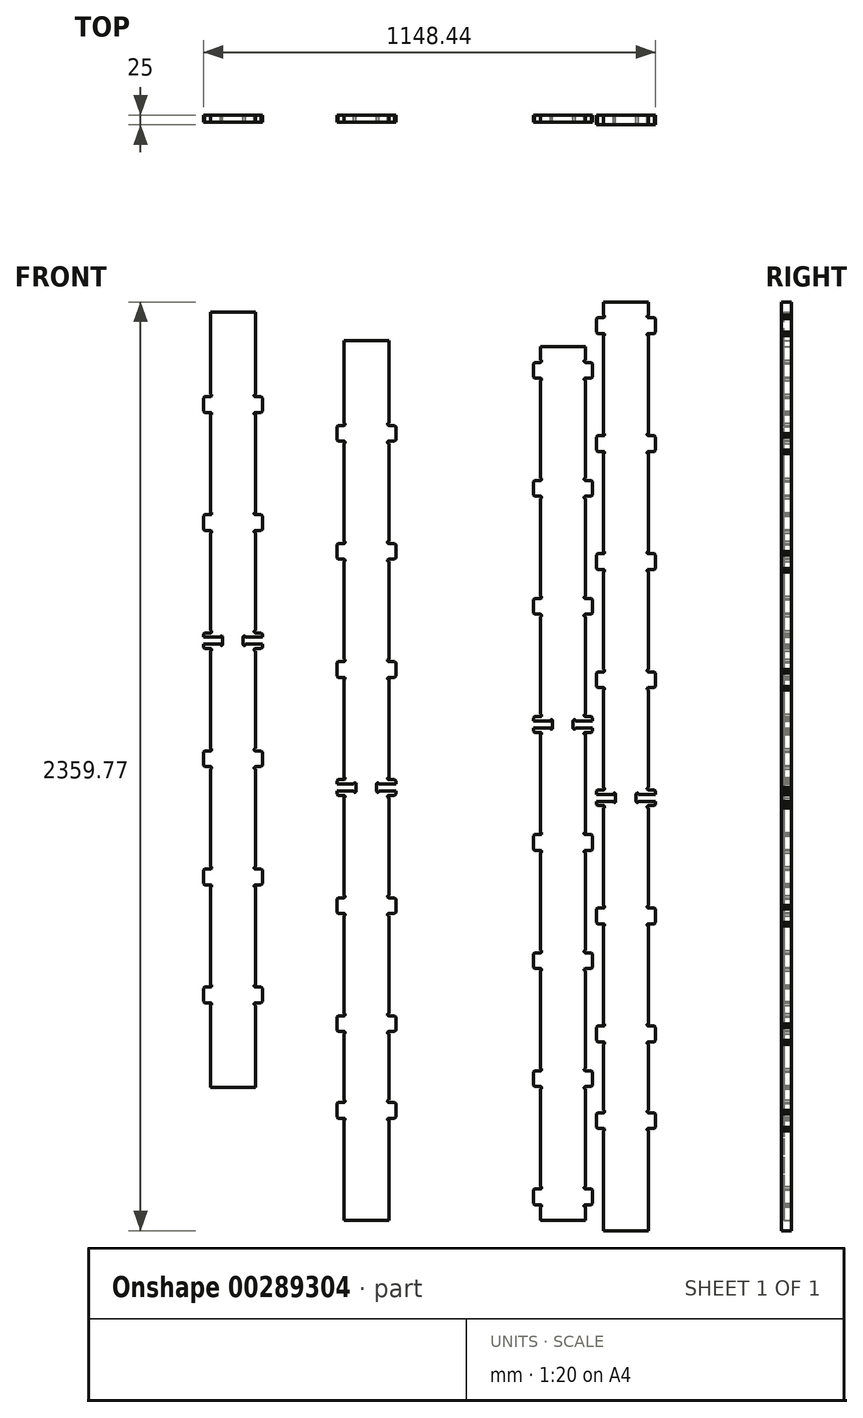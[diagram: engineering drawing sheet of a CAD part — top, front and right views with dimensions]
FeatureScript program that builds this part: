
annotation { "Feature Type Name" : "Feature", "Feature Type Description" : "" }
export const myFeature = defineFeature(function(context is Context, id is Id, definition is map)
    precondition{}
    {
        {
            var Q0;
            Q0=qCreatedBy(makeId("Front.planeOp"),FACE);
            var sketch = newSketch(context, id + "F0", { "sketchPlane" : qUnion([Q0])});
            skLineSegment(sketch, "E0", {"start": v(-600, -1200) * mm, "end": v(600, -1200) * mm});
            skLineSegment(sketch, "E1", {"start": v(600, -1200) * mm, "end": v(600, 1200) * mm});
            skLineSegment(sketch, "E2", {"start": v(600, 1200) * mm, "end": v(-600, 1200) * mm});
            skLineSegment(sketch, "E3", {"start": v(-600, 1200) * mm, "end": v(-600, -1200) * mm});
            skLineSegment(sketch, "E4", {"start": v(-87.48, 570.87) * mm, "end": v(-102.48, 570.87) * mm});
            skArc(sketch, "E5", {"start": v(-102.48, 570.87) * mm, "mid": v(-105.5, 573.88) * mm, "end": v(-102.48, 576.89) * mm});
            skLineSegment(sketch, "E6", {"start": v(-102.48, 576.89) * mm, "end": v(-102.48, 824.85) * mm});
            skArc(sketch, "E7", {"start": v(-102.48, 824.85) * mm, "mid": v(-105.5, 827.86) * mm, "end": v(-102.48, 830.87) * mm});
            skLineSegment(sketch, "E8", {"start": v(-102.48, 830.87) * mm, "end": v(-87.48, 830.87) * mm});
            skLineSegment(sketch, "E9", {"start": v(-87.48, 830.87) * mm, "end": v(-84.48, 833.87) * mm});
            skLineSegment(sketch, "E10", {"start": v(-84.48, 833.87) * mm, "end": v(-84.48, 867.87) * mm});
            skLineSegment(sketch, "E11", {"start": v(-84.48, 867.87) * mm, "end": v(-87.48, 870.87) * mm});
            skLineSegment(sketch, "E12", {"start": v(-87.48, 870.87) * mm, "end": v(-102.48, 870.87) * mm});
            skArc(sketch, "E13", {"start": v(-102.48, 870.87) * mm, "mid": v(-105.5, 873.88) * mm, "end": v(-102.48, 876.89) * mm});
            skLineSegment(sketch, "E14", {"start": v(-102.48, 876.89) * mm, "end": v(-102.48, 1085.87) * mm});
            skLineSegment(sketch, "E15", {"start": v(-102.48, 1085.87) * mm, "end": v(-216.48, 1085.87) * mm});
            skLineSegment(sketch, "E16", {"start": v(-216.48, 1085.87) * mm, "end": v(-216.48, 876.89) * mm});
            skArc(sketch, "E17", {"start": v(-216.48, 876.89) * mm, "mid": v(-213.47, 873.88) * mm, "end": v(-216.48, 870.87) * mm});
            skLineSegment(sketch, "E18", {"start": v(-216.48, 870.87) * mm, "end": v(-231.48, 870.87) * mm});
            skLineSegment(sketch, "E19", {"start": v(-231.48, 870.87) * mm, "end": v(-234.48, 867.87) * mm});
            skLineSegment(sketch, "E20", {"start": v(-234.48, 867.87) * mm, "end": v(-234.48, 833.87) * mm});
            skLineSegment(sketch, "E21", {"start": v(-234.48, 833.87) * mm, "end": v(-231.48, 830.87) * mm});
            skLineSegment(sketch, "E22", {"start": v(-231.48, 830.87) * mm, "end": v(-216.48, 830.87) * mm});
            skArc(sketch, "E23", {"start": v(-216.48, 830.87) * mm, "mid": v(-213.47, 827.86) * mm, "end": v(-216.48, 824.85) * mm});
            skLineSegment(sketch, "E24", {"start": v(-216.48, 824.85) * mm, "end": v(-216.48, 576.89) * mm});
            skArc(sketch, "E25", {"start": v(-216.48, 576.89) * mm, "mid": v(-213.47, 573.88) * mm, "end": v(-216.48, 570.87) * mm});
            skLineSegment(sketch, "E26", {"start": v(-216.48, 570.87) * mm, "end": v(-231.48, 570.87) * mm});
            skLineSegment(sketch, "E27", {"start": v(-231.48, 570.87) * mm, "end": v(-234.48, 567.87) * mm});
            skLineSegment(sketch, "E28", {"start": v(-234.48, 567.87) * mm, "end": v(-234.48, 533.87) * mm});
            skLineSegment(sketch, "E29", {"start": v(-234.48, 533.87) * mm, "end": v(-231.48, 530.87) * mm});
            skLineSegment(sketch, "E30", {"start": v(-231.48, 530.87) * mm, "end": v(-216.48, 530.87) * mm});
            skArc(sketch, "E31", {"start": v(-216.48, 530.87) * mm, "mid": v(-213.47, 527.86) * mm, "end": v(-216.48, 524.85) * mm});
            skLineSegment(sketch, "E32", {"start": v(-216.48, 524.85) * mm, "end": v(-216.48, 276.89) * mm});
            skArc(sketch, "E33", {"start": v(-216.48, 276.89) * mm, "mid": v(-213.47, 273.88) * mm, "end": v(-216.48, 270.87) * mm});
            skLineSegment(sketch, "E34", {"start": v(-216.48, 270.87) * mm, "end": v(-231.48, 270.87) * mm});
            skLineSegment(sketch, "E35", {"start": v(-231.48, 270.87) * mm, "end": v(-234.48, 267.87) * mm});
            skLineSegment(sketch, "E36", {"start": v(-234.48, 267.87) * mm, "end": v(-234.48, 233.87) * mm});
            skLineSegment(sketch, "E37", {"start": v(-234.48, 233.87) * mm, "end": v(-231.48, 230.87) * mm});
            skLineSegment(sketch, "E38", {"start": v(-231.48, 230.87) * mm, "end": v(-216.48, 230.87) * mm});
            skArc(sketch, "E39", {"start": v(-216.48, 230.87) * mm, "mid": v(-213.47, 227.86) * mm, "end": v(-216.48, 224.85) * mm});
            skLineSegment(sketch, "E40", {"start": v(-216.48, 224.85) * mm, "end": v(-216.48, -23.12) * mm});
            skArc(sketch, "E41", {"start": v(-216.48, -23.12) * mm, "mid": v(-213.47, -26.13) * mm, "end": v(-216.48, -29.14) * mm});
            skLineSegment(sketch, "E42", {"start": v(-216.48, -29.14) * mm, "end": v(-231.48, -29.14) * mm});
            skLineSegment(sketch, "E43", {"start": v(-231.48, -29.14) * mm, "end": v(-234.48, -32.14) * mm});
            skLineSegment(sketch, "E44", {"start": v(-234.48, -32.14) * mm, "end": v(-234.48, -40.14) * mm});
            skLineSegment(sketch, "E45", {"start": v(-234.48, -40.14) * mm, "end": v(-191.5, -40.14) * mm});
            skArc(sketch, "E46", {"start": v(-191.5, -40.14) * mm, "mid": v(-188.5, -37.13) * mm, "end": v(-185.48, -40.14) * mm});
            skLineSegment(sketch, "E47", {"start": v(-185.48, -40.14) * mm, "end": v(-185.48, -58.14) * mm});
            skArc(sketch, "E48", {"start": v(-185.48, -58.14) * mm, "mid": v(-188.5, -61.15) * mm, "end": v(-191.5, -58.14) * mm});
            skLineSegment(sketch, "E49", {"start": v(-191.5, -58.14) * mm, "end": v(-234.48, -58.14) * mm});
            skLineSegment(sketch, "E50", {"start": v(-234.48, -58.14) * mm, "end": v(-234.48, -66.14) * mm});
            skLineSegment(sketch, "E51", {"start": v(-234.48, -66.14) * mm, "end": v(-231.48, -69.14) * mm});
            skLineSegment(sketch, "E52", {"start": v(-231.48, -69.14) * mm, "end": v(-216.48, -69.14) * mm});
            skArc(sketch, "E53", {"start": v(-216.48, -69.14) * mm, "mid": v(-213.47, -72.15) * mm, "end": v(-216.48, -75.16) * mm});
            skLineSegment(sketch, "E54", {"start": v(-216.48, -75.16) * mm, "end": v(-216.48, -323.11) * mm});
            skArc(sketch, "E55", {"start": v(-216.48, -323.11) * mm, "mid": v(-213.47, -326.12) * mm, "end": v(-216.48, -329.13) * mm});
            skLineSegment(sketch, "E56", {"start": v(-216.48, -329.13) * mm, "end": v(-231.48, -329.13) * mm});
            skLineSegment(sketch, "E57", {"start": v(-231.48, -329.13) * mm, "end": v(-234.48, -332.13) * mm});
            skLineSegment(sketch, "E58", {"start": v(-234.48, -332.13) * mm, "end": v(-234.48, -366.13) * mm});
            skLineSegment(sketch, "E59", {"start": v(-234.48, -366.13) * mm, "end": v(-231.48, -369.13) * mm});
            skLineSegment(sketch, "E60", {"start": v(-231.48, -369.13) * mm, "end": v(-216.48, -369.13) * mm});
            skArc(sketch, "E61", {"start": v(-216.48, -369.13) * mm, "mid": v(-213.47, -372.14) * mm, "end": v(-216.48, -375.15) * mm});
            skLineSegment(sketch, "E62", {"start": v(-216.48, -375.15) * mm, "end": v(-216.48, -623.11) * mm});
            skArc(sketch, "E63", {"start": v(-216.48, -623.11) * mm, "mid": v(-213.47, -626.12) * mm, "end": v(-216.48, -629.13) * mm});
            skLineSegment(sketch, "E64", {"start": v(-216.48, -629.13) * mm, "end": v(-231.48, -629.13) * mm});
            skLineSegment(sketch, "E65", {"start": v(-231.48, -629.13) * mm, "end": v(-234.48, -632.13) * mm});
            skLineSegment(sketch, "E66", {"start": v(-234.48, -632.13) * mm, "end": v(-234.48, -666.13) * mm});
            skLineSegment(sketch, "E67", {"start": v(-234.48, -666.13) * mm, "end": v(-231.48, -669.13) * mm});
            skLineSegment(sketch, "E68", {"start": v(-231.48, -669.13) * mm, "end": v(-216.48, -669.13) * mm});
            skArc(sketch, "E69", {"start": v(-216.48, -669.13) * mm, "mid": v(-213.47, -672.14) * mm, "end": v(-216.48, -675.15) * mm});
            skLineSegment(sketch, "E70", {"start": v(-216.48, -675.15) * mm, "end": v(-216.48, -843.11) * mm});
            skArc(sketch, "E71", {"start": v(-216.48, -843.11) * mm, "mid": v(-213.47, -846.12) * mm, "end": v(-216.48, -849.13) * mm});
            skLineSegment(sketch, "E72", {"start": v(-216.48, -849.13) * mm, "end": v(-231.48, -849.13) * mm});
            skLineSegment(sketch, "E73", {"start": v(-231.48, -849.13) * mm, "end": v(-234.48, -852.13) * mm});
            skLineSegment(sketch, "E74", {"start": v(-234.48, -852.13) * mm, "end": v(-234.48, -886.13) * mm});
            skLineSegment(sketch, "E75", {"start": v(-234.48, -886.13) * mm, "end": v(-231.48, -889.13) * mm});
            skLineSegment(sketch, "E76", {"start": v(-231.48, -889.13) * mm, "end": v(-216.48, -889.13) * mm});
            skArc(sketch, "E77", {"start": v(-216.48, -889.13) * mm, "mid": v(-213.47, -892.14) * mm, "end": v(-216.48, -895.15) * mm});
            skLineSegment(sketch, "E78", {"start": v(-216.48, -895.15) * mm, "end": v(-216.48, -1148.9) * mm});
            skLineSegment(sketch, "E79", {"start": v(-216.48, -1148.9) * mm, "end": v(-102.48, -1148.9) * mm});
            skLineSegment(sketch, "E80", {"start": v(-102.48, -1148.9) * mm, "end": v(-102.48, -895.15) * mm});
            skArc(sketch, "E81", {"start": v(-102.48, -895.15) * mm, "mid": v(-105.5, -892.14) * mm, "end": v(-102.48, -889.13) * mm});
            skLineSegment(sketch, "E82", {"start": v(-102.48, -889.13) * mm, "end": v(-87.48, -889.13) * mm});
            skLineSegment(sketch, "E83", {"start": v(-87.48, -889.13) * mm, "end": v(-84.48, -886.13) * mm});
            skLineSegment(sketch, "E84", {"start": v(-84.48, -886.13) * mm, "end": v(-84.48, -852.13) * mm});
            skLineSegment(sketch, "E85", {"start": v(-84.48, -852.13) * mm, "end": v(-87.48, -849.13) * mm});
            skLineSegment(sketch, "E86", {"start": v(-87.48, -849.13) * mm, "end": v(-102.48, -849.13) * mm});
            skArc(sketch, "E87", {"start": v(-102.48, -849.13) * mm, "mid": v(-105.5, -846.12) * mm, "end": v(-102.48, -843.11) * mm});
            skLineSegment(sketch, "E88", {"start": v(-102.48, -843.11) * mm, "end": v(-102.48, -675.15) * mm});
            skArc(sketch, "E89", {"start": v(-102.48, -675.15) * mm, "mid": v(-105.5, -672.14) * mm, "end": v(-102.48, -669.13) * mm});
            skLineSegment(sketch, "E90", {"start": v(-102.48, -669.13) * mm, "end": v(-87.48, -669.13) * mm});
            skLineSegment(sketch, "E91", {"start": v(-87.48, -669.13) * mm, "end": v(-84.48, -666.13) * mm});
            skLineSegment(sketch, "E92", {"start": v(-84.48, -666.13) * mm, "end": v(-84.48, -632.13) * mm});
            skLineSegment(sketch, "E93", {"start": v(-84.48, -632.13) * mm, "end": v(-87.48, -629.13) * mm});
            skLineSegment(sketch, "E94", {"start": v(-87.48, -629.13) * mm, "end": v(-102.48, -629.13) * mm});
            skArc(sketch, "E95", {"start": v(-102.48, -629.13) * mm, "mid": v(-105.5, -626.12) * mm, "end": v(-102.48, -623.11) * mm});
            skLineSegment(sketch, "E96", {"start": v(-102.48, -623.11) * mm, "end": v(-102.48, -375.15) * mm});
            skArc(sketch, "E97", {"start": v(-102.48, -375.15) * mm, "mid": v(-105.5, -372.14) * mm, "end": v(-102.48, -369.13) * mm});
            skLineSegment(sketch, "E98", {"start": v(-102.48, -369.13) * mm, "end": v(-87.48, -369.13) * mm});
            skLineSegment(sketch, "E99", {"start": v(-87.48, -369.13) * mm, "end": v(-84.48, -366.13) * mm});
            skLineSegment(sketch, "E100", {"start": v(-84.48, -366.13) * mm, "end": v(-84.48, -332.13) * mm});
            skLineSegment(sketch, "E101", {"start": v(-84.48, -332.13) * mm, "end": v(-87.48, -329.13) * mm});
            skLineSegment(sketch, "E102", {"start": v(-87.48, -329.13) * mm, "end": v(-102.48, -329.13) * mm});
            skArc(sketch, "E103", {"start": v(-102.48, -329.13) * mm, "mid": v(-105.5, -326.12) * mm, "end": v(-102.48, -323.11) * mm});
            skLineSegment(sketch, "E104", {"start": v(-102.48, -323.11) * mm, "end": v(-102.48, -75.16) * mm});
            skArc(sketch, "E105", {"start": v(-102.48, -75.16) * mm, "mid": v(-105.5, -72.15) * mm, "end": v(-102.48, -69.14) * mm});
            skLineSegment(sketch, "E106", {"start": v(-102.48, -69.14) * mm, "end": v(-87.48, -69.14) * mm});
            skLineSegment(sketch, "E107", {"start": v(-87.48, -69.14) * mm, "end": v(-84.48, -66.14) * mm});
            skLineSegment(sketch, "E108", {"start": v(-84.48, -66.14) * mm, "end": v(-84.48, -58.14) * mm});
            skLineSegment(sketch, "E109", {"start": v(-84.48, -58.14) * mm, "end": v(-127.46, -58.14) * mm});
            skArc(sketch, "E110", {"start": v(-127.46, -58.14) * mm, "mid": v(-130.47, -61.15) * mm, "end": v(-133.48, -58.14) * mm});
            skLineSegment(sketch, "E111", {"start": v(-133.48, -58.14) * mm, "end": v(-133.48, -40.14) * mm});
            skArc(sketch, "E112", {"start": v(-133.48, -40.14) * mm, "mid": v(-130.47, -37.13) * mm, "end": v(-127.46, -40.14) * mm});
            skLineSegment(sketch, "E113", {"start": v(-127.46, -40.14) * mm, "end": v(-84.48, -40.14) * mm});
            skLineSegment(sketch, "E114", {"start": v(-84.48, -40.14) * mm, "end": v(-84.48, -32.14) * mm});
            skLineSegment(sketch, "E115", {"start": v(-84.48, -32.14) * mm, "end": v(-87.48, -29.14) * mm});
            skLineSegment(sketch, "E116", {"start": v(-87.48, -29.14) * mm, "end": v(-102.48, -29.14) * mm});
            skArc(sketch, "E117", {"start": v(-102.48, -29.14) * mm, "mid": v(-105.5, -26.13) * mm, "end": v(-102.48, -23.12) * mm});
            skLineSegment(sketch, "E118", {"start": v(-102.48, -23.12) * mm, "end": v(-102.48, 224.85) * mm});
            skArc(sketch, "E119", {"start": v(-102.48, 224.85) * mm, "mid": v(-105.5, 227.86) * mm, "end": v(-102.48, 230.87) * mm});
            skLineSegment(sketch, "E120", {"start": v(-102.48, 230.87) * mm, "end": v(-87.48, 230.87) * mm});
            skLineSegment(sketch, "E121", {"start": v(-87.48, 230.87) * mm, "end": v(-84.48, 233.87) * mm});
            skLineSegment(sketch, "E122", {"start": v(-84.48, 233.87) * mm, "end": v(-84.48, 267.87) * mm});
            skLineSegment(sketch, "E123", {"start": v(-84.48, 267.87) * mm, "end": v(-87.48, 270.87) * mm});
            skLineSegment(sketch, "E124", {"start": v(-87.48, 270.87) * mm, "end": v(-102.48, 270.87) * mm});
            skArc(sketch, "E125", {"start": v(-102.48, 270.87) * mm, "mid": v(-105.5, 273.88) * mm, "end": v(-102.48, 276.89) * mm});
            skLineSegment(sketch, "E126", {"start": v(-102.48, 276.89) * mm, "end": v(-102.48, 524.85) * mm});
            skArc(sketch, "E127", {"start": v(-102.48, 524.85) * mm, "mid": v(-105.5, 527.86) * mm, "end": v(-102.48, 530.87) * mm});
            skLineSegment(sketch, "E128", {"start": v(-102.48, 530.87) * mm, "end": v(-87.48, 530.87) * mm});
            skLineSegment(sketch, "E129", {"start": v(-87.48, 530.87) * mm, "end": v(-84.48, 533.87) * mm});
            skLineSegment(sketch, "E130", {"start": v(-84.48, 533.87) * mm, "end": v(-84.48, 567.87) * mm});
            skLineSegment(sketch, "E131", {"start": v(-84.48, 567.87) * mm, "end": v(-87.48, 570.87) * mm});
            skLineSegment(sketch, "E132", {"start": v(74.02, 431.1) * mm, "end": v(59.02, 431.1) * mm});
            skArc(sketch, "E133", {"start": v(59.02, 431.1) * mm, "mid": v(56, 434.1) * mm, "end": v(59.02, 437.12) * mm});
            skLineSegment(sketch, "E134", {"start": v(59.02, 437.12) * mm, "end": v(59.02, 685.08) * mm});
            skArc(sketch, "E135", {"start": v(59.02, 685.08) * mm, "mid": v(56, 688.09) * mm, "end": v(59.02, 691.1) * mm});
            skLineSegment(sketch, "E136", {"start": v(59.02, 691.1) * mm, "end": v(74.02, 691.1) * mm});
            skLineSegment(sketch, "E137", {"start": v(74.02, 691.1) * mm, "end": v(77.02, 694.1) * mm});
            skLineSegment(sketch, "E138", {"start": v(77.02, 694.1) * mm, "end": v(77.02, 728.1) * mm});
            skLineSegment(sketch, "E139", {"start": v(77.02, 728.1) * mm, "end": v(74.02, 731.1) * mm});
            skLineSegment(sketch, "E140", {"start": v(74.02, 731.1) * mm, "end": v(59.02, 731.1) * mm});
            skArc(sketch, "E141", {"start": v(59.02, 731.1) * mm, "mid": v(56, 734.1) * mm, "end": v(59.02, 737.12) * mm});
            skLineSegment(sketch, "E142", {"start": v(59.02, 737.12) * mm, "end": v(59.02, 985.08) * mm});
            skArc(sketch, "E143", {"start": v(59.02, 985.08) * mm, "mid": v(56, 988.09) * mm, "end": v(59.02, 991.1) * mm});
            skLineSegment(sketch, "E144", {"start": v(59.02, 991.1) * mm, "end": v(74.02, 991.1) * mm});
            skLineSegment(sketch, "E145", {"start": v(74.02, 991.1) * mm, "end": v(77.02, 994.1) * mm});
            skLineSegment(sketch, "E146", {"start": v(77.02, 994.1) * mm, "end": v(77.02, 1028.1) * mm});
            skLineSegment(sketch, "E147", {"start": v(77.02, 1028.1) * mm, "end": v(74.02, 1031.1) * mm});
            skLineSegment(sketch, "E148", {"start": v(74.02, 1031.1) * mm, "end": v(59.02, 1031.1) * mm});
            skArc(sketch, "E149", {"start": v(59.02, 1031.1) * mm, "mid": v(56, 1034.1) * mm, "end": v(59.02, 1037.12) * mm});
            skLineSegment(sketch, "E150", {"start": v(59.02, 1037.12) * mm, "end": v(59.02, 1071.1) * mm});
            skLineSegment(sketch, "E151", {"start": v(59.02, 1071.1) * mm, "end": v(-54.98, 1071.1) * mm});
            skLineSegment(sketch, "E152", {"start": v(-54.98, 1071.1) * mm, "end": v(-54.98, 1037.12) * mm});
            skArc(sketch, "E153", {"start": v(-54.98, 1037.12) * mm, "mid": v(-51.97, 1034.1) * mm, "end": v(-54.98, 1031.1) * mm});
            skLineSegment(sketch, "E154", {"start": v(-54.98, 1031.1) * mm, "end": v(-69.98, 1031.1) * mm});
            skLineSegment(sketch, "E155", {"start": v(-69.98, 1031.1) * mm, "end": v(-72.98, 1028.1) * mm});
            skLineSegment(sketch, "E156", {"start": v(-72.98, 1028.1) * mm, "end": v(-72.98, 994.1) * mm});
            skLineSegment(sketch, "E157", {"start": v(-72.98, 994.1) * mm, "end": v(-69.98, 991.1) * mm});
            skLineSegment(sketch, "E158", {"start": v(-69.98, 991.1) * mm, "end": v(-54.98, 991.1) * mm});
            skArc(sketch, "E159", {"start": v(-54.98, 991.1) * mm, "mid": v(-51.97, 988.09) * mm, "end": v(-54.98, 985.08) * mm});
            skLineSegment(sketch, "E160", {"start": v(-54.98, 985.08) * mm, "end": v(-54.98, 737.12) * mm});
            skArc(sketch, "E161", {"start": v(-54.98, 737.12) * mm, "mid": v(-51.97, 734.1) * mm, "end": v(-54.98, 731.1) * mm});
            skLineSegment(sketch, "E162", {"start": v(-54.98, 731.1) * mm, "end": v(-69.98, 731.1) * mm});
            skLineSegment(sketch, "E163", {"start": v(-69.98, 731.1) * mm, "end": v(-72.98, 728.1) * mm});
            skLineSegment(sketch, "E164", {"start": v(-72.98, 728.1) * mm, "end": v(-72.98, 694.1) * mm});
            skLineSegment(sketch, "E165", {"start": v(-72.98, 694.1) * mm, "end": v(-69.98, 691.1) * mm});
            skLineSegment(sketch, "E166", {"start": v(-69.98, 691.1) * mm, "end": v(-54.98, 691.1) * mm});
            skArc(sketch, "E167", {"start": v(-54.98, 691.1) * mm, "mid": v(-51.97, 688.09) * mm, "end": v(-54.98, 685.08) * mm});
            skLineSegment(sketch, "E168", {"start": v(-54.98, 685.08) * mm, "end": v(-54.98, 437.12) * mm});
            skArc(sketch, "E169", {"start": v(-54.98, 437.12) * mm, "mid": v(-51.97, 434.1) * mm, "end": v(-54.98, 431.1) * mm});
            skLineSegment(sketch, "E170", {"start": v(-54.98, 431.1) * mm, "end": v(-69.98, 431.1) * mm});
            skLineSegment(sketch, "E171", {"start": v(-69.98, 431.1) * mm, "end": v(-72.98, 428.1) * mm});
            skLineSegment(sketch, "E172", {"start": v(-72.98, 428.1) * mm, "end": v(-72.98, 394.1) * mm});
            skLineSegment(sketch, "E173", {"start": v(-72.98, 394.1) * mm, "end": v(-69.98, 391.1) * mm});
            skLineSegment(sketch, "E174", {"start": v(-69.98, 391.1) * mm, "end": v(-54.98, 391.1) * mm});
            skArc(sketch, "E175", {"start": v(-54.98, 391.1) * mm, "mid": v(-51.97, 388.09) * mm, "end": v(-54.98, 385.08) * mm});
            skLineSegment(sketch, "E176", {"start": v(-54.98, 385.08) * mm, "end": v(-54.98, 137.12) * mm});
            skArc(sketch, "E177", {"start": v(-54.98, 137.12) * mm, "mid": v(-51.97, 134.1) * mm, "end": v(-54.98, 131.1) * mm});
            skLineSegment(sketch, "E178", {"start": v(-54.98, 131.1) * mm, "end": v(-69.98, 131.1) * mm});
            skLineSegment(sketch, "E179", {"start": v(-69.98, 131.1) * mm, "end": v(-72.98, 128.1) * mm});
            skLineSegment(sketch, "E180", {"start": v(-72.98, 128.1) * mm, "end": v(-72.98, 120.1) * mm});
            skLineSegment(sketch, "E181", {"start": v(-72.98, 120.1) * mm, "end": v(-30, 120.1) * mm});
            skArc(sketch, "E182", {"start": v(-30, 120.1) * mm, "mid": v(-27, 123.11) * mm, "end": v(-23.98, 120.1) * mm});
            skLineSegment(sketch, "E183", {"start": v(-23.98, 120.1) * mm, "end": v(-23.98, 102.1) * mm});
            skArc(sketch, "E184", {"start": v(-23.98, 102.1) * mm, "mid": v(-27, 99.09) * mm, "end": v(-30, 102.1) * mm});
            skLineSegment(sketch, "E185", {"start": v(-30, 102.1) * mm, "end": v(-72.98, 102.1) * mm});
            skLineSegment(sketch, "E186", {"start": v(-72.98, 102.1) * mm, "end": v(-72.98, 94.1) * mm});
            skLineSegment(sketch, "E187", {"start": v(-72.98, 94.1) * mm, "end": v(-69.98, 91.1) * mm});
            skLineSegment(sketch, "E188", {"start": v(-69.98, 91.1) * mm, "end": v(-54.98, 91.1) * mm});
            skArc(sketch, "E189", {"start": v(-54.98, 91.1) * mm, "mid": v(-51.97, 88.09) * mm, "end": v(-54.98, 85.08) * mm});
            skLineSegment(sketch, "E190", {"start": v(-54.98, 85.08) * mm, "end": v(-54.98, -162.88) * mm});
            skArc(sketch, "E191", {"start": v(-54.98, -162.88) * mm, "mid": v(-51.97, -165.9) * mm, "end": v(-54.98, -168.9) * mm});
            skLineSegment(sketch, "E192", {"start": v(-54.98, -168.9) * mm, "end": v(-69.98, -168.9) * mm});
            skLineSegment(sketch, "E193", {"start": v(-69.98, -168.9) * mm, "end": v(-72.98, -171.9) * mm});
            skLineSegment(sketch, "E194", {"start": v(-72.98, -171.9) * mm, "end": v(-72.98, -205.9) * mm});
            skLineSegment(sketch, "E195", {"start": v(-72.98, -205.9) * mm, "end": v(-69.98, -208.9) * mm});
            skLineSegment(sketch, "E196", {"start": v(-69.98, -208.9) * mm, "end": v(-54.98, -208.9) * mm});
            skArc(sketch, "E197", {"start": v(-54.98, -208.9) * mm, "mid": v(-51.97, -211.91) * mm, "end": v(-54.98, -214.92) * mm});
            skLineSegment(sketch, "E198", {"start": v(-54.98, -214.92) * mm, "end": v(-54.98, -462.88) * mm});
            skArc(sketch, "E199", {"start": v(-54.98, -462.88) * mm, "mid": v(-51.97, -465.9) * mm, "end": v(-54.98, -468.9) * mm});
            skLineSegment(sketch, "E200", {"start": v(-54.98, -468.9) * mm, "end": v(-69.98, -468.9) * mm});
            skLineSegment(sketch, "E201", {"start": v(-69.98, -468.9) * mm, "end": v(-72.98, -471.9) * mm});
            skLineSegment(sketch, "E202", {"start": v(-72.98, -471.9) * mm, "end": v(-72.98, -505.9) * mm});
            skLineSegment(sketch, "E203", {"start": v(-72.98, -505.9) * mm, "end": v(-69.98, -508.9) * mm});
            skLineSegment(sketch, "E204", {"start": v(-69.98, -508.9) * mm, "end": v(-54.98, -508.9) * mm});
            skArc(sketch, "E205", {"start": v(-54.98, -508.9) * mm, "mid": v(-51.97, -511.91) * mm, "end": v(-54.98, -514.92) * mm});
            skLineSegment(sketch, "E206", {"start": v(-54.98, -514.92) * mm, "end": v(-54.98, -762.88) * mm});
            skArc(sketch, "E207", {"start": v(-54.98, -762.88) * mm, "mid": v(-51.97, -765.9) * mm, "end": v(-54.98, -768.9) * mm});
            skLineSegment(sketch, "E208", {"start": v(-54.98, -768.9) * mm, "end": v(-69.98, -768.9) * mm});
            skLineSegment(sketch, "E209", {"start": v(-69.98, -768.9) * mm, "end": v(-72.98, -771.9) * mm});
            skLineSegment(sketch, "E210", {"start": v(-72.98, -771.9) * mm, "end": v(-72.98, -805.9) * mm});
            skLineSegment(sketch, "E211", {"start": v(-72.98, -805.9) * mm, "end": v(-69.98, -808.9) * mm});
            skLineSegment(sketch, "E212", {"start": v(-69.98, -808.9) * mm, "end": v(-54.98, -808.9) * mm});
            skArc(sketch, "E213", {"start": v(-54.98, -808.9) * mm, "mid": v(-51.97, -811.91) * mm, "end": v(-54.98, -814.92) * mm});
            skLineSegment(sketch, "E214", {"start": v(-54.98, -814.92) * mm, "end": v(-54.98, -1062.88) * mm});
            skArc(sketch, "E215", {"start": v(-54.98, -1062.88) * mm, "mid": v(-51.97, -1065.9) * mm, "end": v(-54.98, -1068.9) * mm});
            skLineSegment(sketch, "E216", {"start": v(-54.98, -1068.9) * mm, "end": v(-69.98, -1068.9) * mm});
            skLineSegment(sketch, "E217", {"start": v(-69.98, -1068.9) * mm, "end": v(-72.98, -1071.9) * mm});
            skLineSegment(sketch, "E218", {"start": v(-72.98, -1071.9) * mm, "end": v(-72.98, -1105.9) * mm});
            skLineSegment(sketch, "E219", {"start": v(-72.98, -1105.9) * mm, "end": v(-69.98, -1108.9) * mm});
            skLineSegment(sketch, "E220", {"start": v(-69.98, -1108.9) * mm, "end": v(-54.98, -1108.9) * mm});
            skArc(sketch, "E221", {"start": v(-54.98, -1108.9) * mm, "mid": v(-51.97, -1111.91) * mm, "end": v(-54.98, -1114.92) * mm});
            skLineSegment(sketch, "E222", {"start": v(-54.98, -1114.92) * mm, "end": v(-54.98, -1148.9) * mm});
            skLineSegment(sketch, "E223", {"start": v(-54.98, -1148.9) * mm, "end": v(59.02, -1148.9) * mm});
            skLineSegment(sketch, "E224", {"start": v(59.02, -1148.9) * mm, "end": v(59.02, -1114.92) * mm});
            skArc(sketch, "E225", {"start": v(59.02, -1114.92) * mm, "mid": v(56, -1111.91) * mm, "end": v(59.02, -1108.9) * mm});
            skLineSegment(sketch, "E226", {"start": v(59.02, -1108.9) * mm, "end": v(74.02, -1108.9) * mm});
            skLineSegment(sketch, "E227", {"start": v(74.02, -1108.9) * mm, "end": v(77.02, -1105.9) * mm});
            skLineSegment(sketch, "E228", {"start": v(77.02, -1105.9) * mm, "end": v(77.02, -1071.9) * mm});
            skLineSegment(sketch, "E229", {"start": v(77.02, -1071.9) * mm, "end": v(74.02, -1068.9) * mm});
            skLineSegment(sketch, "E230", {"start": v(74.02, -1068.9) * mm, "end": v(59.02, -1068.9) * mm});
            skArc(sketch, "E231", {"start": v(59.02, -1068.9) * mm, "mid": v(56, -1065.9) * mm, "end": v(59.02, -1062.88) * mm});
            skLineSegment(sketch, "E232", {"start": v(59.02, -1062.88) * mm, "end": v(59.02, -814.92) * mm});
            skArc(sketch, "E233", {"start": v(59.02, -814.92) * mm, "mid": v(56, -811.91) * mm, "end": v(59.02, -808.9) * mm});
            skLineSegment(sketch, "E234", {"start": v(59.02, -808.9) * mm, "end": v(74.02, -808.9) * mm});
            skLineSegment(sketch, "E235", {"start": v(74.02, -808.9) * mm, "end": v(77.02, -805.9) * mm});
            skLineSegment(sketch, "E236", {"start": v(77.02, -805.9) * mm, "end": v(77.02, -771.9) * mm});
            skLineSegment(sketch, "E237", {"start": v(77.02, -771.9) * mm, "end": v(74.02, -768.9) * mm});
            skLineSegment(sketch, "E238", {"start": v(74.02, -768.9) * mm, "end": v(59.02, -768.9) * mm});
            skArc(sketch, "E239", {"start": v(59.02, -768.9) * mm, "mid": v(56, -765.9) * mm, "end": v(59.02, -762.88) * mm});
            skLineSegment(sketch, "E240", {"start": v(59.02, -762.88) * mm, "end": v(59.02, -514.92) * mm});
            skArc(sketch, "E241", {"start": v(59.02, -514.92) * mm, "mid": v(56, -511.91) * mm, "end": v(59.02, -508.9) * mm});
            skLineSegment(sketch, "E242", {"start": v(59.02, -508.9) * mm, "end": v(74.02, -508.9) * mm});
            skLineSegment(sketch, "E243", {"start": v(74.02, -508.9) * mm, "end": v(77.02, -505.9) * mm});
            skLineSegment(sketch, "E244", {"start": v(77.02, -505.9) * mm, "end": v(77.02, -471.9) * mm});
            skLineSegment(sketch, "E245", {"start": v(77.02, -471.9) * mm, "end": v(74.02, -468.9) * mm});
            skLineSegment(sketch, "E246", {"start": v(74.02, -468.9) * mm, "end": v(59.02, -468.9) * mm});
            skArc(sketch, "E247", {"start": v(59.02, -468.9) * mm, "mid": v(56, -465.9) * mm, "end": v(59.02, -462.88) * mm});
            skLineSegment(sketch, "E248", {"start": v(59.02, -462.88) * mm, "end": v(59.02, -214.92) * mm});
            skArc(sketch, "E249", {"start": v(59.02, -214.92) * mm, "mid": v(56, -211.91) * mm, "end": v(59.02, -208.9) * mm});
            skLineSegment(sketch, "E250", {"start": v(59.02, -208.9) * mm, "end": v(74.02, -208.9) * mm});
            skLineSegment(sketch, "E251", {"start": v(74.02, -208.9) * mm, "end": v(77.02, -205.9) * mm});
            skLineSegment(sketch, "E252", {"start": v(77.02, -205.9) * mm, "end": v(77.02, -171.9) * mm});
            skLineSegment(sketch, "E253", {"start": v(77.02, -171.9) * mm, "end": v(74.02, -168.9) * mm});
            skLineSegment(sketch, "E254", {"start": v(74.02, -168.9) * mm, "end": v(59.02, -168.9) * mm});
            skArc(sketch, "E255", {"start": v(59.02, -168.9) * mm, "mid": v(56, -165.9) * mm, "end": v(59.02, -162.88) * mm});
            skLineSegment(sketch, "E256", {"start": v(59.02, -162.88) * mm, "end": v(59.02, 85.08) * mm});
            skArc(sketch, "E257", {"start": v(59.02, 85.08) * mm, "mid": v(56, 88.09) * mm, "end": v(59.02, 91.1) * mm});
            skLineSegment(sketch, "E258", {"start": v(59.02, 91.1) * mm, "end": v(74.02, 91.1) * mm});
            skLineSegment(sketch, "E259", {"start": v(74.02, 91.1) * mm, "end": v(77.02, 94.1) * mm});
            skLineSegment(sketch, "E260", {"start": v(77.02, 94.1) * mm, "end": v(77.02, 102.1) * mm});
            skLineSegment(sketch, "E261", {"start": v(77.02, 102.1) * mm, "end": v(34.04, 102.1) * mm});
            skArc(sketch, "E262", {"start": v(34.04, 102.1) * mm, "mid": v(31.03, 99.1) * mm, "end": v(28.02, 102.1) * mm});
            skLineSegment(sketch, "E263", {"start": v(28.02, 102.1) * mm, "end": v(28.02, 120.1) * mm});
            skArc(sketch, "E264", {"start": v(28.02, 120.1) * mm, "mid": v(31.03, 123.11) * mm, "end": v(34.04, 120.1) * mm});
            skLineSegment(sketch, "E265", {"start": v(34.04, 120.1) * mm, "end": v(77.02, 120.1) * mm});
            skLineSegment(sketch, "E266", {"start": v(77.02, 120.1) * mm, "end": v(77.02, 128.1) * mm});
            skLineSegment(sketch, "E267", {"start": v(77.02, 128.1) * mm, "end": v(74.02, 131.1) * mm});
            skLineSegment(sketch, "E268", {"start": v(74.02, 131.1) * mm, "end": v(59.02, 131.1) * mm});
            skArc(sketch, "E269", {"start": v(59.02, 131.1) * mm, "mid": v(56, 134.1) * mm, "end": v(59.02, 137.12) * mm});
            skLineSegment(sketch, "E270", {"start": v(59.02, 137.12) * mm, "end": v(59.02, 385.08) * mm});
            skArc(sketch, "E271", {"start": v(59.02, 385.08) * mm, "mid": v(56, 388.09) * mm, "end": v(59.02, 391.1) * mm});
            skLineSegment(sketch, "E272", {"start": v(59.02, 391.1) * mm, "end": v(74.02, 391.1) * mm});
            skLineSegment(sketch, "E273", {"start": v(74.02, 391.1) * mm, "end": v(77.02, 394.1) * mm});
            skLineSegment(sketch, "E274", {"start": v(77.02, 394.1) * mm, "end": v(77.02, 428.1) * mm});
            skLineSegment(sketch, "E275", {"start": v(77.02, 428.1) * mm, "end": v(74.02, 431.1) * mm});
            skLineSegment(sketch, "E276", {"start": v(247.4, 570.87) * mm, "end": v(232.4, 570.87) * mm});
            skArc(sketch, "E277", {"start": v(232.4, 570.87) * mm, "mid": v(229.4, 573.88) * mm, "end": v(232.4, 576.89) * mm});
            skLineSegment(sketch, "E278", {"start": v(232.4, 576.89) * mm, "end": v(232.4, 824.85) * mm});
            skArc(sketch, "E279", {"start": v(232.4, 824.85) * mm, "mid": v(229.4, 827.86) * mm, "end": v(232.4, 830.87) * mm});
            skLineSegment(sketch, "E280", {"start": v(232.4, 830.87) * mm, "end": v(247.4, 830.87) * mm});
            skLineSegment(sketch, "E281", {"start": v(247.4, 830.87) * mm, "end": v(250.4, 833.87) * mm});
            skLineSegment(sketch, "E282", {"start": v(250.4, 833.87) * mm, "end": v(250.4, 867.87) * mm});
            skLineSegment(sketch, "E283", {"start": v(250.4, 867.87) * mm, "end": v(247.4, 870.87) * mm});
            skLineSegment(sketch, "E284", {"start": v(247.4, 870.87) * mm, "end": v(232.4, 870.87) * mm});
            skArc(sketch, "E285", {"start": v(232.4, 870.87) * mm, "mid": v(229.4, 873.88) * mm, "end": v(232.4, 876.89) * mm});
            skLineSegment(sketch, "E286", {"start": v(232.4, 876.89) * mm, "end": v(232.4, 1085.87) * mm});
            skLineSegment(sketch, "E287", {"start": v(232.4, 1085.87) * mm, "end": v(118.4, 1085.87) * mm});
            skLineSegment(sketch, "E288", {"start": v(118.4, 1085.87) * mm, "end": v(118.4, 876.89) * mm});
            skArc(sketch, "E289", {"start": v(118.4, 876.89) * mm, "mid": v(121.41, 873.88) * mm, "end": v(118.4, 870.87) * mm});
            skLineSegment(sketch, "E290", {"start": v(118.4, 870.87) * mm, "end": v(103.4, 870.87) * mm});
            skLineSegment(sketch, "E291", {"start": v(103.4, 870.87) * mm, "end": v(100.4, 867.87) * mm});
            skLineSegment(sketch, "E292", {"start": v(100.4, 867.87) * mm, "end": v(100.4, 833.87) * mm});
            skLineSegment(sketch, "E293", {"start": v(100.4, 833.87) * mm, "end": v(103.4, 830.87) * mm});
            skLineSegment(sketch, "E294", {"start": v(103.4, 830.87) * mm, "end": v(118.4, 830.87) * mm});
            skArc(sketch, "E295", {"start": v(118.4, 830.87) * mm, "mid": v(121.41, 827.86) * mm, "end": v(118.4, 824.85) * mm});
            skLineSegment(sketch, "E296", {"start": v(118.4, 824.85) * mm, "end": v(118.4, 576.89) * mm});
            skArc(sketch, "E297", {"start": v(118.4, 576.89) * mm, "mid": v(121.41, 573.88) * mm, "end": v(118.4, 570.87) * mm});
            skLineSegment(sketch, "E298", {"start": v(118.4, 570.87) * mm, "end": v(103.4, 570.87) * mm});
            skLineSegment(sketch, "E299", {"start": v(103.4, 570.87) * mm, "end": v(100.4, 567.87) * mm});
            skLineSegment(sketch, "E300", {"start": v(100.4, 567.87) * mm, "end": v(100.4, 533.87) * mm});
            skLineSegment(sketch, "E301", {"start": v(100.4, 533.87) * mm, "end": v(103.4, 530.87) * mm});
            skLineSegment(sketch, "E302", {"start": v(103.4, 530.87) * mm, "end": v(118.4, 530.87) * mm});
            skArc(sketch, "E303", {"start": v(118.4, 530.87) * mm, "mid": v(121.41, 527.86) * mm, "end": v(118.4, 524.85) * mm});
            skLineSegment(sketch, "E304", {"start": v(118.4, 524.85) * mm, "end": v(118.4, 276.89) * mm});
            skArc(sketch, "E305", {"start": v(118.4, 276.89) * mm, "mid": v(121.41, 273.88) * mm, "end": v(118.4, 270.87) * mm});
            skLineSegment(sketch, "E306", {"start": v(118.4, 270.87) * mm, "end": v(103.4, 270.87) * mm});
            skLineSegment(sketch, "E307", {"start": v(103.4, 270.87) * mm, "end": v(100.4, 267.87) * mm});
            skLineSegment(sketch, "E308", {"start": v(100.4, 267.87) * mm, "end": v(100.4, 233.87) * mm});
            skLineSegment(sketch, "E309", {"start": v(100.4, 233.87) * mm, "end": v(103.4, 230.87) * mm});
            skLineSegment(sketch, "E310", {"start": v(103.4, 230.87) * mm, "end": v(118.4, 230.87) * mm});
            skArc(sketch, "E311", {"start": v(118.4, 230.87) * mm, "mid": v(121.41, 227.86) * mm, "end": v(118.4, 224.85) * mm});
            skLineSegment(sketch, "E312", {"start": v(118.4, 224.85) * mm, "end": v(118.4, -23.12) * mm});
            skArc(sketch, "E313", {"start": v(118.4, -23.12) * mm, "mid": v(121.41, -26.13) * mm, "end": v(118.4, -29.14) * mm});
            skLineSegment(sketch, "E314", {"start": v(118.4, -29.14) * mm, "end": v(103.4, -29.14) * mm});
            skLineSegment(sketch, "E315", {"start": v(103.4, -29.14) * mm, "end": v(100.4, -32.14) * mm});
            skLineSegment(sketch, "E316", {"start": v(100.4, -32.14) * mm, "end": v(100.4, -40.14) * mm});
            skLineSegment(sketch, "E317", {"start": v(100.4, -40.14) * mm, "end": v(143.38, -40.14) * mm});
            skArc(sketch, "E318", {"start": v(143.38, -40.14) * mm, "mid": v(146.39, -37.13) * mm, "end": v(149.4, -40.14) * mm});
            skLineSegment(sketch, "E319", {"start": v(149.4, -40.14) * mm, "end": v(149.4, -58.14) * mm});
            skArc(sketch, "E320", {"start": v(149.4, -58.14) * mm, "mid": v(146.39, -61.15) * mm, "end": v(143.38, -58.14) * mm});
            skLineSegment(sketch, "E321", {"start": v(143.38, -58.14) * mm, "end": v(100.4, -58.14) * mm});
            skLineSegment(sketch, "E322", {"start": v(100.4, -58.14) * mm, "end": v(100.4, -66.14) * mm});
            skLineSegment(sketch, "E323", {"start": v(100.4, -66.14) * mm, "end": v(103.4, -69.14) * mm});
            skLineSegment(sketch, "E324", {"start": v(103.4, -69.14) * mm, "end": v(118.4, -69.14) * mm});
            skArc(sketch, "E325", {"start": v(118.4, -69.14) * mm, "mid": v(121.41, -72.15) * mm, "end": v(118.4, -75.16) * mm});
            skLineSegment(sketch, "E326", {"start": v(118.4, -75.16) * mm, "end": v(118.4, -323.11) * mm});
            skArc(sketch, "E327", {"start": v(118.4, -323.11) * mm, "mid": v(121.41, -326.12) * mm, "end": v(118.4, -329.13) * mm});
            skLineSegment(sketch, "E328", {"start": v(118.4, -329.13) * mm, "end": v(103.4, -329.13) * mm});
            skLineSegment(sketch, "E329", {"start": v(103.4, -329.13) * mm, "end": v(100.4, -332.13) * mm});
            skLineSegment(sketch, "E330", {"start": v(100.4, -332.13) * mm, "end": v(100.4, -366.13) * mm});
            skLineSegment(sketch, "E331", {"start": v(100.4, -366.13) * mm, "end": v(103.4, -369.13) * mm});
            skLineSegment(sketch, "E332", {"start": v(103.4, -369.13) * mm, "end": v(118.4, -369.13) * mm});
            skArc(sketch, "E333", {"start": v(118.4, -369.13) * mm, "mid": v(121.41, -372.14) * mm, "end": v(118.4, -375.15) * mm});
            skLineSegment(sketch, "E334", {"start": v(118.4, -375.15) * mm, "end": v(118.4, -623.11) * mm});
            skArc(sketch, "E335", {"start": v(118.4, -623.11) * mm, "mid": v(121.41, -626.12) * mm, "end": v(118.4, -629.13) * mm});
            skLineSegment(sketch, "E336", {"start": v(118.4, -629.13) * mm, "end": v(103.4, -629.13) * mm});
            skLineSegment(sketch, "E337", {"start": v(103.4, -629.13) * mm, "end": v(100.4, -632.13) * mm});
            skLineSegment(sketch, "E338", {"start": v(100.4, -632.13) * mm, "end": v(100.4, -666.13) * mm});
            skLineSegment(sketch, "E339", {"start": v(100.4, -666.13) * mm, "end": v(103.4, -669.13) * mm});
            skLineSegment(sketch, "E340", {"start": v(103.4, -669.13) * mm, "end": v(118.4, -669.13) * mm});
            skArc(sketch, "E341", {"start": v(118.4, -669.13) * mm, "mid": v(121.41, -672.14) * mm, "end": v(118.4, -675.15) * mm});
            skLineSegment(sketch, "E342", {"start": v(118.4, -675.15) * mm, "end": v(118.4, -843.11) * mm});
            skArc(sketch, "E343", {"start": v(118.4, -843.11) * mm, "mid": v(121.4, -846.12) * mm, "end": v(118.4, -849.13) * mm});
            skLineSegment(sketch, "E344", {"start": v(118.4, -849.13) * mm, "end": v(103.4, -849.13) * mm});
            skLineSegment(sketch, "E345", {"start": v(103.4, -849.13) * mm, "end": v(100.4, -852.13) * mm});
            skLineSegment(sketch, "E346", {"start": v(100.4, -852.13) * mm, "end": v(100.4, -886.13) * mm});
            skLineSegment(sketch, "E347", {"start": v(100.4, -886.13) * mm, "end": v(103.4, -889.13) * mm});
            skLineSegment(sketch, "E348", {"start": v(103.4, -889.13) * mm, "end": v(118.4, -889.13) * mm});
            skArc(sketch, "E349", {"start": v(118.4, -889.13) * mm, "mid": v(121.4, -892.14) * mm, "end": v(118.4, -895.15) * mm});
            skLineSegment(sketch, "E350", {"start": v(118.4, -895.15) * mm, "end": v(118.4, -1148.9) * mm});
            skLineSegment(sketch, "E351", {"start": v(118.4, -1148.9) * mm, "end": v(232.4, -1148.9) * mm});
            skLineSegment(sketch, "E352", {"start": v(232.4, -1148.9) * mm, "end": v(232.4, -895.15) * mm});
            skArc(sketch, "E353", {"start": v(232.4, -895.15) * mm, "mid": v(229.4, -892.14) * mm, "end": v(232.4, -889.13) * mm});
            skLineSegment(sketch, "E354", {"start": v(232.4, -889.13) * mm, "end": v(247.4, -889.13) * mm});
            skLineSegment(sketch, "E355", {"start": v(247.4, -889.13) * mm, "end": v(250.4, -886.13) * mm});
            skLineSegment(sketch, "E356", {"start": v(250.4, -886.13) * mm, "end": v(250.4, -852.13) * mm});
            skLineSegment(sketch, "E357", {"start": v(250.4, -852.13) * mm, "end": v(247.4, -849.13) * mm});
            skLineSegment(sketch, "E358", {"start": v(247.4, -849.13) * mm, "end": v(232.4, -849.13) * mm});
            skArc(sketch, "E359", {"start": v(232.4, -849.13) * mm, "mid": v(229.4, -846.12) * mm, "end": v(232.4, -843.11) * mm});
            skLineSegment(sketch, "E360", {"start": v(232.4, -843.11) * mm, "end": v(232.4, -675.15) * mm});
            skArc(sketch, "E361", {"start": v(232.4, -675.15) * mm, "mid": v(229.4, -672.14) * mm, "end": v(232.4, -669.13) * mm});
            skLineSegment(sketch, "E362", {"start": v(232.4, -669.13) * mm, "end": v(247.4, -669.13) * mm});
            skLineSegment(sketch, "E363", {"start": v(247.4, -669.13) * mm, "end": v(250.4, -666.13) * mm});
            skLineSegment(sketch, "E364", {"start": v(250.4, -666.13) * mm, "end": v(250.4, -632.13) * mm});
            skLineSegment(sketch, "E365", {"start": v(250.4, -632.13) * mm, "end": v(247.4, -629.13) * mm});
            skLineSegment(sketch, "E366", {"start": v(247.4, -629.13) * mm, "end": v(232.4, -629.13) * mm});
            skArc(sketch, "E367", {"start": v(232.4, -629.13) * mm, "mid": v(229.4, -626.12) * mm, "end": v(232.4, -623.11) * mm});
            skLineSegment(sketch, "E368", {"start": v(232.4, -623.11) * mm, "end": v(232.4, -375.15) * mm});
            skArc(sketch, "E369", {"start": v(232.4, -375.15) * mm, "mid": v(229.4, -372.14) * mm, "end": v(232.4, -369.13) * mm});
            skLineSegment(sketch, "E370", {"start": v(232.4, -369.13) * mm, "end": v(247.4, -369.13) * mm});
            skLineSegment(sketch, "E371", {"start": v(247.4, -369.13) * mm, "end": v(250.4, -366.13) * mm});
            skLineSegment(sketch, "E372", {"start": v(250.4, -366.13) * mm, "end": v(250.4, -332.13) * mm});
            skLineSegment(sketch, "E373", {"start": v(250.4, -332.13) * mm, "end": v(247.4, -329.13) * mm});
            skLineSegment(sketch, "E374", {"start": v(247.4, -329.13) * mm, "end": v(232.4, -329.13) * mm});
            skArc(sketch, "E375", {"start": v(232.4, -329.13) * mm, "mid": v(229.4, -326.12) * mm, "end": v(232.4, -323.11) * mm});
            skLineSegment(sketch, "E376", {"start": v(232.4, -323.11) * mm, "end": v(232.4, -75.16) * mm});
            skArc(sketch, "E377", {"start": v(232.4, -75.16) * mm, "mid": v(229.4, -72.15) * mm, "end": v(232.4, -69.14) * mm});
            skLineSegment(sketch, "E378", {"start": v(232.4, -69.14) * mm, "end": v(247.4, -69.14) * mm});
            skLineSegment(sketch, "E379", {"start": v(247.4, -69.14) * mm, "end": v(250.4, -66.14) * mm});
            skLineSegment(sketch, "E380", {"start": v(250.4, -66.14) * mm, "end": v(250.4, -58.14) * mm});
            skLineSegment(sketch, "E381", {"start": v(250.4, -58.14) * mm, "end": v(207.42, -58.14) * mm});
            skArc(sketch, "E382", {"start": v(207.42, -58.14) * mm, "mid": v(204.4, -61.15) * mm, "end": v(201.4, -58.14) * mm});
            skLineSegment(sketch, "E383", {"start": v(201.4, -58.14) * mm, "end": v(201.4, -40.14) * mm});
            skArc(sketch, "E384", {"start": v(201.4, -40.14) * mm, "mid": v(204.4, -37.13) * mm, "end": v(207.42, -40.14) * mm});
            skLineSegment(sketch, "E385", {"start": v(207.42, -40.14) * mm, "end": v(250.4, -40.14) * mm});
            skLineSegment(sketch, "E386", {"start": v(250.4, -40.14) * mm, "end": v(250.4, -32.14) * mm});
            skLineSegment(sketch, "E387", {"start": v(250.4, -32.14) * mm, "end": v(247.4, -29.14) * mm});
            skLineSegment(sketch, "E388", {"start": v(247.4, -29.14) * mm, "end": v(232.4, -29.14) * mm});
            skArc(sketch, "E389", {"start": v(232.4, -29.14) * mm, "mid": v(229.4, -26.13) * mm, "end": v(232.4, -23.12) * mm});
            skLineSegment(sketch, "E390", {"start": v(232.4, -23.12) * mm, "end": v(232.4, 224.85) * mm});
            skArc(sketch, "E391", {"start": v(232.4, 224.85) * mm, "mid": v(229.4, 227.86) * mm, "end": v(232.4, 230.87) * mm});
            skLineSegment(sketch, "E392", {"start": v(232.4, 230.87) * mm, "end": v(247.4, 230.87) * mm});
            skLineSegment(sketch, "E393", {"start": v(247.4, 230.87) * mm, "end": v(250.4, 233.87) * mm});
            skLineSegment(sketch, "E394", {"start": v(250.4, 233.87) * mm, "end": v(250.4, 267.87) * mm});
            skLineSegment(sketch, "E395", {"start": v(250.4, 267.87) * mm, "end": v(247.4, 270.87) * mm});
            skLineSegment(sketch, "E396", {"start": v(247.4, 270.87) * mm, "end": v(232.4, 270.87) * mm});
            skArc(sketch, "E397", {"start": v(232.4, 270.87) * mm, "mid": v(229.4, 273.88) * mm, "end": v(232.4, 276.89) * mm});
            skLineSegment(sketch, "E398", {"start": v(232.4, 276.89) * mm, "end": v(232.4, 524.85) * mm});
            skArc(sketch, "E399", {"start": v(232.4, 524.85) * mm, "mid": v(229.4, 527.86) * mm, "end": v(232.4, 530.87) * mm});
            skLineSegment(sketch, "E400", {"start": v(232.4, 530.87) * mm, "end": v(247.4, 530.87) * mm});
            skLineSegment(sketch, "E401", {"start": v(247.4, 530.87) * mm, "end": v(250.4, 533.87) * mm});
            skLineSegment(sketch, "E402", {"start": v(250.4, 533.87) * mm, "end": v(250.4, 567.87) * mm});
            skLineSegment(sketch, "E403", {"start": v(250.4, 567.87) * mm, "end": v(247.4, 570.87) * mm});
            skLineSegment(sketch, "E404", {"start": v(411.9, 431.1) * mm, "end": v(396.9, 431.1) * mm});
            skArc(sketch, "E405", {"start": v(396.9, 431.1) * mm, "mid": v(393.9, 434.1) * mm, "end": v(396.9, 437.12) * mm});
            skLineSegment(sketch, "E406", {"start": v(396.9, 437.12) * mm, "end": v(396.9, 685.08) * mm});
            skArc(sketch, "E407", {"start": v(396.9, 685.08) * mm, "mid": v(393.9, 688.09) * mm, "end": v(396.9, 691.1) * mm});
            skLineSegment(sketch, "E408", {"start": v(396.9, 691.1) * mm, "end": v(411.9, 691.1) * mm});
            skLineSegment(sketch, "E409", {"start": v(411.9, 691.1) * mm, "end": v(414.9, 694.1) * mm});
            skLineSegment(sketch, "E410", {"start": v(414.9, 694.1) * mm, "end": v(414.9, 728.1) * mm});
            skLineSegment(sketch, "E411", {"start": v(414.9, 728.1) * mm, "end": v(411.9, 731.1) * mm});
            skLineSegment(sketch, "E412", {"start": v(411.9, 731.1) * mm, "end": v(396.9, 731.1) * mm});
            skArc(sketch, "E413", {"start": v(396.9, 731.1) * mm, "mid": v(393.9, 734.1) * mm, "end": v(396.9, 737.12) * mm});
            skLineSegment(sketch, "E414", {"start": v(396.9, 737.12) * mm, "end": v(396.9, 985.08) * mm});
            skArc(sketch, "E415", {"start": v(396.9, 985.08) * mm, "mid": v(393.9, 988.09) * mm, "end": v(396.9, 991.1) * mm});
            skLineSegment(sketch, "E416", {"start": v(396.9, 991.1) * mm, "end": v(411.9, 991.1) * mm});
            skLineSegment(sketch, "E417", {"start": v(411.9, 991.1) * mm, "end": v(414.9, 994.1) * mm});
            skLineSegment(sketch, "E418", {"start": v(414.9, 994.1) * mm, "end": v(414.9, 1028.1) * mm});
            skLineSegment(sketch, "E419", {"start": v(414.9, 1028.1) * mm, "end": v(411.9, 1031.1) * mm});
            skLineSegment(sketch, "E420", {"start": v(411.9, 1031.1) * mm, "end": v(396.9, 1031.1) * mm});
            skArc(sketch, "E421", {"start": v(396.9, 1031.1) * mm, "mid": v(393.9, 1034.1) * mm, "end": v(396.9, 1037.12) * mm});
            skLineSegment(sketch, "E422", {"start": v(396.9, 1037.12) * mm, "end": v(396.9, 1071.1) * mm});
            skLineSegment(sketch, "E423", {"start": v(396.9, 1071.1) * mm, "end": v(282.9, 1071.1) * mm});
            skLineSegment(sketch, "E424", {"start": v(282.9, 1071.1) * mm, "end": v(282.9, 1037.12) * mm});
            skArc(sketch, "E425", {"start": v(282.9, 1037.12) * mm, "mid": v(285.91, 1034.1) * mm, "end": v(282.9, 1031.1) * mm});
            skLineSegment(sketch, "E426", {"start": v(282.9, 1031.1) * mm, "end": v(267.9, 1031.1) * mm});
            skLineSegment(sketch, "E427", {"start": v(267.9, 1031.1) * mm, "end": v(264.9, 1028.1) * mm});
            skLineSegment(sketch, "E428", {"start": v(264.9, 1028.1) * mm, "end": v(264.9, 994.1) * mm});
            skLineSegment(sketch, "E429", {"start": v(264.9, 994.1) * mm, "end": v(267.9, 991.1) * mm});
            skLineSegment(sketch, "E430", {"start": v(267.9, 991.1) * mm, "end": v(282.9, 991.1) * mm});
            skArc(sketch, "E431", {"start": v(282.9, 991.1) * mm, "mid": v(285.91, 988.09) * mm, "end": v(282.9, 985.08) * mm});
            skLineSegment(sketch, "E432", {"start": v(282.9, 985.08) * mm, "end": v(282.9, 737.12) * mm});
            skArc(sketch, "E433", {"start": v(282.9, 737.12) * mm, "mid": v(285.91, 734.1) * mm, "end": v(282.9, 731.1) * mm});
            skLineSegment(sketch, "E434", {"start": v(282.9, 731.1) * mm, "end": v(267.9, 731.1) * mm});
            skLineSegment(sketch, "E435", {"start": v(267.9, 731.1) * mm, "end": v(264.9, 728.1) * mm});
            skLineSegment(sketch, "E436", {"start": v(264.9, 728.1) * mm, "end": v(264.9, 694.1) * mm});
            skLineSegment(sketch, "E437", {"start": v(264.9, 694.1) * mm, "end": v(267.9, 691.1) * mm});
            skLineSegment(sketch, "E438", {"start": v(267.9, 691.1) * mm, "end": v(282.9, 691.1) * mm});
            skArc(sketch, "E439", {"start": v(282.9, 691.1) * mm, "mid": v(285.91, 688.09) * mm, "end": v(282.9, 685.08) * mm});
            skLineSegment(sketch, "E440", {"start": v(282.9, 685.08) * mm, "end": v(282.9, 437.12) * mm});
            skArc(sketch, "E441", {"start": v(282.9, 437.12) * mm, "mid": v(285.91, 434.1) * mm, "end": v(282.9, 431.1) * mm});
            skLineSegment(sketch, "E442", {"start": v(282.9, 431.1) * mm, "end": v(267.9, 431.1) * mm});
            skLineSegment(sketch, "E443", {"start": v(267.9, 431.1) * mm, "end": v(264.9, 428.1) * mm});
            skLineSegment(sketch, "E444", {"start": v(264.9, 428.1) * mm, "end": v(264.9, 394.1) * mm});
            skLineSegment(sketch, "E445", {"start": v(264.9, 394.1) * mm, "end": v(267.9, 391.1) * mm});
            skLineSegment(sketch, "E446", {"start": v(267.9, 391.1) * mm, "end": v(282.9, 391.1) * mm});
            skArc(sketch, "E447", {"start": v(282.9, 391.1) * mm, "mid": v(285.91, 388.09) * mm, "end": v(282.9, 385.08) * mm});
            skLineSegment(sketch, "E448", {"start": v(282.9, 385.08) * mm, "end": v(282.9, 137.12) * mm});
            skArc(sketch, "E449", {"start": v(282.9, 137.12) * mm, "mid": v(285.91, 134.1) * mm, "end": v(282.9, 131.1) * mm});
            skLineSegment(sketch, "E450", {"start": v(282.9, 131.1) * mm, "end": v(267.9, 131.1) * mm});
            skLineSegment(sketch, "E451", {"start": v(267.9, 131.1) * mm, "end": v(264.9, 128.1) * mm});
            skLineSegment(sketch, "E452", {"start": v(264.9, 128.1) * mm, "end": v(264.9, 120.1) * mm});
            skLineSegment(sketch, "E453", {"start": v(264.9, 120.1) * mm, "end": v(307.88, 120.1) * mm});
            skArc(sketch, "E454", {"start": v(307.88, 120.1) * mm, "mid": v(310.89, 123.11) * mm, "end": v(313.9, 120.1) * mm});
            skLineSegment(sketch, "E455", {"start": v(313.9, 120.1) * mm, "end": v(313.9, 102.1) * mm});
            skArc(sketch, "E456", {"start": v(313.9, 102.1) * mm, "mid": v(310.89, 99.09) * mm, "end": v(307.88, 102.1) * mm});
            skLineSegment(sketch, "E457", {"start": v(307.88, 102.1) * mm, "end": v(264.9, 102.1) * mm});
            skLineSegment(sketch, "E458", {"start": v(264.9, 102.1) * mm, "end": v(264.9, 94.1) * mm});
            skLineSegment(sketch, "E459", {"start": v(264.9, 94.1) * mm, "end": v(267.9, 91.1) * mm});
            skLineSegment(sketch, "E460", {"start": v(267.9, 91.1) * mm, "end": v(282.9, 91.1) * mm});
            skArc(sketch, "E461", {"start": v(282.9, 91.1) * mm, "mid": v(285.91, 88.09) * mm, "end": v(282.9, 85.08) * mm});
            skLineSegment(sketch, "E462", {"start": v(282.9, 85.08) * mm, "end": v(282.9, -162.88) * mm});
            skArc(sketch, "E463", {"start": v(282.9, -162.88) * mm, "mid": v(285.91, -165.9) * mm, "end": v(282.9, -168.9) * mm});
            skLineSegment(sketch, "E464", {"start": v(282.9, -168.9) * mm, "end": v(267.9, -168.9) * mm});
            skLineSegment(sketch, "E465", {"start": v(267.9, -168.9) * mm, "end": v(264.9, -171.9) * mm});
            skLineSegment(sketch, "E466", {"start": v(264.9, -171.9) * mm, "end": v(264.9, -205.9) * mm});
            skLineSegment(sketch, "E467", {"start": v(264.9, -205.9) * mm, "end": v(267.9, -208.9) * mm});
            skLineSegment(sketch, "E468", {"start": v(267.9, -208.9) * mm, "end": v(282.9, -208.9) * mm});
            skArc(sketch, "E469", {"start": v(282.9, -208.9) * mm, "mid": v(285.91, -211.91) * mm, "end": v(282.9, -214.92) * mm});
            skLineSegment(sketch, "E470", {"start": v(282.9, -214.92) * mm, "end": v(282.9, -462.88) * mm});
            skArc(sketch, "E471", {"start": v(282.9, -462.88) * mm, "mid": v(285.91, -465.9) * mm, "end": v(282.9, -468.9) * mm});
            skLineSegment(sketch, "E472", {"start": v(282.9, -468.9) * mm, "end": v(267.9, -468.9) * mm});
            skLineSegment(sketch, "E473", {"start": v(267.9, -468.9) * mm, "end": v(264.9, -471.9) * mm});
            skLineSegment(sketch, "E474", {"start": v(264.9, -471.9) * mm, "end": v(264.9, -505.9) * mm});
            skLineSegment(sketch, "E475", {"start": v(264.9, -505.9) * mm, "end": v(267.9, -508.9) * mm});
            skLineSegment(sketch, "E476", {"start": v(267.9, -508.9) * mm, "end": v(282.9, -508.9) * mm});
            skArc(sketch, "E477", {"start": v(282.9, -508.9) * mm, "mid": v(285.91, -511.91) * mm, "end": v(282.9, -514.92) * mm});
            skLineSegment(sketch, "E478", {"start": v(282.9, -514.92) * mm, "end": v(282.9, -762.88) * mm});
            skArc(sketch, "E479", {"start": v(282.9, -762.88) * mm, "mid": v(285.91, -765.9) * mm, "end": v(282.9, -768.9) * mm});
            skLineSegment(sketch, "E480", {"start": v(282.9, -768.9) * mm, "end": v(267.9, -768.9) * mm});
            skLineSegment(sketch, "E481", {"start": v(267.9, -768.9) * mm, "end": v(264.9, -771.9) * mm});
            skLineSegment(sketch, "E482", {"start": v(264.9, -771.9) * mm, "end": v(264.9, -805.9) * mm});
            skLineSegment(sketch, "E483", {"start": v(264.9, -805.9) * mm, "end": v(267.9, -808.9) * mm});
            skLineSegment(sketch, "E484", {"start": v(267.9, -808.9) * mm, "end": v(282.9, -808.9) * mm});
            skArc(sketch, "E485", {"start": v(282.9, -808.9) * mm, "mid": v(285.91, -811.91) * mm, "end": v(282.9, -814.92) * mm});
            skLineSegment(sketch, "E486", {"start": v(282.9, -814.92) * mm, "end": v(282.9, -1062.88) * mm});
            skArc(sketch, "E487", {"start": v(282.9, -1062.88) * mm, "mid": v(285.91, -1065.9) * mm, "end": v(282.9, -1068.9) * mm});
            skLineSegment(sketch, "E488", {"start": v(282.9, -1068.9) * mm, "end": v(267.9, -1068.9) * mm});
            skLineSegment(sketch, "E489", {"start": v(267.9, -1068.9) * mm, "end": v(264.9, -1071.9) * mm});
            skLineSegment(sketch, "E490", {"start": v(264.9, -1071.9) * mm, "end": v(264.9, -1105.9) * mm});
            skLineSegment(sketch, "E491", {"start": v(264.9, -1105.9) * mm, "end": v(267.9, -1108.9) * mm});
            skLineSegment(sketch, "E492", {"start": v(267.9, -1108.9) * mm, "end": v(282.9, -1108.9) * mm});
            skArc(sketch, "E493", {"start": v(282.9, -1108.9) * mm, "mid": v(285.91, -1111.91) * mm, "end": v(282.9, -1114.92) * mm});
            skLineSegment(sketch, "E494", {"start": v(282.9, -1114.92) * mm, "end": v(282.9, -1148.9) * mm});
            skLineSegment(sketch, "E495", {"start": v(282.9, -1148.9) * mm, "end": v(396.9, -1148.9) * mm});
            skLineSegment(sketch, "E496", {"start": v(396.9, -1148.9) * mm, "end": v(396.9, -1114.92) * mm});
            skArc(sketch, "E497", {"start": v(396.9, -1114.92) * mm, "mid": v(393.9, -1111.91) * mm, "end": v(396.9, -1108.9) * mm});
            skLineSegment(sketch, "E498", {"start": v(396.9, -1108.9) * mm, "end": v(411.9, -1108.9) * mm});
            skLineSegment(sketch, "E499", {"start": v(411.9, -1108.9) * mm, "end": v(414.9, -1105.9) * mm});
            skLineSegment(sketch, "E500", {"start": v(414.9, -1105.9) * mm, "end": v(414.9, -1071.9) * mm});
            skLineSegment(sketch, "E501", {"start": v(414.9, -1071.9) * mm, "end": v(411.9, -1068.9) * mm});
            skLineSegment(sketch, "E502", {"start": v(411.9, -1068.9) * mm, "end": v(396.9, -1068.9) * mm});
            skArc(sketch, "E503", {"start": v(396.9, -1068.9) * mm, "mid": v(393.9, -1065.9) * mm, "end": v(396.9, -1062.88) * mm});
            skLineSegment(sketch, "E504", {"start": v(396.9, -1062.88) * mm, "end": v(396.9, -814.92) * mm});
            skArc(sketch, "E505", {"start": v(396.9, -814.92) * mm, "mid": v(393.9, -811.91) * mm, "end": v(396.9, -808.9) * mm});
            skLineSegment(sketch, "E506", {"start": v(396.9, -808.9) * mm, "end": v(411.9, -808.9) * mm});
            skLineSegment(sketch, "E507", {"start": v(411.9, -808.9) * mm, "end": v(414.9, -805.9) * mm});
            skLineSegment(sketch, "E508", {"start": v(414.9, -805.9) * mm, "end": v(414.9, -771.9) * mm});
            skLineSegment(sketch, "E509", {"start": v(414.9, -771.9) * mm, "end": v(411.9, -768.9) * mm});
            skLineSegment(sketch, "E510", {"start": v(411.9, -768.9) * mm, "end": v(396.9, -768.9) * mm});
            skArc(sketch, "E511", {"start": v(396.9, -768.9) * mm, "mid": v(393.9, -765.9) * mm, "end": v(396.9, -762.88) * mm});
            skLineSegment(sketch, "E512", {"start": v(396.9, -762.88) * mm, "end": v(396.9, -514.92) * mm});
            skArc(sketch, "E513", {"start": v(396.9, -514.92) * mm, "mid": v(393.9, -511.91) * mm, "end": v(396.9, -508.9) * mm});
            skLineSegment(sketch, "E514", {"start": v(396.9, -508.9) * mm, "end": v(411.9, -508.9) * mm});
            skLineSegment(sketch, "E515", {"start": v(411.9, -508.9) * mm, "end": v(414.9, -505.9) * mm});
            skLineSegment(sketch, "E516", {"start": v(414.9, -505.9) * mm, "end": v(414.9, -471.9) * mm});
            skLineSegment(sketch, "E517", {"start": v(414.9, -471.9) * mm, "end": v(411.9, -468.9) * mm});
            skLineSegment(sketch, "E518", {"start": v(411.9, -468.9) * mm, "end": v(396.9, -468.9) * mm});
            skArc(sketch, "E519", {"start": v(396.9, -468.9) * mm, "mid": v(393.9, -465.9) * mm, "end": v(396.9, -462.88) * mm});
            skLineSegment(sketch, "E520", {"start": v(396.9, -462.88) * mm, "end": v(396.9, -214.92) * mm});
            skArc(sketch, "E521", {"start": v(396.9, -214.92) * mm, "mid": v(393.9, -211.91) * mm, "end": v(396.9, -208.9) * mm});
            skLineSegment(sketch, "E522", {"start": v(396.9, -208.9) * mm, "end": v(411.9, -208.9) * mm});
            skLineSegment(sketch, "E523", {"start": v(411.9, -208.9) * mm, "end": v(414.9, -205.9) * mm});
            skLineSegment(sketch, "E524", {"start": v(414.9, -205.9) * mm, "end": v(414.9, -171.9) * mm});
            skLineSegment(sketch, "E525", {"start": v(414.9, -171.9) * mm, "end": v(411.9, -168.9) * mm});
            skLineSegment(sketch, "E526", {"start": v(411.9, -168.9) * mm, "end": v(396.9, -168.9) * mm});
            skArc(sketch, "E527", {"start": v(396.9, -168.9) * mm, "mid": v(393.9, -165.9) * mm, "end": v(396.9, -162.88) * mm});
            skLineSegment(sketch, "E528", {"start": v(396.9, -162.88) * mm, "end": v(396.9, 85.08) * mm});
            skArc(sketch, "E529", {"start": v(396.9, 85.08) * mm, "mid": v(393.9, 88.09) * mm, "end": v(396.9, 91.1) * mm});
            skLineSegment(sketch, "E530", {"start": v(396.9, 91.1) * mm, "end": v(411.9, 91.1) * mm});
            skLineSegment(sketch, "E531", {"start": v(411.9, 91.1) * mm, "end": v(414.9, 94.1) * mm});
            skLineSegment(sketch, "E532", {"start": v(414.9, 94.1) * mm, "end": v(414.9, 102.1) * mm});
            skLineSegment(sketch, "E533", {"start": v(414.9, 102.1) * mm, "end": v(371.92, 102.1) * mm});
            skArc(sketch, "E534", {"start": v(371.92, 102.1) * mm, "mid": v(368.9, 99.1) * mm, "end": v(365.9, 102.1) * mm});
            skLineSegment(sketch, "E535", {"start": v(365.9, 102.1) * mm, "end": v(365.9, 120.1) * mm});
            skArc(sketch, "E536", {"start": v(365.9, 120.1) * mm, "mid": v(368.9, 123.11) * mm, "end": v(371.92, 120.1) * mm});
            skLineSegment(sketch, "E537", {"start": v(371.92, 120.1) * mm, "end": v(414.9, 120.1) * mm});
            skLineSegment(sketch, "E538", {"start": v(414.9, 120.1) * mm, "end": v(414.9, 128.1) * mm});
            skLineSegment(sketch, "E539", {"start": v(414.9, 128.1) * mm, "end": v(411.9, 131.1) * mm});
            skLineSegment(sketch, "E540", {"start": v(411.9, 131.1) * mm, "end": v(396.9, 131.1) * mm});
            skArc(sketch, "E541", {"start": v(396.9, 131.1) * mm, "mid": v(393.9, 134.1) * mm, "end": v(396.9, 137.12) * mm});
            skLineSegment(sketch, "E542", {"start": v(396.9, 137.12) * mm, "end": v(396.9, 385.08) * mm});
            skArc(sketch, "E543", {"start": v(396.9, 385.08) * mm, "mid": v(393.9, 388.09) * mm, "end": v(396.9, 391.1) * mm});
            skLineSegment(sketch, "E544", {"start": v(396.9, 391.1) * mm, "end": v(411.9, 391.1) * mm});
            skLineSegment(sketch, "E545", {"start": v(411.9, 391.1) * mm, "end": v(414.9, 394.1) * mm});
            skLineSegment(sketch, "E546", {"start": v(414.9, 394.1) * mm, "end": v(414.9, 428.1) * mm});
            skLineSegment(sketch, "E547", {"start": v(414.9, 428.1) * mm, "end": v(411.9, 431.1) * mm});
            skLineSegment(sketch, "E548", {"start": v(-246.2, 640.87) * mm, "end": v(-249.2, 643.87) * mm});
            skLineSegment(sketch, "E549", {"start": v(-249.2, 643.87) * mm, "end": v(-264.2, 643.87) * mm});
            skArc(sketch, "E550", {"start": v(-264.2, 643.87) * mm, "mid": v(-267.2, 646.88) * mm, "end": v(-264.2, 649.9) * mm});
            skLineSegment(sketch, "E551", {"start": v(-264.2, 649.9) * mm, "end": v(-264.2, 897.85) * mm});
            skArc(sketch, "E552", {"start": v(-264.2, 897.85) * mm, "mid": v(-267.2, 900.86) * mm, "end": v(-264.2, 903.87) * mm});
            skLineSegment(sketch, "E553", {"start": v(-264.2, 903.87) * mm, "end": v(-249.2, 903.87) * mm});
            skLineSegment(sketch, "E554", {"start": v(-249.2, 903.87) * mm, "end": v(-246.2, 906.87) * mm});
            skLineSegment(sketch, "E555", {"start": v(-246.2, 906.87) * mm, "end": v(-246.2, 940.87) * mm});
            skLineSegment(sketch, "E556", {"start": v(-246.2, 940.87) * mm, "end": v(-249.2, 943.87) * mm});
            skLineSegment(sketch, "E557", {"start": v(-249.2, 943.87) * mm, "end": v(-264.2, 943.87) * mm});
            skArc(sketch, "E558", {"start": v(-264.2, 943.87) * mm, "mid": v(-267.2, 946.88) * mm, "end": v(-264.2, 949.9) * mm});
            skLineSegment(sketch, "E559", {"start": v(-264.2, 949.9) * mm, "end": v(-264.2, 1158.87) * mm});
            skLineSegment(sketch, "E560", {"start": v(-264.2, 1158.87) * mm, "end": v(-378.2, 1158.87) * mm});
            skLineSegment(sketch, "E561", {"start": v(-378.2, 1158.87) * mm, "end": v(-378.2, 949.9) * mm});
            skArc(sketch, "E562", {"start": v(-378.2, 949.9) * mm, "mid": v(-375.19, 946.88) * mm, "end": v(-378.2, 943.87) * mm});
            skLineSegment(sketch, "E563", {"start": v(-378.2, 943.87) * mm, "end": v(-393.2, 943.87) * mm});
            skLineSegment(sketch, "E564", {"start": v(-393.2, 943.87) * mm, "end": v(-396.2, 940.87) * mm});
            skLineSegment(sketch, "E565", {"start": v(-396.2, 940.87) * mm, "end": v(-396.2, 906.87) * mm});
            skLineSegment(sketch, "E566", {"start": v(-396.2, 906.87) * mm, "end": v(-393.2, 903.87) * mm});
            skLineSegment(sketch, "E567", {"start": v(-393.2, 903.87) * mm, "end": v(-378.2, 903.87) * mm});
            skArc(sketch, "E568", {"start": v(-378.2, 903.87) * mm, "mid": v(-375.19, 900.86) * mm, "end": v(-378.2, 897.85) * mm});
            skLineSegment(sketch, "E569", {"start": v(-378.2, 897.85) * mm, "end": v(-378.2, 649.9) * mm});
            skArc(sketch, "E570", {"start": v(-378.2, 649.9) * mm, "mid": v(-375.19, 646.88) * mm, "end": v(-378.2, 643.87) * mm});
            skLineSegment(sketch, "E571", {"start": v(-378.2, 643.87) * mm, "end": v(-393.2, 643.87) * mm});
            skLineSegment(sketch, "E572", {"start": v(-393.2, 643.87) * mm, "end": v(-396.2, 640.87) * mm});
            skLineSegment(sketch, "E573", {"start": v(-396.2, 640.87) * mm, "end": v(-396.2, 606.87) * mm});
            skLineSegment(sketch, "E574", {"start": v(-396.2, 606.87) * mm, "end": v(-393.2, 603.87) * mm});
            skLineSegment(sketch, "E575", {"start": v(-393.2, 603.87) * mm, "end": v(-378.2, 603.87) * mm});
            skArc(sketch, "E576", {"start": v(-378.2, 603.87) * mm, "mid": v(-375.19, 600.86) * mm, "end": v(-378.2, 597.85) * mm});
            skLineSegment(sketch, "E577", {"start": v(-378.2, 597.85) * mm, "end": v(-378.2, 349.9) * mm});
            skArc(sketch, "E578", {"start": v(-378.2, 349.9) * mm, "mid": v(-375.19, 346.88) * mm, "end": v(-378.2, 343.87) * mm});
            skLineSegment(sketch, "E579", {"start": v(-378.2, 343.87) * mm, "end": v(-393.2, 343.87) * mm});
            skLineSegment(sketch, "E580", {"start": v(-393.2, 343.87) * mm, "end": v(-396.2, 340.87) * mm});
            skLineSegment(sketch, "E581", {"start": v(-396.2, 340.87) * mm, "end": v(-396.2, 332.87) * mm});
            skLineSegment(sketch, "E582", {"start": v(-396.2, 332.87) * mm, "end": v(-353.22, 332.87) * mm});
            skArc(sketch, "E583", {"start": v(-353.22, 332.87) * mm, "mid": v(-350.21, 335.88) * mm, "end": v(-347.2, 332.87) * mm});
            skLineSegment(sketch, "E584", {"start": v(-347.2, 332.87) * mm, "end": v(-347.2, 314.87) * mm});
            skArc(sketch, "E585", {"start": v(-347.2, 314.87) * mm, "mid": v(-350.21, 311.86) * mm, "end": v(-353.22, 314.87) * mm});
            skLineSegment(sketch, "E586", {"start": v(-353.22, 314.87) * mm, "end": v(-396.2, 314.87) * mm});
            skLineSegment(sketch, "E587", {"start": v(-396.2, 314.87) * mm, "end": v(-396.2, 306.87) * mm});
            skLineSegment(sketch, "E588", {"start": v(-396.2, 306.87) * mm, "end": v(-393.2, 303.87) * mm});
            skLineSegment(sketch, "E589", {"start": v(-393.2, 303.87) * mm, "end": v(-378.2, 303.87) * mm});
            skArc(sketch, "E590", {"start": v(-378.2, 303.87) * mm, "mid": v(-375.19, 300.86) * mm, "end": v(-378.2, 297.85) * mm});
            skLineSegment(sketch, "E591", {"start": v(-378.2, 297.85) * mm, "end": v(-378.2, 49.9) * mm});
            skArc(sketch, "E592", {"start": v(-378.2, 49.9) * mm, "mid": v(-375.19, 46.88) * mm, "end": v(-378.2, 43.87) * mm});
            skLineSegment(sketch, "E593", {"start": v(-378.2, 43.87) * mm, "end": v(-393.2, 43.87) * mm});
            skLineSegment(sketch, "E594", {"start": v(-393.2, 43.87) * mm, "end": v(-396.2, 40.87) * mm});
            skLineSegment(sketch, "E595", {"start": v(-396.2, 40.87) * mm, "end": v(-396.2, 6.87) * mm});
            skLineSegment(sketch, "E596", {"start": v(-396.2, 6.87) * mm, "end": v(-393.2, 3.87) * mm});
            skLineSegment(sketch, "E597", {"start": v(-393.2, 3.87) * mm, "end": v(-378.2, 3.87) * mm});
            skArc(sketch, "E598", {"start": v(-378.2, 3.87) * mm, "mid": v(-375.19, 0.86) * mm, "end": v(-378.2, -2.15) * mm});
            skLineSegment(sketch, "E599", {"start": v(-378.2, -2.15) * mm, "end": v(-378.2, -250.1) * mm});
            skArc(sketch, "E600", {"start": v(-378.2, -250.1) * mm, "mid": v(-375.19, -253.12) * mm, "end": v(-378.2, -256.13) * mm});
            skLineSegment(sketch, "E601", {"start": v(-378.2, -256.13) * mm, "end": v(-393.2, -256.13) * mm});
            skLineSegment(sketch, "E602", {"start": v(-393.2, -256.13) * mm, "end": v(-396.2, -259.13) * mm});
            skLineSegment(sketch, "E603", {"start": v(-396.2, -259.13) * mm, "end": v(-396.2, -293.13) * mm});
            skLineSegment(sketch, "E604", {"start": v(-396.2, -293.13) * mm, "end": v(-393.2, -296.13) * mm});
            skLineSegment(sketch, "E605", {"start": v(-393.2, -296.13) * mm, "end": v(-378.2, -296.13) * mm});
            skArc(sketch, "E606", {"start": v(-378.2, -296.13) * mm, "mid": v(-375.19, -299.14) * mm, "end": v(-378.2, -302.15) * mm});
            skLineSegment(sketch, "E607", {"start": v(-378.2, -302.15) * mm, "end": v(-378.2, -550.1) * mm});
            skArc(sketch, "E608", {"start": v(-378.2, -550.1) * mm, "mid": v(-375.19, -553.12) * mm, "end": v(-378.2, -556.13) * mm});
            skLineSegment(sketch, "E609", {"start": v(-378.2, -556.13) * mm, "end": v(-393.2, -556.13) * mm});
            skLineSegment(sketch, "E610", {"start": v(-393.2, -556.13) * mm, "end": v(-396.2, -559.13) * mm});
            skLineSegment(sketch, "E611", {"start": v(-396.2, -559.13) * mm, "end": v(-396.2, -593.13) * mm});
            skLineSegment(sketch, "E612", {"start": v(-396.2, -593.13) * mm, "end": v(-393.2, -596.13) * mm});
            skLineSegment(sketch, "E613", {"start": v(-393.2, -596.13) * mm, "end": v(-378.2, -596.13) * mm});
            skArc(sketch, "E614", {"start": v(-378.2, -596.13) * mm, "mid": v(-375.19, -599.14) * mm, "end": v(-378.2, -602.15) * mm});
            skLineSegment(sketch, "E615", {"start": v(-378.2, -602.15) * mm, "end": v(-378.2, -811.13) * mm});
            skLineSegment(sketch, "E616", {"start": v(-378.2, -811.13) * mm, "end": v(-264.2, -811.13) * mm});
            skLineSegment(sketch, "E617", {"start": v(-264.2, -811.13) * mm, "end": v(-264.2, -602.15) * mm});
            skArc(sketch, "E618", {"start": v(-264.2, -602.15) * mm, "mid": v(-267.2, -599.14) * mm, "end": v(-264.2, -596.13) * mm});
            skLineSegment(sketch, "E619", {"start": v(-264.2, -596.13) * mm, "end": v(-249.2, -596.13) * mm});
            skLineSegment(sketch, "E620", {"start": v(-249.2, -596.13) * mm, "end": v(-246.2, -593.13) * mm});
            skLineSegment(sketch, "E621", {"start": v(-246.2, -593.13) * mm, "end": v(-246.2, -559.13) * mm});
            skLineSegment(sketch, "E622", {"start": v(-246.2, -559.13) * mm, "end": v(-249.2, -556.13) * mm});
            skLineSegment(sketch, "E623", {"start": v(-249.2, -556.13) * mm, "end": v(-264.2, -556.13) * mm});
            skArc(sketch, "E624", {"start": v(-264.2, -556.13) * mm, "mid": v(-267.2, -553.12) * mm, "end": v(-264.2, -550.1) * mm});
            skLineSegment(sketch, "E625", {"start": v(-264.2, -550.1) * mm, "end": v(-264.2, -302.15) * mm});
            skArc(sketch, "E626", {"start": v(-264.2, -302.15) * mm, "mid": v(-267.2, -299.14) * mm, "end": v(-264.2, -296.13) * mm});
            skLineSegment(sketch, "E627", {"start": v(-264.2, -296.13) * mm, "end": v(-249.2, -296.13) * mm});
            skLineSegment(sketch, "E628", {"start": v(-249.2, -296.13) * mm, "end": v(-246.2, -293.13) * mm});
            skLineSegment(sketch, "E629", {"start": v(-246.2, -293.13) * mm, "end": v(-246.2, -259.13) * mm});
            skLineSegment(sketch, "E630", {"start": v(-246.2, -259.13) * mm, "end": v(-249.2, -256.13) * mm});
            skLineSegment(sketch, "E631", {"start": v(-249.2, -256.13) * mm, "end": v(-264.2, -256.13) * mm});
            skArc(sketch, "E632", {"start": v(-264.2, -256.13) * mm, "mid": v(-267.2, -253.12) * mm, "end": v(-264.2, -250.1) * mm});
            skLineSegment(sketch, "E633", {"start": v(-264.2, -250.1) * mm, "end": v(-264.2, -2.15) * mm});
            skArc(sketch, "E634", {"start": v(-264.2, -2.15) * mm, "mid": v(-267.2, 0.86) * mm, "end": v(-264.2, 3.87) * mm});
            skLineSegment(sketch, "E635", {"start": v(-264.2, 3.87) * mm, "end": v(-249.2, 3.87) * mm});
            skLineSegment(sketch, "E636", {"start": v(-249.2, 3.87) * mm, "end": v(-246.2, 6.87) * mm});
            skLineSegment(sketch, "E637", {"start": v(-246.2, 6.87) * mm, "end": v(-246.2, 40.87) * mm});
            skLineSegment(sketch, "E638", {"start": v(-246.2, 40.87) * mm, "end": v(-249.2, 43.87) * mm});
            skLineSegment(sketch, "E639", {"start": v(-249.2, 43.87) * mm, "end": v(-264.2, 43.87) * mm});
            skArc(sketch, "E640", {"start": v(-264.2, 43.87) * mm, "mid": v(-267.2, 46.88) * mm, "end": v(-264.2, 49.9) * mm});
            skLineSegment(sketch, "E641", {"start": v(-264.2, 49.9) * mm, "end": v(-264.2, 297.85) * mm});
            skArc(sketch, "E642", {"start": v(-264.2, 297.85) * mm, "mid": v(-267.2, 300.86) * mm, "end": v(-264.2, 303.87) * mm});
            skLineSegment(sketch, "E643", {"start": v(-264.2, 303.87) * mm, "end": v(-249.2, 303.87) * mm});
            skLineSegment(sketch, "E644", {"start": v(-249.2, 303.87) * mm, "end": v(-246.2, 306.87) * mm});
            skLineSegment(sketch, "E645", {"start": v(-246.2, 306.87) * mm, "end": v(-246.2, 314.87) * mm});
            skLineSegment(sketch, "E646", {"start": v(-246.2, 314.87) * mm, "end": v(-289.18, 314.87) * mm});
            skArc(sketch, "E647", {"start": v(-289.18, 314.87) * mm, "mid": v(-292.2, 311.86) * mm, "end": v(-295.2, 314.87) * mm});
            skLineSegment(sketch, "E648", {"start": v(-295.2, 314.87) * mm, "end": v(-295.2, 332.87) * mm});
            skArc(sketch, "E649", {"start": v(-295.2, 332.87) * mm, "mid": v(-292.2, 335.88) * mm, "end": v(-289.18, 332.87) * mm});
            skLineSegment(sketch, "E650", {"start": v(-289.18, 332.87) * mm, "end": v(-246.2, 332.87) * mm});
            skLineSegment(sketch, "E651", {"start": v(-246.2, 332.87) * mm, "end": v(-246.2, 340.87) * mm});
            skLineSegment(sketch, "E652", {"start": v(-246.2, 340.87) * mm, "end": v(-249.2, 343.87) * mm});
            skLineSegment(sketch, "E653", {"start": v(-249.2, 343.87) * mm, "end": v(-264.2, 343.87) * mm});
            skArc(sketch, "E654", {"start": v(-264.2, 343.87) * mm, "mid": v(-267.2, 346.88) * mm, "end": v(-264.2, 349.9) * mm});
            skLineSegment(sketch, "E655", {"start": v(-264.2, 349.9) * mm, "end": v(-264.2, 597.85) * mm});
            skArc(sketch, "E656", {"start": v(-264.2, 597.85) * mm, "mid": v(-267.2, 600.86) * mm, "end": v(-264.2, 603.87) * mm});
            skLineSegment(sketch, "E657", {"start": v(-264.2, 603.87) * mm, "end": v(-249.2, 603.87) * mm});
            skLineSegment(sketch, "E658", {"start": v(-249.2, 603.87) * mm, "end": v(-246.2, 606.87) * mm});
            skLineSegment(sketch, "E659", {"start": v(-246.2, 606.87) * mm, "end": v(-246.2, 640.87) * mm});
            skLineSegment(sketch, "E660", {"start": v(-423.44, 640.87) * mm, "end": v(-426.44, 643.87) * mm});
            skLineSegment(sketch, "E661", {"start": v(-426.44, 643.87) * mm, "end": v(-441.44, 643.87) * mm});
            skArc(sketch, "E662", {"start": v(-441.44, 643.87) * mm, "mid": v(-444.45, 646.88) * mm, "end": v(-441.44, 649.9) * mm});
            skLineSegment(sketch, "E663", {"start": v(-441.44, 649.9) * mm, "end": v(-441.44, 897.85) * mm});
            skArc(sketch, "E664", {"start": v(-441.44, 897.85) * mm, "mid": v(-444.45, 900.86) * mm, "end": v(-441.44, 903.87) * mm});
            skLineSegment(sketch, "E665", {"start": v(-441.44, 903.87) * mm, "end": v(-426.44, 903.87) * mm});
            skLineSegment(sketch, "E666", {"start": v(-426.44, 903.87) * mm, "end": v(-423.44, 906.87) * mm});
            skLineSegment(sketch, "E667", {"start": v(-423.44, 906.87) * mm, "end": v(-423.44, 940.87) * mm});
            skLineSegment(sketch, "E668", {"start": v(-423.44, 940.87) * mm, "end": v(-426.44, 943.87) * mm});
            skLineSegment(sketch, "E669", {"start": v(-426.44, 943.87) * mm, "end": v(-441.44, 943.87) * mm});
            skArc(sketch, "E670", {"start": v(-441.44, 943.87) * mm, "mid": v(-444.45, 946.88) * mm, "end": v(-441.44, 949.9) * mm});
            skLineSegment(sketch, "E671", {"start": v(-441.44, 949.9) * mm, "end": v(-441.44, 1158.87) * mm});
            skLineSegment(sketch, "E672", {"start": v(-441.44, 1158.87) * mm, "end": v(-555.44, 1158.87) * mm});
            skLineSegment(sketch, "E673", {"start": v(-555.44, 1158.87) * mm, "end": v(-555.44, 949.9) * mm});
            skArc(sketch, "E674", {"start": v(-555.44, 949.9) * mm, "mid": v(-552.43, 946.88) * mm, "end": v(-555.44, 943.87) * mm});
            skLineSegment(sketch, "E675", {"start": v(-555.44, 943.87) * mm, "end": v(-570.44, 943.87) * mm});
            skLineSegment(sketch, "E676", {"start": v(-570.44, 943.87) * mm, "end": v(-573.44, 940.87) * mm});
            skLineSegment(sketch, "E677", {"start": v(-573.44, 940.87) * mm, "end": v(-573.44, 906.87) * mm});
            skLineSegment(sketch, "E678", {"start": v(-573.44, 906.87) * mm, "end": v(-570.44, 903.87) * mm});
            skLineSegment(sketch, "E679", {"start": v(-570.44, 903.87) * mm, "end": v(-555.44, 903.87) * mm});
            skArc(sketch, "E680", {"start": v(-555.44, 903.87) * mm, "mid": v(-552.43, 900.86) * mm, "end": v(-555.44, 897.85) * mm});
            skLineSegment(sketch, "E681", {"start": v(-555.44, 897.85) * mm, "end": v(-555.44, 649.9) * mm});
            skArc(sketch, "E682", {"start": v(-555.44, 649.9) * mm, "mid": v(-552.43, 646.88) * mm, "end": v(-555.44, 643.87) * mm});
            skLineSegment(sketch, "E683", {"start": v(-555.44, 643.87) * mm, "end": v(-570.44, 643.87) * mm});
            skLineSegment(sketch, "E684", {"start": v(-570.44, 643.87) * mm, "end": v(-573.44, 640.87) * mm});
            skLineSegment(sketch, "E685", {"start": v(-573.44, 640.87) * mm, "end": v(-573.44, 606.87) * mm});
            skLineSegment(sketch, "E686", {"start": v(-573.44, 606.87) * mm, "end": v(-570.44, 603.87) * mm});
            skLineSegment(sketch, "E687", {"start": v(-570.44, 603.87) * mm, "end": v(-555.44, 603.87) * mm});
            skArc(sketch, "E688", {"start": v(-555.44, 603.87) * mm, "mid": v(-552.43, 600.86) * mm, "end": v(-555.44, 597.85) * mm});
            skLineSegment(sketch, "E689", {"start": v(-555.44, 597.85) * mm, "end": v(-555.44, 349.9) * mm});
            skArc(sketch, "E690", {"start": v(-555.44, 349.9) * mm, "mid": v(-552.43, 346.88) * mm, "end": v(-555.44, 343.87) * mm});
            skLineSegment(sketch, "E691", {"start": v(-555.44, 343.87) * mm, "end": v(-570.44, 343.87) * mm});
            skLineSegment(sketch, "E692", {"start": v(-570.44, 343.87) * mm, "end": v(-573.44, 340.87) * mm});
            skLineSegment(sketch, "E693", {"start": v(-573.44, 340.87) * mm, "end": v(-573.44, 332.87) * mm});
            skLineSegment(sketch, "E694", {"start": v(-573.44, 332.87) * mm, "end": v(-530.46, 332.87) * mm});
            skArc(sketch, "E695", {"start": v(-530.46, 332.87) * mm, "mid": v(-527.45, 335.88) * mm, "end": v(-524.44, 332.87) * mm});
            skLineSegment(sketch, "E696", {"start": v(-524.44, 332.87) * mm, "end": v(-524.44, 314.87) * mm});
            skArc(sketch, "E697", {"start": v(-524.44, 314.87) * mm, "mid": v(-527.45, 311.86) * mm, "end": v(-530.46, 314.87) * mm});
            skLineSegment(sketch, "E698", {"start": v(-530.46, 314.87) * mm, "end": v(-573.44, 314.87) * mm});
            skLineSegment(sketch, "E699", {"start": v(-573.44, 314.87) * mm, "end": v(-573.44, 306.87) * mm});
            skLineSegment(sketch, "E700", {"start": v(-573.44, 306.87) * mm, "end": v(-570.44, 303.87) * mm});
            skLineSegment(sketch, "E701", {"start": v(-570.44, 303.87) * mm, "end": v(-555.44, 303.87) * mm});
            skArc(sketch, "E702", {"start": v(-555.44, 303.87) * mm, "mid": v(-552.43, 300.86) * mm, "end": v(-555.44, 297.85) * mm});
            skLineSegment(sketch, "E703", {"start": v(-555.44, 297.85) * mm, "end": v(-555.44, 49.9) * mm});
            skArc(sketch, "E704", {"start": v(-555.44, 49.9) * mm, "mid": v(-552.43, 46.88) * mm, "end": v(-555.44, 43.87) * mm});
            skLineSegment(sketch, "E705", {"start": v(-555.44, 43.87) * mm, "end": v(-570.44, 43.87) * mm});
            skLineSegment(sketch, "E706", {"start": v(-570.44, 43.87) * mm, "end": v(-573.44, 40.87) * mm});
            skLineSegment(sketch, "E707", {"start": v(-573.44, 40.87) * mm, "end": v(-573.44, 6.87) * mm});
            skLineSegment(sketch, "E708", {"start": v(-573.44, 6.87) * mm, "end": v(-570.44, 3.87) * mm});
            skLineSegment(sketch, "E709", {"start": v(-570.44, 3.87) * mm, "end": v(-555.44, 3.87) * mm});
            skArc(sketch, "E710", {"start": v(-555.44, 3.87) * mm, "mid": v(-552.43, 0.86) * mm, "end": v(-555.44, -2.15) * mm});
            skLineSegment(sketch, "E711", {"start": v(-555.44, -2.15) * mm, "end": v(-555.44, -250.1) * mm});
            skArc(sketch, "E712", {"start": v(-555.44, -250.1) * mm, "mid": v(-552.43, -253.12) * mm, "end": v(-555.44, -256.13) * mm});
            skLineSegment(sketch, "E713", {"start": v(-555.44, -256.13) * mm, "end": v(-570.44, -256.13) * mm});
            skLineSegment(sketch, "E714", {"start": v(-570.44, -256.13) * mm, "end": v(-573.44, -259.13) * mm});
            skLineSegment(sketch, "E715", {"start": v(-573.44, -259.13) * mm, "end": v(-573.44, -293.13) * mm});
            skLineSegment(sketch, "E716", {"start": v(-573.44, -293.13) * mm, "end": v(-570.44, -296.13) * mm});
            skLineSegment(sketch, "E717", {"start": v(-570.44, -296.13) * mm, "end": v(-555.44, -296.13) * mm});
            skArc(sketch, "E718", {"start": v(-555.44, -296.13) * mm, "mid": v(-552.43, -299.14) * mm, "end": v(-555.44, -302.15) * mm});
            skLineSegment(sketch, "E719", {"start": v(-555.44, -302.15) * mm, "end": v(-555.44, -550.1) * mm});
            skArc(sketch, "E720", {"start": v(-555.44, -550.1) * mm, "mid": v(-552.43, -553.12) * mm, "end": v(-555.44, -556.13) * mm});
            skLineSegment(sketch, "E721", {"start": v(-555.44, -556.13) * mm, "end": v(-570.44, -556.13) * mm});
            skLineSegment(sketch, "E722", {"start": v(-570.44, -556.13) * mm, "end": v(-573.44, -559.13) * mm});
            skLineSegment(sketch, "E723", {"start": v(-573.44, -559.13) * mm, "end": v(-573.44, -593.13) * mm});
            skLineSegment(sketch, "E724", {"start": v(-573.44, -593.13) * mm, "end": v(-570.44, -596.13) * mm});
            skLineSegment(sketch, "E725", {"start": v(-570.44, -596.13) * mm, "end": v(-555.44, -596.13) * mm});
            skArc(sketch, "E726", {"start": v(-555.44, -596.13) * mm, "mid": v(-552.43, -599.14) * mm, "end": v(-555.44, -602.15) * mm});
            skLineSegment(sketch, "E727", {"start": v(-555.44, -602.15) * mm, "end": v(-555.44, -811.13) * mm});
            skLineSegment(sketch, "E728", {"start": v(-555.44, -811.13) * mm, "end": v(-441.44, -811.13) * mm});
            skLineSegment(sketch, "E729", {"start": v(-441.44, -811.13) * mm, "end": v(-441.44, -602.15) * mm});
            skArc(sketch, "E730", {"start": v(-441.44, -602.15) * mm, "mid": v(-444.45, -599.14) * mm, "end": v(-441.44, -596.13) * mm});
            skLineSegment(sketch, "E731", {"start": v(-441.44, -596.13) * mm, "end": v(-426.44, -596.13) * mm});
            skLineSegment(sketch, "E732", {"start": v(-426.44, -596.13) * mm, "end": v(-423.44, -593.13) * mm});
            skLineSegment(sketch, "E733", {"start": v(-423.44, -593.13) * mm, "end": v(-423.44, -559.13) * mm});
            skLineSegment(sketch, "E734", {"start": v(-423.44, -559.13) * mm, "end": v(-426.44, -556.13) * mm});
            skLineSegment(sketch, "E735", {"start": v(-426.44, -556.13) * mm, "end": v(-441.44, -556.13) * mm});
            skArc(sketch, "E736", {"start": v(-441.44, -556.13) * mm, "mid": v(-444.45, -553.12) * mm, "end": v(-441.44, -550.1) * mm});
            skLineSegment(sketch, "E737", {"start": v(-441.44, -550.1) * mm, "end": v(-441.44, -302.15) * mm});
            skArc(sketch, "E738", {"start": v(-441.44, -302.15) * mm, "mid": v(-444.45, -299.14) * mm, "end": v(-441.44, -296.13) * mm});
            skLineSegment(sketch, "E739", {"start": v(-441.44, -296.13) * mm, "end": v(-426.44, -296.13) * mm});
            skLineSegment(sketch, "E740", {"start": v(-426.44, -296.13) * mm, "end": v(-423.44, -293.13) * mm});
            skLineSegment(sketch, "E741", {"start": v(-423.44, -293.13) * mm, "end": v(-423.44, -259.13) * mm});
            skLineSegment(sketch, "E742", {"start": v(-423.44, -259.13) * mm, "end": v(-426.44, -256.13) * mm});
            skLineSegment(sketch, "E743", {"start": v(-426.44, -256.13) * mm, "end": v(-441.44, -256.13) * mm});
            skArc(sketch, "E744", {"start": v(-441.44, -256.13) * mm, "mid": v(-444.45, -253.12) * mm, "end": v(-441.44, -250.1) * mm});
            skLineSegment(sketch, "E745", {"start": v(-441.44, -250.1) * mm, "end": v(-441.44, -2.15) * mm});
            skArc(sketch, "E746", {"start": v(-441.44, -2.15) * mm, "mid": v(-444.45, 0.86) * mm, "end": v(-441.44, 3.87) * mm});
            skLineSegment(sketch, "E747", {"start": v(-441.44, 3.87) * mm, "end": v(-426.44, 3.87) * mm});
            skLineSegment(sketch, "E748", {"start": v(-426.44, 3.87) * mm, "end": v(-423.44, 6.87) * mm});
            skLineSegment(sketch, "E749", {"start": v(-423.44, 6.87) * mm, "end": v(-423.44, 40.87) * mm});
            skLineSegment(sketch, "E750", {"start": v(-423.44, 40.87) * mm, "end": v(-426.44, 43.87) * mm});
            skLineSegment(sketch, "E751", {"start": v(-426.44, 43.87) * mm, "end": v(-441.44, 43.87) * mm});
            skArc(sketch, "E752", {"start": v(-441.44, 43.87) * mm, "mid": v(-444.45, 46.88) * mm, "end": v(-441.44, 49.9) * mm});
            skLineSegment(sketch, "E753", {"start": v(-441.44, 49.9) * mm, "end": v(-441.44, 297.85) * mm});
            skArc(sketch, "E754", {"start": v(-441.44, 297.85) * mm, "mid": v(-444.45, 300.86) * mm, "end": v(-441.44, 303.87) * mm});
            skLineSegment(sketch, "E755", {"start": v(-441.44, 303.87) * mm, "end": v(-426.44, 303.87) * mm});
            skLineSegment(sketch, "E756", {"start": v(-426.44, 303.87) * mm, "end": v(-423.44, 306.87) * mm});
            skLineSegment(sketch, "E757", {"start": v(-423.44, 306.87) * mm, "end": v(-423.45, 314.87) * mm});
            skLineSegment(sketch, "E758", {"start": v(-423.45, 314.87) * mm, "end": v(-466.43, 314.87) * mm});
            skArc(sketch, "E759", {"start": v(-466.43, 314.87) * mm, "mid": v(-469.44, 311.86) * mm, "end": v(-472.45, 314.87) * mm});
            skLineSegment(sketch, "E760", {"start": v(-472.45, 314.87) * mm, "end": v(-472.45, 332.87) * mm});
            skArc(sketch, "E761", {"start": v(-472.45, 332.87) * mm, "mid": v(-469.44, 335.88) * mm, "end": v(-466.43, 332.87) * mm});
            skLineSegment(sketch, "E762", {"start": v(-466.43, 332.87) * mm, "end": v(-423.45, 332.87) * mm});
            skLineSegment(sketch, "E763", {"start": v(-423.45, 332.87) * mm, "end": v(-423.44, 340.87) * mm});
            skLineSegment(sketch, "E764", {"start": v(-423.44, 340.87) * mm, "end": v(-426.44, 343.87) * mm});
            skLineSegment(sketch, "E765", {"start": v(-426.44, 343.87) * mm, "end": v(-441.44, 343.87) * mm});
            skArc(sketch, "E766", {"start": v(-441.44, 343.87) * mm, "mid": v(-444.45, 346.88) * mm, "end": v(-441.44, 349.9) * mm});
            skLineSegment(sketch, "E767", {"start": v(-441.44, 349.9) * mm, "end": v(-441.44, 597.85) * mm});
            skArc(sketch, "E768", {"start": v(-441.44, 597.85) * mm, "mid": v(-444.45, 600.86) * mm, "end": v(-441.44, 603.87) * mm});
            skLineSegment(sketch, "E769", {"start": v(-441.44, 603.87) * mm, "end": v(-426.44, 603.87) * mm});
            skLineSegment(sketch, "E770", {"start": v(-426.44, 603.87) * mm, "end": v(-423.44, 606.87) * mm});
            skLineSegment(sketch, "E771", {"start": v(-423.44, 606.87) * mm, "end": v(-423.44, 640.87) * mm});
            skLineSegment(sketch, "E772", {"start": v(572, 544.77) * mm, "end": v(557, 544.77) * mm});
            skArc(sketch, "E773", {"start": v(557, 544.77) * mm, "mid": v(554, 547.78) * mm, "end": v(557, 550.79) * mm});
            skLineSegment(sketch, "E774", {"start": v(557, 550.79) * mm, "end": v(557, 798.75) * mm});
            skArc(sketch, "E775", {"start": v(557, 798.75) * mm, "mid": v(554, 801.76) * mm, "end": v(557, 804.77) * mm});
            skLineSegment(sketch, "E776", {"start": v(557, 804.77) * mm, "end": v(572, 804.77) * mm});
            skLineSegment(sketch, "E777", {"start": v(572, 804.77) * mm, "end": v(575, 807.77) * mm});
            skLineSegment(sketch, "E778", {"start": v(575, 807.77) * mm, "end": v(575, 841.77) * mm});
            skLineSegment(sketch, "E779", {"start": v(575, 841.77) * mm, "end": v(572, 844.77) * mm});
            skLineSegment(sketch, "E780", {"start": v(572, 844.77) * mm, "end": v(557, 844.77) * mm});
            skArc(sketch, "E781", {"start": v(557, 844.77) * mm, "mid": v(554, 847.78) * mm, "end": v(557, 850.79) * mm});
            skLineSegment(sketch, "E782", {"start": v(557, 850.79) * mm, "end": v(557, 1098.75) * mm});
            skArc(sketch, "E783", {"start": v(557, 1098.75) * mm, "mid": v(554, 1101.76) * mm, "end": v(557, 1104.77) * mm});
            skLineSegment(sketch, "E784", {"start": v(557, 1104.77) * mm, "end": v(572, 1104.77) * mm});
            skLineSegment(sketch, "E785", {"start": v(572, 1104.77) * mm, "end": v(575, 1107.77) * mm});
            skLineSegment(sketch, "E786", {"start": v(575, 1107.77) * mm, "end": v(575, 1141.77) * mm});
            skLineSegment(sketch, "E787", {"start": v(575, 1141.77) * mm, "end": v(572, 1144.77) * mm});
            skLineSegment(sketch, "E788", {"start": v(572, 1144.77) * mm, "end": v(557, 1144.77) * mm});
            skArc(sketch, "E789", {"start": v(557, 1144.77) * mm, "mid": v(554, 1147.78) * mm, "end": v(557, 1150.79) * mm});
            skLineSegment(sketch, "E790", {"start": v(557, 1150.79) * mm, "end": v(557, 1184.77) * mm});
            skLineSegment(sketch, "E791", {"start": v(557, 1184.77) * mm, "end": v(443, 1184.77) * mm});
            skLineSegment(sketch, "E792", {"start": v(443, 1184.77) * mm, "end": v(443, 1150.79) * mm});
            skArc(sketch, "E793", {"start": v(443, 1150.79) * mm, "mid": v(446.01, 1147.78) * mm, "end": v(443, 1144.77) * mm});
            skLineSegment(sketch, "E794", {"start": v(443, 1144.77) * mm, "end": v(428, 1144.77) * mm});
            skLineSegment(sketch, "E795", {"start": v(428, 1144.77) * mm, "end": v(425, 1141.77) * mm});
            skLineSegment(sketch, "E796", {"start": v(425, 1141.77) * mm, "end": v(425, 1107.77) * mm});
            skLineSegment(sketch, "E797", {"start": v(425, 1107.77) * mm, "end": v(428, 1104.77) * mm});
            skLineSegment(sketch, "E798", {"start": v(428, 1104.77) * mm, "end": v(443, 1104.77) * mm});
            skArc(sketch, "E799", {"start": v(443, 1104.77) * mm, "mid": v(446.01, 1101.76) * mm, "end": v(443, 1098.75) * mm});
            skLineSegment(sketch, "E800", {"start": v(443, 1098.75) * mm, "end": v(443, 850.79) * mm});
            skArc(sketch, "E801", {"start": v(443, 850.79) * mm, "mid": v(446.01, 847.78) * mm, "end": v(443, 844.77) * mm});
            skLineSegment(sketch, "E802", {"start": v(443, 844.77) * mm, "end": v(428, 844.77) * mm});
            skLineSegment(sketch, "E803", {"start": v(428, 844.77) * mm, "end": v(425, 841.77) * mm});
            skLineSegment(sketch, "E804", {"start": v(425, 841.77) * mm, "end": v(425, 807.77) * mm});
            skLineSegment(sketch, "E805", {"start": v(425, 807.77) * mm, "end": v(428, 804.77) * mm});
            skLineSegment(sketch, "E806", {"start": v(428, 804.77) * mm, "end": v(443, 804.77) * mm});
            skArc(sketch, "E807", {"start": v(443, 804.77) * mm, "mid": v(446.01, 801.76) * mm, "end": v(443, 798.75) * mm});
            skLineSegment(sketch, "E808", {"start": v(443, 798.75) * mm, "end": v(443, 550.79) * mm});
            skArc(sketch, "E809", {"start": v(443, 550.79) * mm, "mid": v(446.01, 547.78) * mm, "end": v(443, 544.77) * mm});
            skLineSegment(sketch, "E810", {"start": v(443, 544.77) * mm, "end": v(428, 544.77) * mm});
            skLineSegment(sketch, "E811", {"start": v(428, 544.77) * mm, "end": v(425, 541.77) * mm});
            skLineSegment(sketch, "E812", {"start": v(425, 541.77) * mm, "end": v(425, 507.77) * mm});
            skLineSegment(sketch, "E813", {"start": v(425, 507.77) * mm, "end": v(428, 504.77) * mm});
            skLineSegment(sketch, "E814", {"start": v(428, 504.77) * mm, "end": v(443, 504.77) * mm});
            skArc(sketch, "E815", {"start": v(443, 504.77) * mm, "mid": v(446.01, 501.76) * mm, "end": v(443, 498.75) * mm});
            skLineSegment(sketch, "E816", {"start": v(443, 498.75) * mm, "end": v(443, 250.79) * mm});
            skArc(sketch, "E817", {"start": v(443, 250.79) * mm, "mid": v(446.01, 247.78) * mm, "end": v(443, 244.77) * mm});
            skLineSegment(sketch, "E818", {"start": v(443, 244.77) * mm, "end": v(428, 244.77) * mm});
            skLineSegment(sketch, "E819", {"start": v(428, 244.77) * mm, "end": v(425, 241.77) * mm});
            skLineSegment(sketch, "E820", {"start": v(425, 241.77) * mm, "end": v(425, 207.77) * mm});
            skLineSegment(sketch, "E821", {"start": v(425, 207.77) * mm, "end": v(428, 204.77) * mm});
            skLineSegment(sketch, "E822", {"start": v(428, 204.77) * mm, "end": v(443, 204.77) * mm});
            skArc(sketch, "E823", {"start": v(443, 204.77) * mm, "mid": v(446.01, 201.76) * mm, "end": v(443, 198.75) * mm});
            skLineSegment(sketch, "E824", {"start": v(443, 198.75) * mm, "end": v(443, -49.21) * mm});
            skArc(sketch, "E825", {"start": v(443, -49.21) * mm, "mid": v(446.01, -52.22) * mm, "end": v(443, -55.23) * mm});
            skLineSegment(sketch, "E826", {"start": v(443, -55.23) * mm, "end": v(428, -55.23) * mm});
            skLineSegment(sketch, "E827", {"start": v(428, -55.23) * mm, "end": v(425, -58.23) * mm});
            skLineSegment(sketch, "E828", {"start": v(425, -58.23) * mm, "end": v(425, -66.23) * mm});
            skLineSegment(sketch, "E829", {"start": v(425, -66.23) * mm, "end": v(467.98, -66.23) * mm});
            skArc(sketch, "E830", {"start": v(467.98, -66.23) * mm, "mid": v(470.99, -63.22) * mm, "end": v(474, -66.23) * mm});
            skLineSegment(sketch, "E831", {"start": v(474, -66.23) * mm, "end": v(474, -84.23) * mm});
            skArc(sketch, "E832", {"start": v(474, -84.23) * mm, "mid": v(470.99, -87.24) * mm, "end": v(467.98, -84.23) * mm});
            skLineSegment(sketch, "E833", {"start": v(467.98, -84.23) * mm, "end": v(425, -84.23) * mm});
            skLineSegment(sketch, "E834", {"start": v(425, -84.23) * mm, "end": v(425, -92.23) * mm});
            skLineSegment(sketch, "E835", {"start": v(425, -92.23) * mm, "end": v(428, -95.23) * mm});
            skLineSegment(sketch, "E836", {"start": v(428, -95.23) * mm, "end": v(443, -95.23) * mm});
            skArc(sketch, "E837", {"start": v(443, -95.23) * mm, "mid": v(446.01, -98.24) * mm, "end": v(443, -101.25) * mm});
            skLineSegment(sketch, "E838", {"start": v(443, -101.25) * mm, "end": v(443, -349.21) * mm});
            skArc(sketch, "E839", {"start": v(443, -349.21) * mm, "mid": v(446.01, -352.22) * mm, "end": v(443, -355.23) * mm});
            skLineSegment(sketch, "E840", {"start": v(443, -355.23) * mm, "end": v(428, -355.23) * mm});
            skLineSegment(sketch, "E841", {"start": v(428, -355.23) * mm, "end": v(425, -358.23) * mm});
            skLineSegment(sketch, "E842", {"start": v(425, -358.23) * mm, "end": v(425, -392.23) * mm});
            skLineSegment(sketch, "E843", {"start": v(425, -392.23) * mm, "end": v(428, -395.23) * mm});
            skLineSegment(sketch, "E844", {"start": v(428, -395.23) * mm, "end": v(443, -395.23) * mm});
            skArc(sketch, "E845", {"start": v(443, -395.23) * mm, "mid": v(446.01, -398.24) * mm, "end": v(443, -401.25) * mm});
            skLineSegment(sketch, "E846", {"start": v(443, -401.25) * mm, "end": v(443, -649.21) * mm});
            skArc(sketch, "E847", {"start": v(443, -649.21) * mm, "mid": v(446.01, -652.22) * mm, "end": v(443, -655.23) * mm});
            skLineSegment(sketch, "E848", {"start": v(443, -655.23) * mm, "end": v(428, -655.23) * mm});
            skLineSegment(sketch, "E849", {"start": v(428, -655.23) * mm, "end": v(425, -658.23) * mm});
            skLineSegment(sketch, "E850", {"start": v(425, -658.23) * mm, "end": v(425, -692.23) * mm});
            skLineSegment(sketch, "E851", {"start": v(425, -692.23) * mm, "end": v(428, -695.23) * mm});
            skLineSegment(sketch, "E852", {"start": v(428, -695.23) * mm, "end": v(443, -695.23) * mm});
            skArc(sketch, "E853", {"start": v(443, -695.23) * mm, "mid": v(446.01, -698.24) * mm, "end": v(443, -701.25) * mm});
            skLineSegment(sketch, "E854", {"start": v(443, -701.25) * mm, "end": v(443, -869.21) * mm});
            skArc(sketch, "E855", {"start": v(443, -869.21) * mm, "mid": v(446, -872.22) * mm, "end": v(443, -875.23) * mm});
            skLineSegment(sketch, "E856", {"start": v(443, -875.23) * mm, "end": v(428, -875.23) * mm});
            skLineSegment(sketch, "E857", {"start": v(428, -875.23) * mm, "end": v(425, -878.23) * mm});
            skLineSegment(sketch, "E858", {"start": v(425, -878.23) * mm, "end": v(425, -912.23) * mm});
            skLineSegment(sketch, "E859", {"start": v(425, -912.23) * mm, "end": v(428, -915.23) * mm});
            skLineSegment(sketch, "E860", {"start": v(428, -915.23) * mm, "end": v(443, -915.23) * mm});
            skArc(sketch, "E861", {"start": v(443, -915.23) * mm, "mid": v(446, -918.24) * mm, "end": v(443, -921.25) * mm});
            skLineSegment(sketch, "E862", {"start": v(443, -921.25) * mm, "end": v(443, -1175) * mm});
            skLineSegment(sketch, "E863", {"start": v(443, -1175) * mm, "end": v(557, -1175) * mm});
            skLineSegment(sketch, "E864", {"start": v(557, -1175) * mm, "end": v(557, -921.25) * mm});
            skArc(sketch, "E865", {"start": v(557, -921.25) * mm, "mid": v(553.99, -918.24) * mm, "end": v(557, -915.23) * mm});
            skLineSegment(sketch, "E866", {"start": v(557, -915.23) * mm, "end": v(572, -915.23) * mm});
            skLineSegment(sketch, "E867", {"start": v(572, -915.23) * mm, "end": v(575, -912.23) * mm});
            skLineSegment(sketch, "E868", {"start": v(575, -912.23) * mm, "end": v(575, -878.23) * mm});
            skLineSegment(sketch, "E869", {"start": v(575, -878.23) * mm, "end": v(572, -875.23) * mm});
            skLineSegment(sketch, "E870", {"start": v(572, -875.23) * mm, "end": v(557, -875.23) * mm});
            skArc(sketch, "E871", {"start": v(557, -875.23) * mm, "mid": v(553.99, -872.22) * mm, "end": v(557, -869.21) * mm});
            skLineSegment(sketch, "E872", {"start": v(557, -869.21) * mm, "end": v(557, -701.25) * mm});
            skArc(sketch, "E873", {"start": v(557, -701.25) * mm, "mid": v(554, -698.24) * mm, "end": v(557, -695.23) * mm});
            skLineSegment(sketch, "E874", {"start": v(557, -695.23) * mm, "end": v(572, -695.23) * mm});
            skLineSegment(sketch, "E875", {"start": v(572, -695.23) * mm, "end": v(575, -692.23) * mm});
            skLineSegment(sketch, "E876", {"start": v(575, -692.23) * mm, "end": v(575, -658.23) * mm});
            skLineSegment(sketch, "E877", {"start": v(575, -658.23) * mm, "end": v(572, -655.23) * mm});
            skLineSegment(sketch, "E878", {"start": v(572, -655.23) * mm, "end": v(557, -655.23) * mm});
            skArc(sketch, "E879", {"start": v(557, -655.23) * mm, "mid": v(554, -652.22) * mm, "end": v(557, -649.21) * mm});
            skLineSegment(sketch, "E880", {"start": v(557, -649.21) * mm, "end": v(557, -401.25) * mm});
            skArc(sketch, "E881", {"start": v(557, -401.25) * mm, "mid": v(554, -398.24) * mm, "end": v(557, -395.23) * mm});
            skLineSegment(sketch, "E882", {"start": v(557, -395.23) * mm, "end": v(572, -395.23) * mm});
            skLineSegment(sketch, "E883", {"start": v(572, -395.23) * mm, "end": v(575, -392.23) * mm});
            skLineSegment(sketch, "E884", {"start": v(575, -392.23) * mm, "end": v(575, -358.23) * mm});
            skLineSegment(sketch, "E885", {"start": v(575, -358.23) * mm, "end": v(572, -355.23) * mm});
            skLineSegment(sketch, "E886", {"start": v(572, -355.23) * mm, "end": v(557, -355.23) * mm});
            skArc(sketch, "E887", {"start": v(557, -355.23) * mm, "mid": v(554, -352.22) * mm, "end": v(557, -349.21) * mm});
            skLineSegment(sketch, "E888", {"start": v(557, -349.21) * mm, "end": v(557, -101.25) * mm});
            skArc(sketch, "E889", {"start": v(557, -101.25) * mm, "mid": v(554, -98.24) * mm, "end": v(557, -95.23) * mm});
            skLineSegment(sketch, "E890", {"start": v(557, -95.23) * mm, "end": v(572, -95.23) * mm});
            skLineSegment(sketch, "E891", {"start": v(572, -95.23) * mm, "end": v(575, -92.23) * mm});
            skLineSegment(sketch, "E892", {"start": v(575, -92.23) * mm, "end": v(575, -84.23) * mm});
            skLineSegment(sketch, "E893", {"start": v(575, -84.23) * mm, "end": v(532.02, -84.23) * mm});
            skArc(sketch, "E894", {"start": v(532.02, -84.23) * mm, "mid": v(529, -87.24) * mm, "end": v(526, -84.23) * mm});
            skLineSegment(sketch, "E895", {"start": v(526, -84.23) * mm, "end": v(526, -66.23) * mm});
            skArc(sketch, "E896", {"start": v(526, -66.23) * mm, "mid": v(529, -63.22) * mm, "end": v(532.02, -66.23) * mm});
            skLineSegment(sketch, "E897", {"start": v(532.02, -66.23) * mm, "end": v(575, -66.23) * mm});
            skLineSegment(sketch, "E898", {"start": v(575, -66.23) * mm, "end": v(575, -58.23) * mm});
            skLineSegment(sketch, "E899", {"start": v(575, -58.23) * mm, "end": v(572, -55.23) * mm});
            skLineSegment(sketch, "E900", {"start": v(572, -55.23) * mm, "end": v(557, -55.23) * mm});
            skArc(sketch, "E901", {"start": v(557, -55.23) * mm, "mid": v(554, -52.22) * mm, "end": v(557, -49.21) * mm});
            skLineSegment(sketch, "E902", {"start": v(557, -49.21) * mm, "end": v(557, 198.75) * mm});
            skArc(sketch, "E903", {"start": v(557, 198.75) * mm, "mid": v(554, 201.76) * mm, "end": v(557, 204.77) * mm});
            skLineSegment(sketch, "E904", {"start": v(557, 204.77) * mm, "end": v(572, 204.77) * mm});
            skLineSegment(sketch, "E905", {"start": v(572, 204.77) * mm, "end": v(575, 207.77) * mm});
            skLineSegment(sketch, "E906", {"start": v(575, 207.77) * mm, "end": v(575, 241.77) * mm});
            skLineSegment(sketch, "E907", {"start": v(575, 241.77) * mm, "end": v(572, 244.77) * mm});
            skLineSegment(sketch, "E908", {"start": v(572, 244.77) * mm, "end": v(557, 244.77) * mm});
            skArc(sketch, "E909", {"start": v(557, 244.77) * mm, "mid": v(554, 247.78) * mm, "end": v(557, 250.79) * mm});
            skLineSegment(sketch, "E910", {"start": v(557, 250.79) * mm, "end": v(557, 498.75) * mm});
            skArc(sketch, "E911", {"start": v(557, 498.75) * mm, "mid": v(554, 501.76) * mm, "end": v(557, 504.77) * mm});
            skLineSegment(sketch, "E912", {"start": v(557, 504.77) * mm, "end": v(572, 504.77) * mm});
            skLineSegment(sketch, "E913", {"start": v(572, 504.77) * mm, "end": v(575, 507.77) * mm});
            skLineSegment(sketch, "E914", {"start": v(575, 507.77) * mm, "end": v(575, 541.77) * mm});
            skLineSegment(sketch, "E915", {"start": v(575, 541.77) * mm, "end": v(572, 544.77) * mm});
            skLineSegment(sketch, "E916", {"start": v(-439.44, -907.03) * mm, "end": v(-439.44, -979.93) * mm});
            skLineSegment(sketch, "E917", {"start": v(-439.44, -979.93) * mm, "end": v(-555.44, -979.93) * mm});
            skLineSegment(sketch, "E918", {"start": v(-555.44, -979.93) * mm, "end": v(-555.44, -831.13) * mm});
            skLineSegment(sketch, "E919", {"start": v(-555.44, -831.13) * mm, "end": v(-305.64, -831.13) * mm});
            skLineSegment(sketch, "E920", {"start": v(-305.64, -831.13) * mm, "end": v(-305.64, -979.93) * mm});
            skLineSegment(sketch, "E921", {"start": v(-305.64, -979.93) * mm, "end": v(-421.64, -979.93) * mm});
            skLineSegment(sketch, "E922", {"start": v(-421.64, -979.93) * mm, "end": v(-421.64, -907.03) * mm});
            skArc(sketch, "E923", {"start": v(-421.64, -907.03) * mm, "mid": v(-422.55, -904.84) * mm, "end": v(-424.74, -903.93) * mm});
            skLineSegment(sketch, "E924", {"start": v(-424.74, -903.93) * mm, "end": v(-436.34, -903.93) * mm});
            skArc(sketch, "E925", {"start": v(-436.34, -903.93) * mm, "mid": v(-438.54, -904.84) * mm, "end": v(-439.44, -907.03) * mm});
            skLineSegment(sketch, "E926", {"start": v(-439.44, -1075.83) * mm, "end": v(-439.44, -1148.73) * mm});
            skLineSegment(sketch, "E927", {"start": v(-439.44, -1148.73) * mm, "end": v(-555.44, -1148.73) * mm});
            skLineSegment(sketch, "E928", {"start": v(-555.44, -1148.73) * mm, "end": v(-555.44, -999.93) * mm});
            skLineSegment(sketch, "E929", {"start": v(-555.44, -999.93) * mm, "end": v(-305.64, -999.93) * mm});
            skLineSegment(sketch, "E930", {"start": v(-305.64, -999.93) * mm, "end": v(-305.64, -1148.73) * mm});
            skLineSegment(sketch, "E931", {"start": v(-305.64, -1148.73) * mm, "end": v(-421.64, -1148.73) * mm});
            skLineSegment(sketch, "E932", {"start": v(-421.64, -1148.73) * mm, "end": v(-421.64, -1075.83) * mm});
            skArc(sketch, "E933", {"start": v(-421.64, -1075.83) * mm, "mid": v(-422.55, -1073.64) * mm, "end": v(-424.74, -1072.73) * mm});
            skLineSegment(sketch, "E934", {"start": v(-424.74, -1072.73) * mm, "end": v(-436.34, -1072.73) * mm});
            skArc(sketch, "E935", {"start": v(-436.34, -1072.73) * mm, "mid": v(-438.54, -1073.64) * mm, "end": v(-439.44, -1075.83) * mm});
            skLineSegment(sketch, "E936", {"start": v(-151.32, 16.18) * mm, "end": v(-150.93, 16.31) * mm});
            skLineSegment(sketch, "E937", {"start": v(-150.93, 16.31) * mm, "end": v(-150.54, 16.46) * mm});
            skLineSegment(sketch, "E938", {"start": v(-150.54, 16.46) * mm, "end": v(-150.16, 16.61) * mm});
            skLineSegment(sketch, "E939", {"start": v(-150.16, 16.61) * mm, "end": v(-149.78, 16.78) * mm});
            skLineSegment(sketch, "E940", {"start": v(-149.78, 16.78) * mm, "end": v(-149.4, 16.96) * mm});
            skLineSegment(sketch, "E941", {"start": v(-149.4, 16.96) * mm, "end": v(-149.04, 17.15) * mm});
            skLineSegment(sketch, "E942", {"start": v(-149.04, 17.15) * mm, "end": v(-148.68, 17.35) * mm});
            skLineSegment(sketch, "E943", {"start": v(-148.68, 17.35) * mm, "end": v(-148.33, 17.57) * mm});
            skLineSegment(sketch, "E944", {"start": v(-148.33, 17.57) * mm, "end": v(-147.99, 17.8) * mm});
            skLineSegment(sketch, "E945", {"start": v(-147.99, 17.8) * mm, "end": v(-147.65, 18.03) * mm});
            skLineSegment(sketch, "E946", {"start": v(-147.65, 18.03) * mm, "end": v(-147.32, 18.27) * mm});
            skLineSegment(sketch, "E947", {"start": v(-147.32, 18.27) * mm, "end": v(-147, 18.53) * mm});
            skLineSegment(sketch, "E948", {"start": v(-147, 18.53) * mm, "end": v(-146.68, 18.8) * mm});
            skLineSegment(sketch, "E949", {"start": v(-146.68, 18.8) * mm, "end": v(-146.37, 19.07) * mm});
            skLineSegment(sketch, "E950", {"start": v(-146.37, 19.07) * mm, "end": v(-146.08, 19.36) * mm});
            skLineSegment(sketch, "E951", {"start": v(-146.08, 19.36) * mm, "end": v(-145.79, 19.66) * mm});
            skLineSegment(sketch, "E952", {"start": v(-145.79, 19.66) * mm, "end": v(-145.56, 19.9) * mm});
            skLineSegment(sketch, "E953", {"start": v(-145.56, 19.9) * mm, "end": v(-145.33, 20.16) * mm});
            skLineSegment(sketch, "E954", {"start": v(-145.33, 20.16) * mm, "end": v(-145.12, 20.41) * mm});
            skLineSegment(sketch, "E955", {"start": v(-145.12, 20.41) * mm, "end": v(-144.91, 20.68) * mm});
            skLineSegment(sketch, "E956", {"start": v(-144.91, 20.68) * mm, "end": v(-144.7, 20.94) * mm});
            skLineSegment(sketch, "E957", {"start": v(-144.7, 20.94) * mm, "end": v(-144.51, 21.21) * mm});
            skLineSegment(sketch, "E958", {"start": v(-144.51, 21.21) * mm, "end": v(-144.33, 21.5) * mm});
            skLineSegment(sketch, "E959", {"start": v(-144.33, 21.5) * mm, "end": v(-144.15, 21.77) * mm});
            skLineSegment(sketch, "E960", {"start": v(-144.15, 21.77) * mm, "end": v(-143.98, 22.06) * mm});
            skLineSegment(sketch, "E961", {"start": v(-143.98, 22.06) * mm, "end": v(-143.81, 22.35) * mm});
            skLineSegment(sketch, "E962", {"start": v(-143.81, 22.35) * mm, "end": v(-143.65, 22.64) * mm});
            skLineSegment(sketch, "E963", {"start": v(-143.65, 22.64) * mm, "end": v(-143.5, 22.93) * mm});
            skLineSegment(sketch, "E964", {"start": v(-143.5, 22.93) * mm, "end": v(-143.36, 23.23) * mm});
            skLineSegment(sketch, "E965", {"start": v(-143.36, 23.23) * mm, "end": v(-143.23, 23.54) * mm});
            skLineSegment(sketch, "E966", {"start": v(-143.23, 23.54) * mm, "end": v(-143.1, 23.84) * mm});
            skLineSegment(sketch, "E967", {"start": v(-143.1, 23.84) * mm, "end": v(-142.98, 24.15) * mm});
            skLineSegment(sketch, "E968", {"start": v(-142.98, 24.15) * mm, "end": v(-142.87, 24.47) * mm});
            skLineSegment(sketch, "E969", {"start": v(-142.87, 24.47) * mm, "end": v(-142.77, 24.78) * mm});
            skLineSegment(sketch, "E970", {"start": v(-142.77, 24.78) * mm, "end": v(-142.67, 25.1) * mm});
            skLineSegment(sketch, "E971", {"start": v(-142.67, 25.1) * mm, "end": v(-142.59, 25.42) * mm});
            skLineSegment(sketch, "E972", {"start": v(-142.59, 25.42) * mm, "end": v(-142.5, 25.74) * mm});
            skLineSegment(sketch, "E973", {"start": v(-142.5, 25.74) * mm, "end": v(-142.44, 26.07) * mm});
            skLineSegment(sketch, "E974", {"start": v(-142.44, 26.07) * mm, "end": v(-142.38, 26.4) * mm});
            skLineSegment(sketch, "E975", {"start": v(-142.38, 26.4) * mm, "end": v(-142.32, 26.72) * mm});
            skLineSegment(sketch, "E976", {"start": v(-142.32, 26.72) * mm, "end": v(-142.28, 27.05) * mm});
            skLineSegment(sketch, "E977", {"start": v(-142.28, 27.05) * mm, "end": v(-142.24, 27.39) * mm});
            skLineSegment(sketch, "E978", {"start": v(-142.24, 27.39) * mm, "end": v(-142.21, 27.72) * mm});
            skLineSegment(sketch, "E979", {"start": v(-142.21, 27.72) * mm, "end": v(-142.2, 28.05) * mm});
            skLineSegment(sketch, "E980", {"start": v(-142.2, 28.05) * mm, "end": v(-142.18, 28.39) * mm});
            skLineSegment(sketch, "E981", {"start": v(-142.18, 28.39) * mm, "end": v(-142.18, 28.72) * mm});
            skLineSegment(sketch, "E982", {"start": v(-142.18, 28.72) * mm, "end": v(-142.18, 29.06) * mm});
            skLineSegment(sketch, "E983", {"start": v(-142.18, 29.06) * mm, "end": v(-142.2, 29.4) * mm});
            skLineSegment(sketch, "E984", {"start": v(-142.2, 29.4) * mm, "end": v(-142.19, 29.7) * mm});
            skLineSegment(sketch, "E985", {"start": v(-142.19, 29.7) * mm, "end": v(-142.19, 30.02) * mm});
            skLineSegment(sketch, "E986", {"start": v(-142.19, 30.02) * mm, "end": v(-142.2, 30.32) * mm});
            skLineSegment(sketch, "E987", {"start": v(-142.2, 30.32) * mm, "end": v(-142.21, 30.63) * mm});
            skLineSegment(sketch, "E988", {"start": v(-142.21, 30.63) * mm, "end": v(-142.23, 30.94) * mm});
            skLineSegment(sketch, "E989", {"start": v(-142.23, 30.94) * mm, "end": v(-142.26, 31.24) * mm});
            skLineSegment(sketch, "E990", {"start": v(-142.26, 31.24) * mm, "end": v(-142.3, 31.55) * mm});
            skLineSegment(sketch, "E991", {"start": v(-142.3, 31.55) * mm, "end": v(-142.35, 31.85) * mm});
            skLineSegment(sketch, "E992", {"start": v(-142.35, 31.85) * mm, "end": v(-142.4, 32.15) * mm});
            skLineSegment(sketch, "E993", {"start": v(-142.4, 32.15) * mm, "end": v(-142.46, 32.45) * mm});
            skLineSegment(sketch, "E994", {"start": v(-142.46, 32.45) * mm, "end": v(-142.53, 32.75) * mm});
            skLineSegment(sketch, "E995", {"start": v(-142.53, 32.75) * mm, "end": v(-142.6, 33.04) * mm});
            skLineSegment(sketch, "E996", {"start": v(-142.6, 33.04) * mm, "end": v(-142.7, 33.34) * mm});
            skLineSegment(sketch, "E997", {"start": v(-142.7, 33.34) * mm, "end": v(-142.79, 33.63) * mm});
            skLineSegment(sketch, "E998", {"start": v(-142.79, 33.63) * mm, "end": v(-142.88, 33.92) * mm});
            skLineSegment(sketch, "E999", {"start": v(-142.88, 33.92) * mm, "end": v(-143, 34.2) * mm});
            skLineSegment(sketch, "E1000", {"start": v(-143, 34.2) * mm, "end": v(-143.1, 34.49) * mm});
            skLineSegment(sketch, "E1001", {"start": v(-143.1, 34.49) * mm, "end": v(-143.22, 34.77) * mm});
            skLineSegment(sketch, "E1002", {"start": v(-143.22, 34.77) * mm, "end": v(-143.35, 35.04) * mm});
            skLineSegment(sketch, "E1003", {"start": v(-143.35, 35.04) * mm, "end": v(-143.49, 35.32) * mm});
            skLineSegment(sketch, "E1004", {"start": v(-143.49, 35.32) * mm, "end": v(-143.63, 35.59) * mm});
            skLineSegment(sketch, "E1005", {"start": v(-143.63, 35.59) * mm, "end": v(-143.78, 35.85) * mm});
            skLineSegment(sketch, "E1006", {"start": v(-143.78, 35.85) * mm, "end": v(-143.93, 36.12) * mm});
            skLineSegment(sketch, "E1007", {"start": v(-143.93, 36.12) * mm, "end": v(-144.1, 36.38) * mm});
            skLineSegment(sketch, "E1008", {"start": v(-144.1, 36.38) * mm, "end": v(-144.26, 36.63) * mm});
            skLineSegment(sketch, "E1009", {"start": v(-144.26, 36.63) * mm, "end": v(-144.44, 36.88) * mm});
            skLineSegment(sketch, "E1010", {"start": v(-144.44, 36.88) * mm, "end": v(-144.62, 37.13) * mm});
            skLineSegment(sketch, "E1011", {"start": v(-144.62, 37.13) * mm, "end": v(-144.81, 37.37) * mm});
            skLineSegment(sketch, "E1012", {"start": v(-144.81, 37.37) * mm, "end": v(-145, 37.6) * mm});
            skLineSegment(sketch, "E1013", {"start": v(-145, 37.6) * mm, "end": v(-145.21, 37.84) * mm});
            skLineSegment(sketch, "E1014", {"start": v(-145.21, 37.84) * mm, "end": v(-145.42, 38.07) * mm});
            skLineSegment(sketch, "E1015", {"start": v(-145.42, 38.07) * mm, "end": v(-145.63, 38.3) * mm});
            skLineSegment(sketch, "E1016", {"start": v(-145.63, 38.3) * mm, "end": v(-145.93, 38.6) * mm});
            skLineSegment(sketch, "E1017", {"start": v(-145.93, 38.6) * mm, "end": v(-146.24, 38.88) * mm});
            skLineSegment(sketch, "E1018", {"start": v(-146.24, 38.88) * mm, "end": v(-146.56, 39.15) * mm});
            skLineSegment(sketch, "E1019", {"start": v(-146.56, 39.15) * mm, "end": v(-146.9, 39.4) * mm});
            skLineSegment(sketch, "E1020", {"start": v(-146.9, 39.4) * mm, "end": v(-147.24, 39.63) * mm});
            skLineSegment(sketch, "E1021", {"start": v(-147.24, 39.63) * mm, "end": v(-147.58, 39.85) * mm});
            skLineSegment(sketch, "E1022", {"start": v(-147.58, 39.85) * mm, "end": v(-147.94, 40.05) * mm});
            skLineSegment(sketch, "E1023", {"start": v(-147.94, 40.05) * mm, "end": v(-148.3, 40.23) * mm});
            skLineSegment(sketch, "E1024", {"start": v(-148.3, 40.23) * mm, "end": v(-148.68, 40.4) * mm});
            skLineSegment(sketch, "E1025", {"start": v(-148.68, 40.4) * mm, "end": v(-149.05, 40.54) * mm});
            skLineSegment(sketch, "E1026", {"start": v(-149.05, 40.54) * mm, "end": v(-149.44, 40.66) * mm});
            skLineSegment(sketch, "E1027", {"start": v(-149.44, 40.66) * mm, "end": v(-149.82, 40.77) * mm});
            skLineSegment(sketch, "E1028", {"start": v(-149.82, 40.77) * mm, "end": v(-150.21, 40.86) * mm});
            skLineSegment(sketch, "E1029", {"start": v(-150.21, 40.86) * mm, "end": v(-150.6, 40.94) * mm});
            skLineSegment(sketch, "E1030", {"start": v(-150.6, 40.94) * mm, "end": v(-151, 41) * mm});
            skLineSegment(sketch, "E1031", {"start": v(-151, 41) * mm, "end": v(-151.4, 41.03) * mm});
            skLineSegment(sketch, "E1032", {"start": v(-151.4, 41.03) * mm, "end": v(-151.8, 41.05) * mm});
            skLineSegment(sketch, "E1033", {"start": v(-151.8, 41.05) * mm, "end": v(-152.2, 41.05) * mm});
            skLineSegment(sketch, "E1034", {"start": v(-152.2, 41.05) * mm, "end": v(-152.6, 41.04) * mm});
            skLineSegment(sketch, "E1035", {"start": v(-152.6, 41.04) * mm, "end": v(-153, 41) * mm});
            skLineSegment(sketch, "E1036", {"start": v(-153, 41) * mm, "end": v(-153.4, 40.95) * mm});
            skLineSegment(sketch, "E1037", {"start": v(-153.4, 40.95) * mm, "end": v(-153.8, 40.88) * mm});
            skLineSegment(sketch, "E1038", {"start": v(-153.8, 40.88) * mm, "end": v(-154.2, 40.8) * mm});
            skLineSegment(sketch, "E1039", {"start": v(-154.2, 40.8) * mm, "end": v(-154.59, 40.68) * mm});
            skLineSegment(sketch, "E1040", {"start": v(-154.59, 40.68) * mm, "end": v(-154.97, 40.56) * mm});
            skLineSegment(sketch, "E1041", {"start": v(-154.97, 40.56) * mm, "end": v(-155.36, 40.41) * mm});
            skLineSegment(sketch, "E1042", {"start": v(-155.36, 40.41) * mm, "end": v(-155.73, 40.25) * mm});
            skLineSegment(sketch, "E1043", {"start": v(-155.73, 40.25) * mm, "end": v(-156.1, 40.07) * mm});
            skLineSegment(sketch, "E1044", {"start": v(-156.1, 40.07) * mm, "end": v(-156.47, 39.87) * mm});
            skLineSegment(sketch, "E1045", {"start": v(-156.47, 39.87) * mm, "end": v(-156.82, 39.65) * mm});
            skLineSegment(sketch, "E1046", {"start": v(-156.82, 39.65) * mm, "end": v(-157.17, 39.41) * mm});
            skLineSegment(sketch, "E1047", {"start": v(-157.17, 39.41) * mm, "end": v(-157.51, 39.16) * mm});
            skLineSegment(sketch, "E1048", {"start": v(-157.51, 39.16) * mm, "end": v(-157.77, 38.9) * mm});
            skLineSegment(sketch, "E1049", {"start": v(-157.77, 38.9) * mm, "end": v(-158.03, 38.63) * mm});
            skLineSegment(sketch, "E1050", {"start": v(-158.03, 38.63) * mm, "end": v(-158.28, 38.36) * mm});
            skLineSegment(sketch, "E1051", {"start": v(-158.28, 38.36) * mm, "end": v(-158.51, 38.08) * mm});
            skLineSegment(sketch, "E1052", {"start": v(-158.51, 38.08) * mm, "end": v(-158.75, 37.8) * mm});
            skLineSegment(sketch, "E1053", {"start": v(-158.75, 37.8) * mm, "end": v(-158.97, 37.51) * mm});
            skLineSegment(sketch, "E1054", {"start": v(-158.97, 37.51) * mm, "end": v(-159.18, 37.22) * mm});
            skLineSegment(sketch, "E1055", {"start": v(-159.18, 37.22) * mm, "end": v(-159.39, 36.92) * mm});
            skLineSegment(sketch, "E1056", {"start": v(-159.39, 36.92) * mm, "end": v(-159.59, 36.61) * mm});
            skLineSegment(sketch, "E1057", {"start": v(-159.59, 36.61) * mm, "end": v(-159.78, 36.3) * mm});
            skLineSegment(sketch, "E1058", {"start": v(-159.78, 36.3) * mm, "end": v(-159.96, 36) * mm});
            skLineSegment(sketch, "E1059", {"start": v(-159.96, 36) * mm, "end": v(-160.13, 35.67) * mm});
            skLineSegment(sketch, "E1060", {"start": v(-160.13, 35.67) * mm, "end": v(-160.3, 35.35) * mm});
            skLineSegment(sketch, "E1061", {"start": v(-160.3, 35.35) * mm, "end": v(-160.45, 35.02) * mm});
            skLineSegment(sketch, "E1062", {"start": v(-160.45, 35.02) * mm, "end": v(-160.6, 34.7) * mm});
            skLineSegment(sketch, "E1063", {"start": v(-160.6, 34.7) * mm, "end": v(-160.73, 34.36) * mm});
            skLineSegment(sketch, "E1064", {"start": v(-160.73, 34.36) * mm, "end": v(-160.86, 34.02) * mm});
            skLineSegment(sketch, "E1065", {"start": v(-160.86, 34.02) * mm, "end": v(-160.98, 33.68) * mm});
            skLineSegment(sketch, "E1066", {"start": v(-160.98, 33.68) * mm, "end": v(-161.1, 33.33) * mm});
            skLineSegment(sketch, "E1067", {"start": v(-161.1, 33.33) * mm, "end": v(-161.2, 32.99) * mm});
            skLineSegment(sketch, "E1068", {"start": v(-161.2, 32.99) * mm, "end": v(-161.29, 32.63) * mm});
            skLineSegment(sketch, "E1069", {"start": v(-161.29, 32.63) * mm, "end": v(-161.37, 32.28) * mm});
            skLineSegment(sketch, "E1070", {"start": v(-161.37, 32.28) * mm, "end": v(-161.44, 31.93) * mm});
            skLineSegment(sketch, "E1071", {"start": v(-161.44, 31.93) * mm, "end": v(-161.5, 31.57) * mm});
            skLineSegment(sketch, "E1072", {"start": v(-161.5, 31.57) * mm, "end": v(-161.56, 31.2) * mm});
            skLineSegment(sketch, "E1073", {"start": v(-161.56, 31.2) * mm, "end": v(-161.6, 30.85) * mm});
            skLineSegment(sketch, "E1074", {"start": v(-161.6, 30.85) * mm, "end": v(-161.64, 30.48) * mm});
            skLineSegment(sketch, "E1075", {"start": v(-161.64, 30.48) * mm, "end": v(-161.67, 30.12) * mm});
            skLineSegment(sketch, "E1076", {"start": v(-161.67, 30.12) * mm, "end": v(-161.68, 29.75) * mm});
            skLineSegment(sketch, "E1077", {"start": v(-161.68, 29.75) * mm, "end": v(-161.69, 29.39) * mm});
            skLineSegment(sketch, "E1078", {"start": v(-161.69, 29.39) * mm, "end": v(-161.68, 29.02) * mm});
            skLineSegment(sketch, "E1079", {"start": v(-161.68, 29.02) * mm, "end": v(-161.67, 28.65) * mm});
            skLineSegment(sketch, "E1080", {"start": v(-161.67, 28.65) * mm, "end": v(-161.61, 28.16) * mm});
            skLineSegment(sketch, "E1081", {"start": v(-161.61, 28.16) * mm, "end": v(-161.58, 27.67) * mm});
            skLineSegment(sketch, "E1082", {"start": v(-161.58, 27.67) * mm, "end": v(-161.57, 27.19) * mm});
            skLineSegment(sketch, "E1083", {"start": v(-161.57, 27.19) * mm, "end": v(-161.59, 26.7) * mm});
            skLineSegment(sketch, "E1084", {"start": v(-161.59, 26.7) * mm, "end": v(-161.63, 26.23) * mm});
            skLineSegment(sketch, "E1085", {"start": v(-161.63, 26.23) * mm, "end": v(-161.7, 25.76) * mm});
            skLineSegment(sketch, "E1086", {"start": v(-161.7, 25.76) * mm, "end": v(-161.77, 25.3) * mm});
            skLineSegment(sketch, "E1087", {"start": v(-161.77, 25.3) * mm, "end": v(-161.88, 24.83) * mm});
            skLineSegment(sketch, "E1088", {"start": v(-161.88, 24.83) * mm, "end": v(-162, 24.38) * mm});
            skLineSegment(sketch, "E1089", {"start": v(-162, 24.38) * mm, "end": v(-162.16, 23.94) * mm});
            skLineSegment(sketch, "E1090", {"start": v(-162.16, 23.94) * mm, "end": v(-162.32, 23.5) * mm});
            skLineSegment(sketch, "E1091", {"start": v(-162.32, 23.5) * mm, "end": v(-162.51, 23.07) * mm});
            skLineSegment(sketch, "E1092", {"start": v(-162.51, 23.07) * mm, "end": v(-162.72, 22.66) * mm});
            skLineSegment(sketch, "E1093", {"start": v(-162.72, 22.66) * mm, "end": v(-162.94, 22.25) * mm});
            skLineSegment(sketch, "E1094", {"start": v(-162.94, 22.25) * mm, "end": v(-163.19, 21.85) * mm});
            skLineSegment(sketch, "E1095", {"start": v(-163.19, 21.85) * mm, "end": v(-163.45, 21.47) * mm});
            skLineSegment(sketch, "E1096", {"start": v(-163.45, 21.47) * mm, "end": v(-163.73, 21.1) * mm});
            skLineSegment(sketch, "E1097", {"start": v(-163.73, 21.1) * mm, "end": v(-164.02, 20.74) * mm});
            skLineSegment(sketch, "E1098", {"start": v(-164.02, 20.74) * mm, "end": v(-164.34, 20.4) * mm});
            skLineSegment(sketch, "E1099", {"start": v(-164.34, 20.4) * mm, "end": v(-164.66, 20.07) * mm});
            skLineSegment(sketch, "E1100", {"start": v(-164.66, 20.07) * mm, "end": v(-165, 19.75) * mm});
            skLineSegment(sketch, "E1101", {"start": v(-165, 19.75) * mm, "end": v(-165.37, 19.45) * mm});
            skLineSegment(sketch, "E1102", {"start": v(-165.37, 19.45) * mm, "end": v(-165.74, 19.17) * mm});
            skLineSegment(sketch, "E1103", {"start": v(-165.74, 19.17) * mm, "end": v(-166.13, 18.9) * mm});
            skLineSegment(sketch, "E1104", {"start": v(-166.13, 18.9) * mm, "end": v(-166.53, 18.65) * mm});
            skLineSegment(sketch, "E1105", {"start": v(-166.53, 18.65) * mm, "end": v(-166.94, 18.42) * mm});
            skLineSegment(sketch, "E1106", {"start": v(-166.94, 18.42) * mm, "end": v(-167.37, 18.21) * mm});
            skLineSegment(sketch, "E1107", {"start": v(-167.37, 18.21) * mm, "end": v(-167.8, 18.02) * mm});
            skLineSegment(sketch, "E1108", {"start": v(-167.8, 18.02) * mm, "end": v(-168.26, 17.85) * mm});
            skLineSegment(sketch, "E1109", {"start": v(-168.26, 17.85) * mm, "end": v(-168.72, 17.7) * mm});
            skLineSegment(sketch, "E1110", {"start": v(-168.72, 17.7) * mm, "end": v(-169.2, 17.57) * mm});
            skLineSegment(sketch, "E1111", {"start": v(-169.2, 17.57) * mm, "end": v(-169.68, 17.47) * mm});
            skLineSegment(sketch, "E1112", {"start": v(-169.68, 17.47) * mm, "end": v(-170.08, 17.47) * mm});
            skLineSegment(sketch, "E1113", {"start": v(-170.08, 17.47) * mm, "end": v(-170.47, 17.5) * mm});
            skLineSegment(sketch, "E1114", {"start": v(-170.47, 17.5) * mm, "end": v(-170.87, 17.54) * mm});
            skLineSegment(sketch, "E1115", {"start": v(-170.87, 17.54) * mm, "end": v(-171.26, 17.6) * mm});
            skLineSegment(sketch, "E1116", {"start": v(-171.26, 17.6) * mm, "end": v(-171.64, 17.7) * mm});
            skLineSegment(sketch, "E1117", {"start": v(-171.64, 17.7) * mm, "end": v(-172.02, 17.8) * mm});
            skLineSegment(sketch, "E1118", {"start": v(-172.02, 17.8) * mm, "end": v(-172.39, 17.94) * mm});
            skLineSegment(sketch, "E1119", {"start": v(-172.39, 17.94) * mm, "end": v(-172.75, 18.09) * mm});
            skLineSegment(sketch, "E1120", {"start": v(-172.75, 18.09) * mm, "end": v(-173.1, 18.26) * mm});
            skLineSegment(sketch, "E1121", {"start": v(-173.1, 18.26) * mm, "end": v(-173.45, 18.45) * mm});
            skLineSegment(sketch, "E1122", {"start": v(-173.45, 18.45) * mm, "end": v(-173.78, 18.66) * mm});
            skLineSegment(sketch, "E1123", {"start": v(-173.78, 18.66) * mm, "end": v(-174.1, 18.88) * mm});
            skLineSegment(sketch, "E1124", {"start": v(-174.1, 18.88) * mm, "end": v(-174.4, 19.13) * mm});
            skLineSegment(sketch, "E1125", {"start": v(-174.4, 19.13) * mm, "end": v(-174.7, 19.4) * mm});
            skLineSegment(sketch, "E1126", {"start": v(-174.7, 19.4) * mm, "end": v(-174.99, 19.67) * mm});
            skLineSegment(sketch, "E1127", {"start": v(-174.99, 19.67) * mm, "end": v(-175.25, 19.97) * mm});
            skLineSegment(sketch, "E1128", {"start": v(-175.25, 19.97) * mm, "end": v(-175.47, 20.21) * mm});
            skLineSegment(sketch, "E1129", {"start": v(-175.47, 20.21) * mm, "end": v(-175.68, 20.46) * mm});
            skLineSegment(sketch, "E1130", {"start": v(-175.68, 20.46) * mm, "end": v(-175.88, 20.72) * mm});
            skLineSegment(sketch, "E1131", {"start": v(-175.88, 20.72) * mm, "end": v(-176.08, 20.98) * mm});
            skLineSegment(sketch, "E1132", {"start": v(-176.08, 20.98) * mm, "end": v(-176.27, 21.24) * mm});
            skLineSegment(sketch, "E1133", {"start": v(-176.27, 21.24) * mm, "end": v(-176.45, 21.5) * mm});
            skLineSegment(sketch, "E1134", {"start": v(-176.45, 21.5) * mm, "end": v(-176.63, 21.78) * mm});
            skLineSegment(sketch, "E1135", {"start": v(-176.63, 21.78) * mm, "end": v(-176.8, 22.05) * mm});
            skLineSegment(sketch, "E1136", {"start": v(-176.8, 22.05) * mm, "end": v(-176.96, 22.33) * mm});
            skLineSegment(sketch, "E1137", {"start": v(-176.96, 22.33) * mm, "end": v(-177.12, 22.62) * mm});
            skLineSegment(sketch, "E1138", {"start": v(-177.12, 22.62) * mm, "end": v(-177.26, 22.9) * mm});
            skLineSegment(sketch, "E1139", {"start": v(-177.26, 22.9) * mm, "end": v(-177.4, 23.2) * mm});
            skLineSegment(sketch, "E1140", {"start": v(-177.4, 23.2) * mm, "end": v(-177.54, 23.49) * mm});
            skLineSegment(sketch, "E1141", {"start": v(-177.54, 23.49) * mm, "end": v(-177.66, 23.79) * mm});
            skLineSegment(sketch, "E1142", {"start": v(-177.66, 23.79) * mm, "end": v(-177.78, 24.08) * mm});
            skLineSegment(sketch, "E1143", {"start": v(-177.78, 24.08) * mm, "end": v(-177.9, 24.39) * mm});
            skLineSegment(sketch, "E1144", {"start": v(-177.9, 24.39) * mm, "end": v(-178, 24.7) * mm});
            skLineSegment(sketch, "E1145", {"start": v(-178, 24.7) * mm, "end": v(-178.09, 25) * mm});
            skLineSegment(sketch, "E1146", {"start": v(-178.09, 25) * mm, "end": v(-178.18, 25.31) * mm});
            skLineSegment(sketch, "E1147", {"start": v(-178.18, 25.31) * mm, "end": v(-178.26, 25.62) * mm});
            skLineSegment(sketch, "E1148", {"start": v(-178.26, 25.62) * mm, "end": v(-178.33, 25.94) * mm});
            skLineSegment(sketch, "E1149", {"start": v(-178.33, 25.94) * mm, "end": v(-178.4, 26.25) * mm});
            skLineSegment(sketch, "E1150", {"start": v(-178.4, 26.25) * mm, "end": v(-178.45, 26.57) * mm});
            skLineSegment(sketch, "E1151", {"start": v(-178.45, 26.57) * mm, "end": v(-178.5, 26.89) * mm});
            skLineSegment(sketch, "E1152", {"start": v(-178.5, 26.89) * mm, "end": v(-178.54, 27.21) * mm});
            skLineSegment(sketch, "E1153", {"start": v(-178.54, 27.21) * mm, "end": v(-178.57, 27.53) * mm});
            skLineSegment(sketch, "E1154", {"start": v(-178.57, 27.53) * mm, "end": v(-178.6, 27.86) * mm});
            skLineSegment(sketch, "E1155", {"start": v(-178.6, 27.86) * mm, "end": v(-178.61, 28.18) * mm});
            skLineSegment(sketch, "E1156", {"start": v(-178.61, 28.18) * mm, "end": v(-178.62, 28.5) * mm});
            skLineSegment(sketch, "E1157", {"start": v(-178.62, 28.5) * mm, "end": v(-178.62, 28.83) * mm});
            skLineSegment(sketch, "E1158", {"start": v(-178.62, 28.83) * mm, "end": v(-178.6, 29.16) * mm});
            skLineSegment(sketch, "E1159", {"start": v(-178.6, 29.16) * mm, "end": v(-178.6, 29.48) * mm});
            skLineSegment(sketch, "E1160", {"start": v(-178.6, 29.48) * mm, "end": v(-178.6, 30.06) * mm});
            skLineSegment(sketch, "E1161", {"start": v(-178.6, 30.06) * mm, "end": v(-178.56, 30.63) * mm});
            skLineSegment(sketch, "E1162", {"start": v(-178.56, 30.63) * mm, "end": v(-178.5, 31.2) * mm});
            skLineSegment(sketch, "E1163", {"start": v(-178.5, 31.2) * mm, "end": v(-178.43, 31.76) * mm});
            skLineSegment(sketch, "E1164", {"start": v(-178.43, 31.76) * mm, "end": v(-178.32, 32.32) * mm});
            skLineSegment(sketch, "E1165", {"start": v(-178.32, 32.32) * mm, "end": v(-178.18, 32.87) * mm});
            skLineSegment(sketch, "E1166", {"start": v(-178.18, 32.87) * mm, "end": v(-178.02, 33.41) * mm});
            skLineSegment(sketch, "E1167", {"start": v(-178.02, 33.41) * mm, "end": v(-177.83, 33.95) * mm});
            skLineSegment(sketch, "E1168", {"start": v(-177.83, 33.95) * mm, "end": v(-177.62, 34.48) * mm});
            skLineSegment(sketch, "E1169", {"start": v(-177.62, 34.48) * mm, "end": v(-177.38, 35) * mm});
            skLineSegment(sketch, "E1170", {"start": v(-177.38, 35) * mm, "end": v(-177.12, 35.5) * mm});
            skLineSegment(sketch, "E1171", {"start": v(-177.12, 35.5) * mm, "end": v(-176.83, 35.99) * mm});
            skLineSegment(sketch, "E1172", {"start": v(-176.83, 35.99) * mm, "end": v(-176.52, 36.46) * mm});
            skLineSegment(sketch, "E1173", {"start": v(-176.52, 36.46) * mm, "end": v(-176.19, 36.93) * mm});
            skLineSegment(sketch, "E1174", {"start": v(-176.19, 36.93) * mm, "end": v(-175.83, 37.37) * mm});
            skLineSegment(sketch, "E1175", {"start": v(-175.83, 37.37) * mm, "end": v(-175.45, 37.8) * mm});
            skLineSegment(sketch, "E1176", {"start": v(-175.45, 37.8) * mm, "end": v(-175.16, 38.07) * mm});
            skLineSegment(sketch, "E1177", {"start": v(-175.16, 38.07) * mm, "end": v(-174.87, 38.32) * mm});
            skLineSegment(sketch, "E1178", {"start": v(-174.87, 38.32) * mm, "end": v(-174.57, 38.56) * mm});
            skLineSegment(sketch, "E1179", {"start": v(-174.57, 38.56) * mm, "end": v(-174.25, 38.78) * mm});
            skLineSegment(sketch, "E1180", {"start": v(-174.25, 38.78) * mm, "end": v(-173.94, 39) * mm});
            skLineSegment(sketch, "E1181", {"start": v(-173.94, 39) * mm, "end": v(-173.61, 39.2) * mm});
            skLineSegment(sketch, "E1182", {"start": v(-173.61, 39.2) * mm, "end": v(-173.28, 39.4) * mm});
            skLineSegment(sketch, "E1183", {"start": v(-173.28, 39.4) * mm, "end": v(-172.94, 39.59) * mm});
            skLineSegment(sketch, "E1184", {"start": v(-172.94, 39.59) * mm, "end": v(-172.6, 39.76) * mm});
            skLineSegment(sketch, "E1185", {"start": v(-172.6, 39.76) * mm, "end": v(-172.24, 39.92) * mm});
            skLineSegment(sketch, "E1186", {"start": v(-172.24, 39.92) * mm, "end": v(-171.89, 40.07) * mm});
            skLineSegment(sketch, "E1187", {"start": v(-171.89, 40.07) * mm, "end": v(-171.53, 40.2) * mm});
            skLineSegment(sketch, "E1188", {"start": v(-171.53, 40.2) * mm, "end": v(-171.16, 40.32) * mm});
            skLineSegment(sketch, "E1189", {"start": v(-171.16, 40.32) * mm, "end": v(-170.8, 40.43) * mm});
            skLineSegment(sketch, "E1190", {"start": v(-170.8, 40.43) * mm, "end": v(-170.42, 40.53) * mm});
            skLineSegment(sketch, "E1191", {"start": v(-170.42, 40.53) * mm, "end": v(-170.04, 40.62) * mm});
            skLineSegment(sketch, "E1192", {"start": v(-142.93, 48.9) * mm, "end": v(-177.88, 48.9) * mm});
            skLineSegment(sketch, "E1193", {"start": v(-142.92, 56.6) * mm, "end": v(-177.9, 56.6) * mm});
            skLineSegment(sketch, "E1194", {"start": v(-177.9, 56.6) * mm, "end": v(-177.9, 69.43) * mm});
            skLineSegment(sketch, "E1195", {"start": v(-177.9, 69.43) * mm, "end": v(-177.88, 69.73) * mm});
            skLineSegment(sketch, "E1196", {"start": v(-177.88, 69.73) * mm, "end": v(-177.86, 70.03) * mm});
            skLineSegment(sketch, "E1197", {"start": v(-177.86, 70.03) * mm, "end": v(-177.83, 70.33) * mm});
            skLineSegment(sketch, "E1198", {"start": v(-177.83, 70.33) * mm, "end": v(-177.8, 70.63) * mm});
            skLineSegment(sketch, "E1199", {"start": v(-177.8, 70.63) * mm, "end": v(-177.75, 70.93) * mm});
            skLineSegment(sketch, "E1200", {"start": v(-177.75, 70.93) * mm, "end": v(-177.7, 71.23) * mm});
            skLineSegment(sketch, "E1201", {"start": v(-177.7, 71.23) * mm, "end": v(-177.64, 71.53) * mm});
            skLineSegment(sketch, "E1202", {"start": v(-177.64, 71.53) * mm, "end": v(-177.57, 71.82) * mm});
            skLineSegment(sketch, "E1203", {"start": v(-177.57, 71.82) * mm, "end": v(-177.5, 72.1) * mm});
            skLineSegment(sketch, "E1204", {"start": v(-177.5, 72.1) * mm, "end": v(-177.41, 72.4) * mm});
            skLineSegment(sketch, "E1205", {"start": v(-177.41, 72.4) * mm, "end": v(-177.33, 72.69) * mm});
            skLineSegment(sketch, "E1206", {"start": v(-177.33, 72.69) * mm, "end": v(-177.23, 72.97) * mm});
            skLineSegment(sketch, "E1207", {"start": v(-177.23, 72.97) * mm, "end": v(-177.02, 73.53) * mm});
            skLineSegment(sketch, "E1208", {"start": v(-177.02, 73.53) * mm, "end": v(-176.78, 74.08) * mm});
            skLineSegment(sketch, "E1209", {"start": v(-176.78, 74.08) * mm, "end": v(-176.5, 74.62) * mm});
            skLineSegment(sketch, "E1210", {"start": v(-176.5, 74.62) * mm, "end": v(-176.21, 75.14) * mm});
            skLineSegment(sketch, "E1211", {"start": v(-176.21, 75.14) * mm, "end": v(-176.06, 75.4) * mm});
            skLineSegment(sketch, "E1212", {"start": v(-176.06, 75.4) * mm, "end": v(-175.9, 75.65) * mm});
            skLineSegment(sketch, "E1213", {"start": v(-175.9, 75.65) * mm, "end": v(-175.72, 75.9) * mm});
            skLineSegment(sketch, "E1214", {"start": v(-175.72, 75.9) * mm, "end": v(-175.55, 76.14) * mm});
            skLineSegment(sketch, "E1215", {"start": v(-175.55, 76.14) * mm, "end": v(-175.37, 76.38) * mm});
            skLineSegment(sketch, "E1216", {"start": v(-175.37, 76.38) * mm, "end": v(-175.18, 76.61) * mm});
            skLineSegment(sketch, "E1217", {"start": v(-175.18, 76.61) * mm, "end": v(-174.98, 76.84) * mm});
            skLineSegment(sketch, "E1218", {"start": v(-174.98, 76.84) * mm, "end": v(-174.78, 77.07) * mm});
            skLineSegment(sketch, "E1219", {"start": v(-174.78, 77.07) * mm, "end": v(-174.58, 77.29) * mm});
            skLineSegment(sketch, "E1220", {"start": v(-174.58, 77.29) * mm, "end": v(-174.36, 77.5) * mm});
            skLineSegment(sketch, "E1221", {"start": v(-174.36, 77.5) * mm, "end": v(-174.14, 77.72) * mm});
            skLineSegment(sketch, "E1222", {"start": v(-174.14, 77.72) * mm, "end": v(-173.92, 77.92) * mm});
            skLineSegment(sketch, "E1223", {"start": v(-173.92, 77.92) * mm, "end": v(-173.56, 78.27) * mm});
            skLineSegment(sketch, "E1224", {"start": v(-173.56, 78.27) * mm, "end": v(-173.2, 78.61) * mm});
            skLineSegment(sketch, "E1225", {"start": v(-173.2, 78.61) * mm, "end": v(-172.81, 78.94) * mm});
            skLineSegment(sketch, "E1226", {"start": v(-172.81, 78.94) * mm, "end": v(-172.43, 79.26) * mm});
            skLineSegment(sketch, "E1227", {"start": v(-172.43, 79.26) * mm, "end": v(-172.04, 79.57) * mm});
            skLineSegment(sketch, "E1228", {"start": v(-172.04, 79.57) * mm, "end": v(-171.64, 79.87) * mm});
            skLineSegment(sketch, "E1229", {"start": v(-171.64, 79.87) * mm, "end": v(-171.23, 80.16) * mm});
            skLineSegment(sketch, "E1230", {"start": v(-171.23, 80.16) * mm, "end": v(-170.82, 80.44) * mm});
            skLineSegment(sketch, "E1231", {"start": v(-170.82, 80.44) * mm, "end": v(-170.4, 80.7) * mm});
            skLineSegment(sketch, "E1232", {"start": v(-170.4, 80.7) * mm, "end": v(-169.98, 80.97) * mm});
            skLineSegment(sketch, "E1233", {"start": v(-169.98, 80.97) * mm, "end": v(-169.55, 81.21) * mm});
            skLineSegment(sketch, "E1234", {"start": v(-169.55, 81.21) * mm, "end": v(-169.1, 81.45) * mm});
            skLineSegment(sketch, "E1235", {"start": v(-169.1, 81.45) * mm, "end": v(-168.67, 81.67) * mm});
            skLineSegment(sketch, "E1236", {"start": v(-168.67, 81.67) * mm, "end": v(-168.22, 81.89) * mm});
            skLineSegment(sketch, "E1237", {"start": v(-168.22, 81.89) * mm, "end": v(-167.77, 82.09) * mm});
            skLineSegment(sketch, "E1238", {"start": v(-167.77, 82.09) * mm, "end": v(-167.3, 82.28) * mm});
            skLineSegment(sketch, "E1239", {"start": v(-167.3, 82.28) * mm, "end": v(-166.85, 82.46) * mm});
            skLineSegment(sketch, "E1240", {"start": v(-166.85, 82.46) * mm, "end": v(-166.38, 82.62) * mm});
            skLineSegment(sketch, "E1241", {"start": v(-166.38, 82.62) * mm, "end": v(-165.91, 82.78) * mm});
            skLineSegment(sketch, "E1242", {"start": v(-165.91, 82.78) * mm, "end": v(-165.44, 82.92) * mm});
            skLineSegment(sketch, "E1243", {"start": v(-165.44, 82.92) * mm, "end": v(-164.96, 83.06) * mm});
            skLineSegment(sketch, "E1244", {"start": v(-164.96, 83.06) * mm, "end": v(-164.48, 83.18) * mm});
            skLineSegment(sketch, "E1245", {"start": v(-164.48, 83.18) * mm, "end": v(-164, 83.29) * mm});
            skLineSegment(sketch, "E1246", {"start": v(-164, 83.29) * mm, "end": v(-163.5, 83.38) * mm});
            skLineSegment(sketch, "E1247", {"start": v(-163.5, 83.38) * mm, "end": v(-163.01, 83.47) * mm});
            skLineSegment(sketch, "E1248", {"start": v(-163.01, 83.47) * mm, "end": v(-162.52, 83.54) * mm});
            skLineSegment(sketch, "E1249", {"start": v(-162.52, 83.54) * mm, "end": v(-162.02, 83.6) * mm});
            skLineSegment(sketch, "E1250", {"start": v(-162.02, 83.6) * mm, "end": v(-161.53, 83.65) * mm});
            skLineSegment(sketch, "E1251", {"start": v(-161.53, 83.65) * mm, "end": v(-161.03, 83.68) * mm});
            skLineSegment(sketch, "E1252", {"start": v(-161.03, 83.68) * mm, "end": v(-160.53, 83.7) * mm});
            skLineSegment(sketch, "E1253", {"start": v(-160.53, 83.7) * mm, "end": v(-160.03, 83.71) * mm});
            skLineSegment(sketch, "E1254", {"start": v(-160.03, 83.71) * mm, "end": v(-159.52, 83.71) * mm});
            skLineSegment(sketch, "E1255", {"start": v(-159.52, 83.71) * mm, "end": v(-159.1, 83.72) * mm});
            skLineSegment(sketch, "E1256", {"start": v(-159.1, 83.72) * mm, "end": v(-158.68, 83.72) * mm});
            skLineSegment(sketch, "E1257", {"start": v(-158.68, 83.72) * mm, "end": v(-158.26, 83.7) * mm});
            skLineSegment(sketch, "E1258", {"start": v(-158.26, 83.7) * mm, "end": v(-157.84, 83.69) * mm});
            skLineSegment(sketch, "E1259", {"start": v(-157.84, 83.69) * mm, "end": v(-157.42, 83.66) * mm});
            skLineSegment(sketch, "E1260", {"start": v(-157.42, 83.66) * mm, "end": v(-157, 83.61) * mm});
            skLineSegment(sketch, "E1261", {"start": v(-157, 83.61) * mm, "end": v(-156.6, 83.56) * mm});
            skLineSegment(sketch, "E1262", {"start": v(-156.6, 83.56) * mm, "end": v(-156.18, 83.5) * mm});
            skLineSegment(sketch, "E1263", {"start": v(-156.18, 83.5) * mm, "end": v(-155.77, 83.43) * mm});
            skLineSegment(sketch, "E1264", {"start": v(-155.77, 83.43) * mm, "end": v(-155.36, 83.35) * mm});
            skLineSegment(sketch, "E1265", {"start": v(-155.36, 83.35) * mm, "end": v(-154.95, 83.25) * mm});
            skLineSegment(sketch, "E1266", {"start": v(-154.95, 83.25) * mm, "end": v(-154.55, 83.15) * mm});
            skLineSegment(sketch, "E1267", {"start": v(-154.55, 83.15) * mm, "end": v(-154.15, 83.04) * mm});
            skLineSegment(sketch, "E1268", {"start": v(-154.15, 83.04) * mm, "end": v(-153.75, 82.92) * mm});
            skLineSegment(sketch, "E1269", {"start": v(-153.75, 82.92) * mm, "end": v(-153.36, 82.79) * mm});
            skLineSegment(sketch, "E1270", {"start": v(-153.36, 82.79) * mm, "end": v(-152.97, 82.65) * mm});
            skLineSegment(sketch, "E1271", {"start": v(-152.97, 82.65) * mm, "end": v(-152.58, 82.5) * mm});
            skLineSegment(sketch, "E1272", {"start": v(-152.58, 82.5) * mm, "end": v(-152.2, 82.34) * mm});
            skLineSegment(sketch, "E1273", {"start": v(-152.2, 82.34) * mm, "end": v(-151.81, 82.17) * mm});
            skLineSegment(sketch, "E1274", {"start": v(-151.81, 82.17) * mm, "end": v(-151.44, 81.99) * mm});
            skLineSegment(sketch, "E1275", {"start": v(-151.44, 81.99) * mm, "end": v(-151.07, 81.8) * mm});
            skLineSegment(sketch, "E1276", {"start": v(-151.07, 81.8) * mm, "end": v(-150.7, 81.6) * mm});
            skLineSegment(sketch, "E1277", {"start": v(-150.7, 81.6) * mm, "end": v(-150.34, 81.4) * mm});
            skLineSegment(sketch, "E1278", {"start": v(-150.34, 81.4) * mm, "end": v(-149.98, 81.18) * mm});
            skLineSegment(sketch, "E1279", {"start": v(-149.98, 81.18) * mm, "end": v(-149.63, 80.96) * mm});
            skLineSegment(sketch, "E1280", {"start": v(-149.63, 80.96) * mm, "end": v(-149.28, 80.73) * mm});
            skLineSegment(sketch, "E1281", {"start": v(-149.28, 80.73) * mm, "end": v(-148.94, 80.49) * mm});
            skLineSegment(sketch, "E1282", {"start": v(-148.94, 80.49) * mm, "end": v(-148.6, 80.24) * mm});
            skLineSegment(sketch, "E1283", {"start": v(-148.6, 80.24) * mm, "end": v(-148.27, 79.98) * mm});
            skLineSegment(sketch, "E1284", {"start": v(-148.27, 79.98) * mm, "end": v(-147.95, 79.71) * mm});
            skLineSegment(sketch, "E1285", {"start": v(-147.95, 79.71) * mm, "end": v(-147.63, 79.44) * mm});
            skLineSegment(sketch, "E1286", {"start": v(-147.63, 79.44) * mm, "end": v(-147.32, 79.15) * mm});
            skLineSegment(sketch, "E1287", {"start": v(-147.32, 79.15) * mm, "end": v(-147.07, 78.91) * mm});
            skLineSegment(sketch, "E1288", {"start": v(-147.07, 78.91) * mm, "end": v(-146.83, 78.67) * mm});
            skLineSegment(sketch, "E1289", {"start": v(-146.83, 78.67) * mm, "end": v(-146.6, 78.42) * mm});
            skLineSegment(sketch, "E1290", {"start": v(-146.6, 78.42) * mm, "end": v(-146.36, 78.16) * mm});
            skLineSegment(sketch, "E1291", {"start": v(-146.36, 78.16) * mm, "end": v(-146.14, 77.9) * mm});
            skLineSegment(sketch, "E1292", {"start": v(-146.14, 77.9) * mm, "end": v(-145.92, 77.63) * mm});
            skLineSegment(sketch, "E1293", {"start": v(-145.92, 77.63) * mm, "end": v(-145.72, 77.36) * mm});
            skLineSegment(sketch, "E1294", {"start": v(-145.72, 77.36) * mm, "end": v(-145.51, 77.08) * mm});
            skLineSegment(sketch, "E1295", {"start": v(-145.51, 77.08) * mm, "end": v(-145.32, 76.8) * mm});
            skLineSegment(sketch, "E1296", {"start": v(-145.32, 76.8) * mm, "end": v(-145.13, 76.52) * mm});
            skLineSegment(sketch, "E1297", {"start": v(-145.13, 76.52) * mm, "end": v(-144.95, 76.23) * mm});
            skLineSegment(sketch, "E1298", {"start": v(-144.95, 76.23) * mm, "end": v(-144.78, 75.94) * mm});
            skLineSegment(sketch, "E1299", {"start": v(-144.78, 75.94) * mm, "end": v(-144.61, 75.64) * mm});
            skLineSegment(sketch, "E1300", {"start": v(-144.61, 75.64) * mm, "end": v(-144.45, 75.34) * mm});
            skLineSegment(sketch, "E1301", {"start": v(-144.45, 75.34) * mm, "end": v(-144.3, 75.03) * mm});
            skLineSegment(sketch, "E1302", {"start": v(-144.3, 75.03) * mm, "end": v(-144.16, 74.72) * mm});
            skLineSegment(sketch, "E1303", {"start": v(-144.16, 74.72) * mm, "end": v(-144.02, 74.41) * mm});
            skLineSegment(sketch, "E1304", {"start": v(-144.02, 74.41) * mm, "end": v(-143.9, 74.1) * mm});
            skLineSegment(sketch, "E1305", {"start": v(-143.9, 74.1) * mm, "end": v(-143.77, 73.78) * mm});
            skLineSegment(sketch, "E1306", {"start": v(-143.77, 73.78) * mm, "end": v(-143.66, 73.46) * mm});
            skLineSegment(sketch, "E1307", {"start": v(-143.66, 73.46) * mm, "end": v(-143.55, 73.13) * mm});
            skLineSegment(sketch, "E1308", {"start": v(-143.55, 73.13) * mm, "end": v(-143.45, 72.8) * mm});
            skLineSegment(sketch, "E1309", {"start": v(-143.45, 72.8) * mm, "end": v(-143.36, 72.48) * mm});
            skLineSegment(sketch, "E1310", {"start": v(-143.36, 72.48) * mm, "end": v(-143.28, 72.15) * mm});
            skLineSegment(sketch, "E1311", {"start": v(-143.28, 72.15) * mm, "end": v(-143.2, 71.81) * mm});
            skLineSegment(sketch, "E1312", {"start": v(-143.2, 71.81) * mm, "end": v(-143.14, 71.48) * mm});
            skLineSegment(sketch, "E1313", {"start": v(-143.14, 71.48) * mm, "end": v(-143.08, 71.14) * mm});
            skLineSegment(sketch, "E1314", {"start": v(-143.08, 71.14) * mm, "end": v(-143.03, 70.8) * mm});
            skLineSegment(sketch, "E1315", {"start": v(-143.03, 70.8) * mm, "end": v(-143, 70.46) * mm});
            skLineSegment(sketch, "E1316", {"start": v(-143, 70.46) * mm, "end": v(-142.96, 70.11) * mm});
            skLineSegment(sketch, "E1317", {"start": v(-142.96, 70.11) * mm, "end": v(-142.94, 69.77) * mm});
            skLineSegment(sketch, "E1318", {"start": v(-142.94, 69.77) * mm, "end": v(-142.92, 69.43) * mm});
            skLineSegment(sketch, "E1319", {"start": v(-142.92, 69.43) * mm, "end": v(-142.92, 56.6) * mm});
            skLineSegment(sketch, "E1320", {"start": v(-142.93, 114.63) * mm, "end": v(-142.93, 91.6) * mm});
            skLineSegment(sketch, "E1321", {"start": v(-142.93, 91.6) * mm, "end": v(-177.89, 91.6) * mm});
            skLineSegment(sketch, "E1322", {"start": v(-177.89, 91.6) * mm, "end": v(-177.89, 114.63) * mm});
            skLineSegment(sketch, "E1323", {"start": v(-161.04, 91.6) * mm, "end": v(-161.04, 111.75) * mm});
            skLineSegment(sketch, "E1324", {"start": v(-155.99, 122.33) * mm, "end": v(-155.99, 146.46) * mm});
            skLineSegment(sketch, "E1325", {"start": v(-142.92, 154.16) * mm, "end": v(-169.1, 154.16) * mm});
            skLineSegment(sketch, "E1326", {"start": v(-177.37, 154.16) * mm, "end": v(-177.82, 154.16) * mm});
            skLineSegment(sketch, "E1327", {"start": v(-142.92, 161.87) * mm, "end": v(-169.15, 161.87) * mm});
            skLineSegment(sketch, "E1328", {"start": v(-158.9, 161.87) * mm, "end": v(-159.47, 161.88) * mm});
            skLineSegment(sketch, "E1329", {"start": v(-159.47, 161.88) * mm, "end": v(-160.04, 161.93) * mm});
            skLineSegment(sketch, "E1330", {"start": v(-160.04, 161.93) * mm, "end": v(-160.6, 162) * mm});
            skLineSegment(sketch, "E1331", {"start": v(-160.6, 162) * mm, "end": v(-161.17, 162.1) * mm});
            skLineSegment(sketch, "E1332", {"start": v(-161.17, 162.1) * mm, "end": v(-161.72, 162.23) * mm});
            skLineSegment(sketch, "E1333", {"start": v(-161.72, 162.23) * mm, "end": v(-162.26, 162.39) * mm});
            skLineSegment(sketch, "E1334", {"start": v(-162.26, 162.39) * mm, "end": v(-162.8, 162.57) * mm});
            skLineSegment(sketch, "E1335", {"start": v(-162.8, 162.57) * mm, "end": v(-163.32, 162.78) * mm});
            skLineSegment(sketch, "E1336", {"start": v(-163.32, 162.78) * mm, "end": v(-163.84, 163.01) * mm});
            skLineSegment(sketch, "E1337", {"start": v(-163.84, 163.01) * mm, "end": v(-164.34, 163.27) * mm});
            skLineSegment(sketch, "E1338", {"start": v(-164.34, 163.27) * mm, "end": v(-164.83, 163.56) * mm});
            skLineSegment(sketch, "E1339", {"start": v(-164.83, 163.56) * mm, "end": v(-165.3, 163.87) * mm});
            skLineSegment(sketch, "E1340", {"start": v(-165.3, 163.87) * mm, "end": v(-165.76, 164.2) * mm});
            skLineSegment(sketch, "E1341", {"start": v(-165.76, 164.2) * mm, "end": v(-166.2, 164.56) * mm});
            skLineSegment(sketch, "E1342", {"start": v(-166.2, 164.56) * mm, "end": v(-166.63, 164.94) * mm});
            skLineSegment(sketch, "E1343", {"start": v(-166.63, 164.94) * mm, "end": v(-167.04, 165.34) * mm});
            skLineSegment(sketch, "E1344", {"start": v(-167.04, 165.34) * mm, "end": v(-167.37, 165.7) * mm});
            skLineSegment(sketch, "E1345", {"start": v(-167.37, 165.7) * mm, "end": v(-167.68, 166.07) * mm});
            skLineSegment(sketch, "E1346", {"start": v(-167.68, 166.07) * mm, "end": v(-167.97, 166.45) * mm});
            skLineSegment(sketch, "E1347", {"start": v(-167.97, 166.45) * mm, "end": v(-168.24, 166.84) * mm});
            skLineSegment(sketch, "E1348", {"start": v(-168.24, 166.84) * mm, "end": v(-168.5, 167.25) * mm});
            skLineSegment(sketch, "E1349", {"start": v(-168.5, 167.25) * mm, "end": v(-168.72, 167.67) * mm});
            skLineSegment(sketch, "E1350", {"start": v(-168.72, 167.67) * mm, "end": v(-168.93, 168.1) * mm});
            skLineSegment(sketch, "E1351", {"start": v(-168.93, 168.1) * mm, "end": v(-169.12, 168.54) * mm});
            skLineSegment(sketch, "E1352", {"start": v(-169.12, 168.54) * mm, "end": v(-169.28, 168.99) * mm});
            skLineSegment(sketch, "E1353", {"start": v(-169.28, 168.99) * mm, "end": v(-169.42, 169.45) * mm});
            skLineSegment(sketch, "E1354", {"start": v(-169.42, 169.45) * mm, "end": v(-169.54, 169.9) * mm});
            skLineSegment(sketch, "E1355", {"start": v(-169.54, 169.9) * mm, "end": v(-169.64, 170.38) * mm});
            skLineSegment(sketch, "E1356", {"start": v(-169.64, 170.38) * mm, "end": v(-169.71, 170.85) * mm});
            skLineSegment(sketch, "E1357", {"start": v(-169.71, 170.85) * mm, "end": v(-169.76, 171.33) * mm});
            skLineSegment(sketch, "E1358", {"start": v(-169.76, 171.33) * mm, "end": v(-169.79, 171.81) * mm});
            skLineSegment(sketch, "E1359", {"start": v(-169.79, 171.81) * mm, "end": v(-169.79, 172.3) * mm});
            skLineSegment(sketch, "E1360", {"start": v(-169.79, 172.3) * mm, "end": v(-169.82, 172.76) * mm});
            skLineSegment(sketch, "E1361", {"start": v(-169.82, 172.76) * mm, "end": v(-169.82, 173.22) * mm});
            skLineSegment(sketch, "E1362", {"start": v(-169.82, 173.22) * mm, "end": v(-169.8, 173.68) * mm});
            skLineSegment(sketch, "E1363", {"start": v(-169.8, 173.68) * mm, "end": v(-169.76, 174.13) * mm});
            skLineSegment(sketch, "E1364", {"start": v(-169.76, 174.13) * mm, "end": v(-169.7, 174.59) * mm});
            skLineSegment(sketch, "E1365", {"start": v(-169.7, 174.59) * mm, "end": v(-169.6, 175.03) * mm});
            skLineSegment(sketch, "E1366", {"start": v(-169.6, 175.03) * mm, "end": v(-169.5, 175.48) * mm});
            skLineSegment(sketch, "E1367", {"start": v(-169.5, 175.48) * mm, "end": v(-169.36, 175.91) * mm});
            skLineSegment(sketch, "E1368", {"start": v(-169.36, 175.91) * mm, "end": v(-169.2, 176.34) * mm});
            skLineSegment(sketch, "E1369", {"start": v(-169.2, 176.34) * mm, "end": v(-169.02, 176.76) * mm});
            skLineSegment(sketch, "E1370", {"start": v(-169.02, 176.76) * mm, "end": v(-168.82, 177.17) * mm});
            skLineSegment(sketch, "E1371", {"start": v(-168.82, 177.17) * mm, "end": v(-168.6, 177.57) * mm});
            skLineSegment(sketch, "E1372", {"start": v(-168.6, 177.57) * mm, "end": v(-168.36, 177.96) * mm});
            skLineSegment(sketch, "E1373", {"start": v(-168.36, 177.96) * mm, "end": v(-168.1, 178.34) * mm});
            skLineSegment(sketch, "E1374", {"start": v(-168.1, 178.34) * mm, "end": v(-167.82, 178.7) * mm});
            skLineSegment(sketch, "E1375", {"start": v(-167.82, 178.7) * mm, "end": v(-167.51, 179.05) * mm});
            skLineSegment(sketch, "E1376", {"start": v(-167.51, 179.05) * mm, "end": v(-167.26, 179.26) * mm});
            skLineSegment(sketch, "E1377", {"start": v(-167.26, 179.26) * mm, "end": v(-167, 179.47) * mm});
            skLineSegment(sketch, "E1378", {"start": v(-167, 179.47) * mm, "end": v(-166.72, 179.65) * mm});
            skLineSegment(sketch, "E1379", {"start": v(-166.72, 179.65) * mm, "end": v(-166.44, 179.83) * mm});
            skLineSegment(sketch, "E1380", {"start": v(-166.44, 179.83) * mm, "end": v(-166.15, 179.99) * mm});
            skLineSegment(sketch, "E1381", {"start": v(-166.15, 179.99) * mm, "end": v(-165.86, 180.14) * mm});
            skLineSegment(sketch, "E1382", {"start": v(-165.86, 180.14) * mm, "end": v(-165.56, 180.27) * mm});
            skLineSegment(sketch, "E1383", {"start": v(-165.56, 180.27) * mm, "end": v(-165.25, 180.4) * mm});
            skLineSegment(sketch, "E1384", {"start": v(-165.25, 180.4) * mm, "end": v(-164.94, 180.5) * mm});
            skLineSegment(sketch, "E1385", {"start": v(-164.94, 180.5) * mm, "end": v(-164.63, 180.59) * mm});
            skLineSegment(sketch, "E1386", {"start": v(-164.63, 180.59) * mm, "end": v(-164.3, 180.66) * mm});
            skLineSegment(sketch, "E1387", {"start": v(-164.3, 180.66) * mm, "end": v(-163.98, 180.72) * mm});
            skLineSegment(sketch, "E1388", {"start": v(-163.98, 180.72) * mm, "end": v(-163.66, 180.77) * mm});
            skLineSegment(sketch, "E1389", {"start": v(-163.66, 180.77) * mm, "end": v(-163.33, 180.8) * mm});
            skLineSegment(sketch, "E1390", {"start": v(-163.33, 180.8) * mm, "end": v(-163, 180.82) * mm});
            skLineSegment(sketch, "E1391", {"start": v(-163, 180.82) * mm, "end": v(-162.66, 180.82) * mm});
            skLineSegment(sketch, "E1392", {"start": v(-162.66, 180.82) * mm, "end": v(-142.92, 180.82) * mm});
            skLineSegment(sketch, "E1393", {"start": v(16.94, -163.29) * mm, "end": v(-18.02, -163.29) * mm});
            skLineSegment(sketch, "E1394", {"start": v(-18.02, -163.29) * mm, "end": v(-18.02, -147.92) * mm});
            skLineSegment(sketch, "E1395", {"start": v(-18.02, -147.92) * mm, "end": v(-18.02, -147.5) * mm});
            skLineSegment(sketch, "E1396", {"start": v(-18.02, -147.5) * mm, "end": v(-18, -147.06) * mm});
            skLineSegment(sketch, "E1397", {"start": v(-18, -147.06) * mm, "end": v(-17.95, -146.63) * mm});
            skLineSegment(sketch, "E1398", {"start": v(-17.95, -146.63) * mm, "end": v(-17.88, -146.21) * mm});
            skLineSegment(sketch, "E1399", {"start": v(-17.88, -146.21) * mm, "end": v(-17.79, -145.8) * mm});
            skLineSegment(sketch, "E1400", {"start": v(-17.79, -145.8) * mm, "end": v(-17.68, -145.38) * mm});
            skLineSegment(sketch, "E1401", {"start": v(-17.68, -145.38) * mm, "end": v(-17.54, -144.98) * mm});
            skLineSegment(sketch, "E1402", {"start": v(-17.54, -144.98) * mm, "end": v(-17.4, -144.58) * mm});
            skLineSegment(sketch, "E1403", {"start": v(-17.4, -144.58) * mm, "end": v(-17.22, -144.19) * mm});
            skLineSegment(sketch, "E1404", {"start": v(-17.22, -144.19) * mm, "end": v(-17.03, -143.8) * mm});
            skLineSegment(sketch, "E1405", {"start": v(-17.03, -143.8) * mm, "end": v(-16.82, -143.44) * mm});
            skLineSegment(sketch, "E1406", {"start": v(-16.82, -143.44) * mm, "end": v(-16.59, -143.08) * mm});
            skLineSegment(sketch, "E1407", {"start": v(-16.59, -143.08) * mm, "end": v(-16.34, -142.73) * mm});
            skLineSegment(sketch, "E1408", {"start": v(-16.34, -142.73) * mm, "end": v(-16.07, -142.4) * mm});
            skLineSegment(sketch, "E1409", {"start": v(-16.07, -142.4) * mm, "end": v(-15.79, -142.07) * mm});
            skLineSegment(sketch, "E1410", {"start": v(-15.79, -142.07) * mm, "end": v(-15.48, -141.76) * mm});
            skLineSegment(sketch, "E1411", {"start": v(-15.48, -141.76) * mm, "end": v(-15.18, -141.46) * mm});
            skLineSegment(sketch, "E1412", {"start": v(-15.18, -141.46) * mm, "end": v(-14.85, -141.18) * mm});
            skLineSegment(sketch, "E1413", {"start": v(-14.85, -141.18) * mm, "end": v(-14.52, -140.92) * mm});
            skLineSegment(sketch, "E1414", {"start": v(-14.52, -140.92) * mm, "end": v(-14.17, -140.67) * mm});
            skLineSegment(sketch, "E1415", {"start": v(-14.17, -140.67) * mm, "end": v(-13.82, -140.44) * mm});
            skLineSegment(sketch, "E1416", {"start": v(-13.82, -140.44) * mm, "end": v(-13.45, -140.23) * mm});
            skLineSegment(sketch, "E1417", {"start": v(-13.45, -140.23) * mm, "end": v(-13.07, -140.04) * mm});
            skLineSegment(sketch, "E1418", {"start": v(-13.07, -140.04) * mm, "end": v(-12.69, -139.87) * mm});
            skLineSegment(sketch, "E1419", {"start": v(-12.69, -139.87) * mm, "end": v(-12.3, -139.72) * mm});
            skLineSegment(sketch, "E1420", {"start": v(-12.3, -139.72) * mm, "end": v(-11.9, -139.58) * mm});
            skLineSegment(sketch, "E1421", {"start": v(-11.9, -139.58) * mm, "end": v(-11.49, -139.47) * mm});
            skLineSegment(sketch, "E1422", {"start": v(-11.49, -139.47) * mm, "end": v(-11.07, -139.38) * mm});
            skLineSegment(sketch, "E1423", {"start": v(-11.07, -139.38) * mm, "end": v(-10.65, -139.3) * mm});
            skLineSegment(sketch, "E1424", {"start": v(-10.65, -139.3) * mm, "end": v(-10.23, -139.25) * mm});
            skLineSegment(sketch, "E1425", {"start": v(-10.23, -139.25) * mm, "end": v(-9.8, -139.22) * mm});
            skLineSegment(sketch, "E1426", {"start": v(-9.8, -139.22) * mm, "end": v(-9.38, -139.2) * mm});
            skLineSegment(sketch, "E1427", {"start": v(-9.38, -139.2) * mm, "end": v(-8.94, -139.2) * mm});
            skLineSegment(sketch, "E1428", {"start": v(-8.94, -139.2) * mm, "end": v(-8.5, -139.23) * mm});
            skLineSegment(sketch, "E1429", {"start": v(-8.5, -139.23) * mm, "end": v(-8.07, -139.27) * mm});
            skLineSegment(sketch, "E1430", {"start": v(-8.07, -139.27) * mm, "end": v(-7.64, -139.33) * mm});
            skLineSegment(sketch, "E1431", {"start": v(-7.64, -139.33) * mm, "end": v(-7.21, -139.42) * mm});
            skLineSegment(sketch, "E1432", {"start": v(-7.21, -139.42) * mm, "end": v(-6.8, -139.52) * mm});
            skLineSegment(sketch, "E1433", {"start": v(-6.8, -139.52) * mm, "end": v(-6.38, -139.65) * mm});
            skLineSegment(sketch, "E1434", {"start": v(-6.38, -139.65) * mm, "end": v(-5.98, -139.8) * mm});
            skLineSegment(sketch, "E1435", {"start": v(-5.98, -139.8) * mm, "end": v(-5.58, -139.97) * mm});
            skLineSegment(sketch, "E1436", {"start": v(-5.58, -139.97) * mm, "end": v(-5.19, -140.16) * mm});
            skLineSegment(sketch, "E1437", {"start": v(-5.19, -140.16) * mm, "end": v(-4.8, -140.37) * mm});
            skLineSegment(sketch, "E1438", {"start": v(-4.8, -140.37) * mm, "end": v(-4.44, -140.6) * mm});
            skLineSegment(sketch, "E1439", {"start": v(-4.44, -140.6) * mm, "end": v(-4.08, -140.84) * mm});
            skLineSegment(sketch, "E1440", {"start": v(-4.08, -140.84) * mm, "end": v(-3.74, -141.1) * mm});
            skLineSegment(sketch, "E1441", {"start": v(-3.74, -141.1) * mm, "end": v(-3.4, -141.39) * mm});
            skLineSegment(sketch, "E1442", {"start": v(-3.4, -141.39) * mm, "end": v(-3.08, -141.7) * mm});
            skLineSegment(sketch, "E1443", {"start": v(-3.08, -141.7) * mm, "end": v(-2.78, -142) * mm});
            skLineSegment(sketch, "E1444", {"start": v(-2.78, -142) * mm, "end": v(-2.5, -142.33) * mm});
            skLineSegment(sketch, "E1445", {"start": v(-2.5, -142.33) * mm, "end": v(-2.23, -142.68) * mm});
            skLineSegment(sketch, "E1446", {"start": v(-2.23, -142.68) * mm, "end": v(-1.99, -143.03) * mm});
            skLineSegment(sketch, "E1447", {"start": v(-1.99, -143.03) * mm, "end": v(-1.76, -143.4) * mm});
            skLineSegment(sketch, "E1448", {"start": v(-1.76, -143.4) * mm, "end": v(-1.55, -143.77) * mm});
            skLineSegment(sketch, "E1449", {"start": v(-1.55, -143.77) * mm, "end": v(-1.35, -144.16) * mm});
            skLineSegment(sketch, "E1450", {"start": v(-1.35, -144.16) * mm, "end": v(-1.18, -144.55) * mm});
            skLineSegment(sketch, "E1451", {"start": v(-1.18, -144.55) * mm, "end": v(-1.03, -144.95) * mm});
            skLineSegment(sketch, "E1452", {"start": v(-1.03, -144.95) * mm, "end": v(-0.9, -145.36) * mm});
            skLineSegment(sketch, "E1453", {"start": v(-0.9, -145.36) * mm, "end": v(-0.79, -145.78) * mm});
            skLineSegment(sketch, "E1454", {"start": v(-0.79, -145.78) * mm, "end": v(-0.7, -146.2) * mm});
            skLineSegment(sketch, "E1455", {"start": v(-0.7, -146.2) * mm, "end": v(-0.63, -146.62) * mm});
            skLineSegment(sketch, "E1456", {"start": v(-0.63, -146.62) * mm, "end": v(-0.58, -147.05) * mm});
            skLineSegment(sketch, "E1457", {"start": v(-0.58, -147.05) * mm, "end": v(-0.55, -147.49) * mm});
            skLineSegment(sketch, "E1458", {"start": v(-0.55, -147.49) * mm, "end": v(-0.55, -147.92) * mm});
            skLineSegment(sketch, "E1459", {"start": v(-0.55, -147.92) * mm, "end": v(-0.55, -163.29) * mm});
            skLineSegment(sketch, "E1460", {"start": v(-0.55, -147.92) * mm, "end": v(-0.55, -147.56) * mm});
            skLineSegment(sketch, "E1461", {"start": v(-0.55, -147.56) * mm, "end": v(-0.53, -147.2) * mm});
            skLineSegment(sketch, "E1462", {"start": v(-0.53, -147.2) * mm, "end": v(-0.49, -146.85) * mm});
            skLineSegment(sketch, "E1463", {"start": v(-0.49, -146.85) * mm, "end": v(-0.43, -146.5) * mm});
            skLineSegment(sketch, "E1464", {"start": v(-0.43, -146.5) * mm, "end": v(-0.36, -146.16) * mm});
            skLineSegment(sketch, "E1465", {"start": v(-0.36, -146.16) * mm, "end": v(-0.27, -145.82) * mm});
            skLineSegment(sketch, "E1466", {"start": v(-0.27, -145.82) * mm, "end": v(-0.16, -145.48) * mm});
            skLineSegment(sketch, "E1467", {"start": v(-0.16, -145.48) * mm, "end": v(-0.03, -145.15) * mm});
            skLineSegment(sketch, "E1468", {"start": v(-0.03, -145.15) * mm, "end": v(0.1, -144.82) * mm});
            skLineSegment(sketch, "E1469", {"start": v(0.1, -144.82) * mm, "end": v(0.27, -144.5) * mm});
            skLineSegment(sketch, "E1470", {"start": v(0.27, -144.5) * mm, "end": v(0.44, -144.2) * mm});
            skLineSegment(sketch, "E1471", {"start": v(0.44, -144.2) * mm, "end": v(0.63, -143.9) * mm});
            skLineSegment(sketch, "E1472", {"start": v(0.63, -143.9) * mm, "end": v(0.83, -143.61) * mm});
            skLineSegment(sketch, "E1473", {"start": v(0.83, -143.61) * mm, "end": v(1.05, -143.33) * mm});
            skLineSegment(sketch, "E1474", {"start": v(1.05, -143.33) * mm, "end": v(1.29, -143.06) * mm});
            skLineSegment(sketch, "E1475", {"start": v(1.29, -143.06) * mm, "end": v(1.54, -142.8) * mm});
            skLineSegment(sketch, "E1476", {"start": v(1.54, -142.8) * mm, "end": v(1.98, -142.5) * mm});
            skLineSegment(sketch, "E1477", {"start": v(1.98, -142.5) * mm, "end": v(2.42, -142.23) * mm});
            skLineSegment(sketch, "E1478", {"start": v(2.42, -142.23) * mm, "end": v(2.88, -141.97) * mm});
            skLineSegment(sketch, "E1479", {"start": v(2.88, -141.97) * mm, "end": v(3.35, -141.74) * mm});
            skLineSegment(sketch, "E1480", {"start": v(3.35, -141.74) * mm, "end": v(3.83, -141.52) * mm});
            skLineSegment(sketch, "E1481", {"start": v(3.83, -141.52) * mm, "end": v(4.32, -141.33) * mm});
            skLineSegment(sketch, "E1482", {"start": v(4.32, -141.33) * mm, "end": v(4.82, -141.16) * mm});
            skLineSegment(sketch, "E1483", {"start": v(4.82, -141.16) * mm, "end": v(5.32, -141.01) * mm});
            skLineSegment(sketch, "E1484", {"start": v(5.32, -141.01) * mm, "end": v(5.83, -140.89) * mm});
            skLineSegment(sketch, "E1485", {"start": v(5.83, -140.89) * mm, "end": v(6.34, -140.78) * mm});
            skLineSegment(sketch, "E1486", {"start": v(6.34, -140.78) * mm, "end": v(6.86, -140.7) * mm});
            skLineSegment(sketch, "E1487", {"start": v(6.86, -140.7) * mm, "end": v(7.38, -140.64) * mm});
            skLineSegment(sketch, "E1488", {"start": v(7.38, -140.64) * mm, "end": v(7.9, -140.61) * mm});
            skLineSegment(sketch, "E1489", {"start": v(7.9, -140.61) * mm, "end": v(8.43, -140.6) * mm});
            skLineSegment(sketch, "E1490", {"start": v(8.43, -140.6) * mm, "end": v(8.96, -140.61) * mm});
            skLineSegment(sketch, "E1491", {"start": v(8.96, -140.61) * mm, "end": v(9.49, -140.65) * mm});
            skLineSegment(sketch, "E1492", {"start": v(9.49, -140.65) * mm, "end": v(9.96, -140.66) * mm});
            skLineSegment(sketch, "E1493", {"start": v(9.96, -140.66) * mm, "end": v(10.43, -140.66) * mm});
            skLineSegment(sketch, "E1494", {"start": v(10.43, -140.66) * mm, "end": v(10.9, -140.65) * mm});
            skLineSegment(sketch, "E1495", {"start": v(10.9, -140.65) * mm, "end": v(11.37, -140.63) * mm});
            skLineSegment(sketch, "E1496", {"start": v(11.37, -140.63) * mm, "end": v(11.84, -140.6) * mm});
            skLineSegment(sketch, "E1497", {"start": v(11.84, -140.6) * mm, "end": v(12.31, -140.56) * mm});
            skLineSegment(sketch, "E1498", {"start": v(12.31, -140.56) * mm, "end": v(12.78, -140.52) * mm});
            skLineSegment(sketch, "E1499", {"start": v(12.78, -140.52) * mm, "end": v(13.25, -140.47) * mm});
            skLineSegment(sketch, "E1500", {"start": v(13.25, -140.47) * mm, "end": v(13.72, -140.4) * mm});
            skLineSegment(sketch, "E1501", {"start": v(13.72, -140.4) * mm, "end": v(14.18, -140.34) * mm});
            skLineSegment(sketch, "E1502", {"start": v(14.18, -140.34) * mm, "end": v(14.65, -140.26) * mm});
            skLineSegment(sketch, "E1503", {"start": v(14.65, -140.26) * mm, "end": v(15.1, -140.17) * mm});
            skLineSegment(sketch, "E1504", {"start": v(15.1, -140.17) * mm, "end": v(15.57, -140.08) * mm});
            skLineSegment(sketch, "E1505", {"start": v(15.57, -140.08) * mm, "end": v(16.03, -139.98) * mm});
            skLineSegment(sketch, "E1506", {"start": v(16.03, -139.98) * mm, "end": v(16.49, -139.87) * mm});
            skLineSegment(sketch, "E1507", {"start": v(16.49, -139.87) * mm, "end": v(16.94, -139.75) * mm});
            skLineSegment(sketch, "E1508", {"start": v(17.43, -117.08) * mm, "end": v(17.44, -117.45) * mm});
            skLineSegment(sketch, "E1509", {"start": v(17.44, -117.45) * mm, "end": v(17.43, -117.82) * mm});
            skLineSegment(sketch, "E1510", {"start": v(17.43, -117.82) * mm, "end": v(17.41, -118.18) * mm});
            skLineSegment(sketch, "E1511", {"start": v(17.41, -118.18) * mm, "end": v(17.39, -118.55) * mm});
            skLineSegment(sketch, "E1512", {"start": v(17.39, -118.55) * mm, "end": v(17.36, -118.9) * mm});
            skLineSegment(sketch, "E1513", {"start": v(17.36, -118.9) * mm, "end": v(17.31, -119.27) * mm});
            skLineSegment(sketch, "E1514", {"start": v(17.31, -119.27) * mm, "end": v(17.26, -119.63) * mm});
            skLineSegment(sketch, "E1515", {"start": v(17.26, -119.63) * mm, "end": v(17.2, -119.99) * mm});
            skLineSegment(sketch, "E1516", {"start": v(17.2, -119.99) * mm, "end": v(17.13, -120.35) * mm});
            skLineSegment(sketch, "E1517", {"start": v(17.13, -120.35) * mm, "end": v(17.05, -120.7) * mm});
            skLineSegment(sketch, "E1518", {"start": v(17.05, -120.7) * mm, "end": v(16.96, -121.05) * mm});
            skLineSegment(sketch, "E1519", {"start": v(16.96, -121.05) * mm, "end": v(16.87, -121.4) * mm});
            skLineSegment(sketch, "E1520", {"start": v(16.87, -121.4) * mm, "end": v(16.76, -121.75) * mm});
            skLineSegment(sketch, "E1521", {"start": v(16.76, -121.75) * mm, "end": v(16.65, -122.1) * mm});
            skLineSegment(sketch, "E1522", {"start": v(16.65, -122.1) * mm, "end": v(16.53, -122.43) * mm});
            skLineSegment(sketch, "E1523", {"start": v(16.53, -122.43) * mm, "end": v(16.4, -122.77) * mm});
            skLineSegment(sketch, "E1524", {"start": v(16.4, -122.77) * mm, "end": v(16.26, -123.1) * mm});
            skLineSegment(sketch, "E1525", {"start": v(16.26, -123.1) * mm, "end": v(16.12, -123.44) * mm});
            skLineSegment(sketch, "E1526", {"start": v(16.12, -123.44) * mm, "end": v(15.96, -123.76) * mm});
            skLineSegment(sketch, "E1527", {"start": v(15.96, -123.76) * mm, "end": v(15.8, -124.09) * mm});
            skLineSegment(sketch, "E1528", {"start": v(15.8, -124.09) * mm, "end": v(15.63, -124.4) * mm});
            skLineSegment(sketch, "E1529", {"start": v(15.63, -124.4) * mm, "end": v(15.45, -124.72) * mm});
            skLineSegment(sketch, "E1530", {"start": v(15.45, -124.72) * mm, "end": v(15.26, -125.03) * mm});
            skLineSegment(sketch, "E1531", {"start": v(15.26, -125.03) * mm, "end": v(15.07, -125.34) * mm});
            skLineSegment(sketch, "E1532", {"start": v(15.07, -125.34) * mm, "end": v(14.87, -125.64) * mm});
            skLineSegment(sketch, "E1533", {"start": v(14.87, -125.64) * mm, "end": v(14.66, -125.94) * mm});
            skLineSegment(sketch, "E1534", {"start": v(14.66, -125.94) * mm, "end": v(14.44, -126.23) * mm});
            skLineSegment(sketch, "E1535", {"start": v(14.44, -126.23) * mm, "end": v(14.21, -126.52) * mm});
            skLineSegment(sketch, "E1536", {"start": v(14.21, -126.52) * mm, "end": v(13.98, -126.8) * mm});
            skLineSegment(sketch, "E1537", {"start": v(13.98, -126.8) * mm, "end": v(13.74, -127.08) * mm});
            skLineSegment(sketch, "E1538", {"start": v(13.74, -127.08) * mm, "end": v(13.5, -127.35) * mm});
            skLineSegment(sketch, "E1539", {"start": v(13.5, -127.35) * mm, "end": v(13.24, -127.61) * mm});
            skLineSegment(sketch, "E1540", {"start": v(13.24, -127.61) * mm, "end": v(12.9, -127.92) * mm});
            skLineSegment(sketch, "E1541", {"start": v(12.9, -127.92) * mm, "end": v(12.57, -128.21) * mm});
            skLineSegment(sketch, "E1542", {"start": v(12.57, -128.21) * mm, "end": v(12.22, -128.5) * mm});
            skLineSegment(sketch, "E1543", {"start": v(12.22, -128.5) * mm, "end": v(11.87, -128.78) * mm});
            skLineSegment(sketch, "E1544", {"start": v(11.87, -128.78) * mm, "end": v(11.5, -129.05) * mm});
            skLineSegment(sketch, "E1545", {"start": v(11.5, -129.05) * mm, "end": v(11.14, -129.31) * mm});
            skLineSegment(sketch, "E1546", {"start": v(11.14, -129.31) * mm, "end": v(10.77, -129.56) * mm});
            skLineSegment(sketch, "E1547", {"start": v(10.77, -129.56) * mm, "end": v(10.4, -129.8) * mm});
            skLineSegment(sketch, "E1548", {"start": v(10.4, -129.8) * mm, "end": v(10.01, -130.03) * mm});
            skLineSegment(sketch, "E1549", {"start": v(10.01, -130.03) * mm, "end": v(9.62, -130.26) * mm});
            skLineSegment(sketch, "E1550", {"start": v(9.62, -130.26) * mm, "end": v(9.23, -130.47) * mm});
            skLineSegment(sketch, "E1551", {"start": v(9.23, -130.47) * mm, "end": v(8.83, -130.67) * mm});
            skLineSegment(sketch, "E1552", {"start": v(8.83, -130.67) * mm, "end": v(8.43, -130.86) * mm});
            skLineSegment(sketch, "E1553", {"start": v(8.43, -130.86) * mm, "end": v(8.02, -131.05) * mm});
            skLineSegment(sketch, "E1554", {"start": v(8.02, -131.05) * mm, "end": v(7.61, -131.22) * mm});
            skLineSegment(sketch, "E1555", {"start": v(7.61, -131.22) * mm, "end": v(7.2, -131.38) * mm});
            skLineSegment(sketch, "E1556", {"start": v(7.2, -131.38) * mm, "end": v(6.78, -131.53) * mm});
            skLineSegment(sketch, "E1557", {"start": v(6.78, -131.53) * mm, "end": v(6.36, -131.67) * mm});
            skLineSegment(sketch, "E1558", {"start": v(6.36, -131.67) * mm, "end": v(5.93, -131.8) * mm});
            skLineSegment(sketch, "E1559", {"start": v(5.93, -131.8) * mm, "end": v(5.5, -131.93) * mm});
            skLineSegment(sketch, "E1560", {"start": v(5.5, -131.93) * mm, "end": v(5.07, -132.04) * mm});
            skLineSegment(sketch, "E1561", {"start": v(5.07, -132.04) * mm, "end": v(4.63, -132.14) * mm});
            skLineSegment(sketch, "E1562", {"start": v(4.63, -132.14) * mm, "end": v(4.2, -132.23) * mm});
            skLineSegment(sketch, "E1563", {"start": v(4.2, -132.23) * mm, "end": v(3.76, -132.3) * mm});
            skLineSegment(sketch, "E1564", {"start": v(3.76, -132.3) * mm, "end": v(3.31, -132.37) * mm});
            skLineSegment(sketch, "E1565", {"start": v(3.31, -132.37) * mm, "end": v(2.87, -132.43) * mm});
            skLineSegment(sketch, "E1566", {"start": v(2.87, -132.43) * mm, "end": v(2.42, -132.47) * mm});
            skLineSegment(sketch, "E1567", {"start": v(2.42, -132.47) * mm, "end": v(1.98, -132.5) * mm});
            skLineSegment(sketch, "E1568", {"start": v(1.98, -132.5) * mm, "end": v(1.53, -132.53) * mm});
            skLineSegment(sketch, "E1569", {"start": v(1.53, -132.53) * mm, "end": v(1.08, -132.54) * mm});
            skLineSegment(sketch, "E1570", {"start": v(1.08, -132.54) * mm, "end": v(0.63, -132.55) * mm});
            skLineSegment(sketch, "E1571", {"start": v(0.63, -132.55) * mm, "end": v(0.17, -132.53) * mm});
            skLineSegment(sketch, "E1572", {"start": v(0.17, -132.53) * mm, "end": v(-0.32, -132.55) * mm});
            skLineSegment(sketch, "E1573", {"start": v(-0.32, -132.55) * mm, "end": v(-0.8, -132.55) * mm});
            skLineSegment(sketch, "E1574", {"start": v(-0.8, -132.55) * mm, "end": v(-1.3, -132.54) * mm});
            skLineSegment(sketch, "E1575", {"start": v(-1.3, -132.54) * mm, "end": v(-1.78, -132.52) * mm});
            skLineSegment(sketch, "E1576", {"start": v(-1.78, -132.52) * mm, "end": v(-2.27, -132.48) * mm});
            skLineSegment(sketch, "E1577", {"start": v(-2.27, -132.48) * mm, "end": v(-2.76, -132.43) * mm});
            skLineSegment(sketch, "E1578", {"start": v(-2.76, -132.43) * mm, "end": v(-3.24, -132.37) * mm});
            skLineSegment(sketch, "E1579", {"start": v(-3.24, -132.37) * mm, "end": v(-3.72, -132.3) * mm});
            skLineSegment(sketch, "E1580", {"start": v(-3.72, -132.3) * mm, "end": v(-4.2, -132.22) * mm});
            skLineSegment(sketch, "E1581", {"start": v(-4.2, -132.22) * mm, "end": v(-4.67, -132.12) * mm});
            skLineSegment(sketch, "E1582", {"start": v(-4.67, -132.12) * mm, "end": v(-5.14, -132.02) * mm});
            skLineSegment(sketch, "E1583", {"start": v(-5.14, -132.02) * mm, "end": v(-5.61, -131.9) * mm});
            skLineSegment(sketch, "E1584", {"start": v(-5.61, -131.9) * mm, "end": v(-6.08, -131.77) * mm});
            skLineSegment(sketch, "E1585", {"start": v(-6.08, -131.77) * mm, "end": v(-6.54, -131.62) * mm});
            skLineSegment(sketch, "E1586", {"start": v(-6.54, -131.62) * mm, "end": v(-7, -131.47) * mm});
            skLineSegment(sketch, "E1587", {"start": v(-7, -131.47) * mm, "end": v(-7.46, -131.3) * mm});
            skLineSegment(sketch, "E1588", {"start": v(-7.46, -131.3) * mm, "end": v(-7.9, -131.13) * mm});
            skLineSegment(sketch, "E1589", {"start": v(-7.9, -131.13) * mm, "end": v(-8.35, -130.94) * mm});
            skLineSegment(sketch, "E1590", {"start": v(-8.35, -130.94) * mm, "end": v(-8.8, -130.75) * mm});
            skLineSegment(sketch, "E1591", {"start": v(-8.8, -130.75) * mm, "end": v(-9.23, -130.54) * mm});
            skLineSegment(sketch, "E1592", {"start": v(-9.23, -130.54) * mm, "end": v(-9.66, -130.32) * mm});
            skLineSegment(sketch, "E1593", {"start": v(-9.66, -130.32) * mm, "end": v(-10.1, -130.09) * mm});
            skLineSegment(sketch, "E1594", {"start": v(-10.1, -130.09) * mm, "end": v(-10.51, -129.85) * mm});
            skLineSegment(sketch, "E1595", {"start": v(-10.51, -129.85) * mm, "end": v(-10.93, -129.6) * mm});
            skLineSegment(sketch, "E1596", {"start": v(-10.93, -129.6) * mm, "end": v(-11.33, -129.33) * mm});
            skLineSegment(sketch, "E1597", {"start": v(-11.33, -129.33) * mm, "end": v(-11.74, -129.06) * mm});
            skLineSegment(sketch, "E1598", {"start": v(-11.74, -129.06) * mm, "end": v(-12.13, -128.77) * mm});
            skLineSegment(sketch, "E1599", {"start": v(-12.13, -128.77) * mm, "end": v(-12.52, -128.48) * mm});
            skLineSegment(sketch, "E1600", {"start": v(-12.52, -128.48) * mm, "end": v(-12.9, -128.18) * mm});
            skLineSegment(sketch, "E1601", {"start": v(-12.9, -128.18) * mm, "end": v(-13.28, -127.86) * mm});
            skLineSegment(sketch, "E1602", {"start": v(-13.28, -127.86) * mm, "end": v(-13.65, -127.54) * mm});
            skLineSegment(sketch, "E1603", {"start": v(-13.65, -127.54) * mm, "end": v(-14, -127.2) * mm});
            skLineSegment(sketch, "E1604", {"start": v(-14, -127.2) * mm, "end": v(-14.26, -126.96) * mm});
            skLineSegment(sketch, "E1605", {"start": v(-14.26, -126.96) * mm, "end": v(-14.5, -126.7) * mm});
            skLineSegment(sketch, "E1606", {"start": v(-14.5, -126.7) * mm, "end": v(-14.75, -126.44) * mm});
            skLineSegment(sketch, "E1607", {"start": v(-14.75, -126.44) * mm, "end": v(-14.98, -126.17) * mm});
            skLineSegment(sketch, "E1608", {"start": v(-14.98, -126.17) * mm, "end": v(-15.2, -125.9) * mm});
            skLineSegment(sketch, "E1609", {"start": v(-15.2, -125.9) * mm, "end": v(-15.43, -125.62) * mm});
            skLineSegment(sketch, "E1610", {"start": v(-15.43, -125.62) * mm, "end": v(-15.64, -125.34) * mm});
            skLineSegment(sketch, "E1611", {"start": v(-15.64, -125.34) * mm, "end": v(-15.84, -125.05) * mm});
            skLineSegment(sketch, "E1612", {"start": v(-15.84, -125.05) * mm, "end": v(-16.03, -124.75) * mm});
            skLineSegment(sketch, "E1613", {"start": v(-16.03, -124.75) * mm, "end": v(-16.22, -124.46) * mm});
            skLineSegment(sketch, "E1614", {"start": v(-16.22, -124.46) * mm, "end": v(-16.4, -124.15) * mm});
            skLineSegment(sketch, "E1615", {"start": v(-16.4, -124.15) * mm, "end": v(-16.57, -123.85) * mm});
            skLineSegment(sketch, "E1616", {"start": v(-16.57, -123.85) * mm, "end": v(-16.73, -123.54) * mm});
            skLineSegment(sketch, "E1617", {"start": v(-16.73, -123.54) * mm, "end": v(-16.89, -123.22) * mm});
            skLineSegment(sketch, "E1618", {"start": v(-16.89, -123.22) * mm, "end": v(-17.04, -122.9) * mm});
            skLineSegment(sketch, "E1619", {"start": v(-17.04, -122.9) * mm, "end": v(-17.18, -122.58) * mm});
            skLineSegment(sketch, "E1620", {"start": v(-17.18, -122.58) * mm, "end": v(-17.3, -122.25) * mm});
            skLineSegment(sketch, "E1621", {"start": v(-17.3, -122.25) * mm, "end": v(-17.43, -121.93) * mm});
            skLineSegment(sketch, "E1622", {"start": v(-17.43, -121.93) * mm, "end": v(-17.54, -121.6) * mm});
            skLineSegment(sketch, "E1623", {"start": v(-17.54, -121.6) * mm, "end": v(-17.65, -121.26) * mm});
            skLineSegment(sketch, "E1624", {"start": v(-17.65, -121.26) * mm, "end": v(-17.75, -120.92) * mm});
            skLineSegment(sketch, "E1625", {"start": v(-17.75, -120.92) * mm, "end": v(-17.84, -120.58) * mm});
            skLineSegment(sketch, "E1626", {"start": v(-17.84, -120.58) * mm, "end": v(-17.91, -120.24) * mm});
            skLineSegment(sketch, "E1627", {"start": v(-17.91, -120.24) * mm, "end": v(-17.99, -119.9) * mm});
            skLineSegment(sketch, "E1628", {"start": v(-17.99, -119.9) * mm, "end": v(-18.05, -119.55) * mm});
            skLineSegment(sketch, "E1629", {"start": v(-18.05, -119.55) * mm, "end": v(-18.1, -119.2) * mm});
            skLineSegment(sketch, "E1630", {"start": v(-18.1, -119.2) * mm, "end": v(-18.15, -118.85) * mm});
            skLineSegment(sketch, "E1631", {"start": v(-18.15, -118.85) * mm, "end": v(-18.18, -118.5) * mm});
            skLineSegment(sketch, "E1632", {"start": v(-18.18, -118.5) * mm, "end": v(-18.2, -118.14) * mm});
            skLineSegment(sketch, "E1633", {"start": v(-18.2, -118.14) * mm, "end": v(-18.23, -117.79) * mm});
            skLineSegment(sketch, "E1634", {"start": v(-18.23, -117.79) * mm, "end": v(-18.23, -117.43) * mm});
            skLineSegment(sketch, "E1635", {"start": v(-18.23, -117.43) * mm, "end": v(-18.23, -117.07) * mm});
            skLineSegment(sketch, "E1636", {"start": v(-18.23, -117.07) * mm, "end": v(-18.23, -116.71) * mm});
            skLineSegment(sketch, "E1637", {"start": v(-18.23, -116.71) * mm, "end": v(-18.22, -116.35) * mm});
            skLineSegment(sketch, "E1638", {"start": v(-18.22, -116.35) * mm, "end": v(-18.2, -116) * mm});
            skLineSegment(sketch, "E1639", {"start": v(-18.2, -116) * mm, "end": v(-18.16, -115.63) * mm});
            skLineSegment(sketch, "E1640", {"start": v(-18.16, -115.63) * mm, "end": v(-18.12, -115.27) * mm});
            skLineSegment(sketch, "E1641", {"start": v(-18.12, -115.27) * mm, "end": v(-18.07, -114.92) * mm});
            skLineSegment(sketch, "E1642", {"start": v(-18.07, -114.92) * mm, "end": v(-18.01, -114.56) * mm});
            skLineSegment(sketch, "E1643", {"start": v(-18.01, -114.56) * mm, "end": v(-17.95, -114.21) * mm});
            skLineSegment(sketch, "E1644", {"start": v(-17.95, -114.21) * mm, "end": v(-17.87, -113.86) * mm});
            skLineSegment(sketch, "E1645", {"start": v(-17.87, -113.86) * mm, "end": v(-17.78, -113.52) * mm});
            skLineSegment(sketch, "E1646", {"start": v(-17.78, -113.52) * mm, "end": v(-17.69, -113.17) * mm});
            skLineSegment(sketch, "E1647", {"start": v(-17.69, -113.17) * mm, "end": v(-17.59, -112.83) * mm});
            skLineSegment(sketch, "E1648", {"start": v(-17.59, -112.83) * mm, "end": v(-17.47, -112.49) * mm});
            skLineSegment(sketch, "E1649", {"start": v(-17.47, -112.49) * mm, "end": v(-17.35, -112.15) * mm});
            skLineSegment(sketch, "E1650", {"start": v(-17.35, -112.15) * mm, "end": v(-17.23, -111.82) * mm});
            skLineSegment(sketch, "E1651", {"start": v(-17.23, -111.82) * mm, "end": v(-17.09, -111.5) * mm});
            skLineSegment(sketch, "E1652", {"start": v(-17.09, -111.5) * mm, "end": v(-16.94, -111.17) * mm});
            skLineSegment(sketch, "E1653", {"start": v(-16.94, -111.17) * mm, "end": v(-16.79, -110.84) * mm});
            skLineSegment(sketch, "E1654", {"start": v(-16.79, -110.84) * mm, "end": v(-16.63, -110.53) * mm});
            skLineSegment(sketch, "E1655", {"start": v(-16.63, -110.53) * mm, "end": v(-16.46, -110.21) * mm});
            skLineSegment(sketch, "E1656", {"start": v(-16.46, -110.21) * mm, "end": v(-16.28, -109.9) * mm});
            skLineSegment(sketch, "E1657", {"start": v(-16.28, -109.9) * mm, "end": v(-16.1, -109.6) * mm});
            skLineSegment(sketch, "E1658", {"start": v(-16.1, -109.6) * mm, "end": v(-15.9, -109.3) * mm});
            skLineSegment(sketch, "E1659", {"start": v(-15.9, -109.3) * mm, "end": v(-15.7, -109) * mm});
            skLineSegment(sketch, "E1660", {"start": v(-15.7, -109) * mm, "end": v(-15.49, -108.7) * mm});
            skLineSegment(sketch, "E1661", {"start": v(-15.49, -108.7) * mm, "end": v(-15.27, -108.42) * mm});
            skLineSegment(sketch, "E1662", {"start": v(-15.27, -108.42) * mm, "end": v(-15.05, -108.14) * mm});
            skLineSegment(sketch, "E1663", {"start": v(-15.05, -108.14) * mm, "end": v(-14.81, -107.87) * mm});
            skLineSegment(sketch, "E1664", {"start": v(-14.81, -107.87) * mm, "end": v(-14.58, -107.6) * mm});
            skLineSegment(sketch, "E1665", {"start": v(-14.58, -107.6) * mm, "end": v(-14.33, -107.34) * mm});
            skLineSegment(sketch, "E1666", {"start": v(-14.33, -107.34) * mm, "end": v(-14.07, -107.08) * mm});
            skLineSegment(sketch, "E1667", {"start": v(-14.07, -107.08) * mm, "end": v(-13.81, -106.83) * mm});
            skLineSegment(sketch, "E1668", {"start": v(-13.81, -106.83) * mm, "end": v(-13.45, -106.5) * mm});
            skLineSegment(sketch, "E1669", {"start": v(-13.45, -106.5) * mm, "end": v(-13.09, -106.2) * mm});
            skLineSegment(sketch, "E1670", {"start": v(-13.09, -106.2) * mm, "end": v(-12.72, -105.89) * mm});
            skLineSegment(sketch, "E1671", {"start": v(-12.72, -105.89) * mm, "end": v(-12.34, -105.6) * mm});
            skLineSegment(sketch, "E1672", {"start": v(-12.34, -105.6) * mm, "end": v(-11.95, -105.3) * mm});
            skLineSegment(sketch, "E1673", {"start": v(-11.95, -105.3) * mm, "end": v(-11.56, -105.03) * mm});
            skLineSegment(sketch, "E1674", {"start": v(-11.56, -105.03) * mm, "end": v(-11.16, -104.77) * mm});
            skLineSegment(sketch, "E1675", {"start": v(-11.16, -104.77) * mm, "end": v(-10.75, -104.52) * mm});
            skLineSegment(sketch, "E1676", {"start": v(-10.75, -104.52) * mm, "end": v(-10.34, -104.27) * mm});
            skLineSegment(sketch, "E1677", {"start": v(-10.34, -104.27) * mm, "end": v(-9.93, -104.04) * mm});
            skLineSegment(sketch, "E1678", {"start": v(-9.93, -104.04) * mm, "end": v(-9.5, -103.82) * mm});
            skLineSegment(sketch, "E1679", {"start": v(-9.5, -103.82) * mm, "end": v(-9.08, -103.6) * mm});
            skLineSegment(sketch, "E1680", {"start": v(-9.08, -103.6) * mm, "end": v(-8.64, -103.4) * mm});
            skLineSegment(sketch, "E1681", {"start": v(-8.64, -103.4) * mm, "end": v(-8.2, -103.22) * mm});
            skLineSegment(sketch, "E1682", {"start": v(-8.2, -103.22) * mm, "end": v(-7.77, -103.04) * mm});
            skLineSegment(sketch, "E1683", {"start": v(-7.77, -103.04) * mm, "end": v(-7.32, -102.87) * mm});
            skLineSegment(sketch, "E1684", {"start": v(-7.32, -102.87) * mm, "end": v(-6.87, -102.7) * mm});
            skLineSegment(sketch, "E1685", {"start": v(-6.87, -102.7) * mm, "end": v(-6.42, -102.56) * mm});
            skLineSegment(sketch, "E1686", {"start": v(-6.42, -102.56) * mm, "end": v(-5.96, -102.43) * mm});
            skLineSegment(sketch, "E1687", {"start": v(-5.96, -102.43) * mm, "end": v(-5.5, -102.3) * mm});
            skLineSegment(sketch, "E1688", {"start": v(-5.5, -102.3) * mm, "end": v(-5.04, -102.2) * mm});
            skLineSegment(sketch, "E1689", {"start": v(-5.04, -102.2) * mm, "end": v(-4.57, -102.1) * mm});
            skLineSegment(sketch, "E1690", {"start": v(-4.57, -102.1) * mm, "end": v(-4.1, -102) * mm});
            skLineSegment(sketch, "E1691", {"start": v(-4.1, -102) * mm, "end": v(-3.64, -101.92) * mm});
            skLineSegment(sketch, "E1692", {"start": v(-3.64, -101.92) * mm, "end": v(-3.16, -101.86) * mm});
            skLineSegment(sketch, "E1693", {"start": v(-3.16, -101.86) * mm, "end": v(-2.69, -101.8) * mm});
            skLineSegment(sketch, "E1694", {"start": v(-2.69, -101.8) * mm, "end": v(-2.2, -101.76) * mm});
            skLineSegment(sketch, "E1695", {"start": v(-2.2, -101.76) * mm, "end": v(-1.73, -101.73) * mm});
            skLineSegment(sketch, "E1696", {"start": v(-1.73, -101.73) * mm, "end": v(-1.25, -101.7) * mm});
            skLineSegment(sketch, "E1697", {"start": v(-1.25, -101.7) * mm, "end": v(-0.77, -101.7) * mm});
            skLineSegment(sketch, "E1698", {"start": v(-0.77, -101.7) * mm, "end": v(-0.29, -101.7) * mm});
            skLineSegment(sketch, "E1699", {"start": v(-0.29, -101.7) * mm, "end": v(0.2, -101.72) * mm});
            skLineSegment(sketch, "E1700", {"start": v(0.2, -101.72) * mm, "end": v(0.65, -101.72) * mm});
            skLineSegment(sketch, "E1701", {"start": v(0.65, -101.72) * mm, "end": v(1.1, -101.72) * mm});
            skLineSegment(sketch, "E1702", {"start": v(1.1, -101.72) * mm, "end": v(1.54, -101.74) * mm});
            skLineSegment(sketch, "E1703", {"start": v(1.54, -101.74) * mm, "end": v(2, -101.76) * mm});
            skLineSegment(sketch, "E1704", {"start": v(2, -101.76) * mm, "end": v(2.44, -101.8) * mm});
            skLineSegment(sketch, "E1705", {"start": v(2.44, -101.8) * mm, "end": v(2.88, -101.85) * mm});
            skLineSegment(sketch, "E1706", {"start": v(2.88, -101.85) * mm, "end": v(3.32, -101.9) * mm});
            skLineSegment(sketch, "E1707", {"start": v(3.32, -101.9) * mm, "end": v(3.76, -101.98) * mm});
            skLineSegment(sketch, "E1708", {"start": v(3.76, -101.98) * mm, "end": v(4.2, -102.06) * mm});
            skLineSegment(sketch, "E1709", {"start": v(4.2, -102.06) * mm, "end": v(4.64, -102.15) * mm});
            skLineSegment(sketch, "E1710", {"start": v(4.64, -102.15) * mm, "end": v(5.07, -102.26) * mm});
            skLineSegment(sketch, "E1711", {"start": v(5.07, -102.26) * mm, "end": v(5.5, -102.37) * mm});
            skLineSegment(sketch, "E1712", {"start": v(5.5, -102.37) * mm, "end": v(5.92, -102.5) * mm});
            skLineSegment(sketch, "E1713", {"start": v(5.92, -102.5) * mm, "end": v(6.35, -102.63) * mm});
            skLineSegment(sketch, "E1714", {"start": v(6.35, -102.63) * mm, "end": v(6.77, -102.78) * mm});
            skLineSegment(sketch, "E1715", {"start": v(6.77, -102.78) * mm, "end": v(7.18, -102.93) * mm});
            skLineSegment(sketch, "E1716", {"start": v(7.18, -102.93) * mm, "end": v(7.6, -103.1) * mm});
            skLineSegment(sketch, "E1717", {"start": v(7.6, -103.1) * mm, "end": v(8, -103.28) * mm});
            skLineSegment(sketch, "E1718", {"start": v(8, -103.28) * mm, "end": v(8.4, -103.46) * mm});
            skLineSegment(sketch, "E1719", {"start": v(8.4, -103.46) * mm, "end": v(8.8, -103.66) * mm});
            skLineSegment(sketch, "E1720", {"start": v(8.8, -103.66) * mm, "end": v(9.2, -103.87) * mm});
            skLineSegment(sketch, "E1721", {"start": v(9.2, -103.87) * mm, "end": v(9.58, -104.08) * mm});
            skLineSegment(sketch, "E1722", {"start": v(9.58, -104.08) * mm, "end": v(9.97, -104.3) * mm});
            skLineSegment(sketch, "E1723", {"start": v(9.97, -104.3) * mm, "end": v(10.34, -104.54) * mm});
            skLineSegment(sketch, "E1724", {"start": v(10.34, -104.54) * mm, "end": v(10.72, -104.79) * mm});
            skLineSegment(sketch, "E1725", {"start": v(10.72, -104.79) * mm, "end": v(11.08, -105.04) * mm});
            skLineSegment(sketch, "E1726", {"start": v(11.08, -105.04) * mm, "end": v(11.44, -105.3) * mm});
            skLineSegment(sketch, "E1727", {"start": v(11.44, -105.3) * mm, "end": v(11.8, -105.58) * mm});
            skLineSegment(sketch, "E1728", {"start": v(11.8, -105.58) * mm, "end": v(12.15, -105.86) * mm});
            skLineSegment(sketch, "E1729", {"start": v(12.15, -105.86) * mm, "end": v(12.49, -106.15) * mm});
            skLineSegment(sketch, "E1730", {"start": v(12.49, -106.15) * mm, "end": v(12.82, -106.46) * mm});
            skLineSegment(sketch, "E1731", {"start": v(12.82, -106.46) * mm, "end": v(13.15, -106.77) * mm});
            skLineSegment(sketch, "E1732", {"start": v(13.15, -106.77) * mm, "end": v(13.4, -107.02) * mm});
            skLineSegment(sketch, "E1733", {"start": v(13.4, -107.02) * mm, "end": v(13.65, -107.29) * mm});
            skLineSegment(sketch, "E1734", {"start": v(13.65, -107.29) * mm, "end": v(13.9, -107.55) * mm});
            skLineSegment(sketch, "E1735", {"start": v(13.9, -107.55) * mm, "end": v(14.12, -107.83) * mm});
            skLineSegment(sketch, "E1736", {"start": v(14.12, -107.83) * mm, "end": v(14.35, -108.1) * mm});
            skLineSegment(sketch, "E1737", {"start": v(14.35, -108.1) * mm, "end": v(14.57, -108.4) * mm});
            skLineSegment(sketch, "E1738", {"start": v(14.57, -108.4) * mm, "end": v(14.78, -108.68) * mm});
            skLineSegment(sketch, "E1739", {"start": v(14.78, -108.68) * mm, "end": v(14.98, -108.98) * mm});
            skLineSegment(sketch, "E1740", {"start": v(14.98, -108.98) * mm, "end": v(15.18, -109.28) * mm});
            skLineSegment(sketch, "E1741", {"start": v(15.18, -109.28) * mm, "end": v(15.37, -109.58) * mm});
            skLineSegment(sketch, "E1742", {"start": v(15.37, -109.58) * mm, "end": v(15.55, -109.89) * mm});
            skLineSegment(sketch, "E1743", {"start": v(15.55, -109.89) * mm, "end": v(15.72, -110.2) * mm});
            skLineSegment(sketch, "E1744", {"start": v(15.72, -110.2) * mm, "end": v(15.89, -110.52) * mm});
            skLineSegment(sketch, "E1745", {"start": v(15.89, -110.52) * mm, "end": v(16.04, -110.84) * mm});
            skLineSegment(sketch, "E1746", {"start": v(16.04, -110.84) * mm, "end": v(16.2, -111.16) * mm});
            skLineSegment(sketch, "E1747", {"start": v(16.2, -111.16) * mm, "end": v(16.33, -111.5) * mm});
            skLineSegment(sketch, "E1748", {"start": v(16.33, -111.5) * mm, "end": v(16.47, -111.82) * mm});
            skLineSegment(sketch, "E1749", {"start": v(16.47, -111.82) * mm, "end": v(16.59, -112.16) * mm});
            skLineSegment(sketch, "E1750", {"start": v(16.59, -112.16) * mm, "end": v(16.7, -112.5) * mm});
            skLineSegment(sketch, "E1751", {"start": v(16.7, -112.5) * mm, "end": v(16.81, -112.83) * mm});
            skLineSegment(sketch, "E1752", {"start": v(16.81, -112.83) * mm, "end": v(16.91, -113.18) * mm});
            skLineSegment(sketch, "E1753", {"start": v(16.91, -113.18) * mm, "end": v(17, -113.52) * mm});
            skLineSegment(sketch, "E1754", {"start": v(17, -113.52) * mm, "end": v(17.09, -113.87) * mm});
            skLineSegment(sketch, "E1755", {"start": v(17.09, -113.87) * mm, "end": v(17.16, -114.22) * mm});
            skLineSegment(sketch, "E1756", {"start": v(17.16, -114.22) * mm, "end": v(17.23, -114.57) * mm});
            skLineSegment(sketch, "E1757", {"start": v(17.23, -114.57) * mm, "end": v(17.28, -114.93) * mm});
            skLineSegment(sketch, "E1758", {"start": v(17.28, -114.93) * mm, "end": v(17.33, -115.28) * mm});
            skLineSegment(sketch, "E1759", {"start": v(17.33, -115.28) * mm, "end": v(17.37, -115.64) * mm});
            skLineSegment(sketch, "E1760", {"start": v(17.37, -115.64) * mm, "end": v(17.4, -116) * mm});
            skLineSegment(sketch, "E1761", {"start": v(17.4, -116) * mm, "end": v(17.42, -116.36) * mm});
            skLineSegment(sketch, "E1762", {"start": v(17.42, -116.36) * mm, "end": v(17.43, -116.72) * mm});
            skLineSegment(sketch, "E1763", {"start": v(17.43, -116.72) * mm, "end": v(17.43, -117.08) * mm});
            skLineSegment(sketch, "E1764", {"start": v(17.43, -78.37) * mm, "end": v(17.44, -78.73) * mm});
            skLineSegment(sketch, "E1765", {"start": v(17.44, -78.73) * mm, "end": v(17.43, -79.1) * mm});
            skLineSegment(sketch, "E1766", {"start": v(17.43, -79.1) * mm, "end": v(17.41, -79.47) * mm});
            skLineSegment(sketch, "E1767", {"start": v(17.41, -79.47) * mm, "end": v(17.39, -79.83) * mm});
            skLineSegment(sketch, "E1768", {"start": v(17.39, -79.83) * mm, "end": v(17.36, -80.2) * mm});
            skLineSegment(sketch, "E1769", {"start": v(17.36, -80.2) * mm, "end": v(17.31, -80.56) * mm});
            skLineSegment(sketch, "E1770", {"start": v(17.31, -80.56) * mm, "end": v(17.26, -80.92) * mm});
            skLineSegment(sketch, "E1771", {"start": v(17.26, -80.92) * mm, "end": v(17.2, -81.27) * mm});
            skLineSegment(sketch, "E1772", {"start": v(17.2, -81.27) * mm, "end": v(17.13, -81.63) * mm});
            skLineSegment(sketch, "E1773", {"start": v(17.13, -81.63) * mm, "end": v(17.05, -81.98) * mm});
            skLineSegment(sketch, "E1774", {"start": v(17.05, -81.98) * mm, "end": v(16.96, -82.34) * mm});
            skLineSegment(sketch, "E1775", {"start": v(16.96, -82.34) * mm, "end": v(16.87, -82.69) * mm});
            skLineSegment(sketch, "E1776", {"start": v(16.87, -82.69) * mm, "end": v(16.76, -83.03) * mm});
            skLineSegment(sketch, "E1777", {"start": v(16.76, -83.03) * mm, "end": v(16.65, -83.38) * mm});
            skLineSegment(sketch, "E1778", {"start": v(16.65, -83.38) * mm, "end": v(16.53, -83.72) * mm});
            skLineSegment(sketch, "E1779", {"start": v(16.53, -83.72) * mm, "end": v(16.4, -84.06) * mm});
            skLineSegment(sketch, "E1780", {"start": v(16.4, -84.06) * mm, "end": v(16.26, -84.4) * mm});
            skLineSegment(sketch, "E1781", {"start": v(16.26, -84.4) * mm, "end": v(16.12, -84.72) * mm});
            skLineSegment(sketch, "E1782", {"start": v(16.12, -84.72) * mm, "end": v(15.96, -85.05) * mm});
            skLineSegment(sketch, "E1783", {"start": v(15.96, -85.05) * mm, "end": v(15.8, -85.37) * mm});
            skLineSegment(sketch, "E1784", {"start": v(15.8, -85.37) * mm, "end": v(15.63, -85.7) * mm});
            skLineSegment(sketch, "E1785", {"start": v(15.63, -85.7) * mm, "end": v(15.45, -86) * mm});
            skLineSegment(sketch, "E1786", {"start": v(15.45, -86) * mm, "end": v(15.26, -86.32) * mm});
            skLineSegment(sketch, "E1787", {"start": v(15.26, -86.32) * mm, "end": v(15.07, -86.63) * mm});
            skLineSegment(sketch, "E1788", {"start": v(15.07, -86.63) * mm, "end": v(14.87, -86.93) * mm});
            skLineSegment(sketch, "E1789", {"start": v(14.87, -86.93) * mm, "end": v(14.66, -87.23) * mm});
            skLineSegment(sketch, "E1790", {"start": v(14.66, -87.23) * mm, "end": v(14.44, -87.52) * mm});
            skLineSegment(sketch, "E1791", {"start": v(14.44, -87.52) * mm, "end": v(14.21, -87.8) * mm});
            skLineSegment(sketch, "E1792", {"start": v(14.21, -87.8) * mm, "end": v(13.98, -88.09) * mm});
            skLineSegment(sketch, "E1793", {"start": v(13.98, -88.09) * mm, "end": v(13.74, -88.36) * mm});
            skLineSegment(sketch, "E1794", {"start": v(13.74, -88.36) * mm, "end": v(13.5, -88.63) * mm});
            skLineSegment(sketch, "E1795", {"start": v(13.5, -88.63) * mm, "end": v(13.24, -88.9) * mm});
            skLineSegment(sketch, "E1796", {"start": v(13.24, -88.9) * mm, "end": v(12.9, -89.2) * mm});
            skLineSegment(sketch, "E1797", {"start": v(12.9, -89.2) * mm, "end": v(12.57, -89.5) * mm});
            skLineSegment(sketch, "E1798", {"start": v(12.57, -89.5) * mm, "end": v(12.22, -89.79) * mm});
            skLineSegment(sketch, "E1799", {"start": v(12.22, -89.79) * mm, "end": v(11.87, -90.07) * mm});
            skLineSegment(sketch, "E1800", {"start": v(11.87, -90.07) * mm, "end": v(11.5, -90.34) * mm});
            skLineSegment(sketch, "E1801", {"start": v(11.5, -90.34) * mm, "end": v(11.14, -90.6) * mm});
            skLineSegment(sketch, "E1802", {"start": v(11.14, -90.6) * mm, "end": v(10.77, -90.85) * mm});
            skLineSegment(sketch, "E1803", {"start": v(10.77, -90.85) * mm, "end": v(10.4, -91.09) * mm});
            skLineSegment(sketch, "E1804", {"start": v(10.4, -91.09) * mm, "end": v(10.01, -91.32) * mm});
            skLineSegment(sketch, "E1805", {"start": v(10.01, -91.32) * mm, "end": v(9.62, -91.54) * mm});
            skLineSegment(sketch, "E1806", {"start": v(9.62, -91.54) * mm, "end": v(9.23, -91.75) * mm});
            skLineSegment(sketch, "E1807", {"start": v(9.23, -91.75) * mm, "end": v(8.83, -91.96) * mm});
            skLineSegment(sketch, "E1808", {"start": v(8.83, -91.96) * mm, "end": v(8.43, -92.15) * mm});
            skLineSegment(sketch, "E1809", {"start": v(8.43, -92.15) * mm, "end": v(8.02, -92.33) * mm});
            skLineSegment(sketch, "E1810", {"start": v(8.02, -92.33) * mm, "end": v(7.61, -92.5) * mm});
            skLineSegment(sketch, "E1811", {"start": v(7.61, -92.5) * mm, "end": v(7.2, -92.67) * mm});
            skLineSegment(sketch, "E1812", {"start": v(7.2, -92.67) * mm, "end": v(6.78, -92.82) * mm});
            skLineSegment(sketch, "E1813", {"start": v(6.78, -92.82) * mm, "end": v(6.36, -92.96) * mm});
            skLineSegment(sketch, "E1814", {"start": v(6.36, -92.96) * mm, "end": v(5.93, -93.1) * mm});
            skLineSegment(sketch, "E1815", {"start": v(5.93, -93.1) * mm, "end": v(5.5, -93.21) * mm});
            skLineSegment(sketch, "E1816", {"start": v(5.5, -93.21) * mm, "end": v(5.07, -93.32) * mm});
            skLineSegment(sketch, "E1817", {"start": v(5.07, -93.32) * mm, "end": v(4.63, -93.42) * mm});
            skLineSegment(sketch, "E1818", {"start": v(4.63, -93.42) * mm, "end": v(4.2, -93.51) * mm});
            skLineSegment(sketch, "E1819", {"start": v(4.2, -93.51) * mm, "end": v(3.76, -93.59) * mm});
            skLineSegment(sketch, "E1820", {"start": v(3.76, -93.59) * mm, "end": v(3.31, -93.66) * mm});
            skLineSegment(sketch, "E1821", {"start": v(3.31, -93.66) * mm, "end": v(2.87, -93.71) * mm});
            skLineSegment(sketch, "E1822", {"start": v(2.87, -93.71) * mm, "end": v(2.42, -93.76) * mm});
            skLineSegment(sketch, "E1823", {"start": v(2.42, -93.76) * mm, "end": v(1.98, -93.8) * mm});
            skLineSegment(sketch, "E1824", {"start": v(1.98, -93.8) * mm, "end": v(1.53, -93.82) * mm});
            skLineSegment(sketch, "E1825", {"start": v(1.53, -93.82) * mm, "end": v(1.08, -93.83) * mm});
            skLineSegment(sketch, "E1826", {"start": v(1.08, -93.83) * mm, "end": v(0.63, -93.83) * mm});
            skLineSegment(sketch, "E1827", {"start": v(0.63, -93.83) * mm, "end": v(0.17, -93.82) * mm});
            skLineSegment(sketch, "E1828", {"start": v(0.17, -93.82) * mm, "end": v(-0.32, -93.83) * mm});
            skLineSegment(sketch, "E1829", {"start": v(-0.32, -93.83) * mm, "end": v(-0.8, -93.84) * mm});
            skLineSegment(sketch, "E1830", {"start": v(-0.8, -93.84) * mm, "end": v(-1.3, -93.83) * mm});
            skLineSegment(sketch, "E1831", {"start": v(-1.3, -93.83) * mm, "end": v(-1.78, -93.8) * mm});
            skLineSegment(sketch, "E1832", {"start": v(-1.78, -93.8) * mm, "end": v(-2.27, -93.77) * mm});
            skLineSegment(sketch, "E1833", {"start": v(-2.27, -93.77) * mm, "end": v(-2.76, -93.72) * mm});
            skLineSegment(sketch, "E1834", {"start": v(-2.76, -93.72) * mm, "end": v(-3.24, -93.66) * mm});
            skLineSegment(sketch, "E1835", {"start": v(-3.24, -93.66) * mm, "end": v(-3.72, -93.59) * mm});
            skLineSegment(sketch, "E1836", {"start": v(-3.72, -93.59) * mm, "end": v(-4.2, -93.5) * mm});
            skLineSegment(sketch, "E1837", {"start": v(-4.2, -93.5) * mm, "end": v(-4.67, -93.4) * mm});
            skLineSegment(sketch, "E1838", {"start": v(-4.67, -93.4) * mm, "end": v(-5.14, -93.3) * mm});
            skLineSegment(sketch, "E1839", {"start": v(-5.14, -93.3) * mm, "end": v(-5.61, -93.18) * mm});
            skLineSegment(sketch, "E1840", {"start": v(-5.61, -93.18) * mm, "end": v(-6.08, -93.05) * mm});
            skLineSegment(sketch, "E1841", {"start": v(-6.08, -93.05) * mm, "end": v(-6.54, -92.91) * mm});
            skLineSegment(sketch, "E1842", {"start": v(-6.54, -92.91) * mm, "end": v(-7, -92.76) * mm});
            skLineSegment(sketch, "E1843", {"start": v(-7, -92.76) * mm, "end": v(-7.46, -92.6) * mm});
            skLineSegment(sketch, "E1844", {"start": v(-7.46, -92.6) * mm, "end": v(-7.9, -92.42) * mm});
            skLineSegment(sketch, "E1845", {"start": v(-7.9, -92.42) * mm, "end": v(-8.35, -92.23) * mm});
            skLineSegment(sketch, "E1846", {"start": v(-8.35, -92.23) * mm, "end": v(-8.8, -92.03) * mm});
            skLineSegment(sketch, "E1847", {"start": v(-8.8, -92.03) * mm, "end": v(-9.23, -91.82) * mm});
            skLineSegment(sketch, "E1848", {"start": v(-9.23, -91.82) * mm, "end": v(-9.66, -91.6) * mm});
            skLineSegment(sketch, "E1849", {"start": v(-9.66, -91.6) * mm, "end": v(-10.1, -91.37) * mm});
            skLineSegment(sketch, "E1850", {"start": v(-10.1, -91.37) * mm, "end": v(-10.51, -91.13) * mm});
            skLineSegment(sketch, "E1851", {"start": v(-10.51, -91.13) * mm, "end": v(-10.93, -90.88) * mm});
            skLineSegment(sketch, "E1852", {"start": v(-10.93, -90.88) * mm, "end": v(-11.33, -90.62) * mm});
            skLineSegment(sketch, "E1853", {"start": v(-11.33, -90.62) * mm, "end": v(-11.74, -90.34) * mm});
            skLineSegment(sketch, "E1854", {"start": v(-11.74, -90.34) * mm, "end": v(-12.13, -90.06) * mm});
            skLineSegment(sketch, "E1855", {"start": v(-12.13, -90.06) * mm, "end": v(-12.52, -89.77) * mm});
            skLineSegment(sketch, "E1856", {"start": v(-12.52, -89.77) * mm, "end": v(-12.9, -89.46) * mm});
            skLineSegment(sketch, "E1857", {"start": v(-12.9, -89.46) * mm, "end": v(-13.28, -89.15) * mm});
            skLineSegment(sketch, "E1858", {"start": v(-13.28, -89.15) * mm, "end": v(-13.65, -88.82) * mm});
            skLineSegment(sketch, "E1859", {"start": v(-13.65, -88.82) * mm, "end": v(-14, -88.5) * mm});
            skLineSegment(sketch, "E1860", {"start": v(-14, -88.5) * mm, "end": v(-14.26, -88.24) * mm});
            skLineSegment(sketch, "E1861", {"start": v(-14.26, -88.24) * mm, "end": v(-14.5, -87.98) * mm});
            skLineSegment(sketch, "E1862", {"start": v(-14.5, -87.98) * mm, "end": v(-14.75, -87.72) * mm});
            skLineSegment(sketch, "E1863", {"start": v(-14.75, -87.72) * mm, "end": v(-14.98, -87.46) * mm});
            skLineSegment(sketch, "E1864", {"start": v(-14.98, -87.46) * mm, "end": v(-15.2, -87.18) * mm});
            skLineSegment(sketch, "E1865", {"start": v(-15.2, -87.18) * mm, "end": v(-15.43, -86.9) * mm});
            skLineSegment(sketch, "E1866", {"start": v(-15.43, -86.9) * mm, "end": v(-15.64, -86.62) * mm});
            skLineSegment(sketch, "E1867", {"start": v(-15.64, -86.62) * mm, "end": v(-15.84, -86.33) * mm});
            skLineSegment(sketch, "E1868", {"start": v(-15.84, -86.33) * mm, "end": v(-16.03, -86.04) * mm});
            skLineSegment(sketch, "E1869", {"start": v(-16.03, -86.04) * mm, "end": v(-16.22, -85.74) * mm});
            skLineSegment(sketch, "E1870", {"start": v(-16.22, -85.74) * mm, "end": v(-16.4, -85.44) * mm});
            skLineSegment(sketch, "E1871", {"start": v(-16.4, -85.44) * mm, "end": v(-16.57, -85.13) * mm});
            skLineSegment(sketch, "E1872", {"start": v(-16.57, -85.13) * mm, "end": v(-16.73, -84.82) * mm});
            skLineSegment(sketch, "E1873", {"start": v(-16.73, -84.82) * mm, "end": v(-16.89, -84.5) * mm});
            skLineSegment(sketch, "E1874", {"start": v(-16.89, -84.5) * mm, "end": v(-17.04, -84.19) * mm});
            skLineSegment(sketch, "E1875", {"start": v(-17.04, -84.19) * mm, "end": v(-17.18, -83.87) * mm});
            skLineSegment(sketch, "E1876", {"start": v(-17.18, -83.87) * mm, "end": v(-17.3, -83.54) * mm});
            skLineSegment(sketch, "E1877", {"start": v(-17.3, -83.54) * mm, "end": v(-17.43, -83.21) * mm});
            skLineSegment(sketch, "E1878", {"start": v(-17.43, -83.21) * mm, "end": v(-17.54, -82.88) * mm});
            skLineSegment(sketch, "E1879", {"start": v(-17.54, -82.88) * mm, "end": v(-17.65, -82.54) * mm});
            skLineSegment(sketch, "E1880", {"start": v(-17.65, -82.54) * mm, "end": v(-17.75, -82.2) * mm});
            skLineSegment(sketch, "E1881", {"start": v(-17.75, -82.2) * mm, "end": v(-17.84, -81.87) * mm});
            skLineSegment(sketch, "E1882", {"start": v(-17.84, -81.87) * mm, "end": v(-17.91, -81.52) * mm});
            skLineSegment(sketch, "E1883", {"start": v(-17.91, -81.52) * mm, "end": v(-17.99, -81.18) * mm});
            skLineSegment(sketch, "E1884", {"start": v(-17.99, -81.18) * mm, "end": v(-18.05, -80.83) * mm});
            skLineSegment(sketch, "E1885", {"start": v(-18.05, -80.83) * mm, "end": v(-18.1, -80.48) * mm});
            skLineSegment(sketch, "E1886", {"start": v(-18.1, -80.48) * mm, "end": v(-18.15, -80.13) * mm});
            skLineSegment(sketch, "E1887", {"start": v(-18.15, -80.13) * mm, "end": v(-18.18, -79.78) * mm});
            skLineSegment(sketch, "E1888", {"start": v(-18.18, -79.78) * mm, "end": v(-18.2, -79.43) * mm});
            skLineSegment(sketch, "E1889", {"start": v(-18.2, -79.43) * mm, "end": v(-18.23, -79.07) * mm});
            skLineSegment(sketch, "E1890", {"start": v(-18.23, -79.07) * mm, "end": v(-18.23, -78.72) * mm});
            skLineSegment(sketch, "E1891", {"start": v(-18.23, -78.72) * mm, "end": v(-18.23, -78.36) * mm});
            skLineSegment(sketch, "E1892", {"start": v(-18.23, -78.36) * mm, "end": v(-18.23, -78) * mm});
            skLineSegment(sketch, "E1893", {"start": v(-18.23, -78) * mm, "end": v(-18.22, -77.64) * mm});
            skLineSegment(sketch, "E1894", {"start": v(-18.22, -77.64) * mm, "end": v(-18.2, -77.28) * mm});
            skLineSegment(sketch, "E1895", {"start": v(-18.2, -77.28) * mm, "end": v(-18.16, -76.92) * mm});
            skLineSegment(sketch, "E1896", {"start": v(-18.16, -76.92) * mm, "end": v(-18.12, -76.56) * mm});
            skLineSegment(sketch, "E1897", {"start": v(-18.12, -76.56) * mm, "end": v(-18.07, -76.2) * mm});
            skLineSegment(sketch, "E1898", {"start": v(-18.07, -76.2) * mm, "end": v(-18.01, -75.85) * mm});
            skLineSegment(sketch, "E1899", {"start": v(-18.01, -75.85) * mm, "end": v(-17.95, -75.5) * mm});
            skLineSegment(sketch, "E1900", {"start": v(-17.95, -75.5) * mm, "end": v(-17.87, -75.15) * mm});
            skLineSegment(sketch, "E1901", {"start": v(-17.87, -75.15) * mm, "end": v(-17.78, -74.8) * mm});
            skLineSegment(sketch, "E1902", {"start": v(-17.78, -74.8) * mm, "end": v(-17.69, -74.46) * mm});
            skLineSegment(sketch, "E1903", {"start": v(-17.69, -74.46) * mm, "end": v(-17.59, -74.11) * mm});
            skLineSegment(sketch, "E1904", {"start": v(-17.59, -74.11) * mm, "end": v(-17.47, -73.77) * mm});
            skLineSegment(sketch, "E1905", {"start": v(-17.47, -73.77) * mm, "end": v(-17.35, -73.44) * mm});
            skLineSegment(sketch, "E1906", {"start": v(-17.35, -73.44) * mm, "end": v(-17.23, -73.1) * mm});
            skLineSegment(sketch, "E1907", {"start": v(-17.23, -73.1) * mm, "end": v(-17.09, -72.78) * mm});
            skLineSegment(sketch, "E1908", {"start": v(-17.09, -72.78) * mm, "end": v(-16.94, -72.45) * mm});
            skLineSegment(sketch, "E1909", {"start": v(-16.94, -72.45) * mm, "end": v(-16.79, -72.13) * mm});
            skLineSegment(sketch, "E1910", {"start": v(-16.79, -72.13) * mm, "end": v(-16.63, -71.81) * mm});
            skLineSegment(sketch, "E1911", {"start": v(-16.63, -71.81) * mm, "end": v(-16.46, -71.5) * mm});
            skLineSegment(sketch, "E1912", {"start": v(-16.46, -71.5) * mm, "end": v(-16.28, -71.19) * mm});
            skLineSegment(sketch, "E1913", {"start": v(-16.28, -71.19) * mm, "end": v(-16.1, -70.88) * mm});
            skLineSegment(sketch, "E1914", {"start": v(-16.1, -70.88) * mm, "end": v(-15.9, -70.58) * mm});
            skLineSegment(sketch, "E1915", {"start": v(-15.9, -70.58) * mm, "end": v(-15.7, -70.29) * mm});
            skLineSegment(sketch, "E1916", {"start": v(-15.7, -70.29) * mm, "end": v(-15.49, -70) * mm});
            skLineSegment(sketch, "E1917", {"start": v(-15.49, -70) * mm, "end": v(-15.27, -69.7) * mm});
            skLineSegment(sketch, "E1918", {"start": v(-15.27, -69.7) * mm, "end": v(-15.05, -69.43) * mm});
            skLineSegment(sketch, "E1919", {"start": v(-15.05, -69.43) * mm, "end": v(-14.81, -69.15) * mm});
            skLineSegment(sketch, "E1920", {"start": v(-14.81, -69.15) * mm, "end": v(-14.58, -68.89) * mm});
            skLineSegment(sketch, "E1921", {"start": v(-14.58, -68.89) * mm, "end": v(-14.33, -68.62) * mm});
            skLineSegment(sketch, "E1922", {"start": v(-14.33, -68.62) * mm, "end": v(-14.07, -68.36) * mm});
            skLineSegment(sketch, "E1923", {"start": v(-14.07, -68.36) * mm, "end": v(-13.81, -68.11) * mm});
            skLineSegment(sketch, "E1924", {"start": v(-13.81, -68.11) * mm, "end": v(-13.45, -67.8) * mm});
            skLineSegment(sketch, "E1925", {"start": v(-13.45, -67.8) * mm, "end": v(-13.09, -67.48) * mm});
            skLineSegment(sketch, "E1926", {"start": v(-13.09, -67.48) * mm, "end": v(-12.72, -67.17) * mm});
            skLineSegment(sketch, "E1927", {"start": v(-12.72, -67.17) * mm, "end": v(-12.34, -66.88) * mm});
            skLineSegment(sketch, "E1928", {"start": v(-12.34, -66.88) * mm, "end": v(-11.95, -66.6) * mm});
            skLineSegment(sketch, "E1929", {"start": v(-11.95, -66.6) * mm, "end": v(-11.56, -66.32) * mm});
            skLineSegment(sketch, "E1930", {"start": v(-11.56, -66.32) * mm, "end": v(-11.16, -66.06) * mm});
            skLineSegment(sketch, "E1931", {"start": v(-11.16, -66.06) * mm, "end": v(-10.75, -65.8) * mm});
            skLineSegment(sketch, "E1932", {"start": v(-10.75, -65.8) * mm, "end": v(-10.34, -65.56) * mm});
            skLineSegment(sketch, "E1933", {"start": v(-10.34, -65.56) * mm, "end": v(-9.93, -65.33) * mm});
            skLineSegment(sketch, "E1934", {"start": v(-9.93, -65.33) * mm, "end": v(-9.5, -65.1) * mm});
            skLineSegment(sketch, "E1935", {"start": v(-9.5, -65.1) * mm, "end": v(-9.08, -64.9) * mm});
            skLineSegment(sketch, "E1936", {"start": v(-9.08, -64.9) * mm, "end": v(-8.64, -64.7) * mm});
            skLineSegment(sketch, "E1937", {"start": v(-8.64, -64.7) * mm, "end": v(-8.2, -64.5) * mm});
            skLineSegment(sketch, "E1938", {"start": v(-8.2, -64.5) * mm, "end": v(-7.77, -64.32) * mm});
            skLineSegment(sketch, "E1939", {"start": v(-7.77, -64.32) * mm, "end": v(-7.32, -64.15) * mm});
            skLineSegment(sketch, "E1940", {"start": v(-7.32, -64.15) * mm, "end": v(-6.87, -64) * mm});
            skLineSegment(sketch, "E1941", {"start": v(-6.87, -64) * mm, "end": v(-6.42, -63.85) * mm});
            skLineSegment(sketch, "E1942", {"start": v(-6.42, -63.85) * mm, "end": v(-5.96, -63.71) * mm});
            skLineSegment(sketch, "E1943", {"start": v(-5.96, -63.71) * mm, "end": v(-5.5, -63.59) * mm});
            skLineSegment(sketch, "E1944", {"start": v(-5.5, -63.59) * mm, "end": v(-5.04, -63.48) * mm});
            skLineSegment(sketch, "E1945", {"start": v(-5.04, -63.48) * mm, "end": v(-4.57, -63.38) * mm});
            skLineSegment(sketch, "E1946", {"start": v(-4.57, -63.38) * mm, "end": v(-4.1, -63.29) * mm});
            skLineSegment(sketch, "E1947", {"start": v(-4.1, -63.29) * mm, "end": v(-3.64, -63.2) * mm});
            skLineSegment(sketch, "E1948", {"start": v(-3.64, -63.2) * mm, "end": v(-3.16, -63.14) * mm});
            skLineSegment(sketch, "E1949", {"start": v(-3.16, -63.14) * mm, "end": v(-2.69, -63.09) * mm});
            skLineSegment(sketch, "E1950", {"start": v(-2.69, -63.09) * mm, "end": v(-2.2, -63.04) * mm});
            skLineSegment(sketch, "E1951", {"start": v(-2.2, -63.04) * mm, "end": v(-1.73, -63.01) * mm});
            skLineSegment(sketch, "E1952", {"start": v(-1.73, -63.01) * mm, "end": v(-1.25, -63) * mm});
            skLineSegment(sketch, "E1953", {"start": v(-1.25, -63) * mm, "end": v(-0.77, -62.99) * mm});
            skLineSegment(sketch, "E1954", {"start": v(-0.77, -62.99) * mm, "end": v(-0.29, -63) * mm});
            skLineSegment(sketch, "E1955", {"start": v(-0.29, -63) * mm, "end": v(0.2, -63) * mm});
            skLineSegment(sketch, "E1956", {"start": v(0.2, -63) * mm, "end": v(0.65, -63) * mm});
            skLineSegment(sketch, "E1957", {"start": v(0.65, -63) * mm, "end": v(1.1, -63) * mm});
            skLineSegment(sketch, "E1958", {"start": v(1.1, -63) * mm, "end": v(1.54, -63.02) * mm});
            skLineSegment(sketch, "E1959", {"start": v(1.54, -63.02) * mm, "end": v(2, -63.05) * mm});
            skLineSegment(sketch, "E1960", {"start": v(2, -63.05) * mm, "end": v(2.44, -63.09) * mm});
            skLineSegment(sketch, "E1961", {"start": v(2.44, -63.09) * mm, "end": v(2.88, -63.13) * mm});
            skLineSegment(sketch, "E1962", {"start": v(2.88, -63.13) * mm, "end": v(3.32, -63.2) * mm});
            skLineSegment(sketch, "E1963", {"start": v(3.32, -63.2) * mm, "end": v(3.76, -63.27) * mm});
            skLineSegment(sketch, "E1964", {"start": v(3.76, -63.27) * mm, "end": v(4.2, -63.35) * mm});
            skLineSegment(sketch, "E1965", {"start": v(4.2, -63.35) * mm, "end": v(4.64, -63.44) * mm});
            skLineSegment(sketch, "E1966", {"start": v(4.64, -63.44) * mm, "end": v(5.07, -63.54) * mm});
            skLineSegment(sketch, "E1967", {"start": v(5.07, -63.54) * mm, "end": v(5.5, -63.66) * mm});
            skLineSegment(sketch, "E1968", {"start": v(5.5, -63.66) * mm, "end": v(5.92, -63.78) * mm});
            skLineSegment(sketch, "E1969", {"start": v(5.92, -63.78) * mm, "end": v(6.35, -63.92) * mm});
            skLineSegment(sketch, "E1970", {"start": v(6.35, -63.92) * mm, "end": v(6.77, -64.06) * mm});
            skLineSegment(sketch, "E1971", {"start": v(6.77, -64.06) * mm, "end": v(7.18, -64.22) * mm});
            skLineSegment(sketch, "E1972", {"start": v(7.18, -64.22) * mm, "end": v(7.6, -64.39) * mm});
            skLineSegment(sketch, "E1973", {"start": v(7.6, -64.39) * mm, "end": v(8, -64.56) * mm});
            skLineSegment(sketch, "E1974", {"start": v(8, -64.56) * mm, "end": v(8.4, -64.75) * mm});
            skLineSegment(sketch, "E1975", {"start": v(8.4, -64.75) * mm, "end": v(8.8, -64.94) * mm});
            skLineSegment(sketch, "E1976", {"start": v(8.8, -64.94) * mm, "end": v(9.2, -65.15) * mm});
            skLineSegment(sketch, "E1977", {"start": v(9.2, -65.15) * mm, "end": v(9.58, -65.37) * mm});
            skLineSegment(sketch, "E1978", {"start": v(9.58, -65.37) * mm, "end": v(9.97, -65.6) * mm});
            skLineSegment(sketch, "E1979", {"start": v(9.97, -65.6) * mm, "end": v(10.34, -65.83) * mm});
            skLineSegment(sketch, "E1980", {"start": v(10.34, -65.83) * mm, "end": v(10.72, -66.07) * mm});
            skLineSegment(sketch, "E1981", {"start": v(10.72, -66.07) * mm, "end": v(11.08, -66.33) * mm});
            skLineSegment(sketch, "E1982", {"start": v(11.08, -66.33) * mm, "end": v(11.44, -66.6) * mm});
            skLineSegment(sketch, "E1983", {"start": v(11.44, -66.6) * mm, "end": v(11.8, -66.87) * mm});
            skLineSegment(sketch, "E1984", {"start": v(11.8, -66.87) * mm, "end": v(12.15, -67.15) * mm});
            skLineSegment(sketch, "E1985", {"start": v(12.15, -67.15) * mm, "end": v(12.49, -67.44) * mm});
            skLineSegment(sketch, "E1986", {"start": v(12.49, -67.44) * mm, "end": v(12.82, -67.74) * mm});
            skLineSegment(sketch, "E1987", {"start": v(12.82, -67.74) * mm, "end": v(13.15, -68.05) * mm});
            skLineSegment(sketch, "E1988", {"start": v(13.15, -68.05) * mm, "end": v(13.4, -68.3) * mm});
            skLineSegment(sketch, "E1989", {"start": v(13.4, -68.3) * mm, "end": v(13.65, -68.57) * mm});
            skLineSegment(sketch, "E1990", {"start": v(13.65, -68.57) * mm, "end": v(13.9, -68.84) * mm});
            skLineSegment(sketch, "E1991", {"start": v(13.9, -68.84) * mm, "end": v(14.12, -69.11) * mm});
            skLineSegment(sketch, "E1992", {"start": v(14.12, -69.11) * mm, "end": v(14.35, -69.4) * mm});
            skLineSegment(sketch, "E1993", {"start": v(14.35, -69.4) * mm, "end": v(14.57, -69.68) * mm});
            skLineSegment(sketch, "E1994", {"start": v(14.57, -69.68) * mm, "end": v(14.78, -69.97) * mm});
            skLineSegment(sketch, "E1995", {"start": v(14.78, -69.97) * mm, "end": v(14.98, -70.26) * mm});
            skLineSegment(sketch, "E1996", {"start": v(14.98, -70.26) * mm, "end": v(15.18, -70.56) * mm});
            skLineSegment(sketch, "E1997", {"start": v(15.18, -70.56) * mm, "end": v(15.37, -70.87) * mm});
            skLineSegment(sketch, "E1998", {"start": v(15.37, -70.87) * mm, "end": v(15.55, -71.17) * mm});
            skLineSegment(sketch, "E1999", {"start": v(15.55, -71.17) * mm, "end": v(15.72, -71.49) * mm});
            skLineSegment(sketch, "E2000", {"start": v(15.72, -71.49) * mm, "end": v(15.89, -71.8) * mm});
            skLineSegment(sketch, "E2001", {"start": v(15.89, -71.8) * mm, "end": v(16.04, -72.12) * mm});
            skLineSegment(sketch, "E2002", {"start": v(16.04, -72.12) * mm, "end": v(16.2, -72.45) * mm});
            skLineSegment(sketch, "E2003", {"start": v(16.2, -72.45) * mm, "end": v(16.33, -72.78) * mm});
            skLineSegment(sketch, "E2004", {"start": v(16.33, -72.78) * mm, "end": v(16.47, -73.1) * mm});
            skLineSegment(sketch, "E2005", {"start": v(16.47, -73.1) * mm, "end": v(16.59, -73.44) * mm});
            skLineSegment(sketch, "E2006", {"start": v(16.59, -73.44) * mm, "end": v(16.7, -73.78) * mm});
            skLineSegment(sketch, "E2007", {"start": v(16.7, -73.78) * mm, "end": v(16.81, -74.12) * mm});
            skLineSegment(sketch, "E2008", {"start": v(16.81, -74.12) * mm, "end": v(16.91, -74.46) * mm});
            skLineSegment(sketch, "E2009", {"start": v(16.91, -74.46) * mm, "end": v(17, -74.8) * mm});
            skLineSegment(sketch, "E2010", {"start": v(17, -74.8) * mm, "end": v(17.09, -75.15) * mm});
            skLineSegment(sketch, "E2011", {"start": v(17.09, -75.15) * mm, "end": v(17.16, -75.5) * mm});
            skLineSegment(sketch, "E2012", {"start": v(17.16, -75.5) * mm, "end": v(17.23, -75.86) * mm});
            skLineSegment(sketch, "E2013", {"start": v(17.23, -75.86) * mm, "end": v(17.28, -76.21) * mm});
            skLineSegment(sketch, "E2014", {"start": v(17.28, -76.21) * mm, "end": v(17.33, -76.57) * mm});
            skLineSegment(sketch, "E2015", {"start": v(17.33, -76.57) * mm, "end": v(17.37, -76.92) * mm});
            skLineSegment(sketch, "E2016", {"start": v(17.37, -76.92) * mm, "end": v(17.4, -77.28) * mm});
            skLineSegment(sketch, "E2017", {"start": v(17.4, -77.28) * mm, "end": v(17.42, -77.64) * mm});
            skLineSegment(sketch, "E2018", {"start": v(17.42, -77.64) * mm, "end": v(17.43, -78) * mm});
            skLineSegment(sketch, "E2019", {"start": v(17.43, -78) * mm, "end": v(17.43, -78.37) * mm});
            skLineSegment(sketch, "E2020", {"start": v(16.96, -55.11) * mm, "end": v(-18.03, -55.11) * mm});
            skLineSegment(sketch, "E2021", {"start": v(-18.03, -55.11) * mm, "end": v(-18.03, -33.36) * mm});
            skLineSegment(sketch, "E2022", {"start": v(-1.3, -55.11) * mm, "end": v(-1.3, -34.92) * mm});
            skLineSegment(sketch, "E2023", {"start": v(3.88, -25.66) * mm, "end": v(3.88, -1.53) * mm});
            skLineSegment(sketch, "E2024", {"start": v(17.38, 17.74) * mm, "end": v(17.38, 17.22) * mm});
            skLineSegment(sketch, "E2025", {"start": v(17.38, 17.22) * mm, "end": v(17.35, 16.7) * mm});
            skLineSegment(sketch, "E2026", {"start": v(17.35, 16.7) * mm, "end": v(17.3, 16.2) * mm});
            skLineSegment(sketch, "E2027", {"start": v(17.3, 16.2) * mm, "end": v(17.22, 15.7) * mm});
            skLineSegment(sketch, "E2028", {"start": v(17.22, 15.7) * mm, "end": v(17.12, 15.2) * mm});
            skLineSegment(sketch, "E2029", {"start": v(17.12, 15.2) * mm, "end": v(17, 14.7) * mm});
            skLineSegment(sketch, "E2030", {"start": v(17, 14.7) * mm, "end": v(16.84, 14.22) * mm});
            skLineSegment(sketch, "E2031", {"start": v(16.84, 14.22) * mm, "end": v(16.66, 13.75) * mm});
            skLineSegment(sketch, "E2032", {"start": v(16.66, 13.75) * mm, "end": v(16.46, 13.28) * mm});
            skLineSegment(sketch, "E2033", {"start": v(16.46, 13.28) * mm, "end": v(16.24, 12.82) * mm});
            skLineSegment(sketch, "E2034", {"start": v(16.24, 12.82) * mm, "end": v(16, 12.38) * mm});
            skLineSegment(sketch, "E2035", {"start": v(16, 12.38) * mm, "end": v(15.72, 11.95) * mm});
            skLineSegment(sketch, "E2036", {"start": v(15.72, 11.95) * mm, "end": v(15.43, 11.53) * mm});
            skLineSegment(sketch, "E2037", {"start": v(15.43, 11.53) * mm, "end": v(15.12, 11.13) * mm});
            skLineSegment(sketch, "E2038", {"start": v(15.12, 11.13) * mm, "end": v(14.78, 10.74) * mm});
            skLineSegment(sketch, "E2039", {"start": v(14.78, 10.74) * mm, "end": v(14.43, 10.37) * mm});
            skLineSegment(sketch, "E2040", {"start": v(14.43, 10.37) * mm, "end": v(14.17, 10.1) * mm});
            skLineSegment(sketch, "E2041", {"start": v(14.17, 10.1) * mm, "end": v(13.9, 9.86) * mm});
            skLineSegment(sketch, "E2042", {"start": v(13.9, 9.86) * mm, "end": v(13.64, 9.61) * mm});
            skLineSegment(sketch, "E2043", {"start": v(13.64, 9.61) * mm, "end": v(13.36, 9.38) * mm});
            skLineSegment(sketch, "E2044", {"start": v(13.36, 9.38) * mm, "end": v(13.08, 9.15) * mm});
            skLineSegment(sketch, "E2045", {"start": v(13.08, 9.15) * mm, "end": v(12.8, 8.93) * mm});
            skLineSegment(sketch, "E2046", {"start": v(12.8, 8.93) * mm, "end": v(12.5, 8.72) * mm});
            skLineSegment(sketch, "E2047", {"start": v(12.5, 8.72) * mm, "end": v(12.21, 8.51) * mm});
            skLineSegment(sketch, "E2048", {"start": v(12.21, 8.51) * mm, "end": v(11.91, 8.32) * mm});
            skLineSegment(sketch, "E2049", {"start": v(11.91, 8.32) * mm, "end": v(11.6, 8.13) * mm});
            skLineSegment(sketch, "E2050", {"start": v(11.6, 8.13) * mm, "end": v(11.3, 7.95) * mm});
            skLineSegment(sketch, "E2051", {"start": v(11.3, 7.95) * mm, "end": v(10.98, 7.78) * mm});
            skLineSegment(sketch, "E2052", {"start": v(10.98, 7.78) * mm, "end": v(10.67, 7.61) * mm});
            skLineSegment(sketch, "E2053", {"start": v(10.67, 7.61) * mm, "end": v(10.34, 7.46) * mm});
            skLineSegment(sketch, "E2054", {"start": v(10.34, 7.46) * mm, "end": v(10.02, 7.31) * mm});
            skLineSegment(sketch, "E2055", {"start": v(10.02, 7.31) * mm, "end": v(9.69, 7.17) * mm});
            skLineSegment(sketch, "E2056", {"start": v(9.69, 7.17) * mm, "end": v(9.36, 7.04) * mm});
            skLineSegment(sketch, "E2057", {"start": v(9.36, 7.04) * mm, "end": v(9.02, 6.92) * mm});
            skLineSegment(sketch, "E2058", {"start": v(9.02, 6.92) * mm, "end": v(8.68, 6.8) * mm});
            skLineSegment(sketch, "E2059", {"start": v(8.68, 6.8) * mm, "end": v(8.34, 6.7) * mm});
            skLineSegment(sketch, "E2060", {"start": v(8.34, 6.7) * mm, "end": v(8, 6.6) * mm});
            skLineSegment(sketch, "E2061", {"start": v(8, 6.6) * mm, "end": v(7.64, 6.52) * mm});
            skLineSegment(sketch, "E2062", {"start": v(7.64, 6.52) * mm, "end": v(7.3, 6.45) * mm});
            skLineSegment(sketch, "E2063", {"start": v(7.3, 6.45) * mm, "end": v(6.94, 6.38) * mm});
            skLineSegment(sketch, "E2064", {"start": v(6.94, 6.38) * mm, "end": v(6.59, 6.32) * mm});
            skLineSegment(sketch, "E2065", {"start": v(6.59, 6.32) * mm, "end": v(6.23, 6.27) * mm});
            skLineSegment(sketch, "E2066", {"start": v(6.23, 6.27) * mm, "end": v(5.87, 6.23) * mm});
            skLineSegment(sketch, "E2067", {"start": v(5.87, 6.23) * mm, "end": v(5.51, 6.2) * mm});
            skLineSegment(sketch, "E2068", {"start": v(5.51, 6.2) * mm, "end": v(5.15, 6.18) * mm});
            skLineSegment(sketch, "E2069", {"start": v(5.15, 6.18) * mm, "end": v(4.8, 6.17) * mm});
            skLineSegment(sketch, "E2070", {"start": v(4.8, 6.17) * mm, "end": v(4.43, 6.16) * mm});
            skLineSegment(sketch, "E2071", {"start": v(4.43, 6.16) * mm, "end": v(4.06, 6.17) * mm});
            skLineSegment(sketch, "E2072", {"start": v(4.06, 6.17) * mm, "end": v(3.7, 6.16) * mm});
            skLineSegment(sketch, "E2073", {"start": v(3.7, 6.16) * mm, "end": v(3.34, 6.15) * mm});
            skLineSegment(sketch, "E2074", {"start": v(3.34, 6.15) * mm, "end": v(2.98, 6.15) * mm});
            skLineSegment(sketch, "E2075", {"start": v(2.98, 6.15) * mm, "end": v(2.62, 6.17) * mm});
            skLineSegment(sketch, "E2076", {"start": v(2.62, 6.17) * mm, "end": v(2.26, 6.19) * mm});
            skLineSegment(sketch, "E2077", {"start": v(2.26, 6.19) * mm, "end": v(1.9, 6.22) * mm});
            skLineSegment(sketch, "E2078", {"start": v(1.9, 6.22) * mm, "end": v(1.54, 6.26) * mm});
            skLineSegment(sketch, "E2079", {"start": v(1.54, 6.26) * mm, "end": v(1.19, 6.3) * mm});
            skLineSegment(sketch, "E2080", {"start": v(1.19, 6.3) * mm, "end": v(0.84, 6.36) * mm});
            skLineSegment(sketch, "E2081", {"start": v(0.84, 6.36) * mm, "end": v(0.48, 6.43) * mm});
            skLineSegment(sketch, "E2082", {"start": v(0.48, 6.43) * mm, "end": v(0.13, 6.5) * mm});
            skLineSegment(sketch, "E2083", {"start": v(0.13, 6.5) * mm, "end": v(-0.21, 6.59) * mm});
            skLineSegment(sketch, "E2084", {"start": v(-0.21, 6.59) * mm, "end": v(-0.56, 6.68) * mm});
            skLineSegment(sketch, "E2085", {"start": v(-0.56, 6.68) * mm, "end": v(-0.9, 6.78) * mm});
            skLineSegment(sketch, "E2086", {"start": v(-0.9, 6.78) * mm, "end": v(-1.24, 6.88) * mm});
            skLineSegment(sketch, "E2087", {"start": v(-1.24, 6.88) * mm, "end": v(-1.58, 7) * mm});
            skLineSegment(sketch, "E2088", {"start": v(-1.58, 7) * mm, "end": v(-1.92, 7.12) * mm});
            skLineSegment(sketch, "E2089", {"start": v(-1.92, 7.12) * mm, "end": v(-2.25, 7.25) * mm});
            skLineSegment(sketch, "E2090", {"start": v(-2.25, 7.25) * mm, "end": v(-2.58, 7.4) * mm});
            skLineSegment(sketch, "E2091", {"start": v(-2.58, 7.4) * mm, "end": v(-2.9, 7.54) * mm});
            skLineSegment(sketch, "E2092", {"start": v(-2.9, 7.54) * mm, "end": v(-3.22, 7.7) * mm});
            skLineSegment(sketch, "E2093", {"start": v(-3.22, 7.7) * mm, "end": v(-3.54, 7.86) * mm});
            skLineSegment(sketch, "E2094", {"start": v(-3.54, 7.86) * mm, "end": v(-3.86, 8.03) * mm});
            skLineSegment(sketch, "E2095", {"start": v(-3.86, 8.03) * mm, "end": v(-4.17, 8.21) * mm});
            skLineSegment(sketch, "E2096", {"start": v(-4.17, 8.21) * mm, "end": v(-4.47, 8.4) * mm});
            skLineSegment(sketch, "E2097", {"start": v(-4.47, 8.4) * mm, "end": v(-4.77, 8.6) * mm});
            skLineSegment(sketch, "E2098", {"start": v(-4.77, 8.6) * mm, "end": v(-5.07, 8.8) * mm});
            skLineSegment(sketch, "E2099", {"start": v(-5.07, 8.8) * mm, "end": v(-5.36, 9) * mm});
            skLineSegment(sketch, "E2100", {"start": v(-5.36, 9) * mm, "end": v(-5.65, 9.22) * mm});
            skLineSegment(sketch, "E2101", {"start": v(-5.65, 9.22) * mm, "end": v(-5.93, 9.45) * mm});
            skLineSegment(sketch, "E2102", {"start": v(-5.93, 9.45) * mm, "end": v(-6.21, 9.68) * mm});
            skLineSegment(sketch, "E2103", {"start": v(-6.21, 9.68) * mm, "end": v(-6.48, 9.92) * mm});
            skLineSegment(sketch, "E2104", {"start": v(-6.48, 9.92) * mm, "end": v(-6.85, 10.32) * mm});
            skLineSegment(sketch, "E2105", {"start": v(-6.85, 10.32) * mm, "end": v(-7.2, 10.74) * mm});
            skLineSegment(sketch, "E2106", {"start": v(-7.2, 10.74) * mm, "end": v(-7.51, 11.17) * mm});
            skLineSegment(sketch, "E2107", {"start": v(-7.51, 11.17) * mm, "end": v(-7.81, 11.62) * mm});
            skLineSegment(sketch, "E2108", {"start": v(-7.81, 11.62) * mm, "end": v(-8.1, 12.08) * mm});
            skLineSegment(sketch, "E2109", {"start": v(-8.1, 12.08) * mm, "end": v(-8.35, 12.55) * mm});
            skLineSegment(sketch, "E2110", {"start": v(-8.35, 12.55) * mm, "end": v(-8.58, 13.03) * mm});
            skLineSegment(sketch, "E2111", {"start": v(-8.58, 13.03) * mm, "end": v(-8.8, 13.53) * mm});
            skLineSegment(sketch, "E2112", {"start": v(-8.8, 13.53) * mm, "end": v(-8.98, 14.03) * mm});
            skLineSegment(sketch, "E2113", {"start": v(-8.98, 14.03) * mm, "end": v(-9.14, 14.54) * mm});
            skLineSegment(sketch, "E2114", {"start": v(-9.14, 14.54) * mm, "end": v(-9.28, 15.06) * mm});
            skLineSegment(sketch, "E2115", {"start": v(-9.28, 15.06) * mm, "end": v(-9.4, 15.59) * mm});
            skLineSegment(sketch, "E2116", {"start": v(-9.4, 15.59) * mm, "end": v(-9.48, 16.12) * mm});
            skLineSegment(sketch, "E2117", {"start": v(-9.48, 16.12) * mm, "end": v(-9.55, 16.65) * mm});
            skLineSegment(sketch, "E2118", {"start": v(-9.55, 16.65) * mm, "end": v(-9.58, 17.2) * mm});
            skLineSegment(sketch, "E2119", {"start": v(-9.58, 17.2) * mm, "end": v(-9.6, 17.74) * mm});
            skLineSegment(sketch, "E2120", {"start": v(-9.6, 17.74) * mm, "end": v(-9.57, 18.26) * mm});
            skLineSegment(sketch, "E2121", {"start": v(-9.57, 18.26) * mm, "end": v(-9.52, 18.78) * mm});
            skLineSegment(sketch, "E2122", {"start": v(-9.52, 18.78) * mm, "end": v(-9.44, 19.3) * mm});
            skLineSegment(sketch, "E2123", {"start": v(-9.44, 19.3) * mm, "end": v(-9.33, 19.8) * mm});
            skLineSegment(sketch, "E2124", {"start": v(-9.33, 19.8) * mm, "end": v(-9.2, 20.31) * mm});
            skLineSegment(sketch, "E2125", {"start": v(-9.2, 20.31) * mm, "end": v(-9.04, 20.8) * mm});
            skLineSegment(sketch, "E2126", {"start": v(-9.04, 20.8) * mm, "end": v(-8.85, 21.3) * mm});
            skLineSegment(sketch, "E2127", {"start": v(-8.85, 21.3) * mm, "end": v(-8.64, 21.77) * mm});
            skLineSegment(sketch, "E2128", {"start": v(-8.64, 21.77) * mm, "end": v(-8.4, 22.23) * mm});
            skLineSegment(sketch, "E2129", {"start": v(-8.4, 22.23) * mm, "end": v(-8.15, 22.68) * mm});
            skLineSegment(sketch, "E2130", {"start": v(-8.15, 22.68) * mm, "end": v(-7.87, 23.12) * mm});
            skLineSegment(sketch, "E2131", {"start": v(-7.87, 23.12) * mm, "end": v(-7.57, 23.54) * mm});
            skLineSegment(sketch, "E2132", {"start": v(-7.57, 23.54) * mm, "end": v(-7.24, 23.94) * mm});
            skLineSegment(sketch, "E2133", {"start": v(-7.24, 23.94) * mm, "end": v(-6.9, 24.33) * mm});
            skLineSegment(sketch, "E2134", {"start": v(-6.9, 24.33) * mm, "end": v(-6.52, 24.7) * mm});
            skLineSegment(sketch, "E2135", {"start": v(-6.52, 24.7) * mm, "end": v(-6.13, 25.06) * mm});
            skLineSegment(sketch, "E2136", {"start": v(-6.13, 25.06) * mm, "end": v(-5.88, 25.3) * mm});
            skLineSegment(sketch, "E2137", {"start": v(-5.88, 25.3) * mm, "end": v(-5.61, 25.53) * mm});
            skLineSegment(sketch, "E2138", {"start": v(-5.61, 25.53) * mm, "end": v(-5.34, 25.76) * mm});
            skLineSegment(sketch, "E2139", {"start": v(-5.34, 25.76) * mm, "end": v(-5.07, 25.97) * mm});
            skLineSegment(sketch, "E2140", {"start": v(-5.07, 25.97) * mm, "end": v(-4.79, 26.19) * mm});
            skLineSegment(sketch, "E2141", {"start": v(-4.79, 26.19) * mm, "end": v(-4.5, 26.39) * mm});
            skLineSegment(sketch, "E2142", {"start": v(-4.5, 26.39) * mm, "end": v(-4.21, 26.58) * mm});
            skLineSegment(sketch, "E2143", {"start": v(-4.21, 26.58) * mm, "end": v(-3.92, 26.77) * mm});
            skLineSegment(sketch, "E2144", {"start": v(-3.92, 26.77) * mm, "end": v(-3.62, 26.95) * mm});
            skLineSegment(sketch, "E2145", {"start": v(-3.62, 26.95) * mm, "end": v(-3.32, 27.12) * mm});
            skLineSegment(sketch, "E2146", {"start": v(-3.32, 27.12) * mm, "end": v(-3.01, 27.28) * mm});
            skLineSegment(sketch, "E2147", {"start": v(-3.01, 27.28) * mm, "end": v(-2.7, 27.44) * mm});
            skLineSegment(sketch, "E2148", {"start": v(-2.7, 27.44) * mm, "end": v(-2.39, 27.59) * mm});
            skLineSegment(sketch, "E2149", {"start": v(-2.39, 27.59) * mm, "end": v(-2.07, 27.73) * mm});
            skLineSegment(sketch, "E2150", {"start": v(-2.07, 27.73) * mm, "end": v(-1.75, 27.86) * mm});
            skLineSegment(sketch, "E2151", {"start": v(-1.75, 27.86) * mm, "end": v(-1.42, 27.98) * mm});
            skLineSegment(sketch, "E2152", {"start": v(-1.42, 27.98) * mm, "end": v(-1.1, 28.1) * mm});
            skLineSegment(sketch, "E2153", {"start": v(-1.1, 28.1) * mm, "end": v(-0.77, 28.2) * mm});
            skLineSegment(sketch, "E2154", {"start": v(-0.77, 28.2) * mm, "end": v(-0.43, 28.3) * mm});
            skLineSegment(sketch, "E2155", {"start": v(-0.43, 28.3) * mm, "end": v(-0.1, 28.39) * mm});
            skLineSegment(sketch, "E2156", {"start": v(-0.1, 28.39) * mm, "end": v(0.24, 28.47) * mm});
            skLineSegment(sketch, "E2157", {"start": v(0.24, 28.47) * mm, "end": v(0.58, 28.54) * mm});
            skLineSegment(sketch, "E2158", {"start": v(0.58, 28.54) * mm, "end": v(0.92, 28.6) * mm});
            skLineSegment(sketch, "E2159", {"start": v(0.92, 28.6) * mm, "end": v(1.27, 28.66) * mm});
            skLineSegment(sketch, "E2160", {"start": v(1.27, 28.66) * mm, "end": v(1.61, 28.7) * mm});
            skLineSegment(sketch, "E2161", {"start": v(1.61, 28.7) * mm, "end": v(1.96, 28.74) * mm});
            skLineSegment(sketch, "E2162", {"start": v(1.96, 28.74) * mm, "end": v(2.3, 28.77) * mm});
            skLineSegment(sketch, "E2163", {"start": v(2.3, 28.77) * mm, "end": v(2.66, 28.79) * mm});
            skLineSegment(sketch, "E2164", {"start": v(2.66, 28.79) * mm, "end": v(3, 28.8) * mm});
            skLineSegment(sketch, "E2165", {"start": v(3, 28.8) * mm, "end": v(3.36, 28.8) * mm});
            skLineSegment(sketch, "E2166", {"start": v(3.36, 28.8) * mm, "end": v(3.71, 28.79) * mm});
            skLineSegment(sketch, "E2167", {"start": v(3.71, 28.79) * mm, "end": v(4.06, 28.77) * mm});
            skLineSegment(sketch, "E2168", {"start": v(4.06, 28.77) * mm, "end": v(4.41, 28.78) * mm});
            skLineSegment(sketch, "E2169", {"start": v(4.41, 28.78) * mm, "end": v(4.76, 28.79) * mm});
            skLineSegment(sketch, "E2170", {"start": v(4.76, 28.79) * mm, "end": v(5.11, 28.78) * mm});
            skLineSegment(sketch, "E2171", {"start": v(5.11, 28.78) * mm, "end": v(5.46, 28.76) * mm});
            skLineSegment(sketch, "E2172", {"start": v(5.46, 28.76) * mm, "end": v(5.8, 28.74) * mm});
            skLineSegment(sketch, "E2173", {"start": v(5.8, 28.74) * mm, "end": v(6.15, 28.7) * mm});
            skLineSegment(sketch, "E2174", {"start": v(6.15, 28.7) * mm, "end": v(6.5, 28.67) * mm});
            skLineSegment(sketch, "E2175", {"start": v(6.5, 28.67) * mm, "end": v(6.84, 28.62) * mm});
            skLineSegment(sketch, "E2176", {"start": v(6.84, 28.62) * mm, "end": v(7.18, 28.56) * mm});
            skLineSegment(sketch, "E2177", {"start": v(7.18, 28.56) * mm, "end": v(7.52, 28.5) * mm});
            skLineSegment(sketch, "E2178", {"start": v(7.52, 28.5) * mm, "end": v(7.85, 28.42) * mm});
            skLineSegment(sketch, "E2179", {"start": v(7.85, 28.42) * mm, "end": v(8.19, 28.33) * mm});
            skLineSegment(sketch, "E2180", {"start": v(8.19, 28.33) * mm, "end": v(8.52, 28.24) * mm});
            skLineSegment(sketch, "E2181", {"start": v(8.52, 28.24) * mm, "end": v(8.85, 28.14) * mm});
            skLineSegment(sketch, "E2182", {"start": v(8.85, 28.14) * mm, "end": v(9.18, 28.04) * mm});
            skLineSegment(sketch, "E2183", {"start": v(9.18, 28.04) * mm, "end": v(9.5, 27.92) * mm});
            skLineSegment(sketch, "E2184", {"start": v(9.5, 27.92) * mm, "end": v(9.82, 27.8) * mm});
            skLineSegment(sketch, "E2185", {"start": v(9.82, 27.8) * mm, "end": v(10.14, 27.66) * mm});
            skLineSegment(sketch, "E2186", {"start": v(10.14, 27.66) * mm, "end": v(10.46, 27.52) * mm});
            skLineSegment(sketch, "E2187", {"start": v(10.46, 27.52) * mm, "end": v(10.77, 27.37) * mm});
            skLineSegment(sketch, "E2188", {"start": v(10.77, 27.37) * mm, "end": v(11.08, 27.22) * mm});
            skLineSegment(sketch, "E2189", {"start": v(11.08, 27.22) * mm, "end": v(11.38, 27.06) * mm});
            skLineSegment(sketch, "E2190", {"start": v(11.38, 27.06) * mm, "end": v(11.68, 26.88) * mm});
            skLineSegment(sketch, "E2191", {"start": v(11.68, 26.88) * mm, "end": v(11.98, 26.7) * mm});
            skLineSegment(sketch, "E2192", {"start": v(11.98, 26.7) * mm, "end": v(12.27, 26.52) * mm});
            skLineSegment(sketch, "E2193", {"start": v(12.27, 26.52) * mm, "end": v(12.55, 26.33) * mm});
            skLineSegment(sketch, "E2194", {"start": v(12.55, 26.33) * mm, "end": v(12.84, 26.12) * mm});
            skLineSegment(sketch, "E2195", {"start": v(12.84, 26.12) * mm, "end": v(13.11, 25.92) * mm});
            skLineSegment(sketch, "E2196", {"start": v(13.11, 25.92) * mm, "end": v(13.39, 25.7) * mm});
            skLineSegment(sketch, "E2197", {"start": v(13.39, 25.7) * mm, "end": v(13.65, 25.48) * mm});
            skLineSegment(sketch, "E2198", {"start": v(13.65, 25.48) * mm, "end": v(13.92, 25.25) * mm});
            skLineSegment(sketch, "E2199", {"start": v(13.92, 25.25) * mm, "end": v(14.17, 25) * mm});
            skLineSegment(sketch, "E2200", {"start": v(14.17, 25) * mm, "end": v(14.54, 24.65) * mm});
            skLineSegment(sketch, "E2201", {"start": v(14.54, 24.65) * mm, "end": v(14.9, 24.27) * mm});
            skLineSegment(sketch, "E2202", {"start": v(14.9, 24.27) * mm, "end": v(15.22, 23.88) * mm});
            skLineSegment(sketch, "E2203", {"start": v(15.22, 23.88) * mm, "end": v(15.52, 23.47) * mm});
            skLineSegment(sketch, "E2204", {"start": v(15.52, 23.47) * mm, "end": v(15.8, 23.05) * mm});
            skLineSegment(sketch, "E2205", {"start": v(15.8, 23.05) * mm, "end": v(16.07, 22.61) * mm});
            skLineSegment(sketch, "E2206", {"start": v(16.07, 22.61) * mm, "end": v(16.3, 22.16) * mm});
            skLineSegment(sketch, "E2207", {"start": v(16.3, 22.16) * mm, "end": v(16.52, 21.7) * mm});
            skLineSegment(sketch, "E2208", {"start": v(16.52, 21.7) * mm, "end": v(16.72, 21.23) * mm});
            skLineSegment(sketch, "E2209", {"start": v(16.72, 21.23) * mm, "end": v(16.89, 20.75) * mm});
            skLineSegment(sketch, "E2210", {"start": v(16.89, 20.75) * mm, "end": v(17.03, 20.27) * mm});
            skLineSegment(sketch, "E2211", {"start": v(17.03, 20.27) * mm, "end": v(17.15, 19.77) * mm});
            skLineSegment(sketch, "E2212", {"start": v(17.15, 19.77) * mm, "end": v(17.25, 19.27) * mm});
            skLineSegment(sketch, "E2213", {"start": v(17.25, 19.27) * mm, "end": v(17.32, 18.76) * mm});
            skLineSegment(sketch, "E2214", {"start": v(17.32, 18.76) * mm, "end": v(17.36, 18.25) * mm});
            skLineSegment(sketch, "E2215", {"start": v(17.36, 18.25) * mm, "end": v(17.38, 17.74) * mm});
            skLineSegment(sketch, "E2216", {"start": v(16.96, 55.67) * mm, "end": v(-9.18, 55.67) * mm});
            skLineSegment(sketch, "E2217", {"start": v(7.52, 55.67) * mm, "end": v(8, 55.65) * mm});
            skLineSegment(sketch, "E2218", {"start": v(8, 55.65) * mm, "end": v(8.47, 55.61) * mm});
            skLineSegment(sketch, "E2219", {"start": v(8.47, 55.61) * mm, "end": v(8.94, 55.54) * mm});
            skLineSegment(sketch, "E2220", {"start": v(8.94, 55.54) * mm, "end": v(9.4, 55.45) * mm});
            skLineSegment(sketch, "E2221", {"start": v(9.4, 55.45) * mm, "end": v(9.87, 55.34) * mm});
            skLineSegment(sketch, "E2222", {"start": v(9.87, 55.34) * mm, "end": v(10.32, 55.2) * mm});
            skLineSegment(sketch, "E2223", {"start": v(10.32, 55.2) * mm, "end": v(10.76, 55.05) * mm});
            skLineSegment(sketch, "E2224", {"start": v(10.76, 55.05) * mm, "end": v(11.2, 54.87) * mm});
            skLineSegment(sketch, "E2225", {"start": v(11.2, 54.87) * mm, "end": v(11.62, 54.67) * mm});
            skLineSegment(sketch, "E2226", {"start": v(11.62, 54.67) * mm, "end": v(12.04, 54.45) * mm});
            skLineSegment(sketch, "E2227", {"start": v(12.04, 54.45) * mm, "end": v(12.44, 54.2) * mm});
            skLineSegment(sketch, "E2228", {"start": v(12.44, 54.2) * mm, "end": v(12.84, 53.94) * mm});
            skLineSegment(sketch, "E2229", {"start": v(12.84, 53.94) * mm, "end": v(13.22, 53.66) * mm});
            skLineSegment(sketch, "E2230", {"start": v(13.22, 53.66) * mm, "end": v(13.58, 53.36) * mm});
            skLineSegment(sketch, "E2231", {"start": v(13.58, 53.36) * mm, "end": v(13.94, 53.04) * mm});
            skLineSegment(sketch, "E2232", {"start": v(13.94, 53.04) * mm, "end": v(14.27, 52.7) * mm});
            skLineSegment(sketch, "E2233", {"start": v(14.27, 52.7) * mm, "end": v(14.6, 52.36) * mm});
            skLineSegment(sketch, "E2234", {"start": v(14.6, 52.36) * mm, "end": v(14.93, 52) * mm});
            skLineSegment(sketch, "E2235", {"start": v(14.93, 52) * mm, "end": v(15.23, 51.62) * mm});
            skLineSegment(sketch, "E2236", {"start": v(15.23, 51.62) * mm, "end": v(15.5, 51.24) * mm});
            skLineSegment(sketch, "E2237", {"start": v(15.5, 51.24) * mm, "end": v(15.77, 50.84) * mm});
            skLineSegment(sketch, "E2238", {"start": v(15.77, 50.84) * mm, "end": v(16, 50.43) * mm});
            skLineSegment(sketch, "E2239", {"start": v(16, 50.43) * mm, "end": v(16.23, 50) * mm});
            skLineSegment(sketch, "E2240", {"start": v(16.23, 50) * mm, "end": v(16.42, 49.57) * mm});
            skLineSegment(sketch, "E2241", {"start": v(16.42, 49.57) * mm, "end": v(16.6, 49.13) * mm});
            skLineSegment(sketch, "E2242", {"start": v(16.6, 49.13) * mm, "end": v(16.75, 48.68) * mm});
            skLineSegment(sketch, "E2243", {"start": v(16.75, 48.68) * mm, "end": v(16.88, 48.22) * mm});
            skLineSegment(sketch, "E2244", {"start": v(16.88, 48.22) * mm, "end": v(17, 47.76) * mm});
            skLineSegment(sketch, "E2245", {"start": v(17, 47.76) * mm, "end": v(17.08, 47.3) * mm});
            skLineSegment(sketch, "E2246", {"start": v(17.08, 47.3) * mm, "end": v(17.14, 46.82) * mm});
            skLineSegment(sketch, "E2247", {"start": v(17.14, 46.82) * mm, "end": v(17.18, 46.34) * mm});
            skLineSegment(sketch, "E2248", {"start": v(17.18, 46.34) * mm, "end": v(17.2, 45.86) * mm});
            skLineSegment(sketch, "E2249", {"start": v(17.2, 45.86) * mm, "end": v(17.23, 45.38) * mm});
            skLineSegment(sketch, "E2250", {"start": v(17.23, 45.38) * mm, "end": v(17.25, 44.91) * mm});
            skLineSegment(sketch, "E2251", {"start": v(17.25, 44.91) * mm, "end": v(17.24, 44.45) * mm});
            skLineSegment(sketch, "E2252", {"start": v(17.24, 44.45) * mm, "end": v(17.2, 43.98) * mm});
            skLineSegment(sketch, "E2253", {"start": v(17.2, 43.98) * mm, "end": v(17.14, 43.52) * mm});
            skLineSegment(sketch, "E2254", {"start": v(17.14, 43.52) * mm, "end": v(17.07, 43.06) * mm});
            skLineSegment(sketch, "E2255", {"start": v(17.07, 43.06) * mm, "end": v(16.96, 42.6) * mm});
            skLineSegment(sketch, "E2256", {"start": v(16.96, 42.6) * mm, "end": v(16.84, 42.15) * mm});
            skLineSegment(sketch, "E2257", {"start": v(16.84, 42.15) * mm, "end": v(16.7, 41.71) * mm});
            skLineSegment(sketch, "E2258", {"start": v(16.7, 41.71) * mm, "end": v(16.52, 41.28) * mm});
            skLineSegment(sketch, "E2259", {"start": v(16.52, 41.28) * mm, "end": v(16.34, 40.85) * mm});
            skLineSegment(sketch, "E2260", {"start": v(16.34, 40.85) * mm, "end": v(16.12, 40.43) * mm});
            skLineSegment(sketch, "E2261", {"start": v(16.12, 40.43) * mm, "end": v(15.9, 40.03) * mm});
            skLineSegment(sketch, "E2262", {"start": v(15.9, 40.03) * mm, "end": v(15.64, 39.63) * mm});
            skLineSegment(sketch, "E2263", {"start": v(15.64, 39.63) * mm, "end": v(15.37, 39.25) * mm});
            skLineSegment(sketch, "E2264", {"start": v(15.37, 39.25) * mm, "end": v(15.08, 38.88) * mm});
            skLineSegment(sketch, "E2265", {"start": v(15.08, 38.88) * mm, "end": v(14.76, 38.6) * mm});
            skLineSegment(sketch, "E2266", {"start": v(14.76, 38.6) * mm, "end": v(14.43, 38.33) * mm});
            skLineSegment(sketch, "E2267", {"start": v(14.43, 38.33) * mm, "end": v(14.09, 38.08) * mm});
            skLineSegment(sketch, "E2268", {"start": v(14.09, 38.08) * mm, "end": v(13.74, 37.86) * mm});
            skLineSegment(sketch, "E2269", {"start": v(13.74, 37.86) * mm, "end": v(13.37, 37.65) * mm});
            skLineSegment(sketch, "E2270", {"start": v(13.37, 37.65) * mm, "end": v(13, 37.46) * mm});
            skLineSegment(sketch, "E2271", {"start": v(13, 37.46) * mm, "end": v(12.62, 37.29) * mm});
            skLineSegment(sketch, "E2272", {"start": v(12.62, 37.29) * mm, "end": v(12.23, 37.14) * mm});
            skLineSegment(sketch, "E2273", {"start": v(12.23, 37.14) * mm, "end": v(11.83, 37) * mm});
            skLineSegment(sketch, "E2274", {"start": v(11.83, 37) * mm, "end": v(11.43, 36.9) * mm});
            skLineSegment(sketch, "E2275", {"start": v(11.43, 36.9) * mm, "end": v(11.02, 36.8) * mm});
            skLineSegment(sketch, "E2276", {"start": v(11.02, 36.8) * mm, "end": v(10.61, 36.74) * mm});
            skLineSegment(sketch, "E2277", {"start": v(10.61, 36.74) * mm, "end": v(10.2, 36.69) * mm});
            skLineSegment(sketch, "E2278", {"start": v(10.2, 36.69) * mm, "end": v(9.77, 36.66) * mm});
            skLineSegment(sketch, "E2279", {"start": v(9.77, 36.66) * mm, "end": v(9.35, 36.66) * mm});
            skLineSegment(sketch, "E2280", {"start": v(9.35, 36.66) * mm, "end": v(8.93, 36.67) * mm});
            skLineSegment(sketch, "E2281", {"start": v(8.93, 36.67) * mm, "end": v(-9.18, 36.67) * mm});
            skLineSegment(sketch, "E2282", {"start": v(16.82, 72) * mm, "end": v(16.94, 71.78) * mm});
            skLineSegment(sketch, "E2283", {"start": v(16.94, 71.78) * mm, "end": v(17.05, 71.54) * mm});
            skLineSegment(sketch, "E2284", {"start": v(17.05, 71.54) * mm, "end": v(17.14, 71.3) * mm});
            skLineSegment(sketch, "E2285", {"start": v(17.14, 71.3) * mm, "end": v(17.21, 71.05) * mm});
            skLineSegment(sketch, "E2286", {"start": v(17.21, 71.05) * mm, "end": v(17.27, 70.8) * mm});
            skLineSegment(sketch, "E2287", {"start": v(17.27, 70.8) * mm, "end": v(17.3, 70.53) * mm});
            skLineSegment(sketch, "E2288", {"start": v(17.3, 70.53) * mm, "end": v(17.32, 70.27) * mm});
            skLineSegment(sketch, "E2289", {"start": v(17.32, 70.27) * mm, "end": v(17.32, 70.01) * mm});
            skLineSegment(sketch, "E2290", {"start": v(17.32, 70.01) * mm, "end": v(17.32, 69.82) * mm});
            skLineSegment(sketch, "E2291", {"start": v(17.32, 69.82) * mm, "end": v(17.3, 69.63) * mm});
            skLineSegment(sketch, "E2292", {"start": v(17.3, 69.63) * mm, "end": v(17.3, 69.44) * mm});
            skLineSegment(sketch, "E2293", {"start": v(17.3, 69.44) * mm, "end": v(17.26, 69.26) * mm});
            skLineSegment(sketch, "E2294", {"start": v(17.26, 69.26) * mm, "end": v(17.23, 69.07) * mm});
            skLineSegment(sketch, "E2295", {"start": v(17.23, 69.07) * mm, "end": v(17.18, 68.89) * mm});
            skLineSegment(sketch, "E2296", {"start": v(17.18, 68.89) * mm, "end": v(17.13, 68.7) * mm});
            skLineSegment(sketch, "E2297", {"start": v(17.13, 68.7) * mm, "end": v(17.07, 68.53) * mm});
            skLineSegment(sketch, "E2298", {"start": v(17.07, 68.53) * mm, "end": v(17, 68.35) * mm});
            skLineSegment(sketch, "E2299", {"start": v(17, 68.35) * mm, "end": v(16.93, 68.18) * mm});
            skLineSegment(sketch, "E2300", {"start": v(16.93, 68.18) * mm, "end": v(16.84, 68.01) * mm});
            skLineSegment(sketch, "E2301", {"start": v(16.84, 68.01) * mm, "end": v(16.75, 67.85) * mm});
            skLineSegment(sketch, "E2302", {"start": v(16.75, 67.85) * mm, "end": v(16.65, 67.69) * mm});
            skLineSegment(sketch, "E2303", {"start": v(16.65, 67.69) * mm, "end": v(16.55, 67.53) * mm});
            skLineSegment(sketch, "E2304", {"start": v(16.55, 67.53) * mm, "end": v(16.43, 67.38) * mm});
            skLineSegment(sketch, "E2305", {"start": v(16.43, 67.38) * mm, "end": v(16.31, 67.23) * mm});
            skLineSegment(sketch, "E2306", {"start": v(16.31, 67.23) * mm, "end": v(16.2, 67.11) * mm});
            skLineSegment(sketch, "E2307", {"start": v(16.2, 67.11) * mm, "end": v(16.07, 67) * mm});
            skLineSegment(sketch, "E2308", {"start": v(16.07, 67) * mm, "end": v(15.93, 66.9) * mm});
            skLineSegment(sketch, "E2309", {"start": v(15.93, 66.9) * mm, "end": v(15.8, 66.8) * mm});
            skLineSegment(sketch, "E2310", {"start": v(15.8, 66.8) * mm, "end": v(15.66, 66.7) * mm});
            skLineSegment(sketch, "E2311", {"start": v(15.66, 66.7) * mm, "end": v(15.5, 66.62) * mm});
            skLineSegment(sketch, "E2312", {"start": v(15.5, 66.62) * mm, "end": v(15.36, 66.54) * mm});
            skLineSegment(sketch, "E2313", {"start": v(15.36, 66.54) * mm, "end": v(15.2, 66.47) * mm});
            skLineSegment(sketch, "E2314", {"start": v(15.2, 66.47) * mm, "end": v(15.05, 66.41) * mm});
            skLineSegment(sketch, "E2315", {"start": v(15.05, 66.41) * mm, "end": v(14.9, 66.36) * mm});
            skLineSegment(sketch, "E2316", {"start": v(14.9, 66.36) * mm, "end": v(14.73, 66.31) * mm});
            skLineSegment(sketch, "E2317", {"start": v(14.73, 66.31) * mm, "end": v(14.57, 66.27) * mm});
            skLineSegment(sketch, "E2318", {"start": v(14.57, 66.27) * mm, "end": v(14.4, 66.24) * mm});
            skLineSegment(sketch, "E2319", {"start": v(14.4, 66.24) * mm, "end": v(14.23, 66.22) * mm});
            skLineSegment(sketch, "E2320", {"start": v(14.23, 66.22) * mm, "end": v(14.06, 66.21) * mm});
            skLineSegment(sketch, "E2321", {"start": v(14.06, 66.21) * mm, "end": v(13.9, 66.2) * mm});
            skLineSegment(sketch, "E2322", {"start": v(13.9, 66.2) * mm, "end": v(-16.47, 66.2) * mm});
            skLineSegment(sketch, "E2323", {"start": v(-9.34, 63.57) * mm, "end": v(-9.34, 71.63) * mm});
            skLineSegment(sketch, "E2324", {"start": v(183.56, 16.18) * mm, "end": v(183.96, 16.31) * mm});
            skLineSegment(sketch, "E2325", {"start": v(183.96, 16.31) * mm, "end": v(184.34, 16.46) * mm});
            skLineSegment(sketch, "E2326", {"start": v(184.34, 16.46) * mm, "end": v(184.73, 16.61) * mm});
            skLineSegment(sketch, "E2327", {"start": v(184.73, 16.61) * mm, "end": v(185.1, 16.78) * mm});
            skLineSegment(sketch, "E2328", {"start": v(185.1, 16.78) * mm, "end": v(185.47, 16.96) * mm});
            skLineSegment(sketch, "E2329", {"start": v(185.47, 16.96) * mm, "end": v(185.84, 17.15) * mm});
            skLineSegment(sketch, "E2330", {"start": v(185.84, 17.15) * mm, "end": v(186.2, 17.35) * mm});
            skLineSegment(sketch, "E2331", {"start": v(186.2, 17.35) * mm, "end": v(186.55, 17.57) * mm});
            skLineSegment(sketch, "E2332", {"start": v(186.55, 17.57) * mm, "end": v(186.9, 17.8) * mm});
            skLineSegment(sketch, "E2333", {"start": v(186.9, 17.8) * mm, "end": v(187.23, 18.03) * mm});
            skLineSegment(sketch, "E2334", {"start": v(187.23, 18.03) * mm, "end": v(187.56, 18.27) * mm});
            skLineSegment(sketch, "E2335", {"start": v(187.56, 18.27) * mm, "end": v(187.89, 18.53) * mm});
            skLineSegment(sketch, "E2336", {"start": v(187.89, 18.53) * mm, "end": v(188.2, 18.8) * mm});
            skLineSegment(sketch, "E2337", {"start": v(188.2, 18.8) * mm, "end": v(188.5, 19.07) * mm});
            skLineSegment(sketch, "E2338", {"start": v(188.5, 19.07) * mm, "end": v(188.8, 19.36) * mm});
            skLineSegment(sketch, "E2339", {"start": v(188.8, 19.36) * mm, "end": v(189.1, 19.66) * mm});
            skLineSegment(sketch, "E2340", {"start": v(189.1, 19.66) * mm, "end": v(189.32, 19.9) * mm});
            skLineSegment(sketch, "E2341", {"start": v(189.32, 19.9) * mm, "end": v(189.55, 20.16) * mm});
            skLineSegment(sketch, "E2342", {"start": v(189.55, 20.16) * mm, "end": v(189.76, 20.41) * mm});
            skLineSegment(sketch, "E2343", {"start": v(189.76, 20.41) * mm, "end": v(189.97, 20.68) * mm});
            skLineSegment(sketch, "E2344", {"start": v(189.97, 20.68) * mm, "end": v(190.17, 20.94) * mm});
            skLineSegment(sketch, "E2345", {"start": v(190.17, 20.94) * mm, "end": v(190.37, 21.21) * mm});
            skLineSegment(sketch, "E2346", {"start": v(190.37, 21.21) * mm, "end": v(190.55, 21.5) * mm});
            skLineSegment(sketch, "E2347", {"start": v(190.55, 21.5) * mm, "end": v(190.73, 21.77) * mm});
            skLineSegment(sketch, "E2348", {"start": v(190.73, 21.77) * mm, "end": v(190.9, 22.06) * mm});
            skLineSegment(sketch, "E2349", {"start": v(190.9, 22.06) * mm, "end": v(191.07, 22.35) * mm});
            skLineSegment(sketch, "E2350", {"start": v(191.07, 22.35) * mm, "end": v(191.23, 22.64) * mm});
            skLineSegment(sketch, "E2351", {"start": v(191.23, 22.64) * mm, "end": v(191.38, 22.93) * mm});
            skLineSegment(sketch, "E2352", {"start": v(191.38, 22.93) * mm, "end": v(191.52, 23.23) * mm});
            skLineSegment(sketch, "E2353", {"start": v(191.52, 23.23) * mm, "end": v(191.65, 23.54) * mm});
            skLineSegment(sketch, "E2354", {"start": v(191.65, 23.54) * mm, "end": v(191.78, 23.84) * mm});
            skLineSegment(sketch, "E2355", {"start": v(191.78, 23.84) * mm, "end": v(191.9, 24.15) * mm});
            skLineSegment(sketch, "E2356", {"start": v(191.9, 24.15) * mm, "end": v(192, 24.47) * mm});
            skLineSegment(sketch, "E2357", {"start": v(192, 24.47) * mm, "end": v(192.11, 24.78) * mm});
            skLineSegment(sketch, "E2358", {"start": v(192.11, 24.78) * mm, "end": v(192.2, 25.1) * mm});
            skLineSegment(sketch, "E2359", {"start": v(192.2, 25.1) * mm, "end": v(192.3, 25.42) * mm});
            skLineSegment(sketch, "E2360", {"start": v(192.3, 25.42) * mm, "end": v(192.37, 25.74) * mm});
            skLineSegment(sketch, "E2361", {"start": v(192.37, 25.74) * mm, "end": v(192.44, 26.07) * mm});
            skLineSegment(sketch, "E2362", {"start": v(192.44, 26.07) * mm, "end": v(192.5, 26.4) * mm});
            skLineSegment(sketch, "E2363", {"start": v(192.5, 26.4) * mm, "end": v(192.56, 26.72) * mm});
            skLineSegment(sketch, "E2364", {"start": v(192.56, 26.72) * mm, "end": v(192.6, 27.05) * mm});
            skLineSegment(sketch, "E2365", {"start": v(192.6, 27.05) * mm, "end": v(192.64, 27.39) * mm});
            skLineSegment(sketch, "E2366", {"start": v(192.64, 27.39) * mm, "end": v(192.67, 27.72) * mm});
            skLineSegment(sketch, "E2367", {"start": v(192.67, 27.72) * mm, "end": v(192.69, 28.05) * mm});
            skLineSegment(sketch, "E2368", {"start": v(192.69, 28.05) * mm, "end": v(192.7, 28.39) * mm});
            skLineSegment(sketch, "E2369", {"start": v(192.7, 28.39) * mm, "end": v(192.7, 28.72) * mm});
            skLineSegment(sketch, "E2370", {"start": v(192.7, 28.72) * mm, "end": v(192.7, 29.06) * mm});
            skLineSegment(sketch, "E2371", {"start": v(192.7, 29.06) * mm, "end": v(192.68, 29.4) * mm});
            skLineSegment(sketch, "E2372", {"start": v(192.68, 29.4) * mm, "end": v(192.7, 29.7) * mm});
            skLineSegment(sketch, "E2373", {"start": v(192.7, 29.7) * mm, "end": v(192.7, 30.02) * mm});
            skLineSegment(sketch, "E2374", {"start": v(192.7, 30.02) * mm, "end": v(192.69, 30.32) * mm});
            skLineSegment(sketch, "E2375", {"start": v(192.69, 30.32) * mm, "end": v(192.67, 30.63) * mm});
            skLineSegment(sketch, "E2376", {"start": v(192.67, 30.63) * mm, "end": v(192.65, 30.94) * mm});
            skLineSegment(sketch, "E2377", {"start": v(192.65, 30.94) * mm, "end": v(192.62, 31.24) * mm});
            skLineSegment(sketch, "E2378", {"start": v(192.62, 31.24) * mm, "end": v(192.58, 31.55) * mm});
            skLineSegment(sketch, "E2379", {"start": v(192.58, 31.55) * mm, "end": v(192.53, 31.85) * mm});
            skLineSegment(sketch, "E2380", {"start": v(192.53, 31.85) * mm, "end": v(192.48, 32.15) * mm});
            skLineSegment(sketch, "E2381", {"start": v(192.48, 32.15) * mm, "end": v(192.42, 32.45) * mm});
            skLineSegment(sketch, "E2382", {"start": v(192.42, 32.45) * mm, "end": v(192.35, 32.75) * mm});
            skLineSegment(sketch, "E2383", {"start": v(192.35, 32.75) * mm, "end": v(192.27, 33.04) * mm});
            skLineSegment(sketch, "E2384", {"start": v(192.27, 33.04) * mm, "end": v(192.19, 33.34) * mm});
            skLineSegment(sketch, "E2385", {"start": v(192.19, 33.34) * mm, "end": v(192.1, 33.63) * mm});
            skLineSegment(sketch, "E2386", {"start": v(192.1, 33.63) * mm, "end": v(192, 33.92) * mm});
            skLineSegment(sketch, "E2387", {"start": v(192, 33.92) * mm, "end": v(191.9, 34.2) * mm});
            skLineSegment(sketch, "E2388", {"start": v(191.9, 34.2) * mm, "end": v(191.78, 34.49) * mm});
            skLineSegment(sketch, "E2389", {"start": v(191.78, 34.49) * mm, "end": v(191.66, 34.77) * mm});
            skLineSegment(sketch, "E2390", {"start": v(191.66, 34.77) * mm, "end": v(191.53, 35.04) * mm});
            skLineSegment(sketch, "E2391", {"start": v(191.53, 35.04) * mm, "end": v(191.4, 35.32) * mm});
            skLineSegment(sketch, "E2392", {"start": v(191.4, 35.32) * mm, "end": v(191.25, 35.59) * mm});
            skLineSegment(sketch, "E2393", {"start": v(191.25, 35.59) * mm, "end": v(191.1, 35.85) * mm});
            skLineSegment(sketch, "E2394", {"start": v(191.1, 35.85) * mm, "end": v(190.95, 36.12) * mm});
            skLineSegment(sketch, "E2395", {"start": v(190.95, 36.12) * mm, "end": v(190.79, 36.38) * mm});
            skLineSegment(sketch, "E2396", {"start": v(190.79, 36.38) * mm, "end": v(190.62, 36.63) * mm});
            skLineSegment(sketch, "E2397", {"start": v(190.62, 36.63) * mm, "end": v(190.44, 36.88) * mm});
            skLineSegment(sketch, "E2398", {"start": v(190.44, 36.88) * mm, "end": v(190.26, 37.13) * mm});
            skLineSegment(sketch, "E2399", {"start": v(190.26, 37.13) * mm, "end": v(190.07, 37.37) * mm});
            skLineSegment(sketch, "E2400", {"start": v(190.07, 37.37) * mm, "end": v(189.87, 37.6) * mm});
            skLineSegment(sketch, "E2401", {"start": v(189.87, 37.6) * mm, "end": v(189.67, 37.84) * mm});
            skLineSegment(sketch, "E2402", {"start": v(189.67, 37.84) * mm, "end": v(189.46, 38.07) * mm});
            skLineSegment(sketch, "E2403", {"start": v(189.46, 38.07) * mm, "end": v(189.25, 38.3) * mm});
            skLineSegment(sketch, "E2404", {"start": v(189.25, 38.3) * mm, "end": v(188.95, 38.6) * mm});
            skLineSegment(sketch, "E2405", {"start": v(188.95, 38.6) * mm, "end": v(188.64, 38.88) * mm});
            skLineSegment(sketch, "E2406", {"start": v(188.64, 38.88) * mm, "end": v(188.32, 39.15) * mm});
            skLineSegment(sketch, "E2407", {"start": v(188.32, 39.15) * mm, "end": v(187.99, 39.4) * mm});
            skLineSegment(sketch, "E2408", {"start": v(187.99, 39.4) * mm, "end": v(187.65, 39.63) * mm});
            skLineSegment(sketch, "E2409", {"start": v(187.65, 39.63) * mm, "end": v(187.3, 39.85) * mm});
            skLineSegment(sketch, "E2410", {"start": v(187.3, 39.85) * mm, "end": v(186.94, 40.05) * mm});
            skLineSegment(sketch, "E2411", {"start": v(186.94, 40.05) * mm, "end": v(186.58, 40.23) * mm});
            skLineSegment(sketch, "E2412", {"start": v(186.58, 40.23) * mm, "end": v(186.2, 40.4) * mm});
            skLineSegment(sketch, "E2413", {"start": v(186.2, 40.4) * mm, "end": v(185.83, 40.54) * mm});
            skLineSegment(sketch, "E2414", {"start": v(185.83, 40.54) * mm, "end": v(185.44, 40.66) * mm});
            skLineSegment(sketch, "E2415", {"start": v(185.44, 40.66) * mm, "end": v(185.06, 40.77) * mm});
            skLineSegment(sketch, "E2416", {"start": v(185.06, 40.77) * mm, "end": v(184.67, 40.86) * mm});
            skLineSegment(sketch, "E2417", {"start": v(184.67, 40.86) * mm, "end": v(184.27, 40.94) * mm});
            skLineSegment(sketch, "E2418", {"start": v(184.27, 40.94) * mm, "end": v(183.88, 41) * mm});
            skLineSegment(sketch, "E2419", {"start": v(183.88, 41) * mm, "end": v(183.48, 41.03) * mm});
            skLineSegment(sketch, "E2420", {"start": v(183.48, 41.03) * mm, "end": v(183.08, 41.05) * mm});
            skLineSegment(sketch, "E2421", {"start": v(183.08, 41.05) * mm, "end": v(182.68, 41.05) * mm});
            skLineSegment(sketch, "E2422", {"start": v(182.68, 41.05) * mm, "end": v(182.27, 41.04) * mm});
            skLineSegment(sketch, "E2423", {"start": v(182.27, 41.04) * mm, "end": v(181.87, 41) * mm});
            skLineSegment(sketch, "E2424", {"start": v(181.87, 41) * mm, "end": v(181.48, 40.95) * mm});
            skLineSegment(sketch, "E2425", {"start": v(181.48, 40.95) * mm, "end": v(181.08, 40.88) * mm});
            skLineSegment(sketch, "E2426", {"start": v(181.08, 40.88) * mm, "end": v(180.68, 40.8) * mm});
            skLineSegment(sketch, "E2427", {"start": v(180.68, 40.8) * mm, "end": v(180.3, 40.68) * mm});
            skLineSegment(sketch, "E2428", {"start": v(180.3, 40.68) * mm, "end": v(179.9, 40.56) * mm});
            skLineSegment(sketch, "E2429", {"start": v(179.9, 40.56) * mm, "end": v(179.53, 40.41) * mm});
            skLineSegment(sketch, "E2430", {"start": v(179.53, 40.41) * mm, "end": v(179.15, 40.25) * mm});
            skLineSegment(sketch, "E2431", {"start": v(179.15, 40.25) * mm, "end": v(178.78, 40.07) * mm});
            skLineSegment(sketch, "E2432", {"start": v(178.78, 40.07) * mm, "end": v(178.41, 39.87) * mm});
            skLineSegment(sketch, "E2433", {"start": v(178.41, 39.87) * mm, "end": v(178.06, 39.65) * mm});
            skLineSegment(sketch, "E2434", {"start": v(178.06, 39.65) * mm, "end": v(177.71, 39.41) * mm});
            skLineSegment(sketch, "E2435", {"start": v(177.71, 39.41) * mm, "end": v(177.37, 39.16) * mm});
            skLineSegment(sketch, "E2436", {"start": v(177.37, 39.16) * mm, "end": v(177.1, 38.9) * mm});
            skLineSegment(sketch, "E2437", {"start": v(177.1, 38.9) * mm, "end": v(176.85, 38.63) * mm});
            skLineSegment(sketch, "E2438", {"start": v(176.85, 38.63) * mm, "end": v(176.6, 38.36) * mm});
            skLineSegment(sketch, "E2439", {"start": v(176.6, 38.36) * mm, "end": v(176.37, 38.08) * mm});
            skLineSegment(sketch, "E2440", {"start": v(176.37, 38.08) * mm, "end": v(176.14, 37.8) * mm});
            skLineSegment(sketch, "E2441", {"start": v(176.14, 37.8) * mm, "end": v(175.91, 37.51) * mm});
            skLineSegment(sketch, "E2442", {"start": v(175.91, 37.51) * mm, "end": v(175.7, 37.22) * mm});
            skLineSegment(sketch, "E2443", {"start": v(175.7, 37.22) * mm, "end": v(175.5, 36.92) * mm});
            skLineSegment(sketch, "E2444", {"start": v(175.5, 36.92) * mm, "end": v(175.3, 36.61) * mm});
            skLineSegment(sketch, "E2445", {"start": v(175.3, 36.61) * mm, "end": v(175.1, 36.3) * mm});
            skLineSegment(sketch, "E2446", {"start": v(175.1, 36.3) * mm, "end": v(174.92, 36) * mm});
            skLineSegment(sketch, "E2447", {"start": v(174.92, 36) * mm, "end": v(174.75, 35.67) * mm});
            skLineSegment(sketch, "E2448", {"start": v(174.75, 35.67) * mm, "end": v(174.59, 35.35) * mm});
            skLineSegment(sketch, "E2449", {"start": v(174.59, 35.35) * mm, "end": v(174.43, 35.02) * mm});
            skLineSegment(sketch, "E2450", {"start": v(174.43, 35.02) * mm, "end": v(174.28, 34.7) * mm});
            skLineSegment(sketch, "E2451", {"start": v(174.28, 34.7) * mm, "end": v(174.15, 34.36) * mm});
            skLineSegment(sketch, "E2452", {"start": v(174.15, 34.36) * mm, "end": v(174.02, 34.02) * mm});
            skLineSegment(sketch, "E2453", {"start": v(174.02, 34.02) * mm, "end": v(173.9, 33.68) * mm});
            skLineSegment(sketch, "E2454", {"start": v(173.9, 33.68) * mm, "end": v(173.79, 33.33) * mm});
            skLineSegment(sketch, "E2455", {"start": v(173.79, 33.33) * mm, "end": v(173.69, 32.99) * mm});
            skLineSegment(sketch, "E2456", {"start": v(173.69, 32.99) * mm, "end": v(173.6, 32.63) * mm});
            skLineSegment(sketch, "E2457", {"start": v(173.6, 32.63) * mm, "end": v(173.51, 32.28) * mm});
            skLineSegment(sketch, "E2458", {"start": v(173.51, 32.28) * mm, "end": v(173.44, 31.93) * mm});
            skLineSegment(sketch, "E2459", {"start": v(173.44, 31.93) * mm, "end": v(173.37, 31.57) * mm});
            skLineSegment(sketch, "E2460", {"start": v(173.37, 31.57) * mm, "end": v(173.32, 31.2) * mm});
            skLineSegment(sketch, "E2461", {"start": v(173.32, 31.2) * mm, "end": v(173.28, 30.85) * mm});
            skLineSegment(sketch, "E2462", {"start": v(173.28, 30.85) * mm, "end": v(173.24, 30.48) * mm});
            skLineSegment(sketch, "E2463", {"start": v(173.24, 30.48) * mm, "end": v(173.22, 30.12) * mm});
            skLineSegment(sketch, "E2464", {"start": v(173.22, 30.12) * mm, "end": v(173.2, 29.75) * mm});
            skLineSegment(sketch, "E2465", {"start": v(173.2, 29.75) * mm, "end": v(173.2, 29.39) * mm});
            skLineSegment(sketch, "E2466", {"start": v(173.2, 29.39) * mm, "end": v(173.2, 29.02) * mm});
            skLineSegment(sketch, "E2467", {"start": v(173.2, 29.02) * mm, "end": v(173.22, 28.65) * mm});
            skLineSegment(sketch, "E2468", {"start": v(173.22, 28.65) * mm, "end": v(173.27, 28.16) * mm});
            skLineSegment(sketch, "E2469", {"start": v(173.27, 28.16) * mm, "end": v(173.3, 27.67) * mm});
            skLineSegment(sketch, "E2470", {"start": v(173.3, 27.67) * mm, "end": v(173.3, 27.19) * mm});
            skLineSegment(sketch, "E2471", {"start": v(173.3, 27.19) * mm, "end": v(173.3, 26.7) * mm});
            skLineSegment(sketch, "E2472", {"start": v(173.3, 26.7) * mm, "end": v(173.25, 26.23) * mm});
            skLineSegment(sketch, "E2473", {"start": v(173.25, 26.23) * mm, "end": v(173.2, 25.76) * mm});
            skLineSegment(sketch, "E2474", {"start": v(173.2, 25.76) * mm, "end": v(173.1, 25.3) * mm});
            skLineSegment(sketch, "E2475", {"start": v(173.1, 25.3) * mm, "end": v(173, 24.83) * mm});
            skLineSegment(sketch, "E2476", {"start": v(173, 24.83) * mm, "end": v(172.87, 24.38) * mm});
            skLineSegment(sketch, "E2477", {"start": v(172.87, 24.38) * mm, "end": v(172.73, 23.94) * mm});
            skLineSegment(sketch, "E2478", {"start": v(172.73, 23.94) * mm, "end": v(172.56, 23.5) * mm});
            skLineSegment(sketch, "E2479", {"start": v(172.56, 23.5) * mm, "end": v(172.37, 23.07) * mm});
            skLineSegment(sketch, "E2480", {"start": v(172.37, 23.07) * mm, "end": v(172.16, 22.66) * mm});
            skLineSegment(sketch, "E2481", {"start": v(172.16, 22.66) * mm, "end": v(171.94, 22.25) * mm});
            skLineSegment(sketch, "E2482", {"start": v(171.94, 22.25) * mm, "end": v(171.7, 21.85) * mm});
            skLineSegment(sketch, "E2483", {"start": v(171.7, 21.85) * mm, "end": v(171.43, 21.47) * mm});
            skLineSegment(sketch, "E2484", {"start": v(171.43, 21.47) * mm, "end": v(171.15, 21.1) * mm});
            skLineSegment(sketch, "E2485", {"start": v(171.15, 21.1) * mm, "end": v(170.86, 20.74) * mm});
            skLineSegment(sketch, "E2486", {"start": v(170.86, 20.74) * mm, "end": v(170.55, 20.4) * mm});
            skLineSegment(sketch, "E2487", {"start": v(170.55, 20.4) * mm, "end": v(170.22, 20.07) * mm});
            skLineSegment(sketch, "E2488", {"start": v(170.22, 20.07) * mm, "end": v(169.87, 19.75) * mm});
            skLineSegment(sketch, "E2489", {"start": v(169.87, 19.75) * mm, "end": v(169.51, 19.45) * mm});
            skLineSegment(sketch, "E2490", {"start": v(169.51, 19.45) * mm, "end": v(169.14, 19.17) * mm});
            skLineSegment(sketch, "E2491", {"start": v(169.14, 19.17) * mm, "end": v(168.75, 18.9) * mm});
            skLineSegment(sketch, "E2492", {"start": v(168.75, 18.9) * mm, "end": v(168.35, 18.65) * mm});
            skLineSegment(sketch, "E2493", {"start": v(168.35, 18.65) * mm, "end": v(167.94, 18.42) * mm});
            skLineSegment(sketch, "E2494", {"start": v(167.94, 18.42) * mm, "end": v(167.51, 18.21) * mm});
            skLineSegment(sketch, "E2495", {"start": v(167.51, 18.21) * mm, "end": v(167.07, 18.02) * mm});
            skLineSegment(sketch, "E2496", {"start": v(167.07, 18.02) * mm, "end": v(166.62, 17.85) * mm});
            skLineSegment(sketch, "E2497", {"start": v(166.62, 17.85) * mm, "end": v(166.16, 17.7) * mm});
            skLineSegment(sketch, "E2498", {"start": v(166.16, 17.7) * mm, "end": v(165.69, 17.57) * mm});
            skLineSegment(sketch, "E2499", {"start": v(165.69, 17.57) * mm, "end": v(165.2, 17.47) * mm});
            skLineSegment(sketch, "E2500", {"start": v(165.2, 17.47) * mm, "end": v(164.8, 17.47) * mm});
            skLineSegment(sketch, "E2501", {"start": v(164.8, 17.47) * mm, "end": v(164.4, 17.5) * mm});
            skLineSegment(sketch, "E2502", {"start": v(164.4, 17.5) * mm, "end": v(164.01, 17.54) * mm});
            skLineSegment(sketch, "E2503", {"start": v(164.01, 17.54) * mm, "end": v(163.63, 17.6) * mm});
            skLineSegment(sketch, "E2504", {"start": v(163.63, 17.6) * mm, "end": v(163.24, 17.7) * mm});
            skLineSegment(sketch, "E2505", {"start": v(163.24, 17.7) * mm, "end": v(162.86, 17.8) * mm});
            skLineSegment(sketch, "E2506", {"start": v(162.86, 17.8) * mm, "end": v(162.5, 17.94) * mm});
            skLineSegment(sketch, "E2507", {"start": v(162.5, 17.94) * mm, "end": v(162.13, 18.09) * mm});
            skLineSegment(sketch, "E2508", {"start": v(162.13, 18.09) * mm, "end": v(161.78, 18.26) * mm});
            skLineSegment(sketch, "E2509", {"start": v(161.78, 18.26) * mm, "end": v(161.44, 18.45) * mm});
            skLineSegment(sketch, "E2510", {"start": v(161.44, 18.45) * mm, "end": v(161.1, 18.66) * mm});
            skLineSegment(sketch, "E2511", {"start": v(161.1, 18.66) * mm, "end": v(160.78, 18.88) * mm});
            skLineSegment(sketch, "E2512", {"start": v(160.78, 18.88) * mm, "end": v(160.47, 19.13) * mm});
            skLineSegment(sketch, "E2513", {"start": v(160.47, 19.13) * mm, "end": v(160.18, 19.4) * mm});
            skLineSegment(sketch, "E2514", {"start": v(160.18, 19.4) * mm, "end": v(159.9, 19.67) * mm});
            skLineSegment(sketch, "E2515", {"start": v(159.9, 19.67) * mm, "end": v(159.63, 19.97) * mm});
            skLineSegment(sketch, "E2516", {"start": v(159.63, 19.97) * mm, "end": v(159.41, 20.21) * mm});
            skLineSegment(sketch, "E2517", {"start": v(159.41, 20.21) * mm, "end": v(159.2, 20.46) * mm});
            skLineSegment(sketch, "E2518", {"start": v(159.2, 20.46) * mm, "end": v(159, 20.72) * mm});
            skLineSegment(sketch, "E2519", {"start": v(159, 20.72) * mm, "end": v(158.8, 20.98) * mm});
            skLineSegment(sketch, "E2520", {"start": v(158.8, 20.98) * mm, "end": v(158.6, 21.24) * mm});
            skLineSegment(sketch, "E2521", {"start": v(158.6, 21.24) * mm, "end": v(158.43, 21.5) * mm});
            skLineSegment(sketch, "E2522", {"start": v(158.43, 21.5) * mm, "end": v(158.25, 21.78) * mm});
            skLineSegment(sketch, "E2523", {"start": v(158.25, 21.78) * mm, "end": v(158.08, 22.05) * mm});
            skLineSegment(sketch, "E2524", {"start": v(158.08, 22.05) * mm, "end": v(157.92, 22.33) * mm});
            skLineSegment(sketch, "E2525", {"start": v(157.92, 22.33) * mm, "end": v(157.76, 22.62) * mm});
            skLineSegment(sketch, "E2526", {"start": v(157.76, 22.62) * mm, "end": v(157.62, 22.9) * mm});
            skLineSegment(sketch, "E2527", {"start": v(157.62, 22.9) * mm, "end": v(157.48, 23.2) * mm});
            skLineSegment(sketch, "E2528", {"start": v(157.48, 23.2) * mm, "end": v(157.34, 23.49) * mm});
            skLineSegment(sketch, "E2529", {"start": v(157.34, 23.49) * mm, "end": v(157.22, 23.79) * mm});
            skLineSegment(sketch, "E2530", {"start": v(157.22, 23.79) * mm, "end": v(157.1, 24.08) * mm});
            skLineSegment(sketch, "E2531", {"start": v(157.1, 24.08) * mm, "end": v(157, 24.39) * mm});
            skLineSegment(sketch, "E2532", {"start": v(157, 24.39) * mm, "end": v(156.89, 24.7) * mm});
            skLineSegment(sketch, "E2533", {"start": v(156.89, 24.7) * mm, "end": v(156.8, 25) * mm});
            skLineSegment(sketch, "E2534", {"start": v(156.8, 25) * mm, "end": v(156.7, 25.31) * mm});
            skLineSegment(sketch, "E2535", {"start": v(156.7, 25.31) * mm, "end": v(156.63, 25.62) * mm});
            skLineSegment(sketch, "E2536", {"start": v(156.63, 25.62) * mm, "end": v(156.55, 25.94) * mm});
            skLineSegment(sketch, "E2537", {"start": v(156.55, 25.94) * mm, "end": v(156.49, 26.25) * mm});
            skLineSegment(sketch, "E2538", {"start": v(156.49, 26.25) * mm, "end": v(156.43, 26.57) * mm});
            skLineSegment(sketch, "E2539", {"start": v(156.43, 26.57) * mm, "end": v(156.38, 26.89) * mm});
            skLineSegment(sketch, "E2540", {"start": v(156.38, 26.89) * mm, "end": v(156.34, 27.21) * mm});
            skLineSegment(sketch, "E2541", {"start": v(156.34, 27.21) * mm, "end": v(156.31, 27.53) * mm});
            skLineSegment(sketch, "E2542", {"start": v(156.31, 27.53) * mm, "end": v(156.29, 27.86) * mm});
            skLineSegment(sketch, "E2543", {"start": v(156.29, 27.86) * mm, "end": v(156.27, 28.18) * mm});
            skLineSegment(sketch, "E2544", {"start": v(156.27, 28.18) * mm, "end": v(156.26, 28.5) * mm});
            skLineSegment(sketch, "E2545", {"start": v(156.26, 28.5) * mm, "end": v(156.26, 28.83) * mm});
            skLineSegment(sketch, "E2546", {"start": v(156.26, 28.83) * mm, "end": v(156.27, 29.16) * mm});
            skLineSegment(sketch, "E2547", {"start": v(156.27, 29.16) * mm, "end": v(156.29, 29.48) * mm});
            skLineSegment(sketch, "E2548", {"start": v(156.29, 29.48) * mm, "end": v(156.29, 30.06) * mm});
            skLineSegment(sketch, "E2549", {"start": v(156.29, 30.06) * mm, "end": v(156.32, 30.63) * mm});
            skLineSegment(sketch, "E2550", {"start": v(156.32, 30.63) * mm, "end": v(156.37, 31.2) * mm});
            skLineSegment(sketch, "E2551", {"start": v(156.37, 31.2) * mm, "end": v(156.45, 31.76) * mm});
            skLineSegment(sketch, "E2552", {"start": v(156.45, 31.76) * mm, "end": v(156.56, 32.32) * mm});
            skLineSegment(sketch, "E2553", {"start": v(156.56, 32.32) * mm, "end": v(156.7, 32.87) * mm});
            skLineSegment(sketch, "E2554", {"start": v(156.7, 32.87) * mm, "end": v(156.86, 33.41) * mm});
            skLineSegment(sketch, "E2555", {"start": v(156.86, 33.41) * mm, "end": v(157.05, 33.95) * mm});
            skLineSegment(sketch, "E2556", {"start": v(157.05, 33.95) * mm, "end": v(157.26, 34.48) * mm});
            skLineSegment(sketch, "E2557", {"start": v(157.26, 34.48) * mm, "end": v(157.5, 35) * mm});
            skLineSegment(sketch, "E2558", {"start": v(157.5, 35) * mm, "end": v(157.76, 35.5) * mm});
            skLineSegment(sketch, "E2559", {"start": v(157.76, 35.5) * mm, "end": v(158.05, 35.99) * mm});
            skLineSegment(sketch, "E2560", {"start": v(158.05, 35.99) * mm, "end": v(158.36, 36.46) * mm});
            skLineSegment(sketch, "E2561", {"start": v(158.36, 36.46) * mm, "end": v(158.7, 36.93) * mm});
            skLineSegment(sketch, "E2562", {"start": v(158.7, 36.93) * mm, "end": v(159.05, 37.37) * mm});
            skLineSegment(sketch, "E2563", {"start": v(159.05, 37.37) * mm, "end": v(159.43, 37.8) * mm});
            skLineSegment(sketch, "E2564", {"start": v(159.43, 37.8) * mm, "end": v(159.72, 38.07) * mm});
            skLineSegment(sketch, "E2565", {"start": v(159.72, 38.07) * mm, "end": v(160.01, 38.32) * mm});
            skLineSegment(sketch, "E2566", {"start": v(160.01, 38.32) * mm, "end": v(160.32, 38.56) * mm});
            skLineSegment(sketch, "E2567", {"start": v(160.32, 38.56) * mm, "end": v(160.63, 38.78) * mm});
            skLineSegment(sketch, "E2568", {"start": v(160.63, 38.78) * mm, "end": v(160.95, 39) * mm});
            skLineSegment(sketch, "E2569", {"start": v(160.95, 39) * mm, "end": v(161.27, 39.2) * mm});
            skLineSegment(sketch, "E2570", {"start": v(161.27, 39.2) * mm, "end": v(161.6, 39.4) * mm});
            skLineSegment(sketch, "E2571", {"start": v(161.6, 39.4) * mm, "end": v(161.94, 39.59) * mm});
            skLineSegment(sketch, "E2572", {"start": v(161.94, 39.59) * mm, "end": v(162.29, 39.76) * mm});
            skLineSegment(sketch, "E2573", {"start": v(162.29, 39.76) * mm, "end": v(162.64, 39.92) * mm});
            skLineSegment(sketch, "E2574", {"start": v(162.64, 39.92) * mm, "end": v(163, 40.07) * mm});
            skLineSegment(sketch, "E2575", {"start": v(163, 40.07) * mm, "end": v(163.35, 40.2) * mm});
            skLineSegment(sketch, "E2576", {"start": v(163.35, 40.2) * mm, "end": v(163.72, 40.32) * mm});
            skLineSegment(sketch, "E2577", {"start": v(163.72, 40.32) * mm, "end": v(164.1, 40.43) * mm});
            skLineSegment(sketch, "E2578", {"start": v(164.1, 40.43) * mm, "end": v(164.47, 40.53) * mm});
            skLineSegment(sketch, "E2579", {"start": v(164.47, 40.53) * mm, "end": v(164.84, 40.62) * mm});
            skLineSegment(sketch, "E2580", {"start": v(191.95, 48.9) * mm, "end": v(157, 48.9) * mm});
            skLineSegment(sketch, "E2581", {"start": v(191.96, 56.6) * mm, "end": v(156.98, 56.6) * mm});
            skLineSegment(sketch, "E2582", {"start": v(156.98, 56.6) * mm, "end": v(156.98, 69.43) * mm});
            skLineSegment(sketch, "E2583", {"start": v(156.98, 69.43) * mm, "end": v(157, 69.73) * mm});
            skLineSegment(sketch, "E2584", {"start": v(157, 69.73) * mm, "end": v(157.02, 70.03) * mm});
            skLineSegment(sketch, "E2585", {"start": v(157.02, 70.03) * mm, "end": v(157.05, 70.33) * mm});
            skLineSegment(sketch, "E2586", {"start": v(157.05, 70.33) * mm, "end": v(157.09, 70.63) * mm});
            skLineSegment(sketch, "E2587", {"start": v(157.09, 70.63) * mm, "end": v(157.13, 70.93) * mm});
            skLineSegment(sketch, "E2588", {"start": v(157.13, 70.93) * mm, "end": v(157.18, 71.23) * mm});
            skLineSegment(sketch, "E2589", {"start": v(157.18, 71.23) * mm, "end": v(157.24, 71.53) * mm});
            skLineSegment(sketch, "E2590", {"start": v(157.24, 71.53) * mm, "end": v(157.31, 71.82) * mm});
            skLineSegment(sketch, "E2591", {"start": v(157.31, 71.82) * mm, "end": v(157.38, 72.1) * mm});
            skLineSegment(sketch, "E2592", {"start": v(157.38, 72.1) * mm, "end": v(157.47, 72.4) * mm});
            skLineSegment(sketch, "E2593", {"start": v(157.47, 72.4) * mm, "end": v(157.56, 72.69) * mm});
            skLineSegment(sketch, "E2594", {"start": v(157.56, 72.69) * mm, "end": v(157.65, 72.97) * mm});
            skLineSegment(sketch, "E2595", {"start": v(157.65, 72.97) * mm, "end": v(157.86, 73.53) * mm});
            skLineSegment(sketch, "E2596", {"start": v(157.86, 73.53) * mm, "end": v(158.1, 74.08) * mm});
            skLineSegment(sketch, "E2597", {"start": v(158.1, 74.08) * mm, "end": v(158.37, 74.62) * mm});
            skLineSegment(sketch, "E2598", {"start": v(158.37, 74.62) * mm, "end": v(158.67, 75.14) * mm});
            skLineSegment(sketch, "E2599", {"start": v(158.67, 75.14) * mm, "end": v(158.82, 75.4) * mm});
            skLineSegment(sketch, "E2600", {"start": v(158.82, 75.4) * mm, "end": v(158.99, 75.65) * mm});
            skLineSegment(sketch, "E2601", {"start": v(158.99, 75.65) * mm, "end": v(159.16, 75.9) * mm});
            skLineSegment(sketch, "E2602", {"start": v(159.16, 75.9) * mm, "end": v(159.33, 76.14) * mm});
            skLineSegment(sketch, "E2603", {"start": v(159.33, 76.14) * mm, "end": v(159.52, 76.38) * mm});
            skLineSegment(sketch, "E2604", {"start": v(159.52, 76.38) * mm, "end": v(159.7, 76.61) * mm});
            skLineSegment(sketch, "E2605", {"start": v(159.7, 76.61) * mm, "end": v(159.9, 76.84) * mm});
            skLineSegment(sketch, "E2606", {"start": v(159.9, 76.84) * mm, "end": v(160.1, 77.07) * mm});
            skLineSegment(sketch, "E2607", {"start": v(160.1, 77.07) * mm, "end": v(160.3, 77.29) * mm});
            skLineSegment(sketch, "E2608", {"start": v(160.3, 77.29) * mm, "end": v(160.52, 77.5) * mm});
            skLineSegment(sketch, "E2609", {"start": v(160.52, 77.5) * mm, "end": v(160.74, 77.72) * mm});
            skLineSegment(sketch, "E2610", {"start": v(160.74, 77.72) * mm, "end": v(160.96, 77.92) * mm});
            skLineSegment(sketch, "E2611", {"start": v(160.96, 77.92) * mm, "end": v(161.32, 78.27) * mm});
            skLineSegment(sketch, "E2612", {"start": v(161.32, 78.27) * mm, "end": v(161.7, 78.61) * mm});
            skLineSegment(sketch, "E2613", {"start": v(161.7, 78.61) * mm, "end": v(162.07, 78.94) * mm});
            skLineSegment(sketch, "E2614", {"start": v(162.07, 78.94) * mm, "end": v(162.45, 79.26) * mm});
            skLineSegment(sketch, "E2615", {"start": v(162.45, 79.26) * mm, "end": v(162.84, 79.57) * mm});
            skLineSegment(sketch, "E2616", {"start": v(162.84, 79.57) * mm, "end": v(163.24, 79.87) * mm});
            skLineSegment(sketch, "E2617", {"start": v(163.24, 79.87) * mm, "end": v(163.65, 80.16) * mm});
            skLineSegment(sketch, "E2618", {"start": v(163.65, 80.16) * mm, "end": v(164.06, 80.44) * mm});
            skLineSegment(sketch, "E2619", {"start": v(164.06, 80.44) * mm, "end": v(164.48, 80.7) * mm});
            skLineSegment(sketch, "E2620", {"start": v(164.48, 80.7) * mm, "end": v(164.9, 80.97) * mm});
            skLineSegment(sketch, "E2621", {"start": v(164.9, 80.97) * mm, "end": v(165.34, 81.21) * mm});
            skLineSegment(sketch, "E2622", {"start": v(165.34, 81.21) * mm, "end": v(165.77, 81.45) * mm});
            skLineSegment(sketch, "E2623", {"start": v(165.77, 81.45) * mm, "end": v(166.21, 81.67) * mm});
            skLineSegment(sketch, "E2624", {"start": v(166.21, 81.67) * mm, "end": v(166.66, 81.89) * mm});
            skLineSegment(sketch, "E2625", {"start": v(166.66, 81.89) * mm, "end": v(167.11, 82.09) * mm});
            skLineSegment(sketch, "E2626", {"start": v(167.11, 82.09) * mm, "end": v(167.57, 82.28) * mm});
            skLineSegment(sketch, "E2627", {"start": v(167.57, 82.28) * mm, "end": v(168.03, 82.46) * mm});
            skLineSegment(sketch, "E2628", {"start": v(168.03, 82.46) * mm, "end": v(168.5, 82.62) * mm});
            skLineSegment(sketch, "E2629", {"start": v(168.5, 82.62) * mm, "end": v(168.97, 82.78) * mm});
            skLineSegment(sketch, "E2630", {"start": v(168.97, 82.78) * mm, "end": v(169.45, 82.92) * mm});
            skLineSegment(sketch, "E2631", {"start": v(169.45, 82.92) * mm, "end": v(169.92, 83.06) * mm});
            skLineSegment(sketch, "E2632", {"start": v(169.92, 83.06) * mm, "end": v(170.4, 83.18) * mm});
            skLineSegment(sketch, "E2633", {"start": v(170.4, 83.18) * mm, "end": v(170.9, 83.29) * mm});
            skLineSegment(sketch, "E2634", {"start": v(170.9, 83.29) * mm, "end": v(171.38, 83.38) * mm});
            skLineSegment(sketch, "E2635", {"start": v(171.38, 83.38) * mm, "end": v(171.87, 83.47) * mm});
            skLineSegment(sketch, "E2636", {"start": v(171.87, 83.47) * mm, "end": v(172.36, 83.54) * mm});
            skLineSegment(sketch, "E2637", {"start": v(172.36, 83.54) * mm, "end": v(172.86, 83.6) * mm});
            skLineSegment(sketch, "E2638", {"start": v(172.86, 83.6) * mm, "end": v(173.35, 83.65) * mm});
            skLineSegment(sketch, "E2639", {"start": v(173.35, 83.65) * mm, "end": v(173.85, 83.68) * mm});
            skLineSegment(sketch, "E2640", {"start": v(173.85, 83.68) * mm, "end": v(174.35, 83.7) * mm});
            skLineSegment(sketch, "E2641", {"start": v(174.35, 83.7) * mm, "end": v(174.86, 83.71) * mm});
            skLineSegment(sketch, "E2642", {"start": v(174.86, 83.71) * mm, "end": v(175.36, 83.71) * mm});
            skLineSegment(sketch, "E2643", {"start": v(175.36, 83.71) * mm, "end": v(175.78, 83.72) * mm});
            skLineSegment(sketch, "E2644", {"start": v(175.78, 83.72) * mm, "end": v(176.2, 83.72) * mm});
            skLineSegment(sketch, "E2645", {"start": v(176.2, 83.72) * mm, "end": v(176.62, 83.7) * mm});
            skLineSegment(sketch, "E2646", {"start": v(176.62, 83.7) * mm, "end": v(177.04, 83.69) * mm});
            skLineSegment(sketch, "E2647", {"start": v(177.04, 83.69) * mm, "end": v(177.46, 83.66) * mm});
            skLineSegment(sketch, "E2648", {"start": v(177.46, 83.66) * mm, "end": v(177.88, 83.61) * mm});
            skLineSegment(sketch, "E2649", {"start": v(177.88, 83.61) * mm, "end": v(178.29, 83.56) * mm});
            skLineSegment(sketch, "E2650", {"start": v(178.29, 83.56) * mm, "end": v(178.7, 83.5) * mm});
            skLineSegment(sketch, "E2651", {"start": v(178.7, 83.5) * mm, "end": v(179.11, 83.43) * mm});
            skLineSegment(sketch, "E2652", {"start": v(179.11, 83.43) * mm, "end": v(179.52, 83.35) * mm});
            skLineSegment(sketch, "E2653", {"start": v(179.52, 83.35) * mm, "end": v(179.93, 83.25) * mm});
            skLineSegment(sketch, "E2654", {"start": v(179.93, 83.25) * mm, "end": v(180.33, 83.15) * mm});
            skLineSegment(sketch, "E2655", {"start": v(180.33, 83.15) * mm, "end": v(180.73, 83.04) * mm});
            skLineSegment(sketch, "E2656", {"start": v(180.73, 83.04) * mm, "end": v(181.13, 82.92) * mm});
            skLineSegment(sketch, "E2657", {"start": v(181.13, 82.92) * mm, "end": v(181.52, 82.79) * mm});
            skLineSegment(sketch, "E2658", {"start": v(181.52, 82.79) * mm, "end": v(181.92, 82.65) * mm});
            skLineSegment(sketch, "E2659", {"start": v(181.92, 82.65) * mm, "end": v(182.3, 82.5) * mm});
            skLineSegment(sketch, "E2660", {"start": v(182.3, 82.5) * mm, "end": v(182.69, 82.34) * mm});
            skLineSegment(sketch, "E2661", {"start": v(182.69, 82.34) * mm, "end": v(183.07, 82.17) * mm});
            skLineSegment(sketch, "E2662", {"start": v(183.07, 82.17) * mm, "end": v(183.44, 81.99) * mm});
            skLineSegment(sketch, "E2663", {"start": v(183.44, 81.99) * mm, "end": v(183.81, 81.8) * mm});
            skLineSegment(sketch, "E2664", {"start": v(183.81, 81.8) * mm, "end": v(184.18, 81.6) * mm});
            skLineSegment(sketch, "E2665", {"start": v(184.18, 81.6) * mm, "end": v(184.54, 81.4) * mm});
            skLineSegment(sketch, "E2666", {"start": v(184.54, 81.4) * mm, "end": v(184.9, 81.18) * mm});
            skLineSegment(sketch, "E2667", {"start": v(184.9, 81.18) * mm, "end": v(185.25, 80.96) * mm});
            skLineSegment(sketch, "E2668", {"start": v(185.25, 80.96) * mm, "end": v(185.6, 80.73) * mm});
            skLineSegment(sketch, "E2669", {"start": v(185.6, 80.73) * mm, "end": v(185.94, 80.49) * mm});
            skLineSegment(sketch, "E2670", {"start": v(185.94, 80.49) * mm, "end": v(186.28, 80.24) * mm});
            skLineSegment(sketch, "E2671", {"start": v(186.28, 80.24) * mm, "end": v(186.6, 79.98) * mm});
            skLineSegment(sketch, "E2672", {"start": v(186.6, 79.98) * mm, "end": v(186.93, 79.71) * mm});
            skLineSegment(sketch, "E2673", {"start": v(186.93, 79.71) * mm, "end": v(187.25, 79.44) * mm});
            skLineSegment(sketch, "E2674", {"start": v(187.25, 79.44) * mm, "end": v(187.56, 79.15) * mm});
            skLineSegment(sketch, "E2675", {"start": v(187.56, 79.15) * mm, "end": v(187.81, 78.91) * mm});
            skLineSegment(sketch, "E2676", {"start": v(187.81, 78.91) * mm, "end": v(188.05, 78.67) * mm});
            skLineSegment(sketch, "E2677", {"start": v(188.05, 78.67) * mm, "end": v(188.29, 78.42) * mm});
            skLineSegment(sketch, "E2678", {"start": v(188.29, 78.42) * mm, "end": v(188.52, 78.16) * mm});
            skLineSegment(sketch, "E2679", {"start": v(188.52, 78.16) * mm, "end": v(188.74, 77.9) * mm});
            skLineSegment(sketch, "E2680", {"start": v(188.74, 77.9) * mm, "end": v(188.96, 77.63) * mm});
            skLineSegment(sketch, "E2681", {"start": v(188.96, 77.63) * mm, "end": v(189.17, 77.36) * mm});
            skLineSegment(sketch, "E2682", {"start": v(189.17, 77.36) * mm, "end": v(189.37, 77.08) * mm});
            skLineSegment(sketch, "E2683", {"start": v(189.37, 77.08) * mm, "end": v(189.56, 76.8) * mm});
            skLineSegment(sketch, "E2684", {"start": v(189.56, 76.8) * mm, "end": v(189.75, 76.52) * mm});
            skLineSegment(sketch, "E2685", {"start": v(189.75, 76.52) * mm, "end": v(189.93, 76.23) * mm});
            skLineSegment(sketch, "E2686", {"start": v(189.93, 76.23) * mm, "end": v(190.1, 75.94) * mm});
            skLineSegment(sketch, "E2687", {"start": v(190.1, 75.94) * mm, "end": v(190.27, 75.64) * mm});
            skLineSegment(sketch, "E2688", {"start": v(190.27, 75.64) * mm, "end": v(190.43, 75.34) * mm});
            skLineSegment(sketch, "E2689", {"start": v(190.43, 75.34) * mm, "end": v(190.58, 75.03) * mm});
            skLineSegment(sketch, "E2690", {"start": v(190.58, 75.03) * mm, "end": v(190.72, 74.72) * mm});
            skLineSegment(sketch, "E2691", {"start": v(190.72, 74.72) * mm, "end": v(190.86, 74.41) * mm});
            skLineSegment(sketch, "E2692", {"start": v(190.86, 74.41) * mm, "end": v(191, 74.1) * mm});
            skLineSegment(sketch, "E2693", {"start": v(191, 74.1) * mm, "end": v(191.11, 73.78) * mm});
            skLineSegment(sketch, "E2694", {"start": v(191.11, 73.78) * mm, "end": v(191.22, 73.46) * mm});
            skLineSegment(sketch, "E2695", {"start": v(191.22, 73.46) * mm, "end": v(191.33, 73.13) * mm});
            skLineSegment(sketch, "E2696", {"start": v(191.33, 73.13) * mm, "end": v(191.43, 72.8) * mm});
            skLineSegment(sketch, "E2697", {"start": v(191.43, 72.8) * mm, "end": v(191.52, 72.48) * mm});
            skLineSegment(sketch, "E2698", {"start": v(191.52, 72.48) * mm, "end": v(191.6, 72.15) * mm});
            skLineSegment(sketch, "E2699", {"start": v(191.6, 72.15) * mm, "end": v(191.67, 71.81) * mm});
            skLineSegment(sketch, "E2700", {"start": v(191.67, 71.81) * mm, "end": v(191.74, 71.48) * mm});
            skLineSegment(sketch, "E2701", {"start": v(191.74, 71.48) * mm, "end": v(191.8, 71.14) * mm});
            skLineSegment(sketch, "E2702", {"start": v(191.8, 71.14) * mm, "end": v(191.85, 70.8) * mm});
            skLineSegment(sketch, "E2703", {"start": v(191.85, 70.8) * mm, "end": v(191.89, 70.46) * mm});
            skLineSegment(sketch, "E2704", {"start": v(191.89, 70.46) * mm, "end": v(191.92, 70.11) * mm});
            skLineSegment(sketch, "E2705", {"start": v(191.92, 70.11) * mm, "end": v(191.95, 69.77) * mm});
            skLineSegment(sketch, "E2706", {"start": v(191.95, 69.77) * mm, "end": v(191.96, 69.43) * mm});
            skLineSegment(sketch, "E2707", {"start": v(191.96, 69.43) * mm, "end": v(191.96, 56.6) * mm});
            skLineSegment(sketch, "E2708", {"start": v(191.95, 114.63) * mm, "end": v(191.95, 91.6) * mm});
            skLineSegment(sketch, "E2709", {"start": v(191.95, 91.6) * mm, "end": v(157, 91.6) * mm});
            skLineSegment(sketch, "E2710", {"start": v(157, 91.6) * mm, "end": v(157, 114.63) * mm});
            skLineSegment(sketch, "E2711", {"start": v(173.84, 91.6) * mm, "end": v(173.84, 111.75) * mm});
            skLineSegment(sketch, "E2712", {"start": v(178.9, 122.33) * mm, "end": v(178.9, 146.46) * mm});
            skLineSegment(sketch, "E2713", {"start": v(191.96, 154.16) * mm, "end": v(165.79, 154.16) * mm});
            skLineSegment(sketch, "E2714", {"start": v(157.5, 154.16) * mm, "end": v(157.07, 154.16) * mm});
            skLineSegment(sketch, "E2715", {"start": v(191.96, 161.87) * mm, "end": v(165.73, 161.87) * mm});
            skLineSegment(sketch, "E2716", {"start": v(175.98, 161.87) * mm, "end": v(175.4, 161.88) * mm});
            skLineSegment(sketch, "E2717", {"start": v(175.4, 161.88) * mm, "end": v(174.84, 161.93) * mm});
            skLineSegment(sketch, "E2718", {"start": v(174.84, 161.93) * mm, "end": v(174.27, 162) * mm});
            skLineSegment(sketch, "E2719", {"start": v(174.27, 162) * mm, "end": v(173.72, 162.1) * mm});
            skLineSegment(sketch, "E2720", {"start": v(173.72, 162.1) * mm, "end": v(173.16, 162.23) * mm});
            skLineSegment(sketch, "E2721", {"start": v(173.16, 162.23) * mm, "end": v(172.62, 162.39) * mm});
            skLineSegment(sketch, "E2722", {"start": v(172.62, 162.39) * mm, "end": v(172.08, 162.57) * mm});
            skLineSegment(sketch, "E2723", {"start": v(172.08, 162.57) * mm, "end": v(171.56, 162.78) * mm});
            skLineSegment(sketch, "E2724", {"start": v(171.56, 162.78) * mm, "end": v(171.04, 163.01) * mm});
            skLineSegment(sketch, "E2725", {"start": v(171.04, 163.01) * mm, "end": v(170.54, 163.27) * mm});
            skLineSegment(sketch, "E2726", {"start": v(170.54, 163.27) * mm, "end": v(170.05, 163.56) * mm});
            skLineSegment(sketch, "E2727", {"start": v(170.05, 163.56) * mm, "end": v(169.58, 163.87) * mm});
            skLineSegment(sketch, "E2728", {"start": v(169.58, 163.87) * mm, "end": v(169.12, 164.2) * mm});
            skLineSegment(sketch, "E2729", {"start": v(169.12, 164.2) * mm, "end": v(168.68, 164.56) * mm});
            skLineSegment(sketch, "E2730", {"start": v(168.68, 164.56) * mm, "end": v(168.25, 164.94) * mm});
            skLineSegment(sketch, "E2731", {"start": v(168.25, 164.94) * mm, "end": v(167.84, 165.34) * mm});
            skLineSegment(sketch, "E2732", {"start": v(167.84, 165.34) * mm, "end": v(167.51, 165.7) * mm});
            skLineSegment(sketch, "E2733", {"start": v(167.51, 165.7) * mm, "end": v(167.2, 166.07) * mm});
            skLineSegment(sketch, "E2734", {"start": v(167.2, 166.07) * mm, "end": v(166.9, 166.45) * mm});
            skLineSegment(sketch, "E2735", {"start": v(166.9, 166.45) * mm, "end": v(166.64, 166.84) * mm});
            skLineSegment(sketch, "E2736", {"start": v(166.64, 166.84) * mm, "end": v(166.39, 167.25) * mm});
            skLineSegment(sketch, "E2737", {"start": v(166.39, 167.25) * mm, "end": v(166.16, 167.67) * mm});
            skLineSegment(sketch, "E2738", {"start": v(166.16, 167.67) * mm, "end": v(165.95, 168.1) * mm});
            skLineSegment(sketch, "E2739", {"start": v(165.95, 168.1) * mm, "end": v(165.76, 168.54) * mm});
            skLineSegment(sketch, "E2740", {"start": v(165.76, 168.54) * mm, "end": v(165.6, 168.99) * mm});
            skLineSegment(sketch, "E2741", {"start": v(165.6, 168.99) * mm, "end": v(165.46, 169.45) * mm});
            skLineSegment(sketch, "E2742", {"start": v(165.46, 169.45) * mm, "end": v(165.34, 169.9) * mm});
            skLineSegment(sketch, "E2743", {"start": v(165.34, 169.9) * mm, "end": v(165.24, 170.38) * mm});
            skLineSegment(sketch, "E2744", {"start": v(165.24, 170.38) * mm, "end": v(165.17, 170.85) * mm});
            skLineSegment(sketch, "E2745", {"start": v(165.17, 170.85) * mm, "end": v(165.12, 171.33) * mm});
            skLineSegment(sketch, "E2746", {"start": v(165.12, 171.33) * mm, "end": v(165.1, 171.81) * mm});
            skLineSegment(sketch, "E2747", {"start": v(165.1, 171.81) * mm, "end": v(165.1, 172.3) * mm});
            skLineSegment(sketch, "E2748", {"start": v(165.1, 172.3) * mm, "end": v(165.07, 172.76) * mm});
            skLineSegment(sketch, "E2749", {"start": v(165.07, 172.76) * mm, "end": v(165.06, 173.22) * mm});
            skLineSegment(sketch, "E2750", {"start": v(165.06, 173.22) * mm, "end": v(165.08, 173.68) * mm});
            skLineSegment(sketch, "E2751", {"start": v(165.08, 173.68) * mm, "end": v(165.12, 174.13) * mm});
            skLineSegment(sketch, "E2752", {"start": v(165.12, 174.13) * mm, "end": v(165.19, 174.59) * mm});
            skLineSegment(sketch, "E2753", {"start": v(165.19, 174.59) * mm, "end": v(165.28, 175.03) * mm});
            skLineSegment(sketch, "E2754", {"start": v(165.28, 175.03) * mm, "end": v(165.39, 175.48) * mm});
            skLineSegment(sketch, "E2755", {"start": v(165.39, 175.48) * mm, "end": v(165.52, 175.91) * mm});
            skLineSegment(sketch, "E2756", {"start": v(165.52, 175.91) * mm, "end": v(165.68, 176.34) * mm});
            skLineSegment(sketch, "E2757", {"start": v(165.68, 176.34) * mm, "end": v(165.86, 176.76) * mm});
            skLineSegment(sketch, "E2758", {"start": v(165.86, 176.76) * mm, "end": v(166.06, 177.17) * mm});
            skLineSegment(sketch, "E2759", {"start": v(166.06, 177.17) * mm, "end": v(166.28, 177.57) * mm});
            skLineSegment(sketch, "E2760", {"start": v(166.28, 177.57) * mm, "end": v(166.52, 177.96) * mm});
            skLineSegment(sketch, "E2761", {"start": v(166.52, 177.96) * mm, "end": v(166.78, 178.34) * mm});
            skLineSegment(sketch, "E2762", {"start": v(166.78, 178.34) * mm, "end": v(167.06, 178.7) * mm});
            skLineSegment(sketch, "E2763", {"start": v(167.06, 178.7) * mm, "end": v(167.37, 179.05) * mm});
            skLineSegment(sketch, "E2764", {"start": v(167.37, 179.05) * mm, "end": v(167.62, 179.26) * mm});
            skLineSegment(sketch, "E2765", {"start": v(167.62, 179.26) * mm, "end": v(167.89, 179.47) * mm});
            skLineSegment(sketch, "E2766", {"start": v(167.89, 179.47) * mm, "end": v(168.16, 179.65) * mm});
            skLineSegment(sketch, "E2767", {"start": v(168.16, 179.65) * mm, "end": v(168.44, 179.83) * mm});
            skLineSegment(sketch, "E2768", {"start": v(168.44, 179.83) * mm, "end": v(168.73, 179.99) * mm});
            skLineSegment(sketch, "E2769", {"start": v(168.73, 179.99) * mm, "end": v(169.02, 180.14) * mm});
            skLineSegment(sketch, "E2770", {"start": v(169.02, 180.14) * mm, "end": v(169.32, 180.27) * mm});
            skLineSegment(sketch, "E2771", {"start": v(169.32, 180.27) * mm, "end": v(169.63, 180.4) * mm});
            skLineSegment(sketch, "E2772", {"start": v(169.63, 180.4) * mm, "end": v(169.94, 180.5) * mm});
            skLineSegment(sketch, "E2773", {"start": v(169.94, 180.5) * mm, "end": v(170.25, 180.59) * mm});
            skLineSegment(sketch, "E2774", {"start": v(170.25, 180.59) * mm, "end": v(170.57, 180.66) * mm});
            skLineSegment(sketch, "E2775", {"start": v(170.57, 180.66) * mm, "end": v(170.9, 180.72) * mm});
            skLineSegment(sketch, "E2776", {"start": v(170.9, 180.72) * mm, "end": v(171.23, 180.77) * mm});
            skLineSegment(sketch, "E2777", {"start": v(171.23, 180.77) * mm, "end": v(171.55, 180.8) * mm});
            skLineSegment(sketch, "E2778", {"start": v(171.55, 180.8) * mm, "end": v(171.89, 180.82) * mm});
            skLineSegment(sketch, "E2779", {"start": v(171.89, 180.82) * mm, "end": v(172.22, 180.82) * mm});
            skLineSegment(sketch, "E2780", {"start": v(172.22, 180.82) * mm, "end": v(191.96, 180.82) * mm});
            skLineSegment(sketch, "E2781", {"start": v(354.82, -163.29) * mm, "end": v(319.86, -163.29) * mm});
            skLineSegment(sketch, "E2782", {"start": v(319.86, -163.29) * mm, "end": v(319.86, -147.92) * mm});
            skLineSegment(sketch, "E2783", {"start": v(319.86, -147.92) * mm, "end": v(319.86, -147.5) * mm});
            skLineSegment(sketch, "E2784", {"start": v(319.86, -147.5) * mm, "end": v(319.89, -147.06) * mm});
            skLineSegment(sketch, "E2785", {"start": v(319.89, -147.06) * mm, "end": v(319.94, -146.63) * mm});
            skLineSegment(sketch, "E2786", {"start": v(319.94, -146.63) * mm, "end": v(320, -146.21) * mm});
            skLineSegment(sketch, "E2787", {"start": v(320, -146.21) * mm, "end": v(320.1, -145.8) * mm});
            skLineSegment(sketch, "E2788", {"start": v(320.1, -145.8) * mm, "end": v(320.2, -145.38) * mm});
            skLineSegment(sketch, "E2789", {"start": v(320.2, -145.38) * mm, "end": v(320.34, -144.98) * mm});
            skLineSegment(sketch, "E2790", {"start": v(320.34, -144.98) * mm, "end": v(320.5, -144.58) * mm});
            skLineSegment(sketch, "E2791", {"start": v(320.5, -144.58) * mm, "end": v(320.66, -144.19) * mm});
            skLineSegment(sketch, "E2792", {"start": v(320.66, -144.19) * mm, "end": v(320.85, -143.8) * mm});
            skLineSegment(sketch, "E2793", {"start": v(320.85, -143.8) * mm, "end": v(321.07, -143.44) * mm});
            skLineSegment(sketch, "E2794", {"start": v(321.07, -143.44) * mm, "end": v(321.3, -143.08) * mm});
            skLineSegment(sketch, "E2795", {"start": v(321.3, -143.08) * mm, "end": v(321.54, -142.73) * mm});
            skLineSegment(sketch, "E2796", {"start": v(321.54, -142.73) * mm, "end": v(321.81, -142.4) * mm});
            skLineSegment(sketch, "E2797", {"start": v(321.81, -142.4) * mm, "end": v(322.1, -142.07) * mm});
            skLineSegment(sketch, "E2798", {"start": v(322.1, -142.07) * mm, "end": v(322.4, -141.76) * mm});
            skLineSegment(sketch, "E2799", {"start": v(322.4, -141.76) * mm, "end": v(322.7, -141.46) * mm});
            skLineSegment(sketch, "E2800", {"start": v(322.7, -141.46) * mm, "end": v(323.03, -141.18) * mm});
            skLineSegment(sketch, "E2801", {"start": v(323.03, -141.18) * mm, "end": v(323.36, -140.92) * mm});
            skLineSegment(sketch, "E2802", {"start": v(323.36, -140.92) * mm, "end": v(323.7, -140.67) * mm});
            skLineSegment(sketch, "E2803", {"start": v(323.7, -140.67) * mm, "end": v(324.06, -140.44) * mm});
            skLineSegment(sketch, "E2804", {"start": v(324.06, -140.44) * mm, "end": v(324.43, -140.23) * mm});
            skLineSegment(sketch, "E2805", {"start": v(324.43, -140.23) * mm, "end": v(324.8, -140.04) * mm});
            skLineSegment(sketch, "E2806", {"start": v(324.8, -140.04) * mm, "end": v(325.2, -139.87) * mm});
            skLineSegment(sketch, "E2807", {"start": v(325.2, -139.87) * mm, "end": v(325.59, -139.72) * mm});
            skLineSegment(sketch, "E2808", {"start": v(325.59, -139.72) * mm, "end": v(325.99, -139.58) * mm});
            skLineSegment(sketch, "E2809", {"start": v(325.99, -139.58) * mm, "end": v(326.4, -139.47) * mm});
            skLineSegment(sketch, "E2810", {"start": v(326.4, -139.47) * mm, "end": v(326.8, -139.38) * mm});
            skLineSegment(sketch, "E2811", {"start": v(326.8, -139.38) * mm, "end": v(327.23, -139.3) * mm});
            skLineSegment(sketch, "E2812", {"start": v(327.23, -139.3) * mm, "end": v(327.65, -139.25) * mm});
            skLineSegment(sketch, "E2813", {"start": v(327.65, -139.25) * mm, "end": v(328.07, -139.22) * mm});
            skLineSegment(sketch, "E2814", {"start": v(328.07, -139.22) * mm, "end": v(328.5, -139.2) * mm});
            skLineSegment(sketch, "E2815", {"start": v(328.5, -139.2) * mm, "end": v(328.94, -139.2) * mm});
            skLineSegment(sketch, "E2816", {"start": v(328.94, -139.2) * mm, "end": v(329.38, -139.23) * mm});
            skLineSegment(sketch, "E2817", {"start": v(329.38, -139.23) * mm, "end": v(329.81, -139.27) * mm});
            skLineSegment(sketch, "E2818", {"start": v(329.81, -139.27) * mm, "end": v(330.24, -139.33) * mm});
            skLineSegment(sketch, "E2819", {"start": v(330.24, -139.33) * mm, "end": v(330.67, -139.42) * mm});
            skLineSegment(sketch, "E2820", {"start": v(330.67, -139.42) * mm, "end": v(331.09, -139.52) * mm});
            skLineSegment(sketch, "E2821", {"start": v(331.09, -139.52) * mm, "end": v(331.5, -139.65) * mm});
            skLineSegment(sketch, "E2822", {"start": v(331.5, -139.65) * mm, "end": v(331.9, -139.8) * mm});
            skLineSegment(sketch, "E2823", {"start": v(331.9, -139.8) * mm, "end": v(332.3, -139.97) * mm});
            skLineSegment(sketch, "E2824", {"start": v(332.3, -139.97) * mm, "end": v(332.7, -140.16) * mm});
            skLineSegment(sketch, "E2825", {"start": v(332.7, -140.16) * mm, "end": v(333.07, -140.37) * mm});
            skLineSegment(sketch, "E2826", {"start": v(333.07, -140.37) * mm, "end": v(333.44, -140.6) * mm});
            skLineSegment(sketch, "E2827", {"start": v(333.44, -140.6) * mm, "end": v(333.8, -140.84) * mm});
            skLineSegment(sketch, "E2828", {"start": v(333.8, -140.84) * mm, "end": v(334.15, -141.1) * mm});
            skLineSegment(sketch, "E2829", {"start": v(334.15, -141.1) * mm, "end": v(334.48, -141.39) * mm});
            skLineSegment(sketch, "E2830", {"start": v(334.48, -141.39) * mm, "end": v(334.8, -141.7) * mm});
            skLineSegment(sketch, "E2831", {"start": v(334.8, -141.7) * mm, "end": v(335.1, -142) * mm});
            skLineSegment(sketch, "E2832", {"start": v(335.1, -142) * mm, "end": v(335.38, -142.33) * mm});
            skLineSegment(sketch, "E2833", {"start": v(335.38, -142.33) * mm, "end": v(335.65, -142.68) * mm});
            skLineSegment(sketch, "E2834", {"start": v(335.65, -142.68) * mm, "end": v(335.9, -143.03) * mm});
            skLineSegment(sketch, "E2835", {"start": v(335.9, -143.03) * mm, "end": v(336.13, -143.4) * mm});
            skLineSegment(sketch, "E2836", {"start": v(336.13, -143.4) * mm, "end": v(336.34, -143.77) * mm});
            skLineSegment(sketch, "E2837", {"start": v(336.34, -143.77) * mm, "end": v(336.53, -144.16) * mm});
            skLineSegment(sketch, "E2838", {"start": v(336.53, -144.16) * mm, "end": v(336.7, -144.55) * mm});
            skLineSegment(sketch, "E2839", {"start": v(336.7, -144.55) * mm, "end": v(336.85, -144.95) * mm});
            skLineSegment(sketch, "E2840", {"start": v(336.85, -144.95) * mm, "end": v(336.98, -145.36) * mm});
            skLineSegment(sketch, "E2841", {"start": v(336.98, -145.36) * mm, "end": v(337.1, -145.78) * mm});
            skLineSegment(sketch, "E2842", {"start": v(337.1, -145.78) * mm, "end": v(337.18, -146.2) * mm});
            skLineSegment(sketch, "E2843", {"start": v(337.18, -146.2) * mm, "end": v(337.25, -146.62) * mm});
            skLineSegment(sketch, "E2844", {"start": v(337.25, -146.62) * mm, "end": v(337.3, -147.05) * mm});
            skLineSegment(sketch, "E2845", {"start": v(337.3, -147.05) * mm, "end": v(337.33, -147.49) * mm});
            skLineSegment(sketch, "E2846", {"start": v(337.33, -147.49) * mm, "end": v(337.33, -147.92) * mm});
            skLineSegment(sketch, "E2847", {"start": v(337.33, -147.92) * mm, "end": v(337.33, -163.29) * mm});
            skLineSegment(sketch, "E2848", {"start": v(337.33, -147.92) * mm, "end": v(337.34, -147.56) * mm});
            skLineSegment(sketch, "E2849", {"start": v(337.34, -147.56) * mm, "end": v(337.36, -147.2) * mm});
            skLineSegment(sketch, "E2850", {"start": v(337.36, -147.2) * mm, "end": v(337.4, -146.85) * mm});
            skLineSegment(sketch, "E2851", {"start": v(337.4, -146.85) * mm, "end": v(337.45, -146.5) * mm});
            skLineSegment(sketch, "E2852", {"start": v(337.45, -146.5) * mm, "end": v(337.52, -146.16) * mm});
            skLineSegment(sketch, "E2853", {"start": v(337.52, -146.16) * mm, "end": v(337.61, -145.82) * mm});
            skLineSegment(sketch, "E2854", {"start": v(337.61, -145.82) * mm, "end": v(337.72, -145.48) * mm});
            skLineSegment(sketch, "E2855", {"start": v(337.72, -145.48) * mm, "end": v(337.85, -145.15) * mm});
            skLineSegment(sketch, "E2856", {"start": v(337.85, -145.15) * mm, "end": v(337.99, -144.82) * mm});
            skLineSegment(sketch, "E2857", {"start": v(337.99, -144.82) * mm, "end": v(338.15, -144.5) * mm});
            skLineSegment(sketch, "E2858", {"start": v(338.15, -144.5) * mm, "end": v(338.32, -144.2) * mm});
            skLineSegment(sketch, "E2859", {"start": v(338.32, -144.2) * mm, "end": v(338.51, -143.9) * mm});
            skLineSegment(sketch, "E2860", {"start": v(338.51, -143.9) * mm, "end": v(338.72, -143.61) * mm});
            skLineSegment(sketch, "E2861", {"start": v(338.72, -143.61) * mm, "end": v(338.94, -143.33) * mm});
            skLineSegment(sketch, "E2862", {"start": v(338.94, -143.33) * mm, "end": v(339.17, -143.06) * mm});
            skLineSegment(sketch, "E2863", {"start": v(339.17, -143.06) * mm, "end": v(339.42, -142.8) * mm});
            skLineSegment(sketch, "E2864", {"start": v(339.42, -142.8) * mm, "end": v(339.86, -142.5) * mm});
            skLineSegment(sketch, "E2865", {"start": v(339.86, -142.5) * mm, "end": v(340.3, -142.23) * mm});
            skLineSegment(sketch, "E2866", {"start": v(340.3, -142.23) * mm, "end": v(340.77, -141.97) * mm});
            skLineSegment(sketch, "E2867", {"start": v(340.77, -141.97) * mm, "end": v(341.24, -141.74) * mm});
            skLineSegment(sketch, "E2868", {"start": v(341.24, -141.74) * mm, "end": v(341.72, -141.52) * mm});
            skLineSegment(sketch, "E2869", {"start": v(341.72, -141.52) * mm, "end": v(342.2, -141.33) * mm});
            skLineSegment(sketch, "E2870", {"start": v(342.2, -141.33) * mm, "end": v(342.7, -141.16) * mm});
            skLineSegment(sketch, "E2871", {"start": v(342.7, -141.16) * mm, "end": v(343.2, -141.01) * mm});
            skLineSegment(sketch, "E2872", {"start": v(343.2, -141.01) * mm, "end": v(343.7, -140.89) * mm});
            skLineSegment(sketch, "E2873", {"start": v(343.7, -140.89) * mm, "end": v(344.22, -140.78) * mm});
            skLineSegment(sketch, "E2874", {"start": v(344.22, -140.78) * mm, "end": v(344.74, -140.7) * mm});
            skLineSegment(sketch, "E2875", {"start": v(344.74, -140.7) * mm, "end": v(345.26, -140.64) * mm});
            skLineSegment(sketch, "E2876", {"start": v(345.26, -140.64) * mm, "end": v(345.79, -140.61) * mm});
            skLineSegment(sketch, "E2877", {"start": v(345.79, -140.61) * mm, "end": v(346.31, -140.6) * mm});
            skLineSegment(sketch, "E2878", {"start": v(346.31, -140.6) * mm, "end": v(346.84, -140.61) * mm});
            skLineSegment(sketch, "E2879", {"start": v(346.84, -140.61) * mm, "end": v(347.37, -140.65) * mm});
            skLineSegment(sketch, "E2880", {"start": v(347.37, -140.65) * mm, "end": v(347.84, -140.66) * mm});
            skLineSegment(sketch, "E2881", {"start": v(347.84, -140.66) * mm, "end": v(348.31, -140.66) * mm});
            skLineSegment(sketch, "E2882", {"start": v(348.31, -140.66) * mm, "end": v(348.78, -140.65) * mm});
            skLineSegment(sketch, "E2883", {"start": v(348.78, -140.65) * mm, "end": v(349.25, -140.63) * mm});
            skLineSegment(sketch, "E2884", {"start": v(349.25, -140.63) * mm, "end": v(349.72, -140.6) * mm});
            skLineSegment(sketch, "E2885", {"start": v(349.72, -140.6) * mm, "end": v(350.2, -140.56) * mm});
            skLineSegment(sketch, "E2886", {"start": v(350.2, -140.56) * mm, "end": v(350.66, -140.52) * mm});
            skLineSegment(sketch, "E2887", {"start": v(350.66, -140.52) * mm, "end": v(351.13, -140.47) * mm});
            skLineSegment(sketch, "E2888", {"start": v(351.13, -140.47) * mm, "end": v(351.6, -140.4) * mm});
            skLineSegment(sketch, "E2889", {"start": v(351.6, -140.4) * mm, "end": v(352.06, -140.34) * mm});
            skLineSegment(sketch, "E2890", {"start": v(352.06, -140.34) * mm, "end": v(352.53, -140.26) * mm});
            skLineSegment(sketch, "E2891", {"start": v(352.53, -140.26) * mm, "end": v(353, -140.17) * mm});
            skLineSegment(sketch, "E2892", {"start": v(353, -140.17) * mm, "end": v(353.45, -140.08) * mm});
            skLineSegment(sketch, "E2893", {"start": v(353.45, -140.08) * mm, "end": v(353.91, -139.98) * mm});
            skLineSegment(sketch, "E2894", {"start": v(353.91, -139.98) * mm, "end": v(354.37, -139.87) * mm});
            skLineSegment(sketch, "E2895", {"start": v(354.37, -139.87) * mm, "end": v(354.82, -139.75) * mm});
            skLineSegment(sketch, "E2896", {"start": v(355.31, -117.08) * mm, "end": v(355.32, -117.45) * mm});
            skLineSegment(sketch, "E2897", {"start": v(355.32, -117.45) * mm, "end": v(355.31, -117.82) * mm});
            skLineSegment(sketch, "E2898", {"start": v(355.31, -117.82) * mm, "end": v(355.3, -118.18) * mm});
            skLineSegment(sketch, "E2899", {"start": v(355.3, -118.18) * mm, "end": v(355.27, -118.55) * mm});
            skLineSegment(sketch, "E2900", {"start": v(355.27, -118.55) * mm, "end": v(355.24, -118.9) * mm});
            skLineSegment(sketch, "E2901", {"start": v(355.24, -118.9) * mm, "end": v(355.2, -119.27) * mm});
            skLineSegment(sketch, "E2902", {"start": v(355.2, -119.27) * mm, "end": v(355.14, -119.63) * mm});
            skLineSegment(sketch, "E2903", {"start": v(355.14, -119.63) * mm, "end": v(355.08, -119.99) * mm});
            skLineSegment(sketch, "E2904", {"start": v(355.08, -119.99) * mm, "end": v(355.01, -120.35) * mm});
            skLineSegment(sketch, "E2905", {"start": v(355.01, -120.35) * mm, "end": v(354.93, -120.7) * mm});
            skLineSegment(sketch, "E2906", {"start": v(354.93, -120.7) * mm, "end": v(354.85, -121.05) * mm});
            skLineSegment(sketch, "E2907", {"start": v(354.85, -121.05) * mm, "end": v(354.75, -121.4) * mm});
            skLineSegment(sketch, "E2908", {"start": v(354.75, -121.4) * mm, "end": v(354.65, -121.75) * mm});
            skLineSegment(sketch, "E2909", {"start": v(354.65, -121.75) * mm, "end": v(354.53, -122.1) * mm});
            skLineSegment(sketch, "E2910", {"start": v(354.53, -122.1) * mm, "end": v(354.41, -122.43) * mm});
            skLineSegment(sketch, "E2911", {"start": v(354.41, -122.43) * mm, "end": v(354.28, -122.77) * mm});
            skLineSegment(sketch, "E2912", {"start": v(354.28, -122.77) * mm, "end": v(354.14, -123.1) * mm});
            skLineSegment(sketch, "E2913", {"start": v(354.14, -123.1) * mm, "end": v(354, -123.44) * mm});
            skLineSegment(sketch, "E2914", {"start": v(354, -123.44) * mm, "end": v(353.84, -123.76) * mm});
            skLineSegment(sketch, "E2915", {"start": v(353.84, -123.76) * mm, "end": v(353.68, -124.09) * mm});
            skLineSegment(sketch, "E2916", {"start": v(353.68, -124.09) * mm, "end": v(353.5, -124.4) * mm});
            skLineSegment(sketch, "E2917", {"start": v(353.5, -124.4) * mm, "end": v(353.33, -124.72) * mm});
            skLineSegment(sketch, "E2918", {"start": v(353.33, -124.72) * mm, "end": v(353.14, -125.03) * mm});
            skLineSegment(sketch, "E2919", {"start": v(353.14, -125.03) * mm, "end": v(352.95, -125.34) * mm});
            skLineSegment(sketch, "E2920", {"start": v(352.95, -125.34) * mm, "end": v(352.75, -125.64) * mm});
            skLineSegment(sketch, "E2921", {"start": v(352.75, -125.64) * mm, "end": v(352.54, -125.94) * mm});
            skLineSegment(sketch, "E2922", {"start": v(352.54, -125.94) * mm, "end": v(352.32, -126.23) * mm});
            skLineSegment(sketch, "E2923", {"start": v(352.32, -126.23) * mm, "end": v(352.1, -126.52) * mm});
            skLineSegment(sketch, "E2924", {"start": v(352.1, -126.52) * mm, "end": v(351.86, -126.8) * mm});
            skLineSegment(sketch, "E2925", {"start": v(351.86, -126.8) * mm, "end": v(351.62, -127.08) * mm});
            skLineSegment(sketch, "E2926", {"start": v(351.62, -127.08) * mm, "end": v(351.37, -127.35) * mm});
            skLineSegment(sketch, "E2927", {"start": v(351.37, -127.35) * mm, "end": v(351.12, -127.61) * mm});
            skLineSegment(sketch, "E2928", {"start": v(351.12, -127.61) * mm, "end": v(350.79, -127.92) * mm});
            skLineSegment(sketch, "E2929", {"start": v(350.79, -127.92) * mm, "end": v(350.45, -128.21) * mm});
            skLineSegment(sketch, "E2930", {"start": v(350.45, -128.21) * mm, "end": v(350.1, -128.5) * mm});
            skLineSegment(sketch, "E2931", {"start": v(350.1, -128.5) * mm, "end": v(349.75, -128.78) * mm});
            skLineSegment(sketch, "E2932", {"start": v(349.75, -128.78) * mm, "end": v(349.39, -129.05) * mm});
            skLineSegment(sketch, "E2933", {"start": v(349.39, -129.05) * mm, "end": v(349.02, -129.31) * mm});
            skLineSegment(sketch, "E2934", {"start": v(349.02, -129.31) * mm, "end": v(348.65, -129.56) * mm});
            skLineSegment(sketch, "E2935", {"start": v(348.65, -129.56) * mm, "end": v(348.28, -129.8) * mm});
            skLineSegment(sketch, "E2936", {"start": v(348.28, -129.8) * mm, "end": v(347.9, -130.03) * mm});
            skLineSegment(sketch, "E2937", {"start": v(347.9, -130.03) * mm, "end": v(347.5, -130.26) * mm});
            skLineSegment(sketch, "E2938", {"start": v(347.5, -130.26) * mm, "end": v(347.11, -130.47) * mm});
            skLineSegment(sketch, "E2939", {"start": v(347.11, -130.47) * mm, "end": v(346.71, -130.67) * mm});
            skLineSegment(sketch, "E2940", {"start": v(346.71, -130.67) * mm, "end": v(346.31, -130.86) * mm});
            skLineSegment(sketch, "E2941", {"start": v(346.31, -130.86) * mm, "end": v(345.9, -131.05) * mm});
            skLineSegment(sketch, "E2942", {"start": v(345.9, -131.05) * mm, "end": v(345.5, -131.22) * mm});
            skLineSegment(sketch, "E2943", {"start": v(345.5, -131.22) * mm, "end": v(345.08, -131.38) * mm});
            skLineSegment(sketch, "E2944", {"start": v(345.08, -131.38) * mm, "end": v(344.66, -131.53) * mm});
            skLineSegment(sketch, "E2945", {"start": v(344.66, -131.53) * mm, "end": v(344.24, -131.67) * mm});
            skLineSegment(sketch, "E2946", {"start": v(344.24, -131.67) * mm, "end": v(343.81, -131.8) * mm});
            skLineSegment(sketch, "E2947", {"start": v(343.81, -131.8) * mm, "end": v(343.38, -131.93) * mm});
            skLineSegment(sketch, "E2948", {"start": v(343.38, -131.93) * mm, "end": v(342.95, -132.04) * mm});
            skLineSegment(sketch, "E2949", {"start": v(342.95, -132.04) * mm, "end": v(342.52, -132.14) * mm});
            skLineSegment(sketch, "E2950", {"start": v(342.52, -132.14) * mm, "end": v(342.08, -132.23) * mm});
            skLineSegment(sketch, "E2951", {"start": v(342.08, -132.23) * mm, "end": v(341.64, -132.3) * mm});
            skLineSegment(sketch, "E2952", {"start": v(341.64, -132.3) * mm, "end": v(341.2, -132.37) * mm});
            skLineSegment(sketch, "E2953", {"start": v(341.2, -132.37) * mm, "end": v(340.75, -132.43) * mm});
            skLineSegment(sketch, "E2954", {"start": v(340.75, -132.43) * mm, "end": v(340.3, -132.47) * mm});
            skLineSegment(sketch, "E2955", {"start": v(340.3, -132.47) * mm, "end": v(339.86, -132.5) * mm});
            skLineSegment(sketch, "E2956", {"start": v(339.86, -132.5) * mm, "end": v(339.4, -132.53) * mm});
            skLineSegment(sketch, "E2957", {"start": v(339.4, -132.53) * mm, "end": v(338.96, -132.54) * mm});
            skLineSegment(sketch, "E2958", {"start": v(338.96, -132.54) * mm, "end": v(338.5, -132.55) * mm});
            skLineSegment(sketch, "E2959", {"start": v(338.5, -132.55) * mm, "end": v(338.06, -132.53) * mm});
            skLineSegment(sketch, "E2960", {"start": v(338.06, -132.53) * mm, "end": v(337.56, -132.55) * mm});
            skLineSegment(sketch, "E2961", {"start": v(337.56, -132.55) * mm, "end": v(337.07, -132.55) * mm});
            skLineSegment(sketch, "E2962", {"start": v(337.07, -132.55) * mm, "end": v(336.58, -132.54) * mm});
            skLineSegment(sketch, "E2963", {"start": v(336.58, -132.54) * mm, "end": v(336.1, -132.52) * mm});
            skLineSegment(sketch, "E2964", {"start": v(336.1, -132.52) * mm, "end": v(335.61, -132.48) * mm});
            skLineSegment(sketch, "E2965", {"start": v(335.61, -132.48) * mm, "end": v(335.13, -132.43) * mm});
            skLineSegment(sketch, "E2966", {"start": v(335.13, -132.43) * mm, "end": v(334.64, -132.37) * mm});
            skLineSegment(sketch, "E2967", {"start": v(334.64, -132.37) * mm, "end": v(334.16, -132.3) * mm});
            skLineSegment(sketch, "E2968", {"start": v(334.16, -132.3) * mm, "end": v(333.68, -132.22) * mm});
            skLineSegment(sketch, "E2969", {"start": v(333.68, -132.22) * mm, "end": v(333.2, -132.12) * mm});
            skLineSegment(sketch, "E2970", {"start": v(333.2, -132.12) * mm, "end": v(332.74, -132.02) * mm});
            skLineSegment(sketch, "E2971", {"start": v(332.74, -132.02) * mm, "end": v(332.27, -131.9) * mm});
            skLineSegment(sketch, "E2972", {"start": v(332.27, -131.9) * mm, "end": v(331.8, -131.77) * mm});
            skLineSegment(sketch, "E2973", {"start": v(331.8, -131.77) * mm, "end": v(331.34, -131.62) * mm});
            skLineSegment(sketch, "E2974", {"start": v(331.34, -131.62) * mm, "end": v(330.88, -131.47) * mm});
            skLineSegment(sketch, "E2975", {"start": v(330.88, -131.47) * mm, "end": v(330.42, -131.3) * mm});
            skLineSegment(sketch, "E2976", {"start": v(330.42, -131.3) * mm, "end": v(329.97, -131.13) * mm});
            skLineSegment(sketch, "E2977", {"start": v(329.97, -131.13) * mm, "end": v(329.53, -130.94) * mm});
            skLineSegment(sketch, "E2978", {"start": v(329.53, -130.94) * mm, "end": v(329.09, -130.75) * mm});
            skLineSegment(sketch, "E2979", {"start": v(329.09, -130.75) * mm, "end": v(328.65, -130.54) * mm});
            skLineSegment(sketch, "E2980", {"start": v(328.65, -130.54) * mm, "end": v(328.22, -130.32) * mm});
            skLineSegment(sketch, "E2981", {"start": v(328.22, -130.32) * mm, "end": v(327.8, -130.09) * mm});
            skLineSegment(sketch, "E2982", {"start": v(327.8, -130.09) * mm, "end": v(327.37, -129.85) * mm});
            skLineSegment(sketch, "E2983", {"start": v(327.37, -129.85) * mm, "end": v(326.96, -129.6) * mm});
            skLineSegment(sketch, "E2984", {"start": v(326.96, -129.6) * mm, "end": v(326.55, -129.33) * mm});
            skLineSegment(sketch, "E2985", {"start": v(326.55, -129.33) * mm, "end": v(326.14, -129.06) * mm});
            skLineSegment(sketch, "E2986", {"start": v(326.14, -129.06) * mm, "end": v(325.75, -128.77) * mm});
            skLineSegment(sketch, "E2987", {"start": v(325.75, -128.77) * mm, "end": v(325.36, -128.48) * mm});
            skLineSegment(sketch, "E2988", {"start": v(325.36, -128.48) * mm, "end": v(324.98, -128.18) * mm});
            skLineSegment(sketch, "E2989", {"start": v(324.98, -128.18) * mm, "end": v(324.6, -127.86) * mm});
            skLineSegment(sketch, "E2990", {"start": v(324.6, -127.86) * mm, "end": v(324.23, -127.54) * mm});
            skLineSegment(sketch, "E2991", {"start": v(324.23, -127.54) * mm, "end": v(323.87, -127.2) * mm});
            skLineSegment(sketch, "E2992", {"start": v(323.87, -127.2) * mm, "end": v(323.62, -126.96) * mm});
            skLineSegment(sketch, "E2993", {"start": v(323.62, -126.96) * mm, "end": v(323.37, -126.7) * mm});
            skLineSegment(sketch, "E2994", {"start": v(323.37, -126.7) * mm, "end": v(323.13, -126.44) * mm});
            skLineSegment(sketch, "E2995", {"start": v(323.13, -126.44) * mm, "end": v(322.9, -126.17) * mm});
            skLineSegment(sketch, "E2996", {"start": v(322.9, -126.17) * mm, "end": v(322.67, -125.9) * mm});
            skLineSegment(sketch, "E2997", {"start": v(322.67, -125.9) * mm, "end": v(322.46, -125.62) * mm});
            skLineSegment(sketch, "E2998", {"start": v(322.46, -125.62) * mm, "end": v(322.25, -125.34) * mm});
            skLineSegment(sketch, "E2999", {"start": v(322.25, -125.34) * mm, "end": v(322.04, -125.05) * mm});
            skLineSegment(sketch, "E3000", {"start": v(322.04, -125.05) * mm, "end": v(321.85, -124.75) * mm});
            skLineSegment(sketch, "E3001", {"start": v(321.85, -124.75) * mm, "end": v(321.66, -124.46) * mm});
            skLineSegment(sketch, "E3002", {"start": v(321.66, -124.46) * mm, "end": v(321.48, -124.15) * mm});
            skLineSegment(sketch, "E3003", {"start": v(321.48, -124.15) * mm, "end": v(321.31, -123.85) * mm});
            skLineSegment(sketch, "E3004", {"start": v(321.31, -123.85) * mm, "end": v(321.15, -123.54) * mm});
            skLineSegment(sketch, "E3005", {"start": v(321.15, -123.54) * mm, "end": v(321, -123.22) * mm});
            skLineSegment(sketch, "E3006", {"start": v(321, -123.22) * mm, "end": v(320.84, -122.9) * mm});
            skLineSegment(sketch, "E3007", {"start": v(320.84, -122.9) * mm, "end": v(320.7, -122.58) * mm});
            skLineSegment(sketch, "E3008", {"start": v(320.7, -122.58) * mm, "end": v(320.57, -122.25) * mm});
            skLineSegment(sketch, "E3009", {"start": v(320.57, -122.25) * mm, "end": v(320.45, -121.93) * mm});
            skLineSegment(sketch, "E3010", {"start": v(320.45, -121.93) * mm, "end": v(320.34, -121.6) * mm});
            skLineSegment(sketch, "E3011", {"start": v(320.34, -121.6) * mm, "end": v(320.23, -121.26) * mm});
            skLineSegment(sketch, "E3012", {"start": v(320.23, -121.26) * mm, "end": v(320.13, -120.92) * mm});
            skLineSegment(sketch, "E3013", {"start": v(320.13, -120.92) * mm, "end": v(320.05, -120.58) * mm});
            skLineSegment(sketch, "E3014", {"start": v(320.05, -120.58) * mm, "end": v(319.97, -120.24) * mm});
            skLineSegment(sketch, "E3015", {"start": v(319.97, -120.24) * mm, "end": v(319.9, -119.9) * mm});
            skLineSegment(sketch, "E3016", {"start": v(319.9, -119.9) * mm, "end": v(319.83, -119.55) * mm});
            skLineSegment(sketch, "E3017", {"start": v(319.83, -119.55) * mm, "end": v(319.78, -119.2) * mm});
            skLineSegment(sketch, "E3018", {"start": v(319.78, -119.2) * mm, "end": v(319.74, -118.85) * mm});
            skLineSegment(sketch, "E3019", {"start": v(319.74, -118.85) * mm, "end": v(319.7, -118.5) * mm});
            skLineSegment(sketch, "E3020", {"start": v(319.7, -118.5) * mm, "end": v(319.67, -118.14) * mm});
            skLineSegment(sketch, "E3021", {"start": v(319.67, -118.14) * mm, "end": v(319.66, -117.79) * mm});
            skLineSegment(sketch, "E3022", {"start": v(319.66, -117.79) * mm, "end": v(319.65, -117.43) * mm});
            skLineSegment(sketch, "E3023", {"start": v(319.65, -117.43) * mm, "end": v(319.65, -117.07) * mm});
            skLineSegment(sketch, "E3024", {"start": v(319.65, -117.07) * mm, "end": v(319.65, -116.71) * mm});
            skLineSegment(sketch, "E3025", {"start": v(319.65, -116.71) * mm, "end": v(319.67, -116.35) * mm});
            skLineSegment(sketch, "E3026", {"start": v(319.67, -116.35) * mm, "end": v(319.69, -116) * mm});
            skLineSegment(sketch, "E3027", {"start": v(319.69, -116) * mm, "end": v(319.72, -115.63) * mm});
            skLineSegment(sketch, "E3028", {"start": v(319.72, -115.63) * mm, "end": v(319.76, -115.27) * mm});
            skLineSegment(sketch, "E3029", {"start": v(319.76, -115.27) * mm, "end": v(319.8, -114.92) * mm});
            skLineSegment(sketch, "E3030", {"start": v(319.8, -114.92) * mm, "end": v(319.87, -114.56) * mm});
            skLineSegment(sketch, "E3031", {"start": v(319.87, -114.56) * mm, "end": v(319.94, -114.21) * mm});
            skLineSegment(sketch, "E3032", {"start": v(319.94, -114.21) * mm, "end": v(320.01, -113.86) * mm});
            skLineSegment(sketch, "E3033", {"start": v(320.01, -113.86) * mm, "end": v(320.1, -113.52) * mm});
            skLineSegment(sketch, "E3034", {"start": v(320.1, -113.52) * mm, "end": v(320.2, -113.17) * mm});
            skLineSegment(sketch, "E3035", {"start": v(320.2, -113.17) * mm, "end": v(320.3, -112.83) * mm});
            skLineSegment(sketch, "E3036", {"start": v(320.3, -112.83) * mm, "end": v(320.4, -112.49) * mm});
            skLineSegment(sketch, "E3037", {"start": v(320.4, -112.49) * mm, "end": v(320.53, -112.15) * mm});
            skLineSegment(sketch, "E3038", {"start": v(320.53, -112.15) * mm, "end": v(320.66, -111.82) * mm});
            skLineSegment(sketch, "E3039", {"start": v(320.66, -111.82) * mm, "end": v(320.8, -111.5) * mm});
            skLineSegment(sketch, "E3040", {"start": v(320.8, -111.5) * mm, "end": v(320.94, -111.17) * mm});
            skLineSegment(sketch, "E3041", {"start": v(320.94, -111.17) * mm, "end": v(321.1, -110.84) * mm});
            skLineSegment(sketch, "E3042", {"start": v(321.1, -110.84) * mm, "end": v(321.25, -110.53) * mm});
            skLineSegment(sketch, "E3043", {"start": v(321.25, -110.53) * mm, "end": v(321.42, -110.21) * mm});
            skLineSegment(sketch, "E3044", {"start": v(321.42, -110.21) * mm, "end": v(321.6, -109.9) * mm});
            skLineSegment(sketch, "E3045", {"start": v(321.6, -109.9) * mm, "end": v(321.79, -109.6) * mm});
            skLineSegment(sketch, "E3046", {"start": v(321.79, -109.6) * mm, "end": v(321.98, -109.3) * mm});
            skLineSegment(sketch, "E3047", {"start": v(321.98, -109.3) * mm, "end": v(322.18, -109) * mm});
            skLineSegment(sketch, "E3048", {"start": v(322.18, -109) * mm, "end": v(322.4, -108.7) * mm});
            skLineSegment(sketch, "E3049", {"start": v(322.4, -108.7) * mm, "end": v(322.6, -108.42) * mm});
            skLineSegment(sketch, "E3050", {"start": v(322.6, -108.42) * mm, "end": v(322.83, -108.14) * mm});
            skLineSegment(sketch, "E3051", {"start": v(322.83, -108.14) * mm, "end": v(323.07, -107.87) * mm});
            skLineSegment(sketch, "E3052", {"start": v(323.07, -107.87) * mm, "end": v(323.3, -107.6) * mm});
            skLineSegment(sketch, "E3053", {"start": v(323.3, -107.6) * mm, "end": v(323.55, -107.34) * mm});
            skLineSegment(sketch, "E3054", {"start": v(323.55, -107.34) * mm, "end": v(323.8, -107.08) * mm});
            skLineSegment(sketch, "E3055", {"start": v(323.8, -107.08) * mm, "end": v(324.07, -106.83) * mm});
            skLineSegment(sketch, "E3056", {"start": v(324.07, -106.83) * mm, "end": v(324.43, -106.5) * mm});
            skLineSegment(sketch, "E3057", {"start": v(324.43, -106.5) * mm, "end": v(324.8, -106.2) * mm});
            skLineSegment(sketch, "E3058", {"start": v(324.8, -106.2) * mm, "end": v(325.17, -105.89) * mm});
            skLineSegment(sketch, "E3059", {"start": v(325.17, -105.89) * mm, "end": v(325.55, -105.6) * mm});
            skLineSegment(sketch, "E3060", {"start": v(325.55, -105.6) * mm, "end": v(325.93, -105.3) * mm});
            skLineSegment(sketch, "E3061", {"start": v(325.93, -105.3) * mm, "end": v(326.32, -105.03) * mm});
            skLineSegment(sketch, "E3062", {"start": v(326.32, -105.03) * mm, "end": v(326.72, -104.77) * mm});
            skLineSegment(sketch, "E3063", {"start": v(326.72, -104.77) * mm, "end": v(327.13, -104.52) * mm});
            skLineSegment(sketch, "E3064", {"start": v(327.13, -104.52) * mm, "end": v(327.54, -104.27) * mm});
            skLineSegment(sketch, "E3065", {"start": v(327.54, -104.27) * mm, "end": v(327.96, -104.04) * mm});
            skLineSegment(sketch, "E3066", {"start": v(327.96, -104.04) * mm, "end": v(328.38, -103.82) * mm});
            skLineSegment(sketch, "E3067", {"start": v(328.38, -103.82) * mm, "end": v(328.8, -103.6) * mm});
            skLineSegment(sketch, "E3068", {"start": v(328.8, -103.6) * mm, "end": v(329.24, -103.4) * mm});
            skLineSegment(sketch, "E3069", {"start": v(329.24, -103.4) * mm, "end": v(329.67, -103.22) * mm});
            skLineSegment(sketch, "E3070", {"start": v(329.67, -103.22) * mm, "end": v(330.11, -103.04) * mm});
            skLineSegment(sketch, "E3071", {"start": v(330.11, -103.04) * mm, "end": v(330.56, -102.87) * mm});
            skLineSegment(sketch, "E3072", {"start": v(330.56, -102.87) * mm, "end": v(331, -102.7) * mm});
            skLineSegment(sketch, "E3073", {"start": v(331, -102.7) * mm, "end": v(331.46, -102.56) * mm});
            skLineSegment(sketch, "E3074", {"start": v(331.46, -102.56) * mm, "end": v(331.92, -102.43) * mm});
            skLineSegment(sketch, "E3075", {"start": v(331.92, -102.43) * mm, "end": v(332.38, -102.3) * mm});
            skLineSegment(sketch, "E3076", {"start": v(332.38, -102.3) * mm, "end": v(332.84, -102.2) * mm});
            skLineSegment(sketch, "E3077", {"start": v(332.84, -102.2) * mm, "end": v(333.3, -102.1) * mm});
            skLineSegment(sketch, "E3078", {"start": v(333.3, -102.1) * mm, "end": v(333.77, -102) * mm});
            skLineSegment(sketch, "E3079", {"start": v(333.77, -102) * mm, "end": v(334.25, -101.92) * mm});
            skLineSegment(sketch, "E3080", {"start": v(334.25, -101.92) * mm, "end": v(334.72, -101.86) * mm});
            skLineSegment(sketch, "E3081", {"start": v(334.72, -101.86) * mm, "end": v(335.2, -101.8) * mm});
            skLineSegment(sketch, "E3082", {"start": v(335.2, -101.8) * mm, "end": v(335.67, -101.76) * mm});
            skLineSegment(sketch, "E3083", {"start": v(335.67, -101.76) * mm, "end": v(336.15, -101.73) * mm});
            skLineSegment(sketch, "E3084", {"start": v(336.15, -101.73) * mm, "end": v(336.63, -101.7) * mm});
            skLineSegment(sketch, "E3085", {"start": v(336.63, -101.7) * mm, "end": v(337.11, -101.7) * mm});
            skLineSegment(sketch, "E3086", {"start": v(337.11, -101.7) * mm, "end": v(337.6, -101.7) * mm});
            skLineSegment(sketch, "E3087", {"start": v(337.6, -101.7) * mm, "end": v(338.08, -101.72) * mm});
            skLineSegment(sketch, "E3088", {"start": v(338.08, -101.72) * mm, "end": v(338.53, -101.72) * mm});
            skLineSegment(sketch, "E3089", {"start": v(338.53, -101.72) * mm, "end": v(338.98, -101.72) * mm});
            skLineSegment(sketch, "E3090", {"start": v(338.98, -101.72) * mm, "end": v(339.42, -101.74) * mm});
            skLineSegment(sketch, "E3091", {"start": v(339.42, -101.74) * mm, "end": v(339.87, -101.76) * mm});
            skLineSegment(sketch, "E3092", {"start": v(339.87, -101.76) * mm, "end": v(340.32, -101.8) * mm});
            skLineSegment(sketch, "E3093", {"start": v(340.32, -101.8) * mm, "end": v(340.76, -101.85) * mm});
            skLineSegment(sketch, "E3094", {"start": v(340.76, -101.85) * mm, "end": v(341.2, -101.9) * mm});
            skLineSegment(sketch, "E3095", {"start": v(341.2, -101.9) * mm, "end": v(341.64, -101.98) * mm});
            skLineSegment(sketch, "E3096", {"start": v(341.64, -101.98) * mm, "end": v(342.08, -102.06) * mm});
            skLineSegment(sketch, "E3097", {"start": v(342.08, -102.06) * mm, "end": v(342.52, -102.15) * mm});
            skLineSegment(sketch, "E3098", {"start": v(342.52, -102.15) * mm, "end": v(342.95, -102.26) * mm});
            skLineSegment(sketch, "E3099", {"start": v(342.95, -102.26) * mm, "end": v(343.38, -102.37) * mm});
            skLineSegment(sketch, "E3100", {"start": v(343.38, -102.37) * mm, "end": v(343.8, -102.5) * mm});
            skLineSegment(sketch, "E3101", {"start": v(343.8, -102.5) * mm, "end": v(344.23, -102.63) * mm});
            skLineSegment(sketch, "E3102", {"start": v(344.23, -102.63) * mm, "end": v(344.65, -102.78) * mm});
            skLineSegment(sketch, "E3103", {"start": v(344.65, -102.78) * mm, "end": v(345.06, -102.93) * mm});
            skLineSegment(sketch, "E3104", {"start": v(345.06, -102.93) * mm, "end": v(345.47, -103.1) * mm});
            skLineSegment(sketch, "E3105", {"start": v(345.47, -103.1) * mm, "end": v(345.88, -103.28) * mm});
            skLineSegment(sketch, "E3106", {"start": v(345.88, -103.28) * mm, "end": v(346.28, -103.46) * mm});
            skLineSegment(sketch, "E3107", {"start": v(346.28, -103.46) * mm, "end": v(346.68, -103.66) * mm});
            skLineSegment(sketch, "E3108", {"start": v(346.68, -103.66) * mm, "end": v(347.08, -103.87) * mm});
            skLineSegment(sketch, "E3109", {"start": v(347.08, -103.87) * mm, "end": v(347.46, -104.08) * mm});
            skLineSegment(sketch, "E3110", {"start": v(347.46, -104.08) * mm, "end": v(347.85, -104.3) * mm});
            skLineSegment(sketch, "E3111", {"start": v(347.85, -104.3) * mm, "end": v(348.23, -104.54) * mm});
            skLineSegment(sketch, "E3112", {"start": v(348.23, -104.54) * mm, "end": v(348.6, -104.79) * mm});
            skLineSegment(sketch, "E3113", {"start": v(348.6, -104.79) * mm, "end": v(348.96, -105.04) * mm});
            skLineSegment(sketch, "E3114", {"start": v(348.96, -105.04) * mm, "end": v(349.32, -105.3) * mm});
            skLineSegment(sketch, "E3115", {"start": v(349.32, -105.3) * mm, "end": v(349.68, -105.58) * mm});
            skLineSegment(sketch, "E3116", {"start": v(349.68, -105.58) * mm, "end": v(350.03, -105.86) * mm});
            skLineSegment(sketch, "E3117", {"start": v(350.03, -105.86) * mm, "end": v(350.37, -106.15) * mm});
            skLineSegment(sketch, "E3118", {"start": v(350.37, -106.15) * mm, "end": v(350.7, -106.46) * mm});
            skLineSegment(sketch, "E3119", {"start": v(350.7, -106.46) * mm, "end": v(351.03, -106.77) * mm});
            skLineSegment(sketch, "E3120", {"start": v(351.03, -106.77) * mm, "end": v(351.28, -107.02) * mm});
            skLineSegment(sketch, "E3121", {"start": v(351.28, -107.02) * mm, "end": v(351.53, -107.29) * mm});
            skLineSegment(sketch, "E3122", {"start": v(351.53, -107.29) * mm, "end": v(351.77, -107.55) * mm});
            skLineSegment(sketch, "E3123", {"start": v(351.77, -107.55) * mm, "end": v(352, -107.83) * mm});
            skLineSegment(sketch, "E3124", {"start": v(352, -107.83) * mm, "end": v(352.23, -108.1) * mm});
            skLineSegment(sketch, "E3125", {"start": v(352.23, -108.1) * mm, "end": v(352.45, -108.4) * mm});
            skLineSegment(sketch, "E3126", {"start": v(352.45, -108.4) * mm, "end": v(352.66, -108.68) * mm});
            skLineSegment(sketch, "E3127", {"start": v(352.66, -108.68) * mm, "end": v(352.86, -108.98) * mm});
            skLineSegment(sketch, "E3128", {"start": v(352.86, -108.98) * mm, "end": v(353.06, -109.28) * mm});
            skLineSegment(sketch, "E3129", {"start": v(353.06, -109.28) * mm, "end": v(353.25, -109.58) * mm});
            skLineSegment(sketch, "E3130", {"start": v(353.25, -109.58) * mm, "end": v(353.43, -109.89) * mm});
            skLineSegment(sketch, "E3131", {"start": v(353.43, -109.89) * mm, "end": v(353.6, -110.2) * mm});
            skLineSegment(sketch, "E3132", {"start": v(353.6, -110.2) * mm, "end": v(353.77, -110.52) * mm});
            skLineSegment(sketch, "E3133", {"start": v(353.77, -110.52) * mm, "end": v(353.92, -110.84) * mm});
            skLineSegment(sketch, "E3134", {"start": v(353.92, -110.84) * mm, "end": v(354.07, -111.16) * mm});
            skLineSegment(sketch, "E3135", {"start": v(354.07, -111.16) * mm, "end": v(354.21, -111.5) * mm});
            skLineSegment(sketch, "E3136", {"start": v(354.21, -111.5) * mm, "end": v(354.35, -111.82) * mm});
            skLineSegment(sketch, "E3137", {"start": v(354.35, -111.82) * mm, "end": v(354.47, -112.16) * mm});
            skLineSegment(sketch, "E3138", {"start": v(354.47, -112.16) * mm, "end": v(354.59, -112.5) * mm});
            skLineSegment(sketch, "E3139", {"start": v(354.59, -112.5) * mm, "end": v(354.7, -112.83) * mm});
            skLineSegment(sketch, "E3140", {"start": v(354.7, -112.83) * mm, "end": v(354.8, -113.18) * mm});
            skLineSegment(sketch, "E3141", {"start": v(354.8, -113.18) * mm, "end": v(354.89, -113.52) * mm});
            skLineSegment(sketch, "E3142", {"start": v(354.89, -113.52) * mm, "end": v(354.97, -113.87) * mm});
            skLineSegment(sketch, "E3143", {"start": v(354.97, -113.87) * mm, "end": v(355.04, -114.22) * mm});
            skLineSegment(sketch, "E3144", {"start": v(355.04, -114.22) * mm, "end": v(355.1, -114.57) * mm});
            skLineSegment(sketch, "E3145", {"start": v(355.1, -114.57) * mm, "end": v(355.16, -114.93) * mm});
            skLineSegment(sketch, "E3146", {"start": v(355.16, -114.93) * mm, "end": v(355.21, -115.28) * mm});
            skLineSegment(sketch, "E3147", {"start": v(355.21, -115.28) * mm, "end": v(355.25, -115.64) * mm});
            skLineSegment(sketch, "E3148", {"start": v(355.25, -115.64) * mm, "end": v(355.28, -116) * mm});
            skLineSegment(sketch, "E3149", {"start": v(355.28, -116) * mm, "end": v(355.3, -116.36) * mm});
            skLineSegment(sketch, "E3150", {"start": v(355.3, -116.36) * mm, "end": v(355.31, -116.72) * mm});
            skLineSegment(sketch, "E3151", {"start": v(355.31, -116.72) * mm, "end": v(355.31, -117.08) * mm});
            skLineSegment(sketch, "E3152", {"start": v(355.31, -78.37) * mm, "end": v(355.32, -78.73) * mm});
            skLineSegment(sketch, "E3153", {"start": v(355.32, -78.73) * mm, "end": v(355.31, -79.1) * mm});
            skLineSegment(sketch, "E3154", {"start": v(355.31, -79.1) * mm, "end": v(355.3, -79.47) * mm});
            skLineSegment(sketch, "E3155", {"start": v(355.3, -79.47) * mm, "end": v(355.27, -79.83) * mm});
            skLineSegment(sketch, "E3156", {"start": v(355.27, -79.83) * mm, "end": v(355.24, -80.2) * mm});
            skLineSegment(sketch, "E3157", {"start": v(355.24, -80.2) * mm, "end": v(355.2, -80.56) * mm});
            skLineSegment(sketch, "E3158", {"start": v(355.2, -80.56) * mm, "end": v(355.14, -80.92) * mm});
            skLineSegment(sketch, "E3159", {"start": v(355.14, -80.92) * mm, "end": v(355.08, -81.27) * mm});
            skLineSegment(sketch, "E3160", {"start": v(355.08, -81.27) * mm, "end": v(355.01, -81.63) * mm});
            skLineSegment(sketch, "E3161", {"start": v(355.01, -81.63) * mm, "end": v(354.93, -81.98) * mm});
            skLineSegment(sketch, "E3162", {"start": v(354.93, -81.98) * mm, "end": v(354.85, -82.34) * mm});
            skLineSegment(sketch, "E3163", {"start": v(354.85, -82.34) * mm, "end": v(354.75, -82.69) * mm});
            skLineSegment(sketch, "E3164", {"start": v(354.75, -82.69) * mm, "end": v(354.65, -83.03) * mm});
            skLineSegment(sketch, "E3165", {"start": v(354.65, -83.03) * mm, "end": v(354.53, -83.38) * mm});
            skLineSegment(sketch, "E3166", {"start": v(354.53, -83.38) * mm, "end": v(354.41, -83.72) * mm});
            skLineSegment(sketch, "E3167", {"start": v(354.41, -83.72) * mm, "end": v(354.28, -84.06) * mm});
            skLineSegment(sketch, "E3168", {"start": v(354.28, -84.06) * mm, "end": v(354.14, -84.4) * mm});
            skLineSegment(sketch, "E3169", {"start": v(354.14, -84.4) * mm, "end": v(354, -84.72) * mm});
            skLineSegment(sketch, "E3170", {"start": v(354, -84.72) * mm, "end": v(353.84, -85.05) * mm});
            skLineSegment(sketch, "E3171", {"start": v(353.84, -85.05) * mm, "end": v(353.68, -85.37) * mm});
            skLineSegment(sketch, "E3172", {"start": v(353.68, -85.37) * mm, "end": v(353.5, -85.7) * mm});
            skLineSegment(sketch, "E3173", {"start": v(353.5, -85.7) * mm, "end": v(353.33, -86) * mm});
            skLineSegment(sketch, "E3174", {"start": v(353.33, -86) * mm, "end": v(353.14, -86.32) * mm});
            skLineSegment(sketch, "E3175", {"start": v(353.14, -86.32) * mm, "end": v(352.95, -86.63) * mm});
            skLineSegment(sketch, "E3176", {"start": v(352.95, -86.63) * mm, "end": v(352.75, -86.93) * mm});
            skLineSegment(sketch, "E3177", {"start": v(352.75, -86.93) * mm, "end": v(352.54, -87.23) * mm});
            skLineSegment(sketch, "E3178", {"start": v(352.54, -87.23) * mm, "end": v(352.32, -87.52) * mm});
            skLineSegment(sketch, "E3179", {"start": v(352.32, -87.52) * mm, "end": v(352.1, -87.8) * mm});
            skLineSegment(sketch, "E3180", {"start": v(352.1, -87.8) * mm, "end": v(351.86, -88.09) * mm});
            skLineSegment(sketch, "E3181", {"start": v(351.86, -88.09) * mm, "end": v(351.62, -88.36) * mm});
            skLineSegment(sketch, "E3182", {"start": v(351.62, -88.36) * mm, "end": v(351.37, -88.63) * mm});
            skLineSegment(sketch, "E3183", {"start": v(351.37, -88.63) * mm, "end": v(351.12, -88.9) * mm});
            skLineSegment(sketch, "E3184", {"start": v(351.12, -88.9) * mm, "end": v(350.79, -89.2) * mm});
            skLineSegment(sketch, "E3185", {"start": v(350.79, -89.2) * mm, "end": v(350.45, -89.5) * mm});
            skLineSegment(sketch, "E3186", {"start": v(350.45, -89.5) * mm, "end": v(350.1, -89.79) * mm});
            skLineSegment(sketch, "E3187", {"start": v(350.1, -89.79) * mm, "end": v(349.75, -90.07) * mm});
            skLineSegment(sketch, "E3188", {"start": v(349.75, -90.07) * mm, "end": v(349.39, -90.34) * mm});
            skLineSegment(sketch, "E3189", {"start": v(349.39, -90.34) * mm, "end": v(349.02, -90.6) * mm});
            skLineSegment(sketch, "E3190", {"start": v(349.02, -90.6) * mm, "end": v(348.65, -90.85) * mm});
            skLineSegment(sketch, "E3191", {"start": v(348.65, -90.85) * mm, "end": v(348.28, -91.09) * mm});
            skLineSegment(sketch, "E3192", {"start": v(348.28, -91.09) * mm, "end": v(347.9, -91.32) * mm});
            skLineSegment(sketch, "E3193", {"start": v(347.9, -91.32) * mm, "end": v(347.5, -91.54) * mm});
            skLineSegment(sketch, "E3194", {"start": v(347.5, -91.54) * mm, "end": v(347.11, -91.75) * mm});
            skLineSegment(sketch, "E3195", {"start": v(347.11, -91.75) * mm, "end": v(346.71, -91.96) * mm});
            skLineSegment(sketch, "E3196", {"start": v(346.71, -91.96) * mm, "end": v(346.31, -92.15) * mm});
            skLineSegment(sketch, "E3197", {"start": v(346.31, -92.15) * mm, "end": v(345.9, -92.33) * mm});
            skLineSegment(sketch, "E3198", {"start": v(345.9, -92.33) * mm, "end": v(345.5, -92.5) * mm});
            skLineSegment(sketch, "E3199", {"start": v(345.5, -92.5) * mm, "end": v(345.08, -92.67) * mm});
            skLineSegment(sketch, "E3200", {"start": v(345.08, -92.67) * mm, "end": v(344.66, -92.82) * mm});
            skLineSegment(sketch, "E3201", {"start": v(344.66, -92.82) * mm, "end": v(344.24, -92.96) * mm});
            skLineSegment(sketch, "E3202", {"start": v(344.24, -92.96) * mm, "end": v(343.81, -93.1) * mm});
            skLineSegment(sketch, "E3203", {"start": v(343.81, -93.1) * mm, "end": v(343.38, -93.21) * mm});
            skLineSegment(sketch, "E3204", {"start": v(343.38, -93.21) * mm, "end": v(342.95, -93.32) * mm});
            skLineSegment(sketch, "E3205", {"start": v(342.95, -93.32) * mm, "end": v(342.52, -93.42) * mm});
            skLineSegment(sketch, "E3206", {"start": v(342.52, -93.42) * mm, "end": v(342.08, -93.51) * mm});
            skLineSegment(sketch, "E3207", {"start": v(342.08, -93.51) * mm, "end": v(341.64, -93.59) * mm});
            skLineSegment(sketch, "E3208", {"start": v(341.64, -93.59) * mm, "end": v(341.2, -93.66) * mm});
            skLineSegment(sketch, "E3209", {"start": v(341.2, -93.66) * mm, "end": v(340.75, -93.71) * mm});
            skLineSegment(sketch, "E3210", {"start": v(340.75, -93.71) * mm, "end": v(340.3, -93.76) * mm});
            skLineSegment(sketch, "E3211", {"start": v(340.3, -93.76) * mm, "end": v(339.86, -93.8) * mm});
            skLineSegment(sketch, "E3212", {"start": v(339.86, -93.8) * mm, "end": v(339.4, -93.82) * mm});
            skLineSegment(sketch, "E3213", {"start": v(339.4, -93.82) * mm, "end": v(338.96, -93.83) * mm});
            skLineSegment(sketch, "E3214", {"start": v(338.96, -93.83) * mm, "end": v(338.5, -93.83) * mm});
            skLineSegment(sketch, "E3215", {"start": v(338.5, -93.83) * mm, "end": v(338.06, -93.82) * mm});
            skLineSegment(sketch, "E3216", {"start": v(338.06, -93.82) * mm, "end": v(337.56, -93.83) * mm});
            skLineSegment(sketch, "E3217", {"start": v(337.56, -93.83) * mm, "end": v(337.07, -93.84) * mm});
            skLineSegment(sketch, "E3218", {"start": v(337.07, -93.84) * mm, "end": v(336.58, -93.83) * mm});
            skLineSegment(sketch, "E3219", {"start": v(336.58, -93.83) * mm, "end": v(336.1, -93.8) * mm});
            skLineSegment(sketch, "E3220", {"start": v(336.1, -93.8) * mm, "end": v(335.61, -93.77) * mm});
            skLineSegment(sketch, "E3221", {"start": v(335.61, -93.77) * mm, "end": v(335.13, -93.72) * mm});
            skLineSegment(sketch, "E3222", {"start": v(335.13, -93.72) * mm, "end": v(334.64, -93.66) * mm});
            skLineSegment(sketch, "E3223", {"start": v(334.64, -93.66) * mm, "end": v(334.16, -93.59) * mm});
            skLineSegment(sketch, "E3224", {"start": v(334.16, -93.59) * mm, "end": v(333.68, -93.5) * mm});
            skLineSegment(sketch, "E3225", {"start": v(333.68, -93.5) * mm, "end": v(333.2, -93.4) * mm});
            skLineSegment(sketch, "E3226", {"start": v(333.2, -93.4) * mm, "end": v(332.74, -93.3) * mm});
            skLineSegment(sketch, "E3227", {"start": v(332.74, -93.3) * mm, "end": v(332.27, -93.18) * mm});
            skLineSegment(sketch, "E3228", {"start": v(332.27, -93.18) * mm, "end": v(331.8, -93.05) * mm});
            skLineSegment(sketch, "E3229", {"start": v(331.8, -93.05) * mm, "end": v(331.34, -92.91) * mm});
            skLineSegment(sketch, "E3230", {"start": v(331.34, -92.91) * mm, "end": v(330.88, -92.76) * mm});
            skLineSegment(sketch, "E3231", {"start": v(330.88, -92.76) * mm, "end": v(330.42, -92.6) * mm});
            skLineSegment(sketch, "E3232", {"start": v(330.42, -92.6) * mm, "end": v(329.97, -92.42) * mm});
            skLineSegment(sketch, "E3233", {"start": v(329.97, -92.42) * mm, "end": v(329.53, -92.23) * mm});
            skLineSegment(sketch, "E3234", {"start": v(329.53, -92.23) * mm, "end": v(329.09, -92.03) * mm});
            skLineSegment(sketch, "E3235", {"start": v(329.09, -92.03) * mm, "end": v(328.65, -91.82) * mm});
            skLineSegment(sketch, "E3236", {"start": v(328.65, -91.82) * mm, "end": v(328.22, -91.6) * mm});
            skLineSegment(sketch, "E3237", {"start": v(328.22, -91.6) * mm, "end": v(327.8, -91.37) * mm});
            skLineSegment(sketch, "E3238", {"start": v(327.8, -91.37) * mm, "end": v(327.37, -91.13) * mm});
            skLineSegment(sketch, "E3239", {"start": v(327.37, -91.13) * mm, "end": v(326.96, -90.88) * mm});
            skLineSegment(sketch, "E3240", {"start": v(326.96, -90.88) * mm, "end": v(326.55, -90.62) * mm});
            skLineSegment(sketch, "E3241", {"start": v(326.55, -90.62) * mm, "end": v(326.14, -90.34) * mm});
            skLineSegment(sketch, "E3242", {"start": v(326.14, -90.34) * mm, "end": v(325.75, -90.06) * mm});
            skLineSegment(sketch, "E3243", {"start": v(325.75, -90.06) * mm, "end": v(325.36, -89.77) * mm});
            skLineSegment(sketch, "E3244", {"start": v(325.36, -89.77) * mm, "end": v(324.98, -89.46) * mm});
            skLineSegment(sketch, "E3245", {"start": v(324.98, -89.46) * mm, "end": v(324.6, -89.15) * mm});
            skLineSegment(sketch, "E3246", {"start": v(324.6, -89.15) * mm, "end": v(324.23, -88.82) * mm});
            skLineSegment(sketch, "E3247", {"start": v(324.23, -88.82) * mm, "end": v(323.87, -88.5) * mm});
            skLineSegment(sketch, "E3248", {"start": v(323.87, -88.5) * mm, "end": v(323.62, -88.24) * mm});
            skLineSegment(sketch, "E3249", {"start": v(323.62, -88.24) * mm, "end": v(323.37, -87.98) * mm});
            skLineSegment(sketch, "E3250", {"start": v(323.37, -87.98) * mm, "end": v(323.13, -87.72) * mm});
            skLineSegment(sketch, "E3251", {"start": v(323.13, -87.72) * mm, "end": v(322.9, -87.46) * mm});
            skLineSegment(sketch, "E3252", {"start": v(322.9, -87.46) * mm, "end": v(322.67, -87.18) * mm});
            skLineSegment(sketch, "E3253", {"start": v(322.67, -87.18) * mm, "end": v(322.46, -86.9) * mm});
            skLineSegment(sketch, "E3254", {"start": v(322.46, -86.9) * mm, "end": v(322.25, -86.62) * mm});
            skLineSegment(sketch, "E3255", {"start": v(322.25, -86.62) * mm, "end": v(322.04, -86.33) * mm});
            skLineSegment(sketch, "E3256", {"start": v(322.04, -86.33) * mm, "end": v(321.85, -86.04) * mm});
            skLineSegment(sketch, "E3257", {"start": v(321.85, -86.04) * mm, "end": v(321.66, -85.74) * mm});
            skLineSegment(sketch, "E3258", {"start": v(321.66, -85.74) * mm, "end": v(321.48, -85.44) * mm});
            skLineSegment(sketch, "E3259", {"start": v(321.48, -85.44) * mm, "end": v(321.31, -85.13) * mm});
            skLineSegment(sketch, "E3260", {"start": v(321.31, -85.13) * mm, "end": v(321.15, -84.82) * mm});
            skLineSegment(sketch, "E3261", {"start": v(321.15, -84.82) * mm, "end": v(321, -84.5) * mm});
            skLineSegment(sketch, "E3262", {"start": v(321, -84.5) * mm, "end": v(320.84, -84.19) * mm});
            skLineSegment(sketch, "E3263", {"start": v(320.84, -84.19) * mm, "end": v(320.7, -83.87) * mm});
            skLineSegment(sketch, "E3264", {"start": v(320.7, -83.87) * mm, "end": v(320.57, -83.54) * mm});
            skLineSegment(sketch, "E3265", {"start": v(320.57, -83.54) * mm, "end": v(320.45, -83.21) * mm});
            skLineSegment(sketch, "E3266", {"start": v(320.45, -83.21) * mm, "end": v(320.34, -82.88) * mm});
            skLineSegment(sketch, "E3267", {"start": v(320.34, -82.88) * mm, "end": v(320.23, -82.54) * mm});
            skLineSegment(sketch, "E3268", {"start": v(320.23, -82.54) * mm, "end": v(320.13, -82.2) * mm});
            skLineSegment(sketch, "E3269", {"start": v(320.13, -82.2) * mm, "end": v(320.05, -81.87) * mm});
            skLineSegment(sketch, "E3270", {"start": v(320.05, -81.87) * mm, "end": v(319.97, -81.52) * mm});
            skLineSegment(sketch, "E3271", {"start": v(319.97, -81.52) * mm, "end": v(319.9, -81.18) * mm});
            skLineSegment(sketch, "E3272", {"start": v(319.9, -81.18) * mm, "end": v(319.83, -80.83) * mm});
            skLineSegment(sketch, "E3273", {"start": v(319.83, -80.83) * mm, "end": v(319.78, -80.48) * mm});
            skLineSegment(sketch, "E3274", {"start": v(319.78, -80.48) * mm, "end": v(319.74, -80.13) * mm});
            skLineSegment(sketch, "E3275", {"start": v(319.74, -80.13) * mm, "end": v(319.7, -79.78) * mm});
            skLineSegment(sketch, "E3276", {"start": v(319.7, -79.78) * mm, "end": v(319.67, -79.43) * mm});
            skLineSegment(sketch, "E3277", {"start": v(319.67, -79.43) * mm, "end": v(319.66, -79.07) * mm});
            skLineSegment(sketch, "E3278", {"start": v(319.66, -79.07) * mm, "end": v(319.65, -78.72) * mm});
            skLineSegment(sketch, "E3279", {"start": v(319.65, -78.72) * mm, "end": v(319.65, -78.36) * mm});
            skLineSegment(sketch, "E3280", {"start": v(319.65, -78.36) * mm, "end": v(319.65, -78) * mm});
            skLineSegment(sketch, "E3281", {"start": v(319.65, -78) * mm, "end": v(319.67, -77.64) * mm});
            skLineSegment(sketch, "E3282", {"start": v(319.67, -77.64) * mm, "end": v(319.69, -77.28) * mm});
            skLineSegment(sketch, "E3283", {"start": v(319.69, -77.28) * mm, "end": v(319.72, -76.92) * mm});
            skLineSegment(sketch, "E3284", {"start": v(319.72, -76.92) * mm, "end": v(319.76, -76.56) * mm});
            skLineSegment(sketch, "E3285", {"start": v(319.76, -76.56) * mm, "end": v(319.8, -76.2) * mm});
            skLineSegment(sketch, "E3286", {"start": v(319.8, -76.2) * mm, "end": v(319.87, -75.85) * mm});
            skLineSegment(sketch, "E3287", {"start": v(319.87, -75.85) * mm, "end": v(319.94, -75.5) * mm});
            skLineSegment(sketch, "E3288", {"start": v(319.94, -75.5) * mm, "end": v(320.01, -75.15) * mm});
            skLineSegment(sketch, "E3289", {"start": v(320.01, -75.15) * mm, "end": v(320.1, -74.8) * mm});
            skLineSegment(sketch, "E3290", {"start": v(320.1, -74.8) * mm, "end": v(320.2, -74.46) * mm});
            skLineSegment(sketch, "E3291", {"start": v(320.2, -74.46) * mm, "end": v(320.3, -74.11) * mm});
            skLineSegment(sketch, "E3292", {"start": v(320.3, -74.11) * mm, "end": v(320.4, -73.77) * mm});
            skLineSegment(sketch, "E3293", {"start": v(320.4, -73.77) * mm, "end": v(320.53, -73.44) * mm});
            skLineSegment(sketch, "E3294", {"start": v(320.53, -73.44) * mm, "end": v(320.66, -73.1) * mm});
            skLineSegment(sketch, "E3295", {"start": v(320.66, -73.1) * mm, "end": v(320.8, -72.78) * mm});
            skLineSegment(sketch, "E3296", {"start": v(320.8, -72.78) * mm, "end": v(320.94, -72.45) * mm});
            skLineSegment(sketch, "E3297", {"start": v(320.94, -72.45) * mm, "end": v(321.1, -72.13) * mm});
            skLineSegment(sketch, "E3298", {"start": v(321.1, -72.13) * mm, "end": v(321.25, -71.81) * mm});
            skLineSegment(sketch, "E3299", {"start": v(321.25, -71.81) * mm, "end": v(321.42, -71.5) * mm});
            skLineSegment(sketch, "E3300", {"start": v(321.42, -71.5) * mm, "end": v(321.6, -71.19) * mm});
            skLineSegment(sketch, "E3301", {"start": v(321.6, -71.19) * mm, "end": v(321.79, -70.88) * mm});
            skLineSegment(sketch, "E3302", {"start": v(321.79, -70.88) * mm, "end": v(321.98, -70.58) * mm});
            skLineSegment(sketch, "E3303", {"start": v(321.98, -70.58) * mm, "end": v(322.18, -70.29) * mm});
            skLineSegment(sketch, "E3304", {"start": v(322.18, -70.29) * mm, "end": v(322.4, -70) * mm});
            skLineSegment(sketch, "E3305", {"start": v(322.4, -70) * mm, "end": v(322.6, -69.7) * mm});
            skLineSegment(sketch, "E3306", {"start": v(322.6, -69.7) * mm, "end": v(322.83, -69.43) * mm});
            skLineSegment(sketch, "E3307", {"start": v(322.83, -69.43) * mm, "end": v(323.07, -69.15) * mm});
            skLineSegment(sketch, "E3308", {"start": v(323.07, -69.15) * mm, "end": v(323.3, -68.89) * mm});
            skLineSegment(sketch, "E3309", {"start": v(323.3, -68.89) * mm, "end": v(323.55, -68.62) * mm});
            skLineSegment(sketch, "E3310", {"start": v(323.55, -68.62) * mm, "end": v(323.8, -68.36) * mm});
            skLineSegment(sketch, "E3311", {"start": v(323.8, -68.36) * mm, "end": v(324.07, -68.11) * mm});
            skLineSegment(sketch, "E3312", {"start": v(324.07, -68.11) * mm, "end": v(324.43, -67.8) * mm});
            skLineSegment(sketch, "E3313", {"start": v(324.43, -67.8) * mm, "end": v(324.8, -67.48) * mm});
            skLineSegment(sketch, "E3314", {"start": v(324.8, -67.48) * mm, "end": v(325.17, -67.17) * mm});
            skLineSegment(sketch, "E3315", {"start": v(325.17, -67.17) * mm, "end": v(325.55, -66.88) * mm});
            skLineSegment(sketch, "E3316", {"start": v(325.55, -66.88) * mm, "end": v(325.93, -66.6) * mm});
            skLineSegment(sketch, "E3317", {"start": v(325.93, -66.6) * mm, "end": v(326.32, -66.32) * mm});
            skLineSegment(sketch, "E3318", {"start": v(326.32, -66.32) * mm, "end": v(326.72, -66.06) * mm});
            skLineSegment(sketch, "E3319", {"start": v(326.72, -66.06) * mm, "end": v(327.13, -65.8) * mm});
            skLineSegment(sketch, "E3320", {"start": v(327.13, -65.8) * mm, "end": v(327.54, -65.56) * mm});
            skLineSegment(sketch, "E3321", {"start": v(327.54, -65.56) * mm, "end": v(327.96, -65.33) * mm});
            skLineSegment(sketch, "E3322", {"start": v(327.96, -65.33) * mm, "end": v(328.38, -65.1) * mm});
            skLineSegment(sketch, "E3323", {"start": v(328.38, -65.1) * mm, "end": v(328.8, -64.9) * mm});
            skLineSegment(sketch, "E3324", {"start": v(328.8, -64.9) * mm, "end": v(329.24, -64.7) * mm});
            skLineSegment(sketch, "E3325", {"start": v(329.24, -64.7) * mm, "end": v(329.67, -64.5) * mm});
            skLineSegment(sketch, "E3326", {"start": v(329.67, -64.5) * mm, "end": v(330.11, -64.32) * mm});
            skLineSegment(sketch, "E3327", {"start": v(330.11, -64.32) * mm, "end": v(330.56, -64.15) * mm});
            skLineSegment(sketch, "E3328", {"start": v(330.56, -64.15) * mm, "end": v(331, -64) * mm});
            skLineSegment(sketch, "E3329", {"start": v(331, -64) * mm, "end": v(331.46, -63.85) * mm});
            skLineSegment(sketch, "E3330", {"start": v(331.46, -63.85) * mm, "end": v(331.92, -63.71) * mm});
            skLineSegment(sketch, "E3331", {"start": v(331.92, -63.71) * mm, "end": v(332.38, -63.59) * mm});
            skLineSegment(sketch, "E3332", {"start": v(332.38, -63.59) * mm, "end": v(332.84, -63.48) * mm});
            skLineSegment(sketch, "E3333", {"start": v(332.84, -63.48) * mm, "end": v(333.3, -63.38) * mm});
            skLineSegment(sketch, "E3334", {"start": v(333.3, -63.38) * mm, "end": v(333.77, -63.29) * mm});
            skLineSegment(sketch, "E3335", {"start": v(333.77, -63.29) * mm, "end": v(334.25, -63.2) * mm});
            skLineSegment(sketch, "E3336", {"start": v(334.25, -63.2) * mm, "end": v(334.72, -63.14) * mm});
            skLineSegment(sketch, "E3337", {"start": v(334.72, -63.14) * mm, "end": v(335.2, -63.09) * mm});
            skLineSegment(sketch, "E3338", {"start": v(335.2, -63.09) * mm, "end": v(335.67, -63.04) * mm});
            skLineSegment(sketch, "E3339", {"start": v(335.67, -63.04) * mm, "end": v(336.15, -63.01) * mm});
            skLineSegment(sketch, "E3340", {"start": v(336.15, -63.01) * mm, "end": v(336.63, -63) * mm});
            skLineSegment(sketch, "E3341", {"start": v(336.63, -63) * mm, "end": v(337.11, -62.99) * mm});
            skLineSegment(sketch, "E3342", {"start": v(337.11, -62.99) * mm, "end": v(337.6, -63) * mm});
            skLineSegment(sketch, "E3343", {"start": v(337.6, -63) * mm, "end": v(338.08, -63) * mm});
            skLineSegment(sketch, "E3344", {"start": v(338.08, -63) * mm, "end": v(338.53, -63) * mm});
            skLineSegment(sketch, "E3345", {"start": v(338.53, -63) * mm, "end": v(338.98, -63) * mm});
            skLineSegment(sketch, "E3346", {"start": v(338.98, -63) * mm, "end": v(339.42, -63.02) * mm});
            skLineSegment(sketch, "E3347", {"start": v(339.42, -63.02) * mm, "end": v(339.87, -63.05) * mm});
            skLineSegment(sketch, "E3348", {"start": v(339.87, -63.05) * mm, "end": v(340.32, -63.09) * mm});
            skLineSegment(sketch, "E3349", {"start": v(340.32, -63.09) * mm, "end": v(340.76, -63.13) * mm});
            skLineSegment(sketch, "E3350", {"start": v(340.76, -63.13) * mm, "end": v(341.2, -63.2) * mm});
            skLineSegment(sketch, "E3351", {"start": v(341.2, -63.2) * mm, "end": v(341.64, -63.27) * mm});
            skLineSegment(sketch, "E3352", {"start": v(341.64, -63.27) * mm, "end": v(342.08, -63.35) * mm});
            skLineSegment(sketch, "E3353", {"start": v(342.08, -63.35) * mm, "end": v(342.52, -63.44) * mm});
            skLineSegment(sketch, "E3354", {"start": v(342.52, -63.44) * mm, "end": v(342.95, -63.54) * mm});
            skLineSegment(sketch, "E3355", {"start": v(342.95, -63.54) * mm, "end": v(343.38, -63.66) * mm});
            skLineSegment(sketch, "E3356", {"start": v(343.38, -63.66) * mm, "end": v(343.8, -63.78) * mm});
            skLineSegment(sketch, "E3357", {"start": v(343.8, -63.78) * mm, "end": v(344.23, -63.92) * mm});
            skLineSegment(sketch, "E3358", {"start": v(344.23, -63.92) * mm, "end": v(344.65, -64.06) * mm});
            skLineSegment(sketch, "E3359", {"start": v(344.65, -64.06) * mm, "end": v(345.06, -64.22) * mm});
            skLineSegment(sketch, "E3360", {"start": v(345.06, -64.22) * mm, "end": v(345.47, -64.39) * mm});
            skLineSegment(sketch, "E3361", {"start": v(345.47, -64.39) * mm, "end": v(345.88, -64.56) * mm});
            skLineSegment(sketch, "E3362", {"start": v(345.88, -64.56) * mm, "end": v(346.28, -64.75) * mm});
            skLineSegment(sketch, "E3363", {"start": v(346.28, -64.75) * mm, "end": v(346.68, -64.94) * mm});
            skLineSegment(sketch, "E3364", {"start": v(346.68, -64.94) * mm, "end": v(347.08, -65.15) * mm});
            skLineSegment(sketch, "E3365", {"start": v(347.08, -65.15) * mm, "end": v(347.46, -65.37) * mm});
            skLineSegment(sketch, "E3366", {"start": v(347.46, -65.37) * mm, "end": v(347.85, -65.6) * mm});
            skLineSegment(sketch, "E3367", {"start": v(347.85, -65.6) * mm, "end": v(348.23, -65.83) * mm});
            skLineSegment(sketch, "E3368", {"start": v(348.23, -65.83) * mm, "end": v(348.6, -66.07) * mm});
            skLineSegment(sketch, "E3369", {"start": v(348.6, -66.07) * mm, "end": v(348.96, -66.33) * mm});
            skLineSegment(sketch, "E3370", {"start": v(348.96, -66.33) * mm, "end": v(349.32, -66.6) * mm});
            skLineSegment(sketch, "E3371", {"start": v(349.32, -66.6) * mm, "end": v(349.68, -66.87) * mm});
            skLineSegment(sketch, "E3372", {"start": v(349.68, -66.87) * mm, "end": v(350.03, -67.15) * mm});
            skLineSegment(sketch, "E3373", {"start": v(350.03, -67.15) * mm, "end": v(350.37, -67.44) * mm});
            skLineSegment(sketch, "E3374", {"start": v(350.37, -67.44) * mm, "end": v(350.7, -67.74) * mm});
            skLineSegment(sketch, "E3375", {"start": v(350.7, -67.74) * mm, "end": v(351.03, -68.05) * mm});
            skLineSegment(sketch, "E3376", {"start": v(351.03, -68.05) * mm, "end": v(351.28, -68.3) * mm});
            skLineSegment(sketch, "E3377", {"start": v(351.28, -68.3) * mm, "end": v(351.53, -68.57) * mm});
            skLineSegment(sketch, "E3378", {"start": v(351.53, -68.57) * mm, "end": v(351.77, -68.84) * mm});
            skLineSegment(sketch, "E3379", {"start": v(351.77, -68.84) * mm, "end": v(352, -69.11) * mm});
            skLineSegment(sketch, "E3380", {"start": v(352, -69.11) * mm, "end": v(352.23, -69.4) * mm});
            skLineSegment(sketch, "E3381", {"start": v(352.23, -69.4) * mm, "end": v(352.45, -69.68) * mm});
            skLineSegment(sketch, "E3382", {"start": v(352.45, -69.68) * mm, "end": v(352.66, -69.97) * mm});
            skLineSegment(sketch, "E3383", {"start": v(352.66, -69.97) * mm, "end": v(352.86, -70.26) * mm});
            skLineSegment(sketch, "E3384", {"start": v(352.86, -70.26) * mm, "end": v(353.06, -70.56) * mm});
            skLineSegment(sketch, "E3385", {"start": v(353.06, -70.56) * mm, "end": v(353.25, -70.87) * mm});
            skLineSegment(sketch, "E3386", {"start": v(353.25, -70.87) * mm, "end": v(353.43, -71.17) * mm});
            skLineSegment(sketch, "E3387", {"start": v(353.43, -71.17) * mm, "end": v(353.6, -71.49) * mm});
            skLineSegment(sketch, "E3388", {"start": v(353.6, -71.49) * mm, "end": v(353.77, -71.8) * mm});
            skLineSegment(sketch, "E3389", {"start": v(353.77, -71.8) * mm, "end": v(353.92, -72.12) * mm});
            skLineSegment(sketch, "E3390", {"start": v(353.92, -72.12) * mm, "end": v(354.07, -72.45) * mm});
            skLineSegment(sketch, "E3391", {"start": v(354.07, -72.45) * mm, "end": v(354.21, -72.78) * mm});
            skLineSegment(sketch, "E3392", {"start": v(354.21, -72.78) * mm, "end": v(354.35, -73.1) * mm});
            skLineSegment(sketch, "E3393", {"start": v(354.35, -73.1) * mm, "end": v(354.47, -73.44) * mm});
            skLineSegment(sketch, "E3394", {"start": v(354.47, -73.44) * mm, "end": v(354.59, -73.78) * mm});
            skLineSegment(sketch, "E3395", {"start": v(354.59, -73.78) * mm, "end": v(354.7, -74.12) * mm});
            skLineSegment(sketch, "E3396", {"start": v(354.7, -74.12) * mm, "end": v(354.8, -74.46) * mm});
            skLineSegment(sketch, "E3397", {"start": v(354.8, -74.46) * mm, "end": v(354.89, -74.8) * mm});
            skLineSegment(sketch, "E3398", {"start": v(354.89, -74.8) * mm, "end": v(354.97, -75.15) * mm});
            skLineSegment(sketch, "E3399", {"start": v(354.97, -75.15) * mm, "end": v(355.04, -75.5) * mm});
            skLineSegment(sketch, "E3400", {"start": v(355.04, -75.5) * mm, "end": v(355.1, -75.86) * mm});
            skLineSegment(sketch, "E3401", {"start": v(355.1, -75.86) * mm, "end": v(355.16, -76.21) * mm});
            skLineSegment(sketch, "E3402", {"start": v(355.16, -76.21) * mm, "end": v(355.21, -76.57) * mm});
            skLineSegment(sketch, "E3403", {"start": v(355.21, -76.57) * mm, "end": v(355.25, -76.92) * mm});
            skLineSegment(sketch, "E3404", {"start": v(355.25, -76.92) * mm, "end": v(355.28, -77.28) * mm});
            skLineSegment(sketch, "E3405", {"start": v(355.28, -77.28) * mm, "end": v(355.3, -77.64) * mm});
            skLineSegment(sketch, "E3406", {"start": v(355.3, -77.64) * mm, "end": v(355.31, -78) * mm});
            skLineSegment(sketch, "E3407", {"start": v(355.31, -78) * mm, "end": v(355.31, -78.37) * mm});
            skLineSegment(sketch, "E3408", {"start": v(354.85, -55.11) * mm, "end": v(319.85, -55.11) * mm});
            skLineSegment(sketch, "E3409", {"start": v(319.85, -55.11) * mm, "end": v(319.85, -33.36) * mm});
            skLineSegment(sketch, "E3410", {"start": v(336.57, -55.11) * mm, "end": v(336.57, -34.92) * mm});
            skLineSegment(sketch, "E3411", {"start": v(341.76, -25.66) * mm, "end": v(341.76, -1.53) * mm});
            skLineSegment(sketch, "E3412", {"start": v(355.26, 17.74) * mm, "end": v(355.26, 17.22) * mm});
            skLineSegment(sketch, "E3413", {"start": v(355.26, 17.22) * mm, "end": v(355.23, 16.7) * mm});
            skLineSegment(sketch, "E3414", {"start": v(355.23, 16.7) * mm, "end": v(355.18, 16.2) * mm});
            skLineSegment(sketch, "E3415", {"start": v(355.18, 16.2) * mm, "end": v(355.1, 15.7) * mm});
            skLineSegment(sketch, "E3416", {"start": v(355.1, 15.7) * mm, "end": v(355, 15.2) * mm});
            skLineSegment(sketch, "E3417", {"start": v(355, 15.2) * mm, "end": v(354.87, 14.7) * mm});
            skLineSegment(sketch, "E3418", {"start": v(354.87, 14.7) * mm, "end": v(354.72, 14.22) * mm});
            skLineSegment(sketch, "E3419", {"start": v(354.72, 14.22) * mm, "end": v(354.55, 13.75) * mm});
            skLineSegment(sketch, "E3420", {"start": v(354.55, 13.75) * mm, "end": v(354.34, 13.28) * mm});
            skLineSegment(sketch, "E3421", {"start": v(354.34, 13.28) * mm, "end": v(354.12, 12.82) * mm});
            skLineSegment(sketch, "E3422", {"start": v(354.12, 12.82) * mm, "end": v(353.87, 12.38) * mm});
            skLineSegment(sketch, "E3423", {"start": v(353.87, 12.38) * mm, "end": v(353.6, 11.95) * mm});
            skLineSegment(sketch, "E3424", {"start": v(353.6, 11.95) * mm, "end": v(353.31, 11.53) * mm});
            skLineSegment(sketch, "E3425", {"start": v(353.31, 11.53) * mm, "end": v(353, 11.13) * mm});
            skLineSegment(sketch, "E3426", {"start": v(353, 11.13) * mm, "end": v(352.66, 10.74) * mm});
            skLineSegment(sketch, "E3427", {"start": v(352.66, 10.74) * mm, "end": v(352.3, 10.37) * mm});
            skLineSegment(sketch, "E3428", {"start": v(352.3, 10.37) * mm, "end": v(352.05, 10.1) * mm});
            skLineSegment(sketch, "E3429", {"start": v(352.05, 10.1) * mm, "end": v(351.79, 9.86) * mm});
            skLineSegment(sketch, "E3430", {"start": v(351.79, 9.86) * mm, "end": v(351.52, 9.61) * mm});
            skLineSegment(sketch, "E3431", {"start": v(351.52, 9.61) * mm, "end": v(351.25, 9.38) * mm});
            skLineSegment(sketch, "E3432", {"start": v(351.25, 9.38) * mm, "end": v(350.97, 9.15) * mm});
            skLineSegment(sketch, "E3433", {"start": v(350.97, 9.15) * mm, "end": v(350.68, 8.93) * mm});
            skLineSegment(sketch, "E3434", {"start": v(350.68, 8.93) * mm, "end": v(350.4, 8.72) * mm});
            skLineSegment(sketch, "E3435", {"start": v(350.4, 8.72) * mm, "end": v(350.1, 8.51) * mm});
            skLineSegment(sketch, "E3436", {"start": v(350.1, 8.51) * mm, "end": v(349.8, 8.32) * mm});
            skLineSegment(sketch, "E3437", {"start": v(349.8, 8.32) * mm, "end": v(349.49, 8.13) * mm});
            skLineSegment(sketch, "E3438", {"start": v(349.49, 8.13) * mm, "end": v(349.18, 7.95) * mm});
            skLineSegment(sketch, "E3439", {"start": v(349.18, 7.95) * mm, "end": v(348.87, 7.78) * mm});
            skLineSegment(sketch, "E3440", {"start": v(348.87, 7.78) * mm, "end": v(348.55, 7.61) * mm});
            skLineSegment(sketch, "E3441", {"start": v(348.55, 7.61) * mm, "end": v(348.23, 7.46) * mm});
            skLineSegment(sketch, "E3442", {"start": v(348.23, 7.46) * mm, "end": v(347.9, 7.31) * mm});
            skLineSegment(sketch, "E3443", {"start": v(347.9, 7.31) * mm, "end": v(347.57, 7.17) * mm});
            skLineSegment(sketch, "E3444", {"start": v(347.57, 7.17) * mm, "end": v(347.24, 7.04) * mm});
            skLineSegment(sketch, "E3445", {"start": v(347.24, 7.04) * mm, "end": v(346.9, 6.92) * mm});
            skLineSegment(sketch, "E3446", {"start": v(346.9, 6.92) * mm, "end": v(346.56, 6.8) * mm});
            skLineSegment(sketch, "E3447", {"start": v(346.56, 6.8) * mm, "end": v(346.22, 6.7) * mm});
            skLineSegment(sketch, "E3448", {"start": v(346.22, 6.7) * mm, "end": v(345.87, 6.6) * mm});
            skLineSegment(sketch, "E3449", {"start": v(345.87, 6.6) * mm, "end": v(345.52, 6.52) * mm});
            skLineSegment(sketch, "E3450", {"start": v(345.52, 6.52) * mm, "end": v(345.17, 6.45) * mm});
            skLineSegment(sketch, "E3451", {"start": v(345.17, 6.45) * mm, "end": v(344.82, 6.38) * mm});
            skLineSegment(sketch, "E3452", {"start": v(344.82, 6.38) * mm, "end": v(344.47, 6.32) * mm});
            skLineSegment(sketch, "E3453", {"start": v(344.47, 6.32) * mm, "end": v(344.11, 6.27) * mm});
            skLineSegment(sketch, "E3454", {"start": v(344.11, 6.27) * mm, "end": v(343.75, 6.23) * mm});
            skLineSegment(sketch, "E3455", {"start": v(343.75, 6.23) * mm, "end": v(343.4, 6.2) * mm});
            skLineSegment(sketch, "E3456", {"start": v(343.4, 6.2) * mm, "end": v(343.03, 6.18) * mm});
            skLineSegment(sketch, "E3457", {"start": v(343.03, 6.18) * mm, "end": v(342.67, 6.17) * mm});
            skLineSegment(sketch, "E3458", {"start": v(342.67, 6.17) * mm, "end": v(342.3, 6.16) * mm});
            skLineSegment(sketch, "E3459", {"start": v(342.3, 6.16) * mm, "end": v(341.94, 6.17) * mm});
            skLineSegment(sketch, "E3460", {"start": v(341.94, 6.17) * mm, "end": v(341.58, 6.16) * mm});
            skLineSegment(sketch, "E3461", {"start": v(341.58, 6.16) * mm, "end": v(341.22, 6.15) * mm});
            skLineSegment(sketch, "E3462", {"start": v(341.22, 6.15) * mm, "end": v(340.86, 6.15) * mm});
            skLineSegment(sketch, "E3463", {"start": v(340.86, 6.15) * mm, "end": v(340.5, 6.17) * mm});
            skLineSegment(sketch, "E3464", {"start": v(340.5, 6.17) * mm, "end": v(340.14, 6.19) * mm});
            skLineSegment(sketch, "E3465", {"start": v(340.14, 6.19) * mm, "end": v(339.78, 6.22) * mm});
            skLineSegment(sketch, "E3466", {"start": v(339.78, 6.22) * mm, "end": v(339.43, 6.26) * mm});
            skLineSegment(sketch, "E3467", {"start": v(339.43, 6.26) * mm, "end": v(339.07, 6.3) * mm});
            skLineSegment(sketch, "E3468", {"start": v(339.07, 6.3) * mm, "end": v(338.72, 6.36) * mm});
            skLineSegment(sketch, "E3469", {"start": v(338.72, 6.36) * mm, "end": v(338.36, 6.43) * mm});
            skLineSegment(sketch, "E3470", {"start": v(338.36, 6.43) * mm, "end": v(338.01, 6.5) * mm});
            skLineSegment(sketch, "E3471", {"start": v(338.01, 6.5) * mm, "end": v(337.67, 6.59) * mm});
            skLineSegment(sketch, "E3472", {"start": v(337.67, 6.59) * mm, "end": v(337.32, 6.68) * mm});
            skLineSegment(sketch, "E3473", {"start": v(337.32, 6.68) * mm, "end": v(336.98, 6.78) * mm});
            skLineSegment(sketch, "E3474", {"start": v(336.98, 6.78) * mm, "end": v(336.64, 6.88) * mm});
            skLineSegment(sketch, "E3475", {"start": v(336.64, 6.88) * mm, "end": v(336.3, 7) * mm});
            skLineSegment(sketch, "E3476", {"start": v(336.3, 7) * mm, "end": v(335.96, 7.12) * mm});
            skLineSegment(sketch, "E3477", {"start": v(335.96, 7.12) * mm, "end": v(335.63, 7.25) * mm});
            skLineSegment(sketch, "E3478", {"start": v(335.63, 7.25) * mm, "end": v(335.3, 7.4) * mm});
            skLineSegment(sketch, "E3479", {"start": v(335.3, 7.4) * mm, "end": v(334.98, 7.54) * mm});
            skLineSegment(sketch, "E3480", {"start": v(334.98, 7.54) * mm, "end": v(334.66, 7.7) * mm});
            skLineSegment(sketch, "E3481", {"start": v(334.66, 7.7) * mm, "end": v(334.34, 7.86) * mm});
            skLineSegment(sketch, "E3482", {"start": v(334.34, 7.86) * mm, "end": v(334.02, 8.03) * mm});
            skLineSegment(sketch, "E3483", {"start": v(334.02, 8.03) * mm, "end": v(333.71, 8.21) * mm});
            skLineSegment(sketch, "E3484", {"start": v(333.71, 8.21) * mm, "end": v(333.4, 8.4) * mm});
            skLineSegment(sketch, "E3485", {"start": v(333.4, 8.4) * mm, "end": v(333.1, 8.6) * mm});
            skLineSegment(sketch, "E3486", {"start": v(333.1, 8.6) * mm, "end": v(332.8, 8.8) * mm});
            skLineSegment(sketch, "E3487", {"start": v(332.8, 8.8) * mm, "end": v(332.52, 9) * mm});
            skLineSegment(sketch, "E3488", {"start": v(332.52, 9) * mm, "end": v(332.23, 9.22) * mm});
            skLineSegment(sketch, "E3489", {"start": v(332.23, 9.22) * mm, "end": v(331.95, 9.45) * mm});
            skLineSegment(sketch, "E3490", {"start": v(331.95, 9.45) * mm, "end": v(331.67, 9.68) * mm});
            skLineSegment(sketch, "E3491", {"start": v(331.67, 9.68) * mm, "end": v(331.4, 9.92) * mm});
            skLineSegment(sketch, "E3492", {"start": v(331.4, 9.92) * mm, "end": v(331.03, 10.32) * mm});
            skLineSegment(sketch, "E3493", {"start": v(331.03, 10.32) * mm, "end": v(330.7, 10.74) * mm});
            skLineSegment(sketch, "E3494", {"start": v(330.7, 10.74) * mm, "end": v(330.37, 11.17) * mm});
            skLineSegment(sketch, "E3495", {"start": v(330.37, 11.17) * mm, "end": v(330.07, 11.62) * mm});
            skLineSegment(sketch, "E3496", {"start": v(330.07, 11.62) * mm, "end": v(329.8, 12.08) * mm});
            skLineSegment(sketch, "E3497", {"start": v(329.8, 12.08) * mm, "end": v(329.53, 12.55) * mm});
            skLineSegment(sketch, "E3498", {"start": v(329.53, 12.55) * mm, "end": v(329.3, 13.03) * mm});
            skLineSegment(sketch, "E3499", {"start": v(329.3, 13.03) * mm, "end": v(329.1, 13.53) * mm});
            skLineSegment(sketch, "E3500", {"start": v(329.1, 13.53) * mm, "end": v(328.9, 14.03) * mm});
            skLineSegment(sketch, "E3501", {"start": v(328.9, 14.03) * mm, "end": v(328.74, 14.54) * mm});
            skLineSegment(sketch, "E3502", {"start": v(328.74, 14.54) * mm, "end": v(328.6, 15.06) * mm});
            skLineSegment(sketch, "E3503", {"start": v(328.6, 15.06) * mm, "end": v(328.49, 15.59) * mm});
            skLineSegment(sketch, "E3504", {"start": v(328.49, 15.59) * mm, "end": v(328.4, 16.12) * mm});
            skLineSegment(sketch, "E3505", {"start": v(328.4, 16.12) * mm, "end": v(328.34, 16.65) * mm});
            skLineSegment(sketch, "E3506", {"start": v(328.34, 16.65) * mm, "end": v(328.3, 17.2) * mm});
            skLineSegment(sketch, "E3507", {"start": v(328.3, 17.2) * mm, "end": v(328.29, 17.74) * mm});
            skLineSegment(sketch, "E3508", {"start": v(328.29, 17.74) * mm, "end": v(328.31, 18.26) * mm});
            skLineSegment(sketch, "E3509", {"start": v(328.31, 18.26) * mm, "end": v(328.36, 18.78) * mm});
            skLineSegment(sketch, "E3510", {"start": v(328.36, 18.78) * mm, "end": v(328.44, 19.3) * mm});
            skLineSegment(sketch, "E3511", {"start": v(328.44, 19.3) * mm, "end": v(328.55, 19.8) * mm});
            skLineSegment(sketch, "E3512", {"start": v(328.55, 19.8) * mm, "end": v(328.68, 20.31) * mm});
            skLineSegment(sketch, "E3513", {"start": v(328.68, 20.31) * mm, "end": v(328.84, 20.8) * mm});
            skLineSegment(sketch, "E3514", {"start": v(328.84, 20.8) * mm, "end": v(329.03, 21.3) * mm});
            skLineSegment(sketch, "E3515", {"start": v(329.03, 21.3) * mm, "end": v(329.24, 21.77) * mm});
            skLineSegment(sketch, "E3516", {"start": v(329.24, 21.77) * mm, "end": v(329.47, 22.23) * mm});
            skLineSegment(sketch, "E3517", {"start": v(329.47, 22.23) * mm, "end": v(329.73, 22.68) * mm});
            skLineSegment(sketch, "E3518", {"start": v(329.73, 22.68) * mm, "end": v(330.01, 23.12) * mm});
            skLineSegment(sketch, "E3519", {"start": v(330.01, 23.12) * mm, "end": v(330.31, 23.54) * mm});
            skLineSegment(sketch, "E3520", {"start": v(330.31, 23.54) * mm, "end": v(330.64, 23.94) * mm});
            skLineSegment(sketch, "E3521", {"start": v(330.64, 23.94) * mm, "end": v(330.99, 24.33) * mm});
            skLineSegment(sketch, "E3522", {"start": v(330.99, 24.33) * mm, "end": v(331.36, 24.7) * mm});
            skLineSegment(sketch, "E3523", {"start": v(331.36, 24.7) * mm, "end": v(331.75, 25.06) * mm});
            skLineSegment(sketch, "E3524", {"start": v(331.75, 25.06) * mm, "end": v(332, 25.3) * mm});
            skLineSegment(sketch, "E3525", {"start": v(332, 25.3) * mm, "end": v(332.27, 25.53) * mm});
            skLineSegment(sketch, "E3526", {"start": v(332.27, 25.53) * mm, "end": v(332.54, 25.76) * mm});
            skLineSegment(sketch, "E3527", {"start": v(332.54, 25.76) * mm, "end": v(332.81, 25.97) * mm});
            skLineSegment(sketch, "E3528", {"start": v(332.81, 25.97) * mm, "end": v(333.1, 26.19) * mm});
            skLineSegment(sketch, "E3529", {"start": v(333.1, 26.19) * mm, "end": v(333.38, 26.39) * mm});
            skLineSegment(sketch, "E3530", {"start": v(333.38, 26.39) * mm, "end": v(333.67, 26.58) * mm});
            skLineSegment(sketch, "E3531", {"start": v(333.67, 26.58) * mm, "end": v(333.96, 26.77) * mm});
            skLineSegment(sketch, "E3532", {"start": v(333.96, 26.77) * mm, "end": v(334.26, 26.95) * mm});
            skLineSegment(sketch, "E3533", {"start": v(334.26, 26.95) * mm, "end": v(334.56, 27.12) * mm});
            skLineSegment(sketch, "E3534", {"start": v(334.56, 27.12) * mm, "end": v(334.87, 27.28) * mm});
            skLineSegment(sketch, "E3535", {"start": v(334.87, 27.28) * mm, "end": v(335.18, 27.44) * mm});
            skLineSegment(sketch, "E3536", {"start": v(335.18, 27.44) * mm, "end": v(335.5, 27.59) * mm});
            skLineSegment(sketch, "E3537", {"start": v(335.5, 27.59) * mm, "end": v(335.81, 27.73) * mm});
            skLineSegment(sketch, "E3538", {"start": v(335.81, 27.73) * mm, "end": v(336.13, 27.86) * mm});
            skLineSegment(sketch, "E3539", {"start": v(336.13, 27.86) * mm, "end": v(336.46, 27.98) * mm});
            skLineSegment(sketch, "E3540", {"start": v(336.46, 27.98) * mm, "end": v(336.79, 28.1) * mm});
            skLineSegment(sketch, "E3541", {"start": v(336.79, 28.1) * mm, "end": v(337.12, 28.2) * mm});
            skLineSegment(sketch, "E3542", {"start": v(337.12, 28.2) * mm, "end": v(337.45, 28.3) * mm});
            skLineSegment(sketch, "E3543", {"start": v(337.45, 28.3) * mm, "end": v(337.78, 28.39) * mm});
            skLineSegment(sketch, "E3544", {"start": v(337.78, 28.39) * mm, "end": v(338.12, 28.47) * mm});
            skLineSegment(sketch, "E3545", {"start": v(338.12, 28.47) * mm, "end": v(338.46, 28.54) * mm});
            skLineSegment(sketch, "E3546", {"start": v(338.46, 28.54) * mm, "end": v(338.8, 28.6) * mm});
            skLineSegment(sketch, "E3547", {"start": v(338.8, 28.6) * mm, "end": v(339.15, 28.66) * mm});
            skLineSegment(sketch, "E3548", {"start": v(339.15, 28.66) * mm, "end": v(339.5, 28.7) * mm});
            skLineSegment(sketch, "E3549", {"start": v(339.5, 28.7) * mm, "end": v(339.84, 28.74) * mm});
            skLineSegment(sketch, "E3550", {"start": v(339.84, 28.74) * mm, "end": v(340.19, 28.77) * mm});
            skLineSegment(sketch, "E3551", {"start": v(340.19, 28.77) * mm, "end": v(340.54, 28.79) * mm});
            skLineSegment(sketch, "E3552", {"start": v(340.54, 28.79) * mm, "end": v(340.89, 28.8) * mm});
            skLineSegment(sketch, "E3553", {"start": v(340.89, 28.8) * mm, "end": v(341.24, 28.8) * mm});
            skLineSegment(sketch, "E3554", {"start": v(341.24, 28.8) * mm, "end": v(341.6, 28.79) * mm});
            skLineSegment(sketch, "E3555", {"start": v(341.6, 28.79) * mm, "end": v(341.94, 28.77) * mm});
            skLineSegment(sketch, "E3556", {"start": v(341.94, 28.77) * mm, "end": v(342.3, 28.78) * mm});
            skLineSegment(sketch, "E3557", {"start": v(342.3, 28.78) * mm, "end": v(342.64, 28.79) * mm});
            skLineSegment(sketch, "E3558", {"start": v(342.64, 28.79) * mm, "end": v(343, 28.78) * mm});
            skLineSegment(sketch, "E3559", {"start": v(343, 28.78) * mm, "end": v(343.34, 28.76) * mm});
            skLineSegment(sketch, "E3560", {"start": v(343.34, 28.76) * mm, "end": v(343.69, 28.74) * mm});
            skLineSegment(sketch, "E3561", {"start": v(343.69, 28.74) * mm, "end": v(344.03, 28.7) * mm});
            skLineSegment(sketch, "E3562", {"start": v(344.03, 28.7) * mm, "end": v(344.38, 28.67) * mm});
            skLineSegment(sketch, "E3563", {"start": v(344.38, 28.67) * mm, "end": v(344.72, 28.62) * mm});
            skLineSegment(sketch, "E3564", {"start": v(344.72, 28.62) * mm, "end": v(345.06, 28.56) * mm});
            skLineSegment(sketch, "E3565", {"start": v(345.06, 28.56) * mm, "end": v(345.4, 28.5) * mm});
            skLineSegment(sketch, "E3566", {"start": v(345.4, 28.5) * mm, "end": v(345.73, 28.42) * mm});
            skLineSegment(sketch, "E3567", {"start": v(345.73, 28.42) * mm, "end": v(346.07, 28.33) * mm});
            skLineSegment(sketch, "E3568", {"start": v(346.07, 28.33) * mm, "end": v(346.4, 28.24) * mm});
            skLineSegment(sketch, "E3569", {"start": v(346.4, 28.24) * mm, "end": v(346.73, 28.14) * mm});
            skLineSegment(sketch, "E3570", {"start": v(346.73, 28.14) * mm, "end": v(347.06, 28.04) * mm});
            skLineSegment(sketch, "E3571", {"start": v(347.06, 28.04) * mm, "end": v(347.38, 27.92) * mm});
            skLineSegment(sketch, "E3572", {"start": v(347.38, 27.92) * mm, "end": v(347.7, 27.8) * mm});
            skLineSegment(sketch, "E3573", {"start": v(347.7, 27.8) * mm, "end": v(348.02, 27.66) * mm});
            skLineSegment(sketch, "E3574", {"start": v(348.02, 27.66) * mm, "end": v(348.34, 27.52) * mm});
            skLineSegment(sketch, "E3575", {"start": v(348.34, 27.52) * mm, "end": v(348.65, 27.37) * mm});
            skLineSegment(sketch, "E3576", {"start": v(348.65, 27.37) * mm, "end": v(348.96, 27.22) * mm});
            skLineSegment(sketch, "E3577", {"start": v(348.96, 27.22) * mm, "end": v(349.26, 27.06) * mm});
            skLineSegment(sketch, "E3578", {"start": v(349.26, 27.06) * mm, "end": v(349.56, 26.88) * mm});
            skLineSegment(sketch, "E3579", {"start": v(349.56, 26.88) * mm, "end": v(349.86, 26.7) * mm});
            skLineSegment(sketch, "E3580", {"start": v(349.86, 26.7) * mm, "end": v(350.15, 26.52) * mm});
            skLineSegment(sketch, "E3581", {"start": v(350.15, 26.52) * mm, "end": v(350.44, 26.33) * mm});
            skLineSegment(sketch, "E3582", {"start": v(350.44, 26.33) * mm, "end": v(350.72, 26.12) * mm});
            skLineSegment(sketch, "E3583", {"start": v(350.72, 26.12) * mm, "end": v(351, 25.92) * mm});
            skLineSegment(sketch, "E3584", {"start": v(351, 25.92) * mm, "end": v(351.27, 25.7) * mm});
            skLineSegment(sketch, "E3585", {"start": v(351.27, 25.7) * mm, "end": v(351.54, 25.48) * mm});
            skLineSegment(sketch, "E3586", {"start": v(351.54, 25.48) * mm, "end": v(351.8, 25.25) * mm});
            skLineSegment(sketch, "E3587", {"start": v(351.8, 25.25) * mm, "end": v(352.06, 25) * mm});
            skLineSegment(sketch, "E3588", {"start": v(352.06, 25) * mm, "end": v(352.42, 24.65) * mm});
            skLineSegment(sketch, "E3589", {"start": v(352.42, 24.65) * mm, "end": v(352.77, 24.27) * mm});
            skLineSegment(sketch, "E3590", {"start": v(352.77, 24.27) * mm, "end": v(353.1, 23.88) * mm});
            skLineSegment(sketch, "E3591", {"start": v(353.1, 23.88) * mm, "end": v(353.4, 23.47) * mm});
            skLineSegment(sketch, "E3592", {"start": v(353.4, 23.47) * mm, "end": v(353.69, 23.05) * mm});
            skLineSegment(sketch, "E3593", {"start": v(353.69, 23.05) * mm, "end": v(353.95, 22.61) * mm});
            skLineSegment(sketch, "E3594", {"start": v(353.95, 22.61) * mm, "end": v(354.19, 22.16) * mm});
            skLineSegment(sketch, "E3595", {"start": v(354.19, 22.16) * mm, "end": v(354.4, 21.7) * mm});
            skLineSegment(sketch, "E3596", {"start": v(354.4, 21.7) * mm, "end": v(354.6, 21.23) * mm});
            skLineSegment(sketch, "E3597", {"start": v(354.6, 21.23) * mm, "end": v(354.77, 20.75) * mm});
            skLineSegment(sketch, "E3598", {"start": v(354.77, 20.75) * mm, "end": v(354.91, 20.27) * mm});
            skLineSegment(sketch, "E3599", {"start": v(354.91, 20.27) * mm, "end": v(355.03, 19.77) * mm});
            skLineSegment(sketch, "E3600", {"start": v(355.03, 19.77) * mm, "end": v(355.13, 19.27) * mm});
            skLineSegment(sketch, "E3601", {"start": v(355.13, 19.27) * mm, "end": v(355.2, 18.76) * mm});
            skLineSegment(sketch, "E3602", {"start": v(355.2, 18.76) * mm, "end": v(355.24, 18.25) * mm});
            skLineSegment(sketch, "E3603", {"start": v(355.24, 18.25) * mm, "end": v(355.26, 17.74) * mm});
            skLineSegment(sketch, "E3604", {"start": v(354.84, 55.67) * mm, "end": v(328.7, 55.67) * mm});
            skLineSegment(sketch, "E3605", {"start": v(345.4, 55.67) * mm, "end": v(345.88, 55.65) * mm});
            skLineSegment(sketch, "E3606", {"start": v(345.88, 55.65) * mm, "end": v(346.36, 55.61) * mm});
            skLineSegment(sketch, "E3607", {"start": v(346.36, 55.61) * mm, "end": v(346.83, 55.54) * mm});
            skLineSegment(sketch, "E3608", {"start": v(346.83, 55.54) * mm, "end": v(347.29, 55.45) * mm});
            skLineSegment(sketch, "E3609", {"start": v(347.29, 55.45) * mm, "end": v(347.75, 55.34) * mm});
            skLineSegment(sketch, "E3610", {"start": v(347.75, 55.34) * mm, "end": v(348.2, 55.2) * mm});
            skLineSegment(sketch, "E3611", {"start": v(348.2, 55.2) * mm, "end": v(348.64, 55.05) * mm});
            skLineSegment(sketch, "E3612", {"start": v(348.64, 55.05) * mm, "end": v(349.08, 54.87) * mm});
            skLineSegment(sketch, "E3613", {"start": v(349.08, 54.87) * mm, "end": v(349.5, 54.67) * mm});
            skLineSegment(sketch, "E3614", {"start": v(349.5, 54.67) * mm, "end": v(349.92, 54.45) * mm});
            skLineSegment(sketch, "E3615", {"start": v(349.92, 54.45) * mm, "end": v(350.33, 54.2) * mm});
            skLineSegment(sketch, "E3616", {"start": v(350.33, 54.2) * mm, "end": v(350.72, 53.94) * mm});
            skLineSegment(sketch, "E3617", {"start": v(350.72, 53.94) * mm, "end": v(351.1, 53.66) * mm});
            skLineSegment(sketch, "E3618", {"start": v(351.1, 53.66) * mm, "end": v(351.46, 53.36) * mm});
            skLineSegment(sketch, "E3619", {"start": v(351.46, 53.36) * mm, "end": v(351.82, 53.04) * mm});
            skLineSegment(sketch, "E3620", {"start": v(351.82, 53.04) * mm, "end": v(352.15, 52.7) * mm});
            skLineSegment(sketch, "E3621", {"start": v(352.15, 52.7) * mm, "end": v(352.5, 52.36) * mm});
            skLineSegment(sketch, "E3622", {"start": v(352.5, 52.36) * mm, "end": v(352.81, 52) * mm});
            skLineSegment(sketch, "E3623", {"start": v(352.81, 52) * mm, "end": v(353.1, 51.62) * mm});
            skLineSegment(sketch, "E3624", {"start": v(353.1, 51.62) * mm, "end": v(353.39, 51.24) * mm});
            skLineSegment(sketch, "E3625", {"start": v(353.39, 51.24) * mm, "end": v(353.65, 50.84) * mm});
            skLineSegment(sketch, "E3626", {"start": v(353.65, 50.84) * mm, "end": v(353.89, 50.43) * mm});
            skLineSegment(sketch, "E3627", {"start": v(353.89, 50.43) * mm, "end": v(354.1, 50) * mm});
            skLineSegment(sketch, "E3628", {"start": v(354.1, 50) * mm, "end": v(354.3, 49.57) * mm});
            skLineSegment(sketch, "E3629", {"start": v(354.3, 49.57) * mm, "end": v(354.48, 49.13) * mm});
            skLineSegment(sketch, "E3630", {"start": v(354.48, 49.13) * mm, "end": v(354.63, 48.68) * mm});
            skLineSegment(sketch, "E3631", {"start": v(354.63, 48.68) * mm, "end": v(354.77, 48.22) * mm});
            skLineSegment(sketch, "E3632", {"start": v(354.77, 48.22) * mm, "end": v(354.87, 47.76) * mm});
            skLineSegment(sketch, "E3633", {"start": v(354.87, 47.76) * mm, "end": v(354.96, 47.3) * mm});
            skLineSegment(sketch, "E3634", {"start": v(354.96, 47.3) * mm, "end": v(355.02, 46.82) * mm});
            skLineSegment(sketch, "E3635", {"start": v(355.02, 46.82) * mm, "end": v(355.06, 46.34) * mm});
            skLineSegment(sketch, "E3636", {"start": v(355.06, 46.34) * mm, "end": v(355.08, 45.86) * mm});
            skLineSegment(sketch, "E3637", {"start": v(355.08, 45.86) * mm, "end": v(355.11, 45.38) * mm});
            skLineSegment(sketch, "E3638", {"start": v(355.11, 45.38) * mm, "end": v(355.13, 44.91) * mm});
            skLineSegment(sketch, "E3639", {"start": v(355.13, 44.91) * mm, "end": v(355.12, 44.45) * mm});
            skLineSegment(sketch, "E3640", {"start": v(355.12, 44.45) * mm, "end": v(355.08, 43.98) * mm});
            skLineSegment(sketch, "E3641", {"start": v(355.08, 43.98) * mm, "end": v(355.03, 43.52) * mm});
            skLineSegment(sketch, "E3642", {"start": v(355.03, 43.52) * mm, "end": v(354.95, 43.06) * mm});
            skLineSegment(sketch, "E3643", {"start": v(354.95, 43.06) * mm, "end": v(354.84, 42.6) * mm});
            skLineSegment(sketch, "E3644", {"start": v(354.84, 42.6) * mm, "end": v(354.72, 42.15) * mm});
            skLineSegment(sketch, "E3645", {"start": v(354.72, 42.15) * mm, "end": v(354.57, 41.71) * mm});
            skLineSegment(sketch, "E3646", {"start": v(354.57, 41.71) * mm, "end": v(354.4, 41.28) * mm});
            skLineSegment(sketch, "E3647", {"start": v(354.4, 41.28) * mm, "end": v(354.22, 40.85) * mm});
            skLineSegment(sketch, "E3648", {"start": v(354.22, 40.85) * mm, "end": v(354, 40.43) * mm});
            skLineSegment(sketch, "E3649", {"start": v(354, 40.43) * mm, "end": v(353.77, 40.03) * mm});
            skLineSegment(sketch, "E3650", {"start": v(353.77, 40.03) * mm, "end": v(353.52, 39.63) * mm});
            skLineSegment(sketch, "E3651", {"start": v(353.52, 39.63) * mm, "end": v(353.25, 39.25) * mm});
            skLineSegment(sketch, "E3652", {"start": v(353.25, 39.25) * mm, "end": v(352.96, 38.88) * mm});
            skLineSegment(sketch, "E3653", {"start": v(352.96, 38.88) * mm, "end": v(352.64, 38.6) * mm});
            skLineSegment(sketch, "E3654", {"start": v(352.64, 38.6) * mm, "end": v(352.31, 38.33) * mm});
            skLineSegment(sketch, "E3655", {"start": v(352.31, 38.33) * mm, "end": v(351.97, 38.08) * mm});
            skLineSegment(sketch, "E3656", {"start": v(351.97, 38.08) * mm, "end": v(351.62, 37.86) * mm});
            skLineSegment(sketch, "E3657", {"start": v(351.62, 37.86) * mm, "end": v(351.26, 37.65) * mm});
            skLineSegment(sketch, "E3658", {"start": v(351.26, 37.65) * mm, "end": v(350.88, 37.46) * mm});
            skLineSegment(sketch, "E3659", {"start": v(350.88, 37.46) * mm, "end": v(350.5, 37.29) * mm});
            skLineSegment(sketch, "E3660", {"start": v(350.5, 37.29) * mm, "end": v(350.11, 37.14) * mm});
            skLineSegment(sketch, "E3661", {"start": v(350.11, 37.14) * mm, "end": v(349.72, 37) * mm});
            skLineSegment(sketch, "E3662", {"start": v(349.72, 37) * mm, "end": v(349.31, 36.9) * mm});
            skLineSegment(sketch, "E3663", {"start": v(349.31, 36.9) * mm, "end": v(348.9, 36.8) * mm});
            skLineSegment(sketch, "E3664", {"start": v(348.9, 36.8) * mm, "end": v(348.5, 36.74) * mm});
            skLineSegment(sketch, "E3665", {"start": v(348.5, 36.74) * mm, "end": v(348.08, 36.69) * mm});
            skLineSegment(sketch, "E3666", {"start": v(348.08, 36.69) * mm, "end": v(347.66, 36.66) * mm});
            skLineSegment(sketch, "E3667", {"start": v(347.66, 36.66) * mm, "end": v(347.23, 36.66) * mm});
            skLineSegment(sketch, "E3668", {"start": v(347.23, 36.66) * mm, "end": v(346.8, 36.67) * mm});
            skLineSegment(sketch, "E3669", {"start": v(346.8, 36.67) * mm, "end": v(328.7, 36.67) * mm});
            skLineSegment(sketch, "E3670", {"start": v(354.7, 72) * mm, "end": v(354.82, 71.78) * mm});
            skLineSegment(sketch, "E3671", {"start": v(354.82, 71.78) * mm, "end": v(354.93, 71.54) * mm});
            skLineSegment(sketch, "E3672", {"start": v(354.93, 71.54) * mm, "end": v(355.02, 71.3) * mm});
            skLineSegment(sketch, "E3673", {"start": v(355.02, 71.3) * mm, "end": v(355.1, 71.05) * mm});
            skLineSegment(sketch, "E3674", {"start": v(355.1, 71.05) * mm, "end": v(355.15, 70.8) * mm});
            skLineSegment(sketch, "E3675", {"start": v(355.15, 70.8) * mm, "end": v(355.19, 70.53) * mm});
            skLineSegment(sketch, "E3676", {"start": v(355.19, 70.53) * mm, "end": v(355.2, 70.27) * mm});
            skLineSegment(sketch, "E3677", {"start": v(355.2, 70.27) * mm, "end": v(355.2, 70.01) * mm});
            skLineSegment(sketch, "E3678", {"start": v(355.2, 70.01) * mm, "end": v(355.2, 69.82) * mm});
            skLineSegment(sketch, "E3679", {"start": v(355.2, 69.82) * mm, "end": v(355.2, 69.63) * mm});
            skLineSegment(sketch, "E3680", {"start": v(355.2, 69.63) * mm, "end": v(355.17, 69.44) * mm});
            skLineSegment(sketch, "E3681", {"start": v(355.17, 69.44) * mm, "end": v(355.14, 69.26) * mm});
            skLineSegment(sketch, "E3682", {"start": v(355.14, 69.26) * mm, "end": v(355.1, 69.07) * mm});
            skLineSegment(sketch, "E3683", {"start": v(355.1, 69.07) * mm, "end": v(355.06, 68.89) * mm});
            skLineSegment(sketch, "E3684", {"start": v(355.06, 68.89) * mm, "end": v(355.01, 68.7) * mm});
            skLineSegment(sketch, "E3685", {"start": v(355.01, 68.7) * mm, "end": v(354.95, 68.53) * mm});
            skLineSegment(sketch, "E3686", {"start": v(354.95, 68.53) * mm, "end": v(354.88, 68.35) * mm});
            skLineSegment(sketch, "E3687", {"start": v(354.88, 68.35) * mm, "end": v(354.8, 68.18) * mm});
            skLineSegment(sketch, "E3688", {"start": v(354.8, 68.18) * mm, "end": v(354.72, 68.01) * mm});
            skLineSegment(sketch, "E3689", {"start": v(354.72, 68.01) * mm, "end": v(354.63, 67.85) * mm});
            skLineSegment(sketch, "E3690", {"start": v(354.63, 67.85) * mm, "end": v(354.54, 67.69) * mm});
            skLineSegment(sketch, "E3691", {"start": v(354.54, 67.69) * mm, "end": v(354.43, 67.53) * mm});
            skLineSegment(sketch, "E3692", {"start": v(354.43, 67.53) * mm, "end": v(354.32, 67.38) * mm});
            skLineSegment(sketch, "E3693", {"start": v(354.32, 67.38) * mm, "end": v(354.2, 67.23) * mm});
            skLineSegment(sketch, "E3694", {"start": v(354.2, 67.23) * mm, "end": v(354.07, 67.11) * mm});
            skLineSegment(sketch, "E3695", {"start": v(354.07, 67.11) * mm, "end": v(353.95, 67) * mm});
            skLineSegment(sketch, "E3696", {"start": v(353.95, 67) * mm, "end": v(353.81, 66.9) * mm});
            skLineSegment(sketch, "E3697", {"start": v(353.81, 66.9) * mm, "end": v(353.68, 66.8) * mm});
            skLineSegment(sketch, "E3698", {"start": v(353.68, 66.8) * mm, "end": v(353.54, 66.7) * mm});
            skLineSegment(sketch, "E3699", {"start": v(353.54, 66.7) * mm, "end": v(353.4, 66.62) * mm});
            skLineSegment(sketch, "E3700", {"start": v(353.4, 66.62) * mm, "end": v(353.24, 66.54) * mm});
            skLineSegment(sketch, "E3701", {"start": v(353.24, 66.54) * mm, "end": v(353.09, 66.47) * mm});
            skLineSegment(sketch, "E3702", {"start": v(353.09, 66.47) * mm, "end": v(352.93, 66.41) * mm});
            skLineSegment(sketch, "E3703", {"start": v(352.93, 66.41) * mm, "end": v(352.77, 66.36) * mm});
            skLineSegment(sketch, "E3704", {"start": v(352.77, 66.36) * mm, "end": v(352.61, 66.31) * mm});
            skLineSegment(sketch, "E3705", {"start": v(352.61, 66.31) * mm, "end": v(352.45, 66.27) * mm});
            skLineSegment(sketch, "E3706", {"start": v(352.45, 66.27) * mm, "end": v(352.28, 66.24) * mm});
            skLineSegment(sketch, "E3707", {"start": v(352.28, 66.24) * mm, "end": v(352.11, 66.22) * mm});
            skLineSegment(sketch, "E3708", {"start": v(352.11, 66.22) * mm, "end": v(351.95, 66.21) * mm});
            skLineSegment(sketch, "E3709", {"start": v(351.95, 66.21) * mm, "end": v(351.78, 66.2) * mm});
            skLineSegment(sketch, "E3710", {"start": v(351.78, 66.2) * mm, "end": v(321.41, 66.2) * mm});
            skLineSegment(sketch, "E3711", {"start": v(328.54, 63.57) * mm, "end": v(328.54, 71.63) * mm});
            skLineSegment(sketch, "E3712", {"start": v(-304.36, 65.34) * mm, "end": v(-339.33, 65.34) * mm});
            skLineSegment(sketch, "E3713", {"start": v(-339.33, 65.34) * mm, "end": v(-339.33, 80.7) * mm});
            skLineSegment(sketch, "E3714", {"start": v(-339.33, 80.7) * mm, "end": v(-339.32, 81.13) * mm});
            skLineSegment(sketch, "E3715", {"start": v(-339.32, 81.13) * mm, "end": v(-339.3, 81.56) * mm});
            skLineSegment(sketch, "E3716", {"start": v(-339.3, 81.56) * mm, "end": v(-339.25, 82) * mm});
            skLineSegment(sketch, "E3717", {"start": v(-339.25, 82) * mm, "end": v(-339.18, 82.41) * mm});
            skLineSegment(sketch, "E3718", {"start": v(-339.18, 82.41) * mm, "end": v(-339.1, 82.83) * mm});
            skLineSegment(sketch, "E3719", {"start": v(-339.1, 82.83) * mm, "end": v(-338.98, 83.24) * mm});
            skLineSegment(sketch, "E3720", {"start": v(-338.98, 83.24) * mm, "end": v(-338.85, 83.65) * mm});
            skLineSegment(sketch, "E3721", {"start": v(-338.85, 83.65) * mm, "end": v(-338.7, 84.05) * mm});
            skLineSegment(sketch, "E3722", {"start": v(-338.7, 84.05) * mm, "end": v(-338.52, 84.44) * mm});
            skLineSegment(sketch, "E3723", {"start": v(-338.52, 84.44) * mm, "end": v(-338.33, 84.82) * mm});
            skLineSegment(sketch, "E3724", {"start": v(-338.33, 84.82) * mm, "end": v(-338.12, 85.19) * mm});
            skLineSegment(sketch, "E3725", {"start": v(-338.12, 85.19) * mm, "end": v(-337.9, 85.55) * mm});
            skLineSegment(sketch, "E3726", {"start": v(-337.9, 85.55) * mm, "end": v(-337.64, 85.9) * mm});
            skLineSegment(sketch, "E3727", {"start": v(-337.64, 85.9) * mm, "end": v(-337.38, 86.23) * mm});
            skLineSegment(sketch, "E3728", {"start": v(-337.38, 86.23) * mm, "end": v(-337.1, 86.55) * mm});
            skLineSegment(sketch, "E3729", {"start": v(-337.1, 86.55) * mm, "end": v(-336.79, 86.86) * mm});
            skLineSegment(sketch, "E3730", {"start": v(-336.79, 86.86) * mm, "end": v(-336.48, 87.16) * mm});
            skLineSegment(sketch, "E3731", {"start": v(-336.48, 87.16) * mm, "end": v(-336.16, 87.44) * mm});
            skLineSegment(sketch, "E3732", {"start": v(-336.16, 87.44) * mm, "end": v(-335.83, 87.7) * mm});
            skLineSegment(sketch, "E3733", {"start": v(-335.83, 87.7) * mm, "end": v(-335.48, 87.95) * mm});
            skLineSegment(sketch, "E3734", {"start": v(-335.48, 87.95) * mm, "end": v(-335.12, 88.18) * mm});
            skLineSegment(sketch, "E3735", {"start": v(-335.12, 88.18) * mm, "end": v(-334.76, 88.4) * mm});
            skLineSegment(sketch, "E3736", {"start": v(-334.76, 88.4) * mm, "end": v(-334.38, 88.58) * mm});
            skLineSegment(sketch, "E3737", {"start": v(-334.38, 88.58) * mm, "end": v(-334, 88.75) * mm});
            skLineSegment(sketch, "E3738", {"start": v(-334, 88.75) * mm, "end": v(-333.6, 88.9) * mm});
            skLineSegment(sketch, "E3739", {"start": v(-333.6, 88.9) * mm, "end": v(-333.2, 89.04) * mm});
            skLineSegment(sketch, "E3740", {"start": v(-333.2, 89.04) * mm, "end": v(-332.8, 89.16) * mm});
            skLineSegment(sketch, "E3741", {"start": v(-332.8, 89.16) * mm, "end": v(-332.38, 89.25) * mm});
            skLineSegment(sketch, "E3742", {"start": v(-332.38, 89.25) * mm, "end": v(-331.96, 89.32) * mm});
            skLineSegment(sketch, "E3743", {"start": v(-331.96, 89.32) * mm, "end": v(-331.54, 89.37) * mm});
            skLineSegment(sketch, "E3744", {"start": v(-331.54, 89.37) * mm, "end": v(-331.11, 89.4) * mm});
            skLineSegment(sketch, "E3745", {"start": v(-331.11, 89.4) * mm, "end": v(-330.68, 89.42) * mm});
            skLineSegment(sketch, "E3746", {"start": v(-330.68, 89.42) * mm, "end": v(-330.25, 89.42) * mm});
            skLineSegment(sketch, "E3747", {"start": v(-330.25, 89.42) * mm, "end": v(-329.8, 89.4) * mm});
            skLineSegment(sketch, "E3748", {"start": v(-329.8, 89.4) * mm, "end": v(-329.37, 89.36) * mm});
            skLineSegment(sketch, "E3749", {"start": v(-329.37, 89.36) * mm, "end": v(-328.95, 89.3) * mm});
            skLineSegment(sketch, "E3750", {"start": v(-328.95, 89.3) * mm, "end": v(-328.52, 89.2) * mm});
            skLineSegment(sketch, "E3751", {"start": v(-328.52, 89.2) * mm, "end": v(-328.1, 89.1) * mm});
            skLineSegment(sketch, "E3752", {"start": v(-328.1, 89.1) * mm, "end": v(-327.69, 88.97) * mm});
            skLineSegment(sketch, "E3753", {"start": v(-327.69, 88.97) * mm, "end": v(-327.28, 88.82) * mm});
            skLineSegment(sketch, "E3754", {"start": v(-327.28, 88.82) * mm, "end": v(-326.88, 88.65) * mm});
            skLineSegment(sketch, "E3755", {"start": v(-326.88, 88.65) * mm, "end": v(-326.5, 88.47) * mm});
            skLineSegment(sketch, "E3756", {"start": v(-326.5, 88.47) * mm, "end": v(-326.11, 88.26) * mm});
            skLineSegment(sketch, "E3757", {"start": v(-326.11, 88.26) * mm, "end": v(-325.74, 88.03) * mm});
            skLineSegment(sketch, "E3758", {"start": v(-325.74, 88.03) * mm, "end": v(-325.39, 87.78) * mm});
            skLineSegment(sketch, "E3759", {"start": v(-325.39, 87.78) * mm, "end": v(-325.04, 87.52) * mm});
            skLineSegment(sketch, "E3760", {"start": v(-325.04, 87.52) * mm, "end": v(-324.7, 87.23) * mm});
            skLineSegment(sketch, "E3761", {"start": v(-324.7, 87.23) * mm, "end": v(-324.39, 86.93) * mm});
            skLineSegment(sketch, "E3762", {"start": v(-324.39, 86.93) * mm, "end": v(-324.09, 86.62) * mm});
            skLineSegment(sketch, "E3763", {"start": v(-324.09, 86.62) * mm, "end": v(-323.8, 86.29) * mm});
            skLineSegment(sketch, "E3764", {"start": v(-323.8, 86.29) * mm, "end": v(-323.54, 85.95) * mm});
            skLineSegment(sketch, "E3765", {"start": v(-323.54, 85.95) * mm, "end": v(-323.3, 85.6) * mm});
            skLineSegment(sketch, "E3766", {"start": v(-323.3, 85.6) * mm, "end": v(-323.06, 85.23) * mm});
            skLineSegment(sketch, "E3767", {"start": v(-323.06, 85.23) * mm, "end": v(-322.85, 84.85) * mm});
            skLineSegment(sketch, "E3768", {"start": v(-322.85, 84.85) * mm, "end": v(-322.66, 84.47) * mm});
            skLineSegment(sketch, "E3769", {"start": v(-322.66, 84.47) * mm, "end": v(-322.49, 84.07) * mm});
            skLineSegment(sketch, "E3770", {"start": v(-322.49, 84.07) * mm, "end": v(-322.34, 83.67) * mm});
            skLineSegment(sketch, "E3771", {"start": v(-322.34, 83.67) * mm, "end": v(-322.2, 83.26) * mm});
            skLineSegment(sketch, "E3772", {"start": v(-322.2, 83.26) * mm, "end": v(-322.1, 82.85) * mm});
            skLineSegment(sketch, "E3773", {"start": v(-322.1, 82.85) * mm, "end": v(-322, 82.43) * mm});
            skLineSegment(sketch, "E3774", {"start": v(-322, 82.43) * mm, "end": v(-321.93, 82) * mm});
            skLineSegment(sketch, "E3775", {"start": v(-321.93, 82) * mm, "end": v(-321.88, 81.57) * mm});
            skLineSegment(sketch, "E3776", {"start": v(-321.88, 81.57) * mm, "end": v(-321.86, 81.14) * mm});
            skLineSegment(sketch, "E3777", {"start": v(-321.86, 81.14) * mm, "end": v(-321.85, 80.7) * mm});
            skLineSegment(sketch, "E3778", {"start": v(-321.85, 80.7) * mm, "end": v(-321.85, 65.34) * mm});
            skLineSegment(sketch, "E3779", {"start": v(-321.85, 80.7) * mm, "end": v(-321.85, 81.06) * mm});
            skLineSegment(sketch, "E3780", {"start": v(-321.85, 81.06) * mm, "end": v(-321.83, 81.42) * mm});
            skLineSegment(sketch, "E3781", {"start": v(-321.83, 81.42) * mm, "end": v(-321.8, 81.77) * mm});
            skLineSegment(sketch, "E3782", {"start": v(-321.8, 81.77) * mm, "end": v(-321.74, 82.12) * mm});
            skLineSegment(sketch, "E3783", {"start": v(-321.74, 82.12) * mm, "end": v(-321.66, 82.47) * mm});
            skLineSegment(sketch, "E3784", {"start": v(-321.66, 82.47) * mm, "end": v(-321.57, 82.8) * mm});
            skLineSegment(sketch, "E3785", {"start": v(-321.57, 82.8) * mm, "end": v(-321.46, 83.15) * mm});
            skLineSegment(sketch, "E3786", {"start": v(-321.46, 83.15) * mm, "end": v(-321.34, 83.48) * mm});
            skLineSegment(sketch, "E3787", {"start": v(-321.34, 83.48) * mm, "end": v(-321.2, 83.8) * mm});
            skLineSegment(sketch, "E3788", {"start": v(-321.2, 83.8) * mm, "end": v(-321.04, 84.12) * mm});
            skLineSegment(sketch, "E3789", {"start": v(-321.04, 84.12) * mm, "end": v(-320.87, 84.42) * mm});
            skLineSegment(sketch, "E3790", {"start": v(-320.87, 84.42) * mm, "end": v(-320.68, 84.72) * mm});
            skLineSegment(sketch, "E3791", {"start": v(-320.68, 84.72) * mm, "end": v(-320.47, 85.01) * mm});
            skLineSegment(sketch, "E3792", {"start": v(-320.47, 85.01) * mm, "end": v(-320.25, 85.3) * mm});
            skLineSegment(sketch, "E3793", {"start": v(-320.25, 85.3) * mm, "end": v(-320.02, 85.56) * mm});
            skLineSegment(sketch, "E3794", {"start": v(-320.02, 85.56) * mm, "end": v(-319.77, 85.82) * mm});
            skLineSegment(sketch, "E3795", {"start": v(-319.77, 85.82) * mm, "end": v(-319.33, 86.12) * mm});
            skLineSegment(sketch, "E3796", {"start": v(-319.33, 86.12) * mm, "end": v(-318.88, 86.4) * mm});
            skLineSegment(sketch, "E3797", {"start": v(-318.88, 86.4) * mm, "end": v(-318.42, 86.65) * mm});
            skLineSegment(sketch, "E3798", {"start": v(-318.42, 86.65) * mm, "end": v(-317.95, 86.89) * mm});
            skLineSegment(sketch, "E3799", {"start": v(-317.95, 86.89) * mm, "end": v(-317.47, 87.1) * mm});
            skLineSegment(sketch, "E3800", {"start": v(-317.47, 87.1) * mm, "end": v(-316.98, 87.3) * mm});
            skLineSegment(sketch, "E3801", {"start": v(-316.98, 87.3) * mm, "end": v(-316.49, 87.46) * mm});
            skLineSegment(sketch, "E3802", {"start": v(-316.49, 87.46) * mm, "end": v(-315.99, 87.61) * mm});
            skLineSegment(sketch, "E3803", {"start": v(-315.99, 87.61) * mm, "end": v(-315.48, 87.74) * mm});
            skLineSegment(sketch, "E3804", {"start": v(-315.48, 87.74) * mm, "end": v(-314.96, 87.84) * mm});
            skLineSegment(sketch, "E3805", {"start": v(-314.96, 87.84) * mm, "end": v(-314.45, 87.92) * mm});
            skLineSegment(sketch, "E3806", {"start": v(-314.45, 87.92) * mm, "end": v(-313.92, 87.98) * mm});
            skLineSegment(sketch, "E3807", {"start": v(-313.92, 87.98) * mm, "end": v(-313.4, 88.01) * mm});
            skLineSegment(sketch, "E3808", {"start": v(-313.4, 88.01) * mm, "end": v(-312.87, 88.02) * mm});
            skLineSegment(sketch, "E3809", {"start": v(-312.87, 88.02) * mm, "end": v(-312.34, 88.01) * mm});
            skLineSegment(sketch, "E3810", {"start": v(-312.34, 88.01) * mm, "end": v(-311.82, 87.97) * mm});
            skLineSegment(sketch, "E3811", {"start": v(-311.82, 87.97) * mm, "end": v(-311.35, 87.97) * mm});
            skLineSegment(sketch, "E3812", {"start": v(-311.35, 87.97) * mm, "end": v(-310.88, 87.97) * mm});
            skLineSegment(sketch, "E3813", {"start": v(-310.88, 87.97) * mm, "end": v(-310.4, 87.98) * mm});
            skLineSegment(sketch, "E3814", {"start": v(-310.4, 87.98) * mm, "end": v(-309.93, 88) * mm});
            skLineSegment(sketch, "E3815", {"start": v(-309.93, 88) * mm, "end": v(-309.46, 88.02) * mm});
            skLineSegment(sketch, "E3816", {"start": v(-309.46, 88.02) * mm, "end": v(-309, 88.06) * mm});
            skLineSegment(sketch, "E3817", {"start": v(-309, 88.06) * mm, "end": v(-308.53, 88.1) * mm});
            skLineSegment(sketch, "E3818", {"start": v(-308.53, 88.1) * mm, "end": v(-308.06, 88.16) * mm});
            skLineSegment(sketch, "E3819", {"start": v(-308.06, 88.16) * mm, "end": v(-307.59, 88.22) * mm});
            skLineSegment(sketch, "E3820", {"start": v(-307.59, 88.22) * mm, "end": v(-307.12, 88.29) * mm});
            skLineSegment(sketch, "E3821", {"start": v(-307.12, 88.29) * mm, "end": v(-306.66, 88.36) * mm});
            skLineSegment(sketch, "E3822", {"start": v(-306.66, 88.36) * mm, "end": v(-306.2, 88.45) * mm});
            skLineSegment(sketch, "E3823", {"start": v(-306.2, 88.45) * mm, "end": v(-305.73, 88.54) * mm});
            skLineSegment(sketch, "E3824", {"start": v(-305.73, 88.54) * mm, "end": v(-305.27, 88.65) * mm});
            skLineSegment(sketch, "E3825", {"start": v(-305.27, 88.65) * mm, "end": v(-304.82, 88.76) * mm});
            skLineSegment(sketch, "E3826", {"start": v(-304.82, 88.76) * mm, "end": v(-304.36, 88.88) * mm});
            skLineSegment(sketch, "E3827", {"start": v(-303.87, 111.54) * mm, "end": v(-303.87, 111.18) * mm});
            skLineSegment(sketch, "E3828", {"start": v(-303.87, 111.18) * mm, "end": v(-303.88, 110.8) * mm});
            skLineSegment(sketch, "E3829", {"start": v(-303.88, 110.8) * mm, "end": v(-303.9, 110.44) * mm});
            skLineSegment(sketch, "E3830", {"start": v(-303.9, 110.44) * mm, "end": v(-303.92, 110.08) * mm});
            skLineSegment(sketch, "E3831", {"start": v(-303.92, 110.08) * mm, "end": v(-303.95, 109.72) * mm});
            skLineSegment(sketch, "E3832", {"start": v(-303.95, 109.72) * mm, "end": v(-304, 109.35) * mm});
            skLineSegment(sketch, "E3833", {"start": v(-304, 109.35) * mm, "end": v(-304.04, 109) * mm});
            skLineSegment(sketch, "E3834", {"start": v(-304.04, 109) * mm, "end": v(-304.1, 108.64) * mm});
            skLineSegment(sketch, "E3835", {"start": v(-304.1, 108.64) * mm, "end": v(-304.17, 108.28) * mm});
            skLineSegment(sketch, "E3836", {"start": v(-304.17, 108.28) * mm, "end": v(-304.25, 107.92) * mm});
            skLineSegment(sketch, "E3837", {"start": v(-304.25, 107.92) * mm, "end": v(-304.34, 107.57) * mm});
            skLineSegment(sketch, "E3838", {"start": v(-304.34, 107.57) * mm, "end": v(-304.44, 107.22) * mm});
            skLineSegment(sketch, "E3839", {"start": v(-304.44, 107.22) * mm, "end": v(-304.54, 106.88) * mm});
            skLineSegment(sketch, "E3840", {"start": v(-304.54, 106.88) * mm, "end": v(-304.65, 106.53) * mm});
            skLineSegment(sketch, "E3841", {"start": v(-304.65, 106.53) * mm, "end": v(-304.77, 106.2) * mm});
            skLineSegment(sketch, "E3842", {"start": v(-304.77, 106.2) * mm, "end": v(-304.9, 105.85) * mm});
            skLineSegment(sketch, "E3843", {"start": v(-304.9, 105.85) * mm, "end": v(-305.04, 105.52) * mm});
            skLineSegment(sketch, "E3844", {"start": v(-305.04, 105.52) * mm, "end": v(-305.19, 105.19) * mm});
            skLineSegment(sketch, "E3845", {"start": v(-305.19, 105.19) * mm, "end": v(-305.34, 104.86) * mm});
            skLineSegment(sketch, "E3846", {"start": v(-305.34, 104.86) * mm, "end": v(-305.5, 104.54) * mm});
            skLineSegment(sketch, "E3847", {"start": v(-305.5, 104.54) * mm, "end": v(-305.68, 104.22) * mm});
            skLineSegment(sketch, "E3848", {"start": v(-305.68, 104.22) * mm, "end": v(-305.86, 103.9) * mm});
            skLineSegment(sketch, "E3849", {"start": v(-305.86, 103.9) * mm, "end": v(-306.04, 103.6) * mm});
            skLineSegment(sketch, "E3850", {"start": v(-306.04, 103.6) * mm, "end": v(-306.24, 103.28) * mm});
            skLineSegment(sketch, "E3851", {"start": v(-306.24, 103.28) * mm, "end": v(-306.44, 102.98) * mm});
            skLineSegment(sketch, "E3852", {"start": v(-306.44, 102.98) * mm, "end": v(-306.65, 102.68) * mm});
            skLineSegment(sketch, "E3853", {"start": v(-306.65, 102.68) * mm, "end": v(-306.87, 102.4) * mm});
            skLineSegment(sketch, "E3854", {"start": v(-306.87, 102.4) * mm, "end": v(-307.1, 102.1) * mm});
            skLineSegment(sketch, "E3855", {"start": v(-307.1, 102.1) * mm, "end": v(-307.32, 101.82) * mm});
            skLineSegment(sketch, "E3856", {"start": v(-307.32, 101.82) * mm, "end": v(-307.56, 101.55) * mm});
            skLineSegment(sketch, "E3857", {"start": v(-307.56, 101.55) * mm, "end": v(-307.81, 101.28) * mm});
            skLineSegment(sketch, "E3858", {"start": v(-307.81, 101.28) * mm, "end": v(-308.07, 101.01) * mm});
            skLineSegment(sketch, "E3859", {"start": v(-308.07, 101.01) * mm, "end": v(-308.4, 100.7) * mm});
            skLineSegment(sketch, "E3860", {"start": v(-308.4, 100.7) * mm, "end": v(-308.74, 100.4) * mm});
            skLineSegment(sketch, "E3861", {"start": v(-308.74, 100.4) * mm, "end": v(-309.09, 100.12) * mm});
            skLineSegment(sketch, "E3862", {"start": v(-309.09, 100.12) * mm, "end": v(-309.44, 99.84) * mm});
            skLineSegment(sketch, "E3863", {"start": v(-309.44, 99.84) * mm, "end": v(-309.8, 99.57) * mm});
            skLineSegment(sketch, "E3864", {"start": v(-309.8, 99.57) * mm, "end": v(-310.16, 99.31) * mm});
            skLineSegment(sketch, "E3865", {"start": v(-310.16, 99.31) * mm, "end": v(-310.53, 99.06) * mm});
            skLineSegment(sketch, "E3866", {"start": v(-310.53, 99.06) * mm, "end": v(-310.91, 98.82) * mm});
            skLineSegment(sketch, "E3867", {"start": v(-310.91, 98.82) * mm, "end": v(-311.3, 98.59) * mm});
            skLineSegment(sketch, "E3868", {"start": v(-311.3, 98.59) * mm, "end": v(-311.68, 98.37) * mm});
            skLineSegment(sketch, "E3869", {"start": v(-311.68, 98.37) * mm, "end": v(-312.07, 98.16) * mm});
            skLineSegment(sketch, "E3870", {"start": v(-312.07, 98.16) * mm, "end": v(-312.47, 97.95) * mm});
            skLineSegment(sketch, "E3871", {"start": v(-312.47, 97.95) * mm, "end": v(-312.87, 97.76) * mm});
            skLineSegment(sketch, "E3872", {"start": v(-312.87, 97.76) * mm, "end": v(-313.28, 97.58) * mm});
            skLineSegment(sketch, "E3873", {"start": v(-313.28, 97.58) * mm, "end": v(-313.7, 97.4) * mm});
            skLineSegment(sketch, "E3874", {"start": v(-313.7, 97.4) * mm, "end": v(-314.1, 97.24) * mm});
            skLineSegment(sketch, "E3875", {"start": v(-314.1, 97.24) * mm, "end": v(-314.53, 97.1) * mm});
            skLineSegment(sketch, "E3876", {"start": v(-314.53, 97.1) * mm, "end": v(-314.95, 96.95) * mm});
            skLineSegment(sketch, "E3877", {"start": v(-314.95, 96.95) * mm, "end": v(-315.37, 96.82) * mm});
            skLineSegment(sketch, "E3878", {"start": v(-315.37, 96.82) * mm, "end": v(-315.8, 96.7) * mm});
            skLineSegment(sketch, "E3879", {"start": v(-315.8, 96.7) * mm, "end": v(-316.24, 96.59) * mm});
            skLineSegment(sketch, "E3880", {"start": v(-316.24, 96.59) * mm, "end": v(-316.67, 96.49) * mm});
            skLineSegment(sketch, "E3881", {"start": v(-316.67, 96.49) * mm, "end": v(-317.1, 96.4) * mm});
            skLineSegment(sketch, "E3882", {"start": v(-317.1, 96.4) * mm, "end": v(-317.55, 96.32) * mm});
            skLineSegment(sketch, "E3883", {"start": v(-317.55, 96.32) * mm, "end": v(-318, 96.25) * mm});
            skLineSegment(sketch, "E3884", {"start": v(-318, 96.25) * mm, "end": v(-318.43, 96.2) * mm});
            skLineSegment(sketch, "E3885", {"start": v(-318.43, 96.2) * mm, "end": v(-318.88, 96.15) * mm});
            skLineSegment(sketch, "E3886", {"start": v(-318.88, 96.15) * mm, "end": v(-319.33, 96.12) * mm});
            skLineSegment(sketch, "E3887", {"start": v(-319.33, 96.12) * mm, "end": v(-319.78, 96.1) * mm});
            skLineSegment(sketch, "E3888", {"start": v(-319.78, 96.1) * mm, "end": v(-320.23, 96.08) * mm});
            skLineSegment(sketch, "E3889", {"start": v(-320.23, 96.08) * mm, "end": v(-320.68, 96.08) * mm});
            skLineSegment(sketch, "E3890", {"start": v(-320.68, 96.08) * mm, "end": v(-321.13, 96.09) * mm});
            skLineSegment(sketch, "E3891", {"start": v(-321.13, 96.09) * mm, "end": v(-321.62, 96.08) * mm});
            skLineSegment(sketch, "E3892", {"start": v(-321.62, 96.08) * mm, "end": v(-322.11, 96.07) * mm});
            skLineSegment(sketch, "E3893", {"start": v(-322.11, 96.07) * mm, "end": v(-322.6, 96.08) * mm});
            skLineSegment(sketch, "E3894", {"start": v(-322.6, 96.08) * mm, "end": v(-323.09, 96.1) * mm});
            skLineSegment(sketch, "E3895", {"start": v(-323.09, 96.1) * mm, "end": v(-323.58, 96.14) * mm});
            skLineSegment(sketch, "E3896", {"start": v(-323.58, 96.14) * mm, "end": v(-324.06, 96.2) * mm});
            skLineSegment(sketch, "E3897", {"start": v(-324.06, 96.2) * mm, "end": v(-324.54, 96.25) * mm});
            skLineSegment(sketch, "E3898", {"start": v(-324.54, 96.25) * mm, "end": v(-325.02, 96.32) * mm});
            skLineSegment(sketch, "E3899", {"start": v(-325.02, 96.32) * mm, "end": v(-325.5, 96.4) * mm});
            skLineSegment(sketch, "E3900", {"start": v(-325.5, 96.4) * mm, "end": v(-325.98, 96.5) * mm});
            skLineSegment(sketch, "E3901", {"start": v(-325.98, 96.5) * mm, "end": v(-326.45, 96.6) * mm});
            skLineSegment(sketch, "E3902", {"start": v(-326.45, 96.6) * mm, "end": v(-326.92, 96.73) * mm});
            skLineSegment(sketch, "E3903", {"start": v(-326.92, 96.73) * mm, "end": v(-327.39, 96.86) * mm});
            skLineSegment(sketch, "E3904", {"start": v(-327.39, 96.86) * mm, "end": v(-327.85, 97) * mm});
            skLineSegment(sketch, "E3905", {"start": v(-327.85, 97) * mm, "end": v(-328.3, 97.15) * mm});
            skLineSegment(sketch, "E3906", {"start": v(-328.3, 97.15) * mm, "end": v(-328.76, 97.32) * mm});
            skLineSegment(sketch, "E3907", {"start": v(-328.76, 97.32) * mm, "end": v(-329.21, 97.5) * mm});
            skLineSegment(sketch, "E3908", {"start": v(-329.21, 97.5) * mm, "end": v(-329.66, 97.68) * mm});
            skLineSegment(sketch, "E3909", {"start": v(-329.66, 97.68) * mm, "end": v(-330.1, 97.88) * mm});
            skLineSegment(sketch, "E3910", {"start": v(-330.1, 97.88) * mm, "end": v(-330.54, 98.09) * mm});
            skLineSegment(sketch, "E3911", {"start": v(-330.54, 98.09) * mm, "end": v(-330.97, 98.3) * mm});
            skLineSegment(sketch, "E3912", {"start": v(-330.97, 98.3) * mm, "end": v(-331.4, 98.54) * mm});
            skLineSegment(sketch, "E3913", {"start": v(-331.4, 98.54) * mm, "end": v(-331.82, 98.78) * mm});
            skLineSegment(sketch, "E3914", {"start": v(-331.82, 98.78) * mm, "end": v(-332.23, 99.03) * mm});
            skLineSegment(sketch, "E3915", {"start": v(-332.23, 99.03) * mm, "end": v(-332.64, 99.3) * mm});
            skLineSegment(sketch, "E3916", {"start": v(-332.64, 99.3) * mm, "end": v(-333.04, 99.57) * mm});
            skLineSegment(sketch, "E3917", {"start": v(-333.04, 99.57) * mm, "end": v(-333.44, 99.85) * mm});
            skLineSegment(sketch, "E3918", {"start": v(-333.44, 99.85) * mm, "end": v(-333.83, 100.14) * mm});
            skLineSegment(sketch, "E3919", {"start": v(-333.83, 100.14) * mm, "end": v(-334.21, 100.45) * mm});
            skLineSegment(sketch, "E3920", {"start": v(-334.21, 100.45) * mm, "end": v(-334.59, 100.76) * mm});
            skLineSegment(sketch, "E3921", {"start": v(-334.59, 100.76) * mm, "end": v(-334.95, 101.08) * mm});
            skLineSegment(sketch, "E3922", {"start": v(-334.95, 101.08) * mm, "end": v(-335.31, 101.42) * mm});
            skLineSegment(sketch, "E3923", {"start": v(-335.31, 101.42) * mm, "end": v(-335.57, 101.67) * mm});
            skLineSegment(sketch, "E3924", {"start": v(-335.57, 101.67) * mm, "end": v(-335.81, 101.92) * mm});
            skLineSegment(sketch, "E3925", {"start": v(-335.81, 101.92) * mm, "end": v(-336.05, 102.19) * mm});
            skLineSegment(sketch, "E3926", {"start": v(-336.05, 102.19) * mm, "end": v(-336.29, 102.45) * mm});
            skLineSegment(sketch, "E3927", {"start": v(-336.29, 102.45) * mm, "end": v(-336.51, 102.73) * mm});
            skLineSegment(sketch, "E3928", {"start": v(-336.51, 102.73) * mm, "end": v(-336.73, 103) * mm});
            skLineSegment(sketch, "E3929", {"start": v(-336.73, 103) * mm, "end": v(-336.94, 103.29) * mm});
            skLineSegment(sketch, "E3930", {"start": v(-336.94, 103.29) * mm, "end": v(-337.14, 103.58) * mm});
            skLineSegment(sketch, "E3931", {"start": v(-337.14, 103.58) * mm, "end": v(-337.34, 103.87) * mm});
            skLineSegment(sketch, "E3932", {"start": v(-337.34, 103.87) * mm, "end": v(-337.53, 104.17) * mm});
            skLineSegment(sketch, "E3933", {"start": v(-337.53, 104.17) * mm, "end": v(-337.7, 104.47) * mm});
            skLineSegment(sketch, "E3934", {"start": v(-337.7, 104.47) * mm, "end": v(-337.88, 104.78) * mm});
            skLineSegment(sketch, "E3935", {"start": v(-337.88, 104.78) * mm, "end": v(-338.04, 105.09) * mm});
            skLineSegment(sketch, "E3936", {"start": v(-338.04, 105.09) * mm, "end": v(-338.2, 105.4) * mm});
            skLineSegment(sketch, "E3937", {"start": v(-338.2, 105.4) * mm, "end": v(-338.34, 105.72) * mm});
            skLineSegment(sketch, "E3938", {"start": v(-338.34, 105.72) * mm, "end": v(-338.48, 106.04) * mm});
            skLineSegment(sketch, "E3939", {"start": v(-338.48, 106.04) * mm, "end": v(-338.61, 106.37) * mm});
            skLineSegment(sketch, "E3940", {"start": v(-338.61, 106.37) * mm, "end": v(-338.73, 106.7) * mm});
            skLineSegment(sketch, "E3941", {"start": v(-338.73, 106.7) * mm, "end": v(-338.85, 107.03) * mm});
            skLineSegment(sketch, "E3942", {"start": v(-338.85, 107.03) * mm, "end": v(-338.95, 107.37) * mm});
            skLineSegment(sketch, "E3943", {"start": v(-338.95, 107.37) * mm, "end": v(-339.05, 107.7) * mm});
            skLineSegment(sketch, "E3944", {"start": v(-339.05, 107.7) * mm, "end": v(-339.14, 108.04) * mm});
            skLineSegment(sketch, "E3945", {"start": v(-339.14, 108.04) * mm, "end": v(-339.22, 108.39) * mm});
            skLineSegment(sketch, "E3946", {"start": v(-339.22, 108.39) * mm, "end": v(-339.3, 108.73) * mm});
            skLineSegment(sketch, "E3947", {"start": v(-339.3, 108.73) * mm, "end": v(-339.35, 109.08) * mm});
            skLineSegment(sketch, "E3948", {"start": v(-339.35, 109.08) * mm, "end": v(-339.4, 109.43) * mm});
            skLineSegment(sketch, "E3949", {"start": v(-339.4, 109.43) * mm, "end": v(-339.45, 109.78) * mm});
            skLineSegment(sketch, "E3950", {"start": v(-339.45, 109.78) * mm, "end": v(-339.49, 110.13) * mm});
            skLineSegment(sketch, "E3951", {"start": v(-339.49, 110.13) * mm, "end": v(-339.51, 110.48) * mm});
            skLineSegment(sketch, "E3952", {"start": v(-339.51, 110.48) * mm, "end": v(-339.53, 110.84) * mm});
            skLineSegment(sketch, "E3953", {"start": v(-339.53, 110.84) * mm, "end": v(-339.54, 111.2) * mm});
            skLineSegment(sketch, "E3954", {"start": v(-339.54, 111.2) * mm, "end": v(-339.54, 111.55) * mm});
            skLineSegment(sketch, "E3955", {"start": v(-339.54, 111.55) * mm, "end": v(-339.53, 111.91) * mm});
            skLineSegment(sketch, "E3956", {"start": v(-339.53, 111.91) * mm, "end": v(-339.52, 112.27) * mm});
            skLineSegment(sketch, "E3957", {"start": v(-339.52, 112.27) * mm, "end": v(-339.5, 112.63) * mm});
            skLineSegment(sketch, "E3958", {"start": v(-339.5, 112.63) * mm, "end": v(-339.47, 113) * mm});
            skLineSegment(sketch, "E3959", {"start": v(-339.47, 113) * mm, "end": v(-339.43, 113.35) * mm});
            skLineSegment(sketch, "E3960", {"start": v(-339.43, 113.35) * mm, "end": v(-339.38, 113.7) * mm});
            skLineSegment(sketch, "E3961", {"start": v(-339.38, 113.7) * mm, "end": v(-339.32, 114.06) * mm});
            skLineSegment(sketch, "E3962", {"start": v(-339.32, 114.06) * mm, "end": v(-339.25, 114.41) * mm});
            skLineSegment(sketch, "E3963", {"start": v(-339.25, 114.41) * mm, "end": v(-339.17, 114.76) * mm});
            skLineSegment(sketch, "E3964", {"start": v(-339.17, 114.76) * mm, "end": v(-339.09, 115.1) * mm});
            skLineSegment(sketch, "E3965", {"start": v(-339.09, 115.1) * mm, "end": v(-339, 115.45) * mm});
            skLineSegment(sketch, "E3966", {"start": v(-339, 115.45) * mm, "end": v(-338.9, 115.8) * mm});
            skLineSegment(sketch, "E3967", {"start": v(-338.9, 115.8) * mm, "end": v(-338.78, 116.14) * mm});
            skLineSegment(sketch, "E3968", {"start": v(-338.78, 116.14) * mm, "end": v(-338.66, 116.47) * mm});
            skLineSegment(sketch, "E3969", {"start": v(-338.66, 116.47) * mm, "end": v(-338.53, 116.8) * mm});
            skLineSegment(sketch, "E3970", {"start": v(-338.53, 116.8) * mm, "end": v(-338.4, 117.13) * mm});
            skLineSegment(sketch, "E3971", {"start": v(-338.4, 117.13) * mm, "end": v(-338.25, 117.46) * mm});
            skLineSegment(sketch, "E3972", {"start": v(-338.25, 117.46) * mm, "end": v(-338.1, 117.78) * mm});
            skLineSegment(sketch, "E3973", {"start": v(-338.1, 117.78) * mm, "end": v(-337.93, 118.1) * mm});
            skLineSegment(sketch, "E3974", {"start": v(-337.93, 118.1) * mm, "end": v(-337.76, 118.41) * mm});
            skLineSegment(sketch, "E3975", {"start": v(-337.76, 118.41) * mm, "end": v(-337.58, 118.72) * mm});
            skLineSegment(sketch, "E3976", {"start": v(-337.58, 118.72) * mm, "end": v(-337.4, 119.03) * mm});
            skLineSegment(sketch, "E3977", {"start": v(-337.4, 119.03) * mm, "end": v(-337.2, 119.33) * mm});
            skLineSegment(sketch, "E3978", {"start": v(-337.2, 119.33) * mm, "end": v(-337, 119.62) * mm});
            skLineSegment(sketch, "E3979", {"start": v(-337, 119.62) * mm, "end": v(-336.8, 119.91) * mm});
            skLineSegment(sketch, "E3980", {"start": v(-336.8, 119.91) * mm, "end": v(-336.58, 120.2) * mm});
            skLineSegment(sketch, "E3981", {"start": v(-336.58, 120.2) * mm, "end": v(-336.35, 120.48) * mm});
            skLineSegment(sketch, "E3982", {"start": v(-336.35, 120.48) * mm, "end": v(-336.12, 120.76) * mm});
            skLineSegment(sketch, "E3983", {"start": v(-336.12, 120.76) * mm, "end": v(-335.88, 121.02) * mm});
            skLineSegment(sketch, "E3984", {"start": v(-335.88, 121.02) * mm, "end": v(-335.63, 121.29) * mm});
            skLineSegment(sketch, "E3985", {"start": v(-335.63, 121.29) * mm, "end": v(-335.38, 121.54) * mm});
            skLineSegment(sketch, "E3986", {"start": v(-335.38, 121.54) * mm, "end": v(-335.12, 121.8) * mm});
            skLineSegment(sketch, "E3987", {"start": v(-335.12, 121.8) * mm, "end": v(-334.76, 122.12) * mm});
            skLineSegment(sketch, "E3988", {"start": v(-334.76, 122.12) * mm, "end": v(-334.4, 122.43) * mm});
            skLineSegment(sketch, "E3989", {"start": v(-334.4, 122.43) * mm, "end": v(-334.02, 122.74) * mm});
            skLineSegment(sketch, "E3990", {"start": v(-334.02, 122.74) * mm, "end": v(-333.64, 123.03) * mm});
            skLineSegment(sketch, "E3991", {"start": v(-333.64, 123.03) * mm, "end": v(-333.25, 123.32) * mm});
            skLineSegment(sketch, "E3992", {"start": v(-333.25, 123.32) * mm, "end": v(-332.86, 123.6) * mm});
            skLineSegment(sketch, "E3993", {"start": v(-332.86, 123.6) * mm, "end": v(-332.46, 123.85) * mm});
            skLineSegment(sketch, "E3994", {"start": v(-332.46, 123.85) * mm, "end": v(-332.06, 124.1) * mm});
            skLineSegment(sketch, "E3995", {"start": v(-332.06, 124.1) * mm, "end": v(-331.65, 124.35) * mm});
            skLineSegment(sketch, "E3996", {"start": v(-331.65, 124.35) * mm, "end": v(-331.23, 124.58) * mm});
            skLineSegment(sketch, "E3997", {"start": v(-331.23, 124.58) * mm, "end": v(-330.8, 124.8) * mm});
            skLineSegment(sketch, "E3998", {"start": v(-330.8, 124.8) * mm, "end": v(-330.38, 125.02) * mm});
            skLineSegment(sketch, "E3999", {"start": v(-330.38, 125.02) * mm, "end": v(-329.95, 125.22) * mm});
            skLineSegment(sketch, "E4000", {"start": v(-329.95, 125.22) * mm, "end": v(-329.51, 125.4) * mm});
            skLineSegment(sketch, "E4001", {"start": v(-329.51, 125.4) * mm, "end": v(-329.07, 125.59) * mm});
            skLineSegment(sketch, "E4002", {"start": v(-329.07, 125.59) * mm, "end": v(-328.63, 125.76) * mm});
            skLineSegment(sketch, "E4003", {"start": v(-328.63, 125.76) * mm, "end": v(-328.18, 125.91) * mm});
            skLineSegment(sketch, "E4004", {"start": v(-328.18, 125.91) * mm, "end": v(-327.73, 126.06) * mm});
            skLineSegment(sketch, "E4005", {"start": v(-327.73, 126.06) * mm, "end": v(-327.27, 126.2) * mm});
            skLineSegment(sketch, "E4006", {"start": v(-327.27, 126.2) * mm, "end": v(-326.8, 126.32) * mm});
            skLineSegment(sketch, "E4007", {"start": v(-326.8, 126.32) * mm, "end": v(-326.35, 126.43) * mm});
            skLineSegment(sketch, "E4008", {"start": v(-326.35, 126.43) * mm, "end": v(-325.88, 126.53) * mm});
            skLineSegment(sketch, "E4009", {"start": v(-325.88, 126.53) * mm, "end": v(-325.41, 126.62) * mm});
            skLineSegment(sketch, "E4010", {"start": v(-325.41, 126.62) * mm, "end": v(-324.94, 126.7) * mm});
            skLineSegment(sketch, "E4011", {"start": v(-324.94, 126.7) * mm, "end": v(-324.47, 126.77) * mm});
            skLineSegment(sketch, "E4012", {"start": v(-324.47, 126.77) * mm, "end": v(-324, 126.82) * mm});
            skLineSegment(sketch, "E4013", {"start": v(-324, 126.82) * mm, "end": v(-323.51, 126.87) * mm});
            skLineSegment(sketch, "E4014", {"start": v(-323.51, 126.87) * mm, "end": v(-323.04, 126.9) * mm});
            skLineSegment(sketch, "E4015", {"start": v(-323.04, 126.9) * mm, "end": v(-322.56, 126.92) * mm});
            skLineSegment(sketch, "E4016", {"start": v(-322.56, 126.92) * mm, "end": v(-322.08, 126.92) * mm});
            skLineSegment(sketch, "E4017", {"start": v(-322.08, 126.92) * mm, "end": v(-321.6, 126.92) * mm});
            skLineSegment(sketch, "E4018", {"start": v(-321.6, 126.92) * mm, "end": v(-321.11, 126.9) * mm});
            skLineSegment(sketch, "E4019", {"start": v(-321.11, 126.9) * mm, "end": v(-320.66, 126.9) * mm});
            skLineSegment(sketch, "E4020", {"start": v(-320.66, 126.9) * mm, "end": v(-320.21, 126.9) * mm});
            skLineSegment(sketch, "E4021", {"start": v(-320.21, 126.9) * mm, "end": v(-319.76, 126.89) * mm});
            skLineSegment(sketch, "E4022", {"start": v(-319.76, 126.89) * mm, "end": v(-319.31, 126.86) * mm});
            skLineSegment(sketch, "E4023", {"start": v(-319.31, 126.86) * mm, "end": v(-318.87, 126.82) * mm});
            skLineSegment(sketch, "E4024", {"start": v(-318.87, 126.82) * mm, "end": v(-318.42, 126.78) * mm});
            skLineSegment(sketch, "E4025", {"start": v(-318.42, 126.78) * mm, "end": v(-317.98, 126.72) * mm});
            skLineSegment(sketch, "E4026", {"start": v(-317.98, 126.72) * mm, "end": v(-317.54, 126.64) * mm});
            skLineSegment(sketch, "E4027", {"start": v(-317.54, 126.64) * mm, "end": v(-317.1, 126.56) * mm});
            skLineSegment(sketch, "E4028", {"start": v(-317.1, 126.56) * mm, "end": v(-316.67, 126.47) * mm});
            skLineSegment(sketch, "E4029", {"start": v(-316.67, 126.47) * mm, "end": v(-316.24, 126.37) * mm});
            skLineSegment(sketch, "E4030", {"start": v(-316.24, 126.37) * mm, "end": v(-315.8, 126.25) * mm});
            skLineSegment(sketch, "E4031", {"start": v(-315.8, 126.25) * mm, "end": v(-315.38, 126.13) * mm});
            skLineSegment(sketch, "E4032", {"start": v(-315.38, 126.13) * mm, "end": v(-314.96, 126) * mm});
            skLineSegment(sketch, "E4033", {"start": v(-314.96, 126) * mm, "end": v(-314.54, 125.85) * mm});
            skLineSegment(sketch, "E4034", {"start": v(-314.54, 125.85) * mm, "end": v(-314.12, 125.7) * mm});
            skLineSegment(sketch, "E4035", {"start": v(-314.12, 125.7) * mm, "end": v(-313.71, 125.52) * mm});
            skLineSegment(sketch, "E4036", {"start": v(-313.71, 125.52) * mm, "end": v(-313.3, 125.35) * mm});
            skLineSegment(sketch, "E4037", {"start": v(-313.3, 125.35) * mm, "end": v(-312.9, 125.16) * mm});
            skLineSegment(sketch, "E4038", {"start": v(-312.9, 125.16) * mm, "end": v(-312.5, 124.97) * mm});
            skLineSegment(sketch, "E4039", {"start": v(-312.5, 124.97) * mm, "end": v(-312.11, 124.76) * mm});
            skLineSegment(sketch, "E4040", {"start": v(-312.11, 124.76) * mm, "end": v(-311.72, 124.54) * mm});
            skLineSegment(sketch, "E4041", {"start": v(-311.72, 124.54) * mm, "end": v(-311.34, 124.32) * mm});
            skLineSegment(sketch, "E4042", {"start": v(-311.34, 124.32) * mm, "end": v(-310.96, 124.08) * mm});
            skLineSegment(sketch, "E4043", {"start": v(-310.96, 124.08) * mm, "end": v(-310.59, 123.84) * mm});
            skLineSegment(sketch, "E4044", {"start": v(-310.59, 123.84) * mm, "end": v(-310.22, 123.58) * mm});
            skLineSegment(sketch, "E4045", {"start": v(-310.22, 123.58) * mm, "end": v(-309.86, 123.32) * mm});
            skLineSegment(sketch, "E4046", {"start": v(-309.86, 123.32) * mm, "end": v(-309.5, 123.04) * mm});
            skLineSegment(sketch, "E4047", {"start": v(-309.5, 123.04) * mm, "end": v(-309.16, 122.76) * mm});
            skLineSegment(sketch, "E4048", {"start": v(-309.16, 122.76) * mm, "end": v(-308.82, 122.47) * mm});
            skLineSegment(sketch, "E4049", {"start": v(-308.82, 122.47) * mm, "end": v(-308.48, 122.17) * mm});
            skLineSegment(sketch, "E4050", {"start": v(-308.48, 122.17) * mm, "end": v(-308.16, 121.86) * mm});
            skLineSegment(sketch, "E4051", {"start": v(-308.16, 121.86) * mm, "end": v(-307.9, 121.6) * mm});
            skLineSegment(sketch, "E4052", {"start": v(-307.9, 121.6) * mm, "end": v(-307.66, 121.34) * mm});
            skLineSegment(sketch, "E4053", {"start": v(-307.66, 121.34) * mm, "end": v(-307.42, 121.07) * mm});
            skLineSegment(sketch, "E4054", {"start": v(-307.42, 121.07) * mm, "end": v(-307.18, 120.8) * mm});
            skLineSegment(sketch, "E4055", {"start": v(-307.18, 120.8) * mm, "end": v(-306.96, 120.52) * mm});
            skLineSegment(sketch, "E4056", {"start": v(-306.96, 120.52) * mm, "end": v(-306.74, 120.23) * mm});
            skLineSegment(sketch, "E4057", {"start": v(-306.74, 120.23) * mm, "end": v(-306.53, 119.94) * mm});
            skLineSegment(sketch, "E4058", {"start": v(-306.53, 119.94) * mm, "end": v(-306.32, 119.65) * mm});
            skLineSegment(sketch, "E4059", {"start": v(-306.32, 119.65) * mm, "end": v(-306.13, 119.35) * mm});
            skLineSegment(sketch, "E4060", {"start": v(-306.13, 119.35) * mm, "end": v(-305.94, 119.04) * mm});
            skLineSegment(sketch, "E4061", {"start": v(-305.94, 119.04) * mm, "end": v(-305.76, 118.74) * mm});
            skLineSegment(sketch, "E4062", {"start": v(-305.76, 118.74) * mm, "end": v(-305.58, 118.42) * mm});
            skLineSegment(sketch, "E4063", {"start": v(-305.58, 118.42) * mm, "end": v(-305.42, 118.1) * mm});
            skLineSegment(sketch, "E4064", {"start": v(-305.42, 118.1) * mm, "end": v(-305.26, 117.79) * mm});
            skLineSegment(sketch, "E4065", {"start": v(-305.26, 117.79) * mm, "end": v(-305.11, 117.46) * mm});
            skLineSegment(sketch, "E4066", {"start": v(-305.11, 117.46) * mm, "end": v(-304.97, 117.13) * mm});
            skLineSegment(sketch, "E4067", {"start": v(-304.97, 117.13) * mm, "end": v(-304.84, 116.8) * mm});
            skLineSegment(sketch, "E4068", {"start": v(-304.84, 116.8) * mm, "end": v(-304.72, 116.47) * mm});
            skLineSegment(sketch, "E4069", {"start": v(-304.72, 116.47) * mm, "end": v(-304.6, 116.13) * mm});
            skLineSegment(sketch, "E4070", {"start": v(-304.6, 116.13) * mm, "end": v(-304.5, 115.8) * mm});
            skLineSegment(sketch, "E4071", {"start": v(-304.5, 115.8) * mm, "end": v(-304.4, 115.45) * mm});
            skLineSegment(sketch, "E4072", {"start": v(-304.4, 115.45) * mm, "end": v(-304.3, 115.1) * mm});
            skLineSegment(sketch, "E4073", {"start": v(-304.3, 115.1) * mm, "end": v(-304.22, 114.75) * mm});
            skLineSegment(sketch, "E4074", {"start": v(-304.22, 114.75) * mm, "end": v(-304.14, 114.4) * mm});
            skLineSegment(sketch, "E4075", {"start": v(-304.14, 114.4) * mm, "end": v(-304.08, 114.05) * mm});
            skLineSegment(sketch, "E4076", {"start": v(-304.08, 114.05) * mm, "end": v(-304.02, 113.7) * mm});
            skLineSegment(sketch, "E4077", {"start": v(-304.02, 113.7) * mm, "end": v(-303.97, 113.34) * mm});
            skLineSegment(sketch, "E4078", {"start": v(-303.97, 113.34) * mm, "end": v(-303.94, 112.99) * mm});
            skLineSegment(sketch, "E4079", {"start": v(-303.94, 112.99) * mm, "end": v(-303.9, 112.63) * mm});
            skLineSegment(sketch, "E4080", {"start": v(-303.9, 112.63) * mm, "end": v(-303.89, 112.27) * mm});
            skLineSegment(sketch, "E4081", {"start": v(-303.89, 112.27) * mm, "end": v(-303.87, 111.9) * mm});
            skLineSegment(sketch, "E4082", {"start": v(-303.87, 111.9) * mm, "end": v(-303.87, 111.54) * mm});
            skLineSegment(sketch, "E4083", {"start": v(-303.87, 150.26) * mm, "end": v(-303.87, 149.9) * mm});
            skLineSegment(sketch, "E4084", {"start": v(-303.87, 149.9) * mm, "end": v(-303.88, 149.52) * mm});
            skLineSegment(sketch, "E4085", {"start": v(-303.88, 149.52) * mm, "end": v(-303.9, 149.16) * mm});
            skLineSegment(sketch, "E4086", {"start": v(-303.9, 149.16) * mm, "end": v(-303.92, 148.8) * mm});
            skLineSegment(sketch, "E4087", {"start": v(-303.92, 148.8) * mm, "end": v(-303.95, 148.43) * mm});
            skLineSegment(sketch, "E4088", {"start": v(-303.95, 148.43) * mm, "end": v(-304, 148.07) * mm});
            skLineSegment(sketch, "E4089", {"start": v(-304, 148.07) * mm, "end": v(-304.04, 147.7) * mm});
            skLineSegment(sketch, "E4090", {"start": v(-304.04, 147.7) * mm, "end": v(-304.1, 147.35) * mm});
            skLineSegment(sketch, "E4091", {"start": v(-304.1, 147.35) * mm, "end": v(-304.17, 147) * mm});
            skLineSegment(sketch, "E4092", {"start": v(-304.17, 147) * mm, "end": v(-304.25, 146.64) * mm});
            skLineSegment(sketch, "E4093", {"start": v(-304.25, 146.64) * mm, "end": v(-304.34, 146.29) * mm});
            skLineSegment(sketch, "E4094", {"start": v(-304.34, 146.29) * mm, "end": v(-304.44, 145.94) * mm});
            skLineSegment(sketch, "E4095", {"start": v(-304.44, 145.94) * mm, "end": v(-304.54, 145.6) * mm});
            skLineSegment(sketch, "E4096", {"start": v(-304.54, 145.6) * mm, "end": v(-304.65, 145.25) * mm});
            skLineSegment(sketch, "E4097", {"start": v(-304.65, 145.25) * mm, "end": v(-304.77, 144.9) * mm});
            skLineSegment(sketch, "E4098", {"start": v(-304.77, 144.9) * mm, "end": v(-304.9, 144.57) * mm});
            skLineSegment(sketch, "E4099", {"start": v(-304.9, 144.57) * mm, "end": v(-305.04, 144.23) * mm});
            skLineSegment(sketch, "E4100", {"start": v(-305.04, 144.23) * mm, "end": v(-305.19, 143.9) * mm});
            skLineSegment(sketch, "E4101", {"start": v(-305.19, 143.9) * mm, "end": v(-305.34, 143.58) * mm});
            skLineSegment(sketch, "E4102", {"start": v(-305.34, 143.58) * mm, "end": v(-305.5, 143.25) * mm});
            skLineSegment(sketch, "E4103", {"start": v(-305.5, 143.25) * mm, "end": v(-305.68, 142.93) * mm});
            skLineSegment(sketch, "E4104", {"start": v(-305.68, 142.93) * mm, "end": v(-305.86, 142.62) * mm});
            skLineSegment(sketch, "E4105", {"start": v(-305.86, 142.62) * mm, "end": v(-306.04, 142.3) * mm});
            skLineSegment(sketch, "E4106", {"start": v(-306.04, 142.3) * mm, "end": v(-306.24, 142) * mm});
            skLineSegment(sketch, "E4107", {"start": v(-306.24, 142) * mm, "end": v(-306.44, 141.7) * mm});
            skLineSegment(sketch, "E4108", {"start": v(-306.44, 141.7) * mm, "end": v(-306.65, 141.4) * mm});
            skLineSegment(sketch, "E4109", {"start": v(-306.65, 141.4) * mm, "end": v(-306.87, 141.1) * mm});
            skLineSegment(sketch, "E4110", {"start": v(-306.87, 141.1) * mm, "end": v(-307.1, 140.82) * mm});
            skLineSegment(sketch, "E4111", {"start": v(-307.1, 140.82) * mm, "end": v(-307.32, 140.54) * mm});
            skLineSegment(sketch, "E4112", {"start": v(-307.32, 140.54) * mm, "end": v(-307.56, 140.26) * mm});
            skLineSegment(sketch, "E4113", {"start": v(-307.56, 140.26) * mm, "end": v(-307.81, 140) * mm});
            skLineSegment(sketch, "E4114", {"start": v(-307.81, 140) * mm, "end": v(-308.07, 139.73) * mm});
            skLineSegment(sketch, "E4115", {"start": v(-308.07, 139.73) * mm, "end": v(-308.4, 139.42) * mm});
            skLineSegment(sketch, "E4116", {"start": v(-308.4, 139.42) * mm, "end": v(-308.74, 139.12) * mm});
            skLineSegment(sketch, "E4117", {"start": v(-308.74, 139.12) * mm, "end": v(-309.09, 138.84) * mm});
            skLineSegment(sketch, "E4118", {"start": v(-309.09, 138.84) * mm, "end": v(-309.44, 138.56) * mm});
            skLineSegment(sketch, "E4119", {"start": v(-309.44, 138.56) * mm, "end": v(-309.8, 138.29) * mm});
            skLineSegment(sketch, "E4120", {"start": v(-309.8, 138.29) * mm, "end": v(-310.16, 138.03) * mm});
            skLineSegment(sketch, "E4121", {"start": v(-310.16, 138.03) * mm, "end": v(-310.53, 137.78) * mm});
            skLineSegment(sketch, "E4122", {"start": v(-310.53, 137.78) * mm, "end": v(-310.91, 137.54) * mm});
            skLineSegment(sketch, "E4123", {"start": v(-310.91, 137.54) * mm, "end": v(-311.3, 137.3) * mm});
            skLineSegment(sketch, "E4124", {"start": v(-311.3, 137.3) * mm, "end": v(-311.68, 137.08) * mm});
            skLineSegment(sketch, "E4125", {"start": v(-311.68, 137.08) * mm, "end": v(-312.07, 136.87) * mm});
            skLineSegment(sketch, "E4126", {"start": v(-312.07, 136.87) * mm, "end": v(-312.47, 136.67) * mm});
            skLineSegment(sketch, "E4127", {"start": v(-312.47, 136.67) * mm, "end": v(-312.87, 136.48) * mm});
            skLineSegment(sketch, "E4128", {"start": v(-312.87, 136.48) * mm, "end": v(-313.28, 136.3) * mm});
            skLineSegment(sketch, "E4129", {"start": v(-313.28, 136.3) * mm, "end": v(-313.7, 136.12) * mm});
            skLineSegment(sketch, "E4130", {"start": v(-313.7, 136.12) * mm, "end": v(-314.1, 135.96) * mm});
            skLineSegment(sketch, "E4131", {"start": v(-314.1, 135.96) * mm, "end": v(-314.53, 135.8) * mm});
            skLineSegment(sketch, "E4132", {"start": v(-314.53, 135.8) * mm, "end": v(-314.95, 135.66) * mm});
            skLineSegment(sketch, "E4133", {"start": v(-314.95, 135.66) * mm, "end": v(-315.37, 135.53) * mm});
            skLineSegment(sketch, "E4134", {"start": v(-315.37, 135.53) * mm, "end": v(-315.8, 135.41) * mm});
            skLineSegment(sketch, "E4135", {"start": v(-315.8, 135.41) * mm, "end": v(-316.24, 135.3) * mm});
            skLineSegment(sketch, "E4136", {"start": v(-316.24, 135.3) * mm, "end": v(-316.67, 135.2) * mm});
            skLineSegment(sketch, "E4137", {"start": v(-316.67, 135.2) * mm, "end": v(-317.1, 135.11) * mm});
            skLineSegment(sketch, "E4138", {"start": v(-317.1, 135.11) * mm, "end": v(-317.55, 135.03) * mm});
            skLineSegment(sketch, "E4139", {"start": v(-317.55, 135.03) * mm, "end": v(-318, 134.97) * mm});
            skLineSegment(sketch, "E4140", {"start": v(-318, 134.97) * mm, "end": v(-318.43, 134.91) * mm});
            skLineSegment(sketch, "E4141", {"start": v(-318.43, 134.91) * mm, "end": v(-318.88, 134.86) * mm});
            skLineSegment(sketch, "E4142", {"start": v(-318.88, 134.86) * mm, "end": v(-319.33, 134.83) * mm});
            skLineSegment(sketch, "E4143", {"start": v(-319.33, 134.83) * mm, "end": v(-319.78, 134.8) * mm});
            skLineSegment(sketch, "E4144", {"start": v(-319.78, 134.8) * mm, "end": v(-320.23, 134.8) * mm});
            skLineSegment(sketch, "E4145", {"start": v(-320.23, 134.8) * mm, "end": v(-320.68, 134.8) * mm});
            skLineSegment(sketch, "E4146", {"start": v(-320.68, 134.8) * mm, "end": v(-321.13, 134.8) * mm});
            skLineSegment(sketch, "E4147", {"start": v(-321.13, 134.8) * mm, "end": v(-321.62, 134.8) * mm});
            skLineSegment(sketch, "E4148", {"start": v(-321.62, 134.8) * mm, "end": v(-322.11, 134.79) * mm});
            skLineSegment(sketch, "E4149", {"start": v(-322.11, 134.79) * mm, "end": v(-322.6, 134.8) * mm});
            skLineSegment(sketch, "E4150", {"start": v(-322.6, 134.8) * mm, "end": v(-323.09, 134.82) * mm});
            skLineSegment(sketch, "E4151", {"start": v(-323.09, 134.82) * mm, "end": v(-323.58, 134.86) * mm});
            skLineSegment(sketch, "E4152", {"start": v(-323.58, 134.86) * mm, "end": v(-324.06, 134.9) * mm});
            skLineSegment(sketch, "E4153", {"start": v(-324.06, 134.9) * mm, "end": v(-324.54, 134.97) * mm});
            skLineSegment(sketch, "E4154", {"start": v(-324.54, 134.97) * mm, "end": v(-325.02, 135.04) * mm});
            skLineSegment(sketch, "E4155", {"start": v(-325.02, 135.04) * mm, "end": v(-325.5, 135.12) * mm});
            skLineSegment(sketch, "E4156", {"start": v(-325.5, 135.12) * mm, "end": v(-325.98, 135.22) * mm});
            skLineSegment(sketch, "E4157", {"start": v(-325.98, 135.22) * mm, "end": v(-326.45, 135.32) * mm});
            skLineSegment(sketch, "E4158", {"start": v(-326.45, 135.32) * mm, "end": v(-326.92, 135.44) * mm});
            skLineSegment(sketch, "E4159", {"start": v(-326.92, 135.44) * mm, "end": v(-327.39, 135.57) * mm});
            skLineSegment(sketch, "E4160", {"start": v(-327.39, 135.57) * mm, "end": v(-327.85, 135.71) * mm});
            skLineSegment(sketch, "E4161", {"start": v(-327.85, 135.71) * mm, "end": v(-328.3, 135.87) * mm});
            skLineSegment(sketch, "E4162", {"start": v(-328.3, 135.87) * mm, "end": v(-328.76, 136.03) * mm});
            skLineSegment(sketch, "E4163", {"start": v(-328.76, 136.03) * mm, "end": v(-329.21, 136.2) * mm});
            skLineSegment(sketch, "E4164", {"start": v(-329.21, 136.2) * mm, "end": v(-329.66, 136.4) * mm});
            skLineSegment(sketch, "E4165", {"start": v(-329.66, 136.4) * mm, "end": v(-330.1, 136.6) * mm});
            skLineSegment(sketch, "E4166", {"start": v(-330.1, 136.6) * mm, "end": v(-330.54, 136.8) * mm});
            skLineSegment(sketch, "E4167", {"start": v(-330.54, 136.8) * mm, "end": v(-330.97, 137.02) * mm});
            skLineSegment(sketch, "E4168", {"start": v(-330.97, 137.02) * mm, "end": v(-331.4, 137.25) * mm});
            skLineSegment(sketch, "E4169", {"start": v(-331.4, 137.25) * mm, "end": v(-331.82, 137.5) * mm});
            skLineSegment(sketch, "E4170", {"start": v(-331.82, 137.5) * mm, "end": v(-332.23, 137.75) * mm});
            skLineSegment(sketch, "E4171", {"start": v(-332.23, 137.75) * mm, "end": v(-332.64, 138) * mm});
            skLineSegment(sketch, "E4172", {"start": v(-332.64, 138) * mm, "end": v(-333.04, 138.28) * mm});
            skLineSegment(sketch, "E4173", {"start": v(-333.04, 138.28) * mm, "end": v(-333.44, 138.56) * mm});
            skLineSegment(sketch, "E4174", {"start": v(-333.44, 138.56) * mm, "end": v(-333.83, 138.86) * mm});
            skLineSegment(sketch, "E4175", {"start": v(-333.83, 138.86) * mm, "end": v(-334.21, 139.16) * mm});
            skLineSegment(sketch, "E4176", {"start": v(-334.21, 139.16) * mm, "end": v(-334.59, 139.48) * mm});
            skLineSegment(sketch, "E4177", {"start": v(-334.59, 139.48) * mm, "end": v(-334.95, 139.8) * mm});
            skLineSegment(sketch, "E4178", {"start": v(-334.95, 139.8) * mm, "end": v(-335.31, 140.13) * mm});
            skLineSegment(sketch, "E4179", {"start": v(-335.31, 140.13) * mm, "end": v(-335.57, 140.38) * mm});
            skLineSegment(sketch, "E4180", {"start": v(-335.57, 140.38) * mm, "end": v(-335.81, 140.64) * mm});
            skLineSegment(sketch, "E4181", {"start": v(-335.81, 140.64) * mm, "end": v(-336.05, 140.9) * mm});
            skLineSegment(sketch, "E4182", {"start": v(-336.05, 140.9) * mm, "end": v(-336.29, 141.17) * mm});
            skLineSegment(sketch, "E4183", {"start": v(-336.29, 141.17) * mm, "end": v(-336.51, 141.44) * mm});
            skLineSegment(sketch, "E4184", {"start": v(-336.51, 141.44) * mm, "end": v(-336.73, 141.72) * mm});
            skLineSegment(sketch, "E4185", {"start": v(-336.73, 141.72) * mm, "end": v(-336.94, 142) * mm});
            skLineSegment(sketch, "E4186", {"start": v(-336.94, 142) * mm, "end": v(-337.14, 142.3) * mm});
            skLineSegment(sketch, "E4187", {"start": v(-337.14, 142.3) * mm, "end": v(-337.34, 142.59) * mm});
            skLineSegment(sketch, "E4188", {"start": v(-337.34, 142.59) * mm, "end": v(-337.53, 142.88) * mm});
            skLineSegment(sketch, "E4189", {"start": v(-337.53, 142.88) * mm, "end": v(-337.7, 143.19) * mm});
            skLineSegment(sketch, "E4190", {"start": v(-337.7, 143.19) * mm, "end": v(-337.88, 143.5) * mm});
            skLineSegment(sketch, "E4191", {"start": v(-337.88, 143.5) * mm, "end": v(-338.04, 143.8) * mm});
            skLineSegment(sketch, "E4192", {"start": v(-338.04, 143.8) * mm, "end": v(-338.2, 144.12) * mm});
            skLineSegment(sketch, "E4193", {"start": v(-338.2, 144.12) * mm, "end": v(-338.34, 144.44) * mm});
            skLineSegment(sketch, "E4194", {"start": v(-338.34, 144.44) * mm, "end": v(-338.48, 144.76) * mm});
            skLineSegment(sketch, "E4195", {"start": v(-338.48, 144.76) * mm, "end": v(-338.61, 145.08) * mm});
            skLineSegment(sketch, "E4196", {"start": v(-338.61, 145.08) * mm, "end": v(-338.73, 145.41) * mm});
            skLineSegment(sketch, "E4197", {"start": v(-338.73, 145.41) * mm, "end": v(-338.85, 145.75) * mm});
            skLineSegment(sketch, "E4198", {"start": v(-338.85, 145.75) * mm, "end": v(-338.95, 146.08) * mm});
            skLineSegment(sketch, "E4199", {"start": v(-338.95, 146.08) * mm, "end": v(-339.05, 146.42) * mm});
            skLineSegment(sketch, "E4200", {"start": v(-339.05, 146.42) * mm, "end": v(-339.14, 146.76) * mm});
            skLineSegment(sketch, "E4201", {"start": v(-339.14, 146.76) * mm, "end": v(-339.22, 147.1) * mm});
            skLineSegment(sketch, "E4202", {"start": v(-339.22, 147.1) * mm, "end": v(-339.3, 147.45) * mm});
            skLineSegment(sketch, "E4203", {"start": v(-339.3, 147.45) * mm, "end": v(-339.35, 147.8) * mm});
            skLineSegment(sketch, "E4204", {"start": v(-339.35, 147.8) * mm, "end": v(-339.4, 148.14) * mm});
            skLineSegment(sketch, "E4205", {"start": v(-339.4, 148.14) * mm, "end": v(-339.45, 148.5) * mm});
            skLineSegment(sketch, "E4206", {"start": v(-339.45, 148.5) * mm, "end": v(-339.49, 148.84) * mm});
            skLineSegment(sketch, "E4207", {"start": v(-339.49, 148.84) * mm, "end": v(-339.51, 149.2) * mm});
            skLineSegment(sketch, "E4208", {"start": v(-339.51, 149.2) * mm, "end": v(-339.53, 149.55) * mm});
            skLineSegment(sketch, "E4209", {"start": v(-339.53, 149.55) * mm, "end": v(-339.54, 149.9) * mm});
            skLineSegment(sketch, "E4210", {"start": v(-339.54, 149.9) * mm, "end": v(-339.54, 150.26) * mm});
            skLineSegment(sketch, "E4211", {"start": v(-339.54, 150.26) * mm, "end": v(-339.53, 150.63) * mm});
            skLineSegment(sketch, "E4212", {"start": v(-339.53, 150.63) * mm, "end": v(-339.52, 150.99) * mm});
            skLineSegment(sketch, "E4213", {"start": v(-339.52, 150.99) * mm, "end": v(-339.5, 151.35) * mm});
            skLineSegment(sketch, "E4214", {"start": v(-339.5, 151.35) * mm, "end": v(-339.47, 151.7) * mm});
            skLineSegment(sketch, "E4215", {"start": v(-339.47, 151.7) * mm, "end": v(-339.43, 152.07) * mm});
            skLineSegment(sketch, "E4216", {"start": v(-339.43, 152.07) * mm, "end": v(-339.38, 152.42) * mm});
            skLineSegment(sketch, "E4217", {"start": v(-339.38, 152.42) * mm, "end": v(-339.32, 152.78) * mm});
            skLineSegment(sketch, "E4218", {"start": v(-339.32, 152.78) * mm, "end": v(-339.25, 153.13) * mm});
            skLineSegment(sketch, "E4219", {"start": v(-339.25, 153.13) * mm, "end": v(-339.17, 153.48) * mm});
            skLineSegment(sketch, "E4220", {"start": v(-339.17, 153.48) * mm, "end": v(-339.09, 153.82) * mm});
            skLineSegment(sketch, "E4221", {"start": v(-339.09, 153.82) * mm, "end": v(-339, 154.17) * mm});
            skLineSegment(sketch, "E4222", {"start": v(-339, 154.17) * mm, "end": v(-338.9, 154.51) * mm});
            skLineSegment(sketch, "E4223", {"start": v(-338.9, 154.51) * mm, "end": v(-338.78, 154.85) * mm});
            skLineSegment(sketch, "E4224", {"start": v(-338.78, 154.85) * mm, "end": v(-338.66, 155.19) * mm});
            skLineSegment(sketch, "E4225", {"start": v(-338.66, 155.19) * mm, "end": v(-338.53, 155.52) * mm});
            skLineSegment(sketch, "E4226", {"start": v(-338.53, 155.52) * mm, "end": v(-338.4, 155.85) * mm});
            skLineSegment(sketch, "E4227", {"start": v(-338.4, 155.85) * mm, "end": v(-338.25, 156.17) * mm});
            skLineSegment(sketch, "E4228", {"start": v(-338.25, 156.17) * mm, "end": v(-338.1, 156.5) * mm});
            skLineSegment(sketch, "E4229", {"start": v(-338.1, 156.5) * mm, "end": v(-337.93, 156.81) * mm});
            skLineSegment(sketch, "E4230", {"start": v(-337.93, 156.81) * mm, "end": v(-337.76, 157.13) * mm});
            skLineSegment(sketch, "E4231", {"start": v(-337.76, 157.13) * mm, "end": v(-337.58, 157.44) * mm});
            skLineSegment(sketch, "E4232", {"start": v(-337.58, 157.44) * mm, "end": v(-337.4, 157.74) * mm});
            skLineSegment(sketch, "E4233", {"start": v(-337.4, 157.74) * mm, "end": v(-337.2, 158.04) * mm});
            skLineSegment(sketch, "E4234", {"start": v(-337.2, 158.04) * mm, "end": v(-337, 158.34) * mm});
            skLineSegment(sketch, "E4235", {"start": v(-337, 158.34) * mm, "end": v(-336.8, 158.63) * mm});
            skLineSegment(sketch, "E4236", {"start": v(-336.8, 158.63) * mm, "end": v(-336.58, 158.91) * mm});
            skLineSegment(sketch, "E4237", {"start": v(-336.58, 158.91) * mm, "end": v(-336.35, 159.2) * mm});
            skLineSegment(sketch, "E4238", {"start": v(-336.35, 159.2) * mm, "end": v(-336.12, 159.47) * mm});
            skLineSegment(sketch, "E4239", {"start": v(-336.12, 159.47) * mm, "end": v(-335.88, 159.74) * mm});
            skLineSegment(sketch, "E4240", {"start": v(-335.88, 159.74) * mm, "end": v(-335.63, 160) * mm});
            skLineSegment(sketch, "E4241", {"start": v(-335.63, 160) * mm, "end": v(-335.38, 160.26) * mm});
            skLineSegment(sketch, "E4242", {"start": v(-335.38, 160.26) * mm, "end": v(-335.12, 160.51) * mm});
            skLineSegment(sketch, "E4243", {"start": v(-335.12, 160.51) * mm, "end": v(-334.76, 160.83) * mm});
            skLineSegment(sketch, "E4244", {"start": v(-334.76, 160.83) * mm, "end": v(-334.4, 161.15) * mm});
            skLineSegment(sketch, "E4245", {"start": v(-334.4, 161.15) * mm, "end": v(-334.02, 161.45) * mm});
            skLineSegment(sketch, "E4246", {"start": v(-334.02, 161.45) * mm, "end": v(-333.64, 161.75) * mm});
            skLineSegment(sketch, "E4247", {"start": v(-333.64, 161.75) * mm, "end": v(-333.25, 162.03) * mm});
            skLineSegment(sketch, "E4248", {"start": v(-333.25, 162.03) * mm, "end": v(-332.86, 162.3) * mm});
            skLineSegment(sketch, "E4249", {"start": v(-332.86, 162.3) * mm, "end": v(-332.46, 162.57) * mm});
            skLineSegment(sketch, "E4250", {"start": v(-332.46, 162.57) * mm, "end": v(-332.06, 162.82) * mm});
            skLineSegment(sketch, "E4251", {"start": v(-332.06, 162.82) * mm, "end": v(-331.65, 163.07) * mm});
            skLineSegment(sketch, "E4252", {"start": v(-331.65, 163.07) * mm, "end": v(-331.23, 163.3) * mm});
            skLineSegment(sketch, "E4253", {"start": v(-331.23, 163.3) * mm, "end": v(-330.8, 163.52) * mm});
            skLineSegment(sketch, "E4254", {"start": v(-330.8, 163.52) * mm, "end": v(-330.38, 163.73) * mm});
            skLineSegment(sketch, "E4255", {"start": v(-330.38, 163.73) * mm, "end": v(-329.95, 163.93) * mm});
            skLineSegment(sketch, "E4256", {"start": v(-329.95, 163.93) * mm, "end": v(-329.51, 164.12) * mm});
            skLineSegment(sketch, "E4257", {"start": v(-329.51, 164.12) * mm, "end": v(-329.07, 164.3) * mm});
            skLineSegment(sketch, "E4258", {"start": v(-329.07, 164.3) * mm, "end": v(-328.63, 164.47) * mm});
            skLineSegment(sketch, "E4259", {"start": v(-328.63, 164.47) * mm, "end": v(-328.18, 164.63) * mm});
            skLineSegment(sketch, "E4260", {"start": v(-328.18, 164.63) * mm, "end": v(-327.73, 164.78) * mm});
            skLineSegment(sketch, "E4261", {"start": v(-327.73, 164.78) * mm, "end": v(-327.27, 164.91) * mm});
            skLineSegment(sketch, "E4262", {"start": v(-327.27, 164.91) * mm, "end": v(-326.8, 165.03) * mm});
            skLineSegment(sketch, "E4263", {"start": v(-326.8, 165.03) * mm, "end": v(-326.35, 165.15) * mm});
            skLineSegment(sketch, "E4264", {"start": v(-326.35, 165.15) * mm, "end": v(-325.88, 165.25) * mm});
            skLineSegment(sketch, "E4265", {"start": v(-325.88, 165.25) * mm, "end": v(-325.41, 165.34) * mm});
            skLineSegment(sketch, "E4266", {"start": v(-325.41, 165.34) * mm, "end": v(-324.94, 165.42) * mm});
            skLineSegment(sketch, "E4267", {"start": v(-324.94, 165.42) * mm, "end": v(-324.47, 165.48) * mm});
            skLineSegment(sketch, "E4268", {"start": v(-324.47, 165.48) * mm, "end": v(-324, 165.54) * mm});
            skLineSegment(sketch, "E4269", {"start": v(-324, 165.54) * mm, "end": v(-323.51, 165.58) * mm});
            skLineSegment(sketch, "E4270", {"start": v(-323.51, 165.58) * mm, "end": v(-323.04, 165.61) * mm});
            skLineSegment(sketch, "E4271", {"start": v(-323.04, 165.61) * mm, "end": v(-322.56, 165.63) * mm});
            skLineSegment(sketch, "E4272", {"start": v(-322.56, 165.63) * mm, "end": v(-322.08, 165.64) * mm});
            skLineSegment(sketch, "E4273", {"start": v(-322.08, 165.64) * mm, "end": v(-321.6, 165.63) * mm});
            skLineSegment(sketch, "E4274", {"start": v(-321.6, 165.63) * mm, "end": v(-321.11, 165.62) * mm});
            skLineSegment(sketch, "E4275", {"start": v(-321.11, 165.62) * mm, "end": v(-320.66, 165.62) * mm});
            skLineSegment(sketch, "E4276", {"start": v(-320.66, 165.62) * mm, "end": v(-320.21, 165.62) * mm});
            skLineSegment(sketch, "E4277", {"start": v(-320.21, 165.62) * mm, "end": v(-319.76, 165.6) * mm});
            skLineSegment(sketch, "E4278", {"start": v(-319.76, 165.6) * mm, "end": v(-319.31, 165.58) * mm});
            skLineSegment(sketch, "E4279", {"start": v(-319.31, 165.58) * mm, "end": v(-318.87, 165.54) * mm});
            skLineSegment(sketch, "E4280", {"start": v(-318.87, 165.54) * mm, "end": v(-318.42, 165.49) * mm});
            skLineSegment(sketch, "E4281", {"start": v(-318.42, 165.49) * mm, "end": v(-317.98, 165.43) * mm});
            skLineSegment(sketch, "E4282", {"start": v(-317.98, 165.43) * mm, "end": v(-317.54, 165.36) * mm});
            skLineSegment(sketch, "E4283", {"start": v(-317.54, 165.36) * mm, "end": v(-317.1, 165.28) * mm});
            skLineSegment(sketch, "E4284", {"start": v(-317.1, 165.28) * mm, "end": v(-316.67, 165.18) * mm});
            skLineSegment(sketch, "E4285", {"start": v(-316.67, 165.18) * mm, "end": v(-316.24, 165.08) * mm});
            skLineSegment(sketch, "E4286", {"start": v(-316.24, 165.08) * mm, "end": v(-315.8, 164.97) * mm});
            skLineSegment(sketch, "E4287", {"start": v(-315.8, 164.97) * mm, "end": v(-315.38, 164.84) * mm});
            skLineSegment(sketch, "E4288", {"start": v(-315.38, 164.84) * mm, "end": v(-314.96, 164.7) * mm});
            skLineSegment(sketch, "E4289", {"start": v(-314.96, 164.7) * mm, "end": v(-314.54, 164.56) * mm});
            skLineSegment(sketch, "E4290", {"start": v(-314.54, 164.56) * mm, "end": v(-314.12, 164.4) * mm});
            skLineSegment(sketch, "E4291", {"start": v(-314.12, 164.4) * mm, "end": v(-313.71, 164.24) * mm});
            skLineSegment(sketch, "E4292", {"start": v(-313.71, 164.24) * mm, "end": v(-313.3, 164.06) * mm});
            skLineSegment(sketch, "E4293", {"start": v(-313.3, 164.06) * mm, "end": v(-312.9, 163.88) * mm});
            skLineSegment(sketch, "E4294", {"start": v(-312.9, 163.88) * mm, "end": v(-312.5, 163.68) * mm});
            skLineSegment(sketch, "E4295", {"start": v(-312.5, 163.68) * mm, "end": v(-312.11, 163.47) * mm});
            skLineSegment(sketch, "E4296", {"start": v(-312.11, 163.47) * mm, "end": v(-311.72, 163.26) * mm});
            skLineSegment(sketch, "E4297", {"start": v(-311.72, 163.26) * mm, "end": v(-311.34, 163.03) * mm});
            skLineSegment(sketch, "E4298", {"start": v(-311.34, 163.03) * mm, "end": v(-310.96, 162.8) * mm});
            skLineSegment(sketch, "E4299", {"start": v(-310.96, 162.8) * mm, "end": v(-310.59, 162.55) * mm});
            skLineSegment(sketch, "E4300", {"start": v(-310.59, 162.55) * mm, "end": v(-310.22, 162.3) * mm});
            skLineSegment(sketch, "E4301", {"start": v(-310.22, 162.3) * mm, "end": v(-309.86, 162.03) * mm});
            skLineSegment(sketch, "E4302", {"start": v(-309.86, 162.03) * mm, "end": v(-309.5, 161.76) * mm});
            skLineSegment(sketch, "E4303", {"start": v(-309.5, 161.76) * mm, "end": v(-309.16, 161.48) * mm});
            skLineSegment(sketch, "E4304", {"start": v(-309.16, 161.48) * mm, "end": v(-308.82, 161.18) * mm});
            skLineSegment(sketch, "E4305", {"start": v(-308.82, 161.18) * mm, "end": v(-308.48, 160.88) * mm});
            skLineSegment(sketch, "E4306", {"start": v(-308.48, 160.88) * mm, "end": v(-308.16, 160.57) * mm});
            skLineSegment(sketch, "E4307", {"start": v(-308.16, 160.57) * mm, "end": v(-307.9, 160.32) * mm});
            skLineSegment(sketch, "E4308", {"start": v(-307.9, 160.32) * mm, "end": v(-307.66, 160.05) * mm});
            skLineSegment(sketch, "E4309", {"start": v(-307.66, 160.05) * mm, "end": v(-307.42, 159.78) * mm});
            skLineSegment(sketch, "E4310", {"start": v(-307.42, 159.78) * mm, "end": v(-307.18, 159.51) * mm});
            skLineSegment(sketch, "E4311", {"start": v(-307.18, 159.51) * mm, "end": v(-306.96, 159.23) * mm});
            skLineSegment(sketch, "E4312", {"start": v(-306.96, 159.23) * mm, "end": v(-306.74, 158.95) * mm});
            skLineSegment(sketch, "E4313", {"start": v(-306.74, 158.95) * mm, "end": v(-306.53, 158.66) * mm});
            skLineSegment(sketch, "E4314", {"start": v(-306.53, 158.66) * mm, "end": v(-306.32, 158.36) * mm});
            skLineSegment(sketch, "E4315", {"start": v(-306.32, 158.36) * mm, "end": v(-306.13, 158.06) * mm});
            skLineSegment(sketch, "E4316", {"start": v(-306.13, 158.06) * mm, "end": v(-305.94, 157.76) * mm});
            skLineSegment(sketch, "E4317", {"start": v(-305.94, 157.76) * mm, "end": v(-305.76, 157.45) * mm});
            skLineSegment(sketch, "E4318", {"start": v(-305.76, 157.45) * mm, "end": v(-305.58, 157.14) * mm});
            skLineSegment(sketch, "E4319", {"start": v(-305.58, 157.14) * mm, "end": v(-305.42, 156.82) * mm});
            skLineSegment(sketch, "E4320", {"start": v(-305.42, 156.82) * mm, "end": v(-305.26, 156.5) * mm});
            skLineSegment(sketch, "E4321", {"start": v(-305.26, 156.5) * mm, "end": v(-305.11, 156.18) * mm});
            skLineSegment(sketch, "E4322", {"start": v(-305.11, 156.18) * mm, "end": v(-304.97, 155.85) * mm});
            skLineSegment(sketch, "E4323", {"start": v(-304.97, 155.85) * mm, "end": v(-304.84, 155.52) * mm});
            skLineSegment(sketch, "E4324", {"start": v(-304.84, 155.52) * mm, "end": v(-304.72, 155.18) * mm});
            skLineSegment(sketch, "E4325", {"start": v(-304.72, 155.18) * mm, "end": v(-304.6, 154.85) * mm});
            skLineSegment(sketch, "E4326", {"start": v(-304.6, 154.85) * mm, "end": v(-304.5, 154.5) * mm});
            skLineSegment(sketch, "E4327", {"start": v(-304.5, 154.5) * mm, "end": v(-304.4, 154.16) * mm});
            skLineSegment(sketch, "E4328", {"start": v(-304.4, 154.16) * mm, "end": v(-304.3, 153.82) * mm});
            skLineSegment(sketch, "E4329", {"start": v(-304.3, 153.82) * mm, "end": v(-304.22, 153.47) * mm});
            skLineSegment(sketch, "E4330", {"start": v(-304.22, 153.47) * mm, "end": v(-304.14, 153.12) * mm});
            skLineSegment(sketch, "E4331", {"start": v(-304.14, 153.12) * mm, "end": v(-304.08, 152.77) * mm});
            skLineSegment(sketch, "E4332", {"start": v(-304.08, 152.77) * mm, "end": v(-304.02, 152.41) * mm});
            skLineSegment(sketch, "E4333", {"start": v(-304.02, 152.41) * mm, "end": v(-303.97, 152.06) * mm});
            skLineSegment(sketch, "E4334", {"start": v(-303.97, 152.06) * mm, "end": v(-303.94, 151.7) * mm});
            skLineSegment(sketch, "E4335", {"start": v(-303.94, 151.7) * mm, "end": v(-303.9, 151.34) * mm});
            skLineSegment(sketch, "E4336", {"start": v(-303.9, 151.34) * mm, "end": v(-303.89, 150.98) * mm});
            skLineSegment(sketch, "E4337", {"start": v(-303.89, 150.98) * mm, "end": v(-303.87, 150.62) * mm});
            skLineSegment(sketch, "E4338", {"start": v(-303.87, 150.62) * mm, "end": v(-303.87, 150.26) * mm});
            skLineSegment(sketch, "E4339", {"start": v(-304.34, 173.51) * mm, "end": v(-339.33, 173.51) * mm});
            skLineSegment(sketch, "E4340", {"start": v(-339.33, 173.51) * mm, "end": v(-339.33, 195.27) * mm});
            skLineSegment(sketch, "E4341", {"start": v(-322.61, 173.51) * mm, "end": v(-322.61, 193.7) * mm});
            skLineSegment(sketch, "E4342", {"start": v(-317.42, 202.97) * mm, "end": v(-317.42, 227.1) * mm});
            skLineSegment(sketch, "E4343", {"start": v(-304.35, 234.8) * mm, "end": v(-330.53, 234.8) * mm});
            skLineSegment(sketch, "E4344", {"start": v(-338.8, 234.8) * mm, "end": v(-339.25, 234.8) * mm});
            skLineSegment(sketch, "E4345", {"start": v(-304.35, 242.5) * mm, "end": v(-330.59, 242.5) * mm});
            skLineSegment(sketch, "E4346", {"start": v(-320.33, 242.5) * mm, "end": v(-320.9, 242.52) * mm});
            skLineSegment(sketch, "E4347", {"start": v(-320.9, 242.52) * mm, "end": v(-321.48, 242.56) * mm});
            skLineSegment(sketch, "E4348", {"start": v(-321.48, 242.56) * mm, "end": v(-322.04, 242.63) * mm});
            skLineSegment(sketch, "E4349", {"start": v(-322.04, 242.63) * mm, "end": v(-322.6, 242.74) * mm});
            skLineSegment(sketch, "E4350", {"start": v(-322.6, 242.74) * mm, "end": v(-323.15, 242.86) * mm});
            skLineSegment(sketch, "E4351", {"start": v(-323.15, 242.86) * mm, "end": v(-323.7, 243.02) * mm});
            skLineSegment(sketch, "E4352", {"start": v(-323.7, 243.02) * mm, "end": v(-324.23, 243.2) * mm});
            skLineSegment(sketch, "E4353", {"start": v(-324.23, 243.2) * mm, "end": v(-324.76, 243.41) * mm});
            skLineSegment(sketch, "E4354", {"start": v(-324.76, 243.41) * mm, "end": v(-325.27, 243.65) * mm});
            skLineSegment(sketch, "E4355", {"start": v(-325.27, 243.65) * mm, "end": v(-325.77, 243.9) * mm});
            skLineSegment(sketch, "E4356", {"start": v(-325.77, 243.9) * mm, "end": v(-326.26, 244.2) * mm});
            skLineSegment(sketch, "E4357", {"start": v(-326.26, 244.2) * mm, "end": v(-326.74, 244.5) * mm});
            skLineSegment(sketch, "E4358", {"start": v(-326.74, 244.5) * mm, "end": v(-327.2, 244.84) * mm});
            skLineSegment(sketch, "E4359", {"start": v(-327.2, 244.84) * mm, "end": v(-327.64, 245.2) * mm});
            skLineSegment(sketch, "E4360", {"start": v(-327.64, 245.2) * mm, "end": v(-328.07, 245.57) * mm});
            skLineSegment(sketch, "E4361", {"start": v(-328.07, 245.57) * mm, "end": v(-328.47, 245.98) * mm});
            skLineSegment(sketch, "E4362", {"start": v(-328.47, 245.98) * mm, "end": v(-328.8, 246.33) * mm});
            skLineSegment(sketch, "E4363", {"start": v(-328.8, 246.33) * mm, "end": v(-329.12, 246.7) * mm});
            skLineSegment(sketch, "E4364", {"start": v(-329.12, 246.7) * mm, "end": v(-329.4, 247.08) * mm});
            skLineSegment(sketch, "E4365", {"start": v(-329.4, 247.08) * mm, "end": v(-329.68, 247.48) * mm});
            skLineSegment(sketch, "E4366", {"start": v(-329.68, 247.48) * mm, "end": v(-329.93, 247.89) * mm});
            skLineSegment(sketch, "E4367", {"start": v(-329.93, 247.89) * mm, "end": v(-330.16, 248.3) * mm});
            skLineSegment(sketch, "E4368", {"start": v(-330.16, 248.3) * mm, "end": v(-330.36, 248.74) * mm});
            skLineSegment(sketch, "E4369", {"start": v(-330.36, 248.74) * mm, "end": v(-330.55, 249.18) * mm});
            skLineSegment(sketch, "E4370", {"start": v(-330.55, 249.18) * mm, "end": v(-330.72, 249.62) * mm});
            skLineSegment(sketch, "E4371", {"start": v(-330.72, 249.62) * mm, "end": v(-330.86, 250.08) * mm});
            skLineSegment(sketch, "E4372", {"start": v(-330.86, 250.08) * mm, "end": v(-330.98, 250.54) * mm});
            skLineSegment(sketch, "E4373", {"start": v(-330.98, 250.54) * mm, "end": v(-331.07, 251.01) * mm});
            skLineSegment(sketch, "E4374", {"start": v(-331.07, 251.01) * mm, "end": v(-331.15, 251.48) * mm});
            skLineSegment(sketch, "E4375", {"start": v(-331.15, 251.48) * mm, "end": v(-331.2, 251.96) * mm});
            skLineSegment(sketch, "E4376", {"start": v(-331.2, 251.96) * mm, "end": v(-331.22, 252.44) * mm});
            skLineSegment(sketch, "E4377", {"start": v(-331.22, 252.44) * mm, "end": v(-331.22, 252.93) * mm});
            skLineSegment(sketch, "E4378", {"start": v(-331.22, 252.93) * mm, "end": v(-331.25, 253.4) * mm});
            skLineSegment(sketch, "E4379", {"start": v(-331.25, 253.4) * mm, "end": v(-331.26, 253.85) * mm});
            skLineSegment(sketch, "E4380", {"start": v(-331.26, 253.85) * mm, "end": v(-331.24, 254.31) * mm});
            skLineSegment(sketch, "E4381", {"start": v(-331.24, 254.31) * mm, "end": v(-331.2, 254.77) * mm});
            skLineSegment(sketch, "E4382", {"start": v(-331.2, 254.77) * mm, "end": v(-331.13, 255.22) * mm});
            skLineSegment(sketch, "E4383", {"start": v(-331.13, 255.22) * mm, "end": v(-331.04, 255.67) * mm});
            skLineSegment(sketch, "E4384", {"start": v(-331.04, 255.67) * mm, "end": v(-330.93, 256.1) * mm});
            skLineSegment(sketch, "E4385", {"start": v(-330.93, 256.1) * mm, "end": v(-330.8, 256.55) * mm});
            skLineSegment(sketch, "E4386", {"start": v(-330.8, 256.55) * mm, "end": v(-330.64, 256.97) * mm});
            skLineSegment(sketch, "E4387", {"start": v(-330.64, 256.97) * mm, "end": v(-330.46, 257.4) * mm});
            skLineSegment(sketch, "E4388", {"start": v(-330.46, 257.4) * mm, "end": v(-330.26, 257.8) * mm});
            skLineSegment(sketch, "E4389", {"start": v(-330.26, 257.8) * mm, "end": v(-330.04, 258.2) * mm});
            skLineSegment(sketch, "E4390", {"start": v(-330.04, 258.2) * mm, "end": v(-329.8, 258.6) * mm});
            skLineSegment(sketch, "E4391", {"start": v(-329.8, 258.6) * mm, "end": v(-329.53, 258.97) * mm});
            skLineSegment(sketch, "E4392", {"start": v(-329.53, 258.97) * mm, "end": v(-329.25, 259.33) * mm});
            skLineSegment(sketch, "E4393", {"start": v(-329.25, 259.33) * mm, "end": v(-328.95, 259.68) * mm});
            skLineSegment(sketch, "E4394", {"start": v(-328.95, 259.68) * mm, "end": v(-328.7, 259.9) * mm});
            skLineSegment(sketch, "E4395", {"start": v(-328.7, 259.9) * mm, "end": v(-328.43, 260.1) * mm});
            skLineSegment(sketch, "E4396", {"start": v(-328.43, 260.1) * mm, "end": v(-328.16, 260.29) * mm});
            skLineSegment(sketch, "E4397", {"start": v(-328.16, 260.29) * mm, "end": v(-327.88, 260.46) * mm});
            skLineSegment(sketch, "E4398", {"start": v(-327.88, 260.46) * mm, "end": v(-327.59, 260.62) * mm});
            skLineSegment(sketch, "E4399", {"start": v(-327.59, 260.62) * mm, "end": v(-327.3, 260.77) * mm});
            skLineSegment(sketch, "E4400", {"start": v(-327.3, 260.77) * mm, "end": v(-327, 260.9) * mm});
            skLineSegment(sketch, "E4401", {"start": v(-327, 260.9) * mm, "end": v(-326.69, 261.02) * mm});
            skLineSegment(sketch, "E4402", {"start": v(-326.69, 261.02) * mm, "end": v(-326.38, 261.13) * mm});
            skLineSegment(sketch, "E4403", {"start": v(-326.38, 261.13) * mm, "end": v(-326.06, 261.22) * mm});
            skLineSegment(sketch, "E4404", {"start": v(-326.06, 261.22) * mm, "end": v(-325.74, 261.3) * mm});
            skLineSegment(sketch, "E4405", {"start": v(-325.74, 261.3) * mm, "end": v(-325.42, 261.36) * mm});
            skLineSegment(sketch, "E4406", {"start": v(-325.42, 261.36) * mm, "end": v(-325.1, 261.4) * mm});
            skLineSegment(sketch, "E4407", {"start": v(-325.1, 261.4) * mm, "end": v(-324.76, 261.44) * mm});
            skLineSegment(sketch, "E4408", {"start": v(-324.76, 261.44) * mm, "end": v(-324.43, 261.45) * mm});
            skLineSegment(sketch, "E4409", {"start": v(-324.43, 261.45) * mm, "end": v(-324.1, 261.45) * mm});
            skLineSegment(sketch, "E4410", {"start": v(-324.1, 261.45) * mm, "end": v(-304.35, 261.45) * mm});
            skLineSegment(sketch, "E4411", {"start": v(-481.6, 65.34) * mm, "end": v(-516.57, 65.34) * mm});
            skLineSegment(sketch, "E4412", {"start": v(-516.57, 65.34) * mm, "end": v(-516.57, 80.7) * mm});
            skLineSegment(sketch, "E4413", {"start": v(-516.57, 80.7) * mm, "end": v(-516.57, 81.13) * mm});
            skLineSegment(sketch, "E4414", {"start": v(-516.57, 81.13) * mm, "end": v(-516.54, 81.56) * mm});
            skLineSegment(sketch, "E4415", {"start": v(-516.54, 81.56) * mm, "end": v(-516.5, 82) * mm});
            skLineSegment(sketch, "E4416", {"start": v(-516.5, 82) * mm, "end": v(-516.43, 82.41) * mm});
            skLineSegment(sketch, "E4417", {"start": v(-516.43, 82.41) * mm, "end": v(-516.34, 82.83) * mm});
            skLineSegment(sketch, "E4418", {"start": v(-516.34, 82.83) * mm, "end": v(-516.22, 83.24) * mm});
            skLineSegment(sketch, "E4419", {"start": v(-516.22, 83.24) * mm, "end": v(-516.1, 83.65) * mm});
            skLineSegment(sketch, "E4420", {"start": v(-516.1, 83.65) * mm, "end": v(-515.94, 84.05) * mm});
            skLineSegment(sketch, "E4421", {"start": v(-515.94, 84.05) * mm, "end": v(-515.77, 84.44) * mm});
            skLineSegment(sketch, "E4422", {"start": v(-515.77, 84.44) * mm, "end": v(-515.58, 84.82) * mm});
            skLineSegment(sketch, "E4423", {"start": v(-515.58, 84.82) * mm, "end": v(-515.36, 85.19) * mm});
            skLineSegment(sketch, "E4424", {"start": v(-515.36, 85.19) * mm, "end": v(-515.13, 85.55) * mm});
            skLineSegment(sketch, "E4425", {"start": v(-515.13, 85.55) * mm, "end": v(-514.89, 85.9) * mm});
            skLineSegment(sketch, "E4426", {"start": v(-514.89, 85.9) * mm, "end": v(-514.62, 86.23) * mm});
            skLineSegment(sketch, "E4427", {"start": v(-514.62, 86.23) * mm, "end": v(-514.33, 86.55) * mm});
            skLineSegment(sketch, "E4428", {"start": v(-514.33, 86.55) * mm, "end": v(-514.03, 86.86) * mm});
            skLineSegment(sketch, "E4429", {"start": v(-514.03, 86.86) * mm, "end": v(-513.72, 87.16) * mm});
            skLineSegment(sketch, "E4430", {"start": v(-513.72, 87.16) * mm, "end": v(-513.4, 87.44) * mm});
            skLineSegment(sketch, "E4431", {"start": v(-513.4, 87.44) * mm, "end": v(-513.07, 87.7) * mm});
            skLineSegment(sketch, "E4432", {"start": v(-513.07, 87.7) * mm, "end": v(-512.72, 87.95) * mm});
            skLineSegment(sketch, "E4433", {"start": v(-512.72, 87.95) * mm, "end": v(-512.37, 88.18) * mm});
            skLineSegment(sketch, "E4434", {"start": v(-512.37, 88.18) * mm, "end": v(-512, 88.4) * mm});
            skLineSegment(sketch, "E4435", {"start": v(-512, 88.4) * mm, "end": v(-511.62, 88.58) * mm});
            skLineSegment(sketch, "E4436", {"start": v(-511.62, 88.58) * mm, "end": v(-511.24, 88.75) * mm});
            skLineSegment(sketch, "E4437", {"start": v(-511.24, 88.75) * mm, "end": v(-510.84, 88.9) * mm});
            skLineSegment(sketch, "E4438", {"start": v(-510.84, 88.9) * mm, "end": v(-510.44, 89.04) * mm});
            skLineSegment(sketch, "E4439", {"start": v(-510.44, 89.04) * mm, "end": v(-510.03, 89.16) * mm});
            skLineSegment(sketch, "E4440", {"start": v(-510.03, 89.16) * mm, "end": v(-509.62, 89.25) * mm});
            skLineSegment(sketch, "E4441", {"start": v(-509.62, 89.25) * mm, "end": v(-509.2, 89.32) * mm});
            skLineSegment(sketch, "E4442", {"start": v(-509.2, 89.32) * mm, "end": v(-508.78, 89.37) * mm});
            skLineSegment(sketch, "E4443", {"start": v(-508.78, 89.37) * mm, "end": v(-508.36, 89.4) * mm});
            skLineSegment(sketch, "E4444", {"start": v(-508.36, 89.4) * mm, "end": v(-507.93, 89.42) * mm});
            skLineSegment(sketch, "E4445", {"start": v(-507.93, 89.42) * mm, "end": v(-507.49, 89.42) * mm});
            skLineSegment(sketch, "E4446", {"start": v(-507.49, 89.42) * mm, "end": v(-507.05, 89.4) * mm});
            skLineSegment(sketch, "E4447", {"start": v(-507.05, 89.4) * mm, "end": v(-506.62, 89.36) * mm});
            skLineSegment(sketch, "E4448", {"start": v(-506.62, 89.36) * mm, "end": v(-506.19, 89.3) * mm});
            skLineSegment(sketch, "E4449", {"start": v(-506.19, 89.3) * mm, "end": v(-505.76, 89.2) * mm});
            skLineSegment(sketch, "E4450", {"start": v(-505.76, 89.2) * mm, "end": v(-505.34, 89.1) * mm});
            skLineSegment(sketch, "E4451", {"start": v(-505.34, 89.1) * mm, "end": v(-504.93, 88.97) * mm});
            skLineSegment(sketch, "E4452", {"start": v(-504.93, 88.97) * mm, "end": v(-504.52, 88.82) * mm});
            skLineSegment(sketch, "E4453", {"start": v(-504.52, 88.82) * mm, "end": v(-504.13, 88.65) * mm});
            skLineSegment(sketch, "E4454", {"start": v(-504.13, 88.65) * mm, "end": v(-503.74, 88.47) * mm});
            skLineSegment(sketch, "E4455", {"start": v(-503.74, 88.47) * mm, "end": v(-503.36, 88.26) * mm});
            skLineSegment(sketch, "E4456", {"start": v(-503.36, 88.26) * mm, "end": v(-502.99, 88.03) * mm});
            skLineSegment(sketch, "E4457", {"start": v(-502.99, 88.03) * mm, "end": v(-502.63, 87.78) * mm});
            skLineSegment(sketch, "E4458", {"start": v(-502.63, 87.78) * mm, "end": v(-502.28, 87.52) * mm});
            skLineSegment(sketch, "E4459", {"start": v(-502.28, 87.52) * mm, "end": v(-501.95, 87.23) * mm});
            skLineSegment(sketch, "E4460", {"start": v(-501.95, 87.23) * mm, "end": v(-501.63, 86.93) * mm});
            skLineSegment(sketch, "E4461", {"start": v(-501.63, 86.93) * mm, "end": v(-501.33, 86.62) * mm});
            skLineSegment(sketch, "E4462", {"start": v(-501.33, 86.62) * mm, "end": v(-501.05, 86.29) * mm});
            skLineSegment(sketch, "E4463", {"start": v(-501.05, 86.29) * mm, "end": v(-500.78, 85.95) * mm});
            skLineSegment(sketch, "E4464", {"start": v(-500.78, 85.95) * mm, "end": v(-500.53, 85.6) * mm});
            skLineSegment(sketch, "E4465", {"start": v(-500.53, 85.6) * mm, "end": v(-500.3, 85.23) * mm});
            skLineSegment(sketch, "E4466", {"start": v(-500.3, 85.23) * mm, "end": v(-500.1, 84.85) * mm});
            skLineSegment(sketch, "E4467", {"start": v(-500.1, 84.85) * mm, "end": v(-499.9, 84.47) * mm});
            skLineSegment(sketch, "E4468", {"start": v(-499.9, 84.47) * mm, "end": v(-499.73, 84.07) * mm});
            skLineSegment(sketch, "E4469", {"start": v(-499.73, 84.07) * mm, "end": v(-499.58, 83.67) * mm});
            skLineSegment(sketch, "E4470", {"start": v(-499.58, 83.67) * mm, "end": v(-499.45, 83.26) * mm});
            skLineSegment(sketch, "E4471", {"start": v(-499.45, 83.26) * mm, "end": v(-499.34, 82.85) * mm});
            skLineSegment(sketch, "E4472", {"start": v(-499.34, 82.85) * mm, "end": v(-499.25, 82.43) * mm});
            skLineSegment(sketch, "E4473", {"start": v(-499.25, 82.43) * mm, "end": v(-499.18, 82) * mm});
            skLineSegment(sketch, "E4474", {"start": v(-499.18, 82) * mm, "end": v(-499.13, 81.57) * mm});
            skLineSegment(sketch, "E4475", {"start": v(-499.13, 81.57) * mm, "end": v(-499.1, 81.14) * mm});
            skLineSegment(sketch, "E4476", {"start": v(-499.1, 81.14) * mm, "end": v(-499.1, 80.7) * mm});
            skLineSegment(sketch, "E4477", {"start": v(-499.1, 80.7) * mm, "end": v(-499.1, 65.34) * mm});
            skLineSegment(sketch, "E4478", {"start": v(-499.1, 80.7) * mm, "end": v(-499.1, 81.06) * mm});
            skLineSegment(sketch, "E4479", {"start": v(-499.1, 81.06) * mm, "end": v(-499.07, 81.42) * mm});
            skLineSegment(sketch, "E4480", {"start": v(-499.07, 81.42) * mm, "end": v(-499.04, 81.77) * mm});
            skLineSegment(sketch, "E4481", {"start": v(-499.04, 81.77) * mm, "end": v(-498.98, 82.12) * mm});
            skLineSegment(sketch, "E4482", {"start": v(-498.98, 82.12) * mm, "end": v(-498.9, 82.47) * mm});
            skLineSegment(sketch, "E4483", {"start": v(-498.9, 82.47) * mm, "end": v(-498.82, 82.8) * mm});
            skLineSegment(sketch, "E4484", {"start": v(-498.82, 82.8) * mm, "end": v(-498.7, 83.15) * mm});
            skLineSegment(sketch, "E4485", {"start": v(-498.7, 83.15) * mm, "end": v(-498.58, 83.48) * mm});
            skLineSegment(sketch, "E4486", {"start": v(-498.58, 83.48) * mm, "end": v(-498.44, 83.8) * mm});
            skLineSegment(sketch, "E4487", {"start": v(-498.44, 83.8) * mm, "end": v(-498.28, 84.12) * mm});
            skLineSegment(sketch, "E4488", {"start": v(-498.28, 84.12) * mm, "end": v(-498.1, 84.42) * mm});
            skLineSegment(sketch, "E4489", {"start": v(-498.1, 84.42) * mm, "end": v(-497.92, 84.72) * mm});
            skLineSegment(sketch, "E4490", {"start": v(-497.92, 84.72) * mm, "end": v(-497.71, 85.01) * mm});
            skLineSegment(sketch, "E4491", {"start": v(-497.71, 85.01) * mm, "end": v(-497.5, 85.3) * mm});
            skLineSegment(sketch, "E4492", {"start": v(-497.5, 85.3) * mm, "end": v(-497.26, 85.56) * mm});
            skLineSegment(sketch, "E4493", {"start": v(-497.26, 85.56) * mm, "end": v(-497.01, 85.82) * mm});
            skLineSegment(sketch, "E4494", {"start": v(-497.01, 85.82) * mm, "end": v(-496.57, 86.12) * mm});
            skLineSegment(sketch, "E4495", {"start": v(-496.57, 86.12) * mm, "end": v(-496.12, 86.4) * mm});
            skLineSegment(sketch, "E4496", {"start": v(-496.12, 86.4) * mm, "end": v(-495.66, 86.65) * mm});
            skLineSegment(sketch, "E4497", {"start": v(-495.66, 86.65) * mm, "end": v(-495.2, 86.89) * mm});
            skLineSegment(sketch, "E4498", {"start": v(-495.2, 86.89) * mm, "end": v(-494.72, 87.1) * mm});
            skLineSegment(sketch, "E4499", {"start": v(-494.72, 87.1) * mm, "end": v(-494.23, 87.3) * mm});
            skLineSegment(sketch, "E4500", {"start": v(-494.23, 87.3) * mm, "end": v(-493.73, 87.46) * mm});
            skLineSegment(sketch, "E4501", {"start": v(-493.73, 87.46) * mm, "end": v(-493.23, 87.61) * mm});
            skLineSegment(sketch, "E4502", {"start": v(-493.23, 87.61) * mm, "end": v(-492.72, 87.74) * mm});
            skLineSegment(sketch, "E4503", {"start": v(-492.72, 87.74) * mm, "end": v(-492.2, 87.84) * mm});
            skLineSegment(sketch, "E4504", {"start": v(-492.2, 87.84) * mm, "end": v(-491.69, 87.92) * mm});
            skLineSegment(sketch, "E4505", {"start": v(-491.69, 87.92) * mm, "end": v(-491.17, 87.98) * mm});
            skLineSegment(sketch, "E4506", {"start": v(-491.17, 87.98) * mm, "end": v(-490.64, 88.01) * mm});
            skLineSegment(sketch, "E4507", {"start": v(-490.64, 88.01) * mm, "end": v(-490.12, 88.02) * mm});
            skLineSegment(sketch, "E4508", {"start": v(-490.12, 88.02) * mm, "end": v(-489.59, 88.01) * mm});
            skLineSegment(sketch, "E4509", {"start": v(-489.59, 88.01) * mm, "end": v(-489.06, 87.97) * mm});
            skLineSegment(sketch, "E4510", {"start": v(-489.06, 87.97) * mm, "end": v(-488.59, 87.97) * mm});
            skLineSegment(sketch, "E4511", {"start": v(-488.59, 87.97) * mm, "end": v(-488.12, 87.97) * mm});
            skLineSegment(sketch, "E4512", {"start": v(-488.12, 87.97) * mm, "end": v(-487.65, 87.98) * mm});
            skLineSegment(sketch, "E4513", {"start": v(-487.65, 87.98) * mm, "end": v(-487.18, 88) * mm});
            skLineSegment(sketch, "E4514", {"start": v(-487.18, 88) * mm, "end": v(-486.7, 88.02) * mm});
            skLineSegment(sketch, "E4515", {"start": v(-486.7, 88.02) * mm, "end": v(-486.24, 88.06) * mm});
            skLineSegment(sketch, "E4516", {"start": v(-486.24, 88.06) * mm, "end": v(-485.77, 88.1) * mm});
            skLineSegment(sketch, "E4517", {"start": v(-485.77, 88.1) * mm, "end": v(-485.3, 88.16) * mm});
            skLineSegment(sketch, "E4518", {"start": v(-485.3, 88.16) * mm, "end": v(-484.83, 88.22) * mm});
            skLineSegment(sketch, "E4519", {"start": v(-484.83, 88.22) * mm, "end": v(-484.37, 88.29) * mm});
            skLineSegment(sketch, "E4520", {"start": v(-484.37, 88.29) * mm, "end": v(-483.9, 88.36) * mm});
            skLineSegment(sketch, "E4521", {"start": v(-483.9, 88.36) * mm, "end": v(-483.44, 88.45) * mm});
            skLineSegment(sketch, "E4522", {"start": v(-483.44, 88.45) * mm, "end": v(-482.98, 88.54) * mm});
            skLineSegment(sketch, "E4523", {"start": v(-482.98, 88.54) * mm, "end": v(-482.52, 88.65) * mm});
            skLineSegment(sketch, "E4524", {"start": v(-482.52, 88.65) * mm, "end": v(-482.06, 88.76) * mm});
            skLineSegment(sketch, "E4525", {"start": v(-482.06, 88.76) * mm, "end": v(-481.6, 88.88) * mm});
            skLineSegment(sketch, "E4526", {"start": v(-481.12, 111.54) * mm, "end": v(-481.11, 111.18) * mm});
            skLineSegment(sketch, "E4527", {"start": v(-481.11, 111.18) * mm, "end": v(-481.12, 110.8) * mm});
            skLineSegment(sketch, "E4528", {"start": v(-481.12, 110.8) * mm, "end": v(-481.13, 110.44) * mm});
            skLineSegment(sketch, "E4529", {"start": v(-481.13, 110.44) * mm, "end": v(-481.16, 110.08) * mm});
            skLineSegment(sketch, "E4530", {"start": v(-481.16, 110.08) * mm, "end": v(-481.2, 109.72) * mm});
            skLineSegment(sketch, "E4531", {"start": v(-481.2, 109.72) * mm, "end": v(-481.24, 109.35) * mm});
            skLineSegment(sketch, "E4532", {"start": v(-481.24, 109.35) * mm, "end": v(-481.29, 109) * mm});
            skLineSegment(sketch, "E4533", {"start": v(-481.29, 109) * mm, "end": v(-481.35, 108.64) * mm});
            skLineSegment(sketch, "E4534", {"start": v(-481.35, 108.64) * mm, "end": v(-481.42, 108.28) * mm});
            skLineSegment(sketch, "E4535", {"start": v(-481.42, 108.28) * mm, "end": v(-481.5, 107.92) * mm});
            skLineSegment(sketch, "E4536", {"start": v(-481.5, 107.92) * mm, "end": v(-481.58, 107.57) * mm});
            skLineSegment(sketch, "E4537", {"start": v(-481.58, 107.57) * mm, "end": v(-481.68, 107.22) * mm});
            skLineSegment(sketch, "E4538", {"start": v(-481.68, 107.22) * mm, "end": v(-481.78, 106.88) * mm});
            skLineSegment(sketch, "E4539", {"start": v(-481.78, 106.88) * mm, "end": v(-481.9, 106.53) * mm});
            skLineSegment(sketch, "E4540", {"start": v(-481.9, 106.53) * mm, "end": v(-482.02, 106.2) * mm});
            skLineSegment(sketch, "E4541", {"start": v(-482.02, 106.2) * mm, "end": v(-482.15, 105.85) * mm});
            skLineSegment(sketch, "E4542", {"start": v(-482.15, 105.85) * mm, "end": v(-482.29, 105.52) * mm});
            skLineSegment(sketch, "E4543", {"start": v(-482.29, 105.52) * mm, "end": v(-482.43, 105.19) * mm});
            skLineSegment(sketch, "E4544", {"start": v(-482.43, 105.19) * mm, "end": v(-482.59, 104.86) * mm});
            skLineSegment(sketch, "E4545", {"start": v(-482.59, 104.86) * mm, "end": v(-482.75, 104.54) * mm});
            skLineSegment(sketch, "E4546", {"start": v(-482.75, 104.54) * mm, "end": v(-482.92, 104.22) * mm});
            skLineSegment(sketch, "E4547", {"start": v(-482.92, 104.22) * mm, "end": v(-483.1, 103.9) * mm});
            skLineSegment(sketch, "E4548", {"start": v(-483.1, 103.9) * mm, "end": v(-483.29, 103.6) * mm});
            skLineSegment(sketch, "E4549", {"start": v(-483.29, 103.6) * mm, "end": v(-483.48, 103.28) * mm});
            skLineSegment(sketch, "E4550", {"start": v(-483.48, 103.28) * mm, "end": v(-483.68, 102.98) * mm});
            skLineSegment(sketch, "E4551", {"start": v(-483.68, 102.98) * mm, "end": v(-483.9, 102.68) * mm});
            skLineSegment(sketch, "E4552", {"start": v(-483.9, 102.68) * mm, "end": v(-484.11, 102.4) * mm});
            skLineSegment(sketch, "E4553", {"start": v(-484.11, 102.4) * mm, "end": v(-484.34, 102.1) * mm});
            skLineSegment(sketch, "E4554", {"start": v(-484.34, 102.1) * mm, "end": v(-484.57, 101.82) * mm});
            skLineSegment(sketch, "E4555", {"start": v(-484.57, 101.82) * mm, "end": v(-484.8, 101.55) * mm});
            skLineSegment(sketch, "E4556", {"start": v(-484.8, 101.55) * mm, "end": v(-485.06, 101.28) * mm});
            skLineSegment(sketch, "E4557", {"start": v(-485.06, 101.28) * mm, "end": v(-485.31, 101.01) * mm});
            skLineSegment(sketch, "E4558", {"start": v(-485.31, 101.01) * mm, "end": v(-485.64, 100.7) * mm});
            skLineSegment(sketch, "E4559", {"start": v(-485.64, 100.7) * mm, "end": v(-485.98, 100.4) * mm});
            skLineSegment(sketch, "E4560", {"start": v(-485.98, 100.4) * mm, "end": v(-486.33, 100.12) * mm});
            skLineSegment(sketch, "E4561", {"start": v(-486.33, 100.12) * mm, "end": v(-486.68, 99.84) * mm});
            skLineSegment(sketch, "E4562", {"start": v(-486.68, 99.84) * mm, "end": v(-487.04, 99.57) * mm});
            skLineSegment(sketch, "E4563", {"start": v(-487.04, 99.57) * mm, "end": v(-487.4, 99.31) * mm});
            skLineSegment(sketch, "E4564", {"start": v(-487.4, 99.31) * mm, "end": v(-487.78, 99.06) * mm});
            skLineSegment(sketch, "E4565", {"start": v(-487.78, 99.06) * mm, "end": v(-488.15, 98.82) * mm});
            skLineSegment(sketch, "E4566", {"start": v(-488.15, 98.82) * mm, "end": v(-488.54, 98.59) * mm});
            skLineSegment(sketch, "E4567", {"start": v(-488.54, 98.59) * mm, "end": v(-488.92, 98.37) * mm});
            skLineSegment(sketch, "E4568", {"start": v(-488.92, 98.37) * mm, "end": v(-489.32, 98.16) * mm});
            skLineSegment(sketch, "E4569", {"start": v(-489.32, 98.16) * mm, "end": v(-489.72, 97.95) * mm});
            skLineSegment(sketch, "E4570", {"start": v(-489.72, 97.95) * mm, "end": v(-490.12, 97.76) * mm});
            skLineSegment(sketch, "E4571", {"start": v(-490.12, 97.76) * mm, "end": v(-490.52, 97.58) * mm});
            skLineSegment(sketch, "E4572", {"start": v(-490.52, 97.58) * mm, "end": v(-490.94, 97.4) * mm});
            skLineSegment(sketch, "E4573", {"start": v(-490.94, 97.4) * mm, "end": v(-491.35, 97.24) * mm});
            skLineSegment(sketch, "E4574", {"start": v(-491.35, 97.24) * mm, "end": v(-491.77, 97.1) * mm});
            skLineSegment(sketch, "E4575", {"start": v(-491.77, 97.1) * mm, "end": v(-492.2, 96.95) * mm});
            skLineSegment(sketch, "E4576", {"start": v(-492.2, 96.95) * mm, "end": v(-492.62, 96.82) * mm});
            skLineSegment(sketch, "E4577", {"start": v(-492.62, 96.82) * mm, "end": v(-493.05, 96.7) * mm});
            skLineSegment(sketch, "E4578", {"start": v(-493.05, 96.7) * mm, "end": v(-493.48, 96.59) * mm});
            skLineSegment(sketch, "E4579", {"start": v(-493.48, 96.59) * mm, "end": v(-493.91, 96.49) * mm});
            skLineSegment(sketch, "E4580", {"start": v(-493.91, 96.49) * mm, "end": v(-494.35, 96.4) * mm});
            skLineSegment(sketch, "E4581", {"start": v(-494.35, 96.4) * mm, "end": v(-494.8, 96.32) * mm});
            skLineSegment(sketch, "E4582", {"start": v(-494.8, 96.32) * mm, "end": v(-495.23, 96.25) * mm});
            skLineSegment(sketch, "E4583", {"start": v(-495.23, 96.25) * mm, "end": v(-495.68, 96.2) * mm});
            skLineSegment(sketch, "E4584", {"start": v(-495.68, 96.2) * mm, "end": v(-496.12, 96.15) * mm});
            skLineSegment(sketch, "E4585", {"start": v(-496.12, 96.15) * mm, "end": v(-496.57, 96.12) * mm});
            skLineSegment(sketch, "E4586", {"start": v(-496.57, 96.12) * mm, "end": v(-497.02, 96.1) * mm});
            skLineSegment(sketch, "E4587", {"start": v(-497.02, 96.1) * mm, "end": v(-497.47, 96.08) * mm});
            skLineSegment(sketch, "E4588", {"start": v(-497.47, 96.08) * mm, "end": v(-497.92, 96.08) * mm});
            skLineSegment(sketch, "E4589", {"start": v(-497.92, 96.08) * mm, "end": v(-498.38, 96.09) * mm});
            skLineSegment(sketch, "E4590", {"start": v(-498.38, 96.09) * mm, "end": v(-498.87, 96.08) * mm});
            skLineSegment(sketch, "E4591", {"start": v(-498.87, 96.08) * mm, "end": v(-499.36, 96.07) * mm});
            skLineSegment(sketch, "E4592", {"start": v(-499.36, 96.07) * mm, "end": v(-499.85, 96.08) * mm});
            skLineSegment(sketch, "E4593", {"start": v(-499.85, 96.08) * mm, "end": v(-500.33, 96.1) * mm});
            skLineSegment(sketch, "E4594", {"start": v(-500.33, 96.1) * mm, "end": v(-500.82, 96.14) * mm});
            skLineSegment(sketch, "E4595", {"start": v(-500.82, 96.14) * mm, "end": v(-501.3, 96.2) * mm});
            skLineSegment(sketch, "E4596", {"start": v(-501.3, 96.2) * mm, "end": v(-501.79, 96.25) * mm});
            skLineSegment(sketch, "E4597", {"start": v(-501.79, 96.25) * mm, "end": v(-502.27, 96.32) * mm});
            skLineSegment(sketch, "E4598", {"start": v(-502.27, 96.32) * mm, "end": v(-502.75, 96.4) * mm});
            skLineSegment(sketch, "E4599", {"start": v(-502.75, 96.4) * mm, "end": v(-503.22, 96.5) * mm});
            skLineSegment(sketch, "E4600", {"start": v(-503.22, 96.5) * mm, "end": v(-503.7, 96.6) * mm});
            skLineSegment(sketch, "E4601", {"start": v(-503.7, 96.6) * mm, "end": v(-504.16, 96.73) * mm});
            skLineSegment(sketch, "E4602", {"start": v(-504.16, 96.73) * mm, "end": v(-504.63, 96.86) * mm});
            skLineSegment(sketch, "E4603", {"start": v(-504.63, 96.86) * mm, "end": v(-505.1, 97) * mm});
            skLineSegment(sketch, "E4604", {"start": v(-505.1, 97) * mm, "end": v(-505.55, 97.15) * mm});
            skLineSegment(sketch, "E4605", {"start": v(-505.55, 97.15) * mm, "end": v(-506, 97.32) * mm});
            skLineSegment(sketch, "E4606", {"start": v(-506, 97.32) * mm, "end": v(-506.46, 97.5) * mm});
            skLineSegment(sketch, "E4607", {"start": v(-506.46, 97.5) * mm, "end": v(-506.9, 97.68) * mm});
            skLineSegment(sketch, "E4608", {"start": v(-506.9, 97.68) * mm, "end": v(-507.34, 97.88) * mm});
            skLineSegment(sketch, "E4609", {"start": v(-507.34, 97.88) * mm, "end": v(-507.78, 98.09) * mm});
            skLineSegment(sketch, "E4610", {"start": v(-507.78, 98.09) * mm, "end": v(-508.21, 98.3) * mm});
            skLineSegment(sketch, "E4611", {"start": v(-508.21, 98.3) * mm, "end": v(-508.64, 98.54) * mm});
            skLineSegment(sketch, "E4612", {"start": v(-508.64, 98.54) * mm, "end": v(-509.06, 98.78) * mm});
            skLineSegment(sketch, "E4613", {"start": v(-509.06, 98.78) * mm, "end": v(-509.47, 99.03) * mm});
            skLineSegment(sketch, "E4614", {"start": v(-509.47, 99.03) * mm, "end": v(-509.88, 99.3) * mm});
            skLineSegment(sketch, "E4615", {"start": v(-509.88, 99.3) * mm, "end": v(-510.29, 99.57) * mm});
            skLineSegment(sketch, "E4616", {"start": v(-510.29, 99.57) * mm, "end": v(-510.68, 99.85) * mm});
            skLineSegment(sketch, "E4617", {"start": v(-510.68, 99.85) * mm, "end": v(-511.07, 100.14) * mm});
            skLineSegment(sketch, "E4618", {"start": v(-511.07, 100.14) * mm, "end": v(-511.45, 100.45) * mm});
            skLineSegment(sketch, "E4619", {"start": v(-511.45, 100.45) * mm, "end": v(-511.83, 100.76) * mm});
            skLineSegment(sketch, "E4620", {"start": v(-511.83, 100.76) * mm, "end": v(-512.2, 101.08) * mm});
            skLineSegment(sketch, "E4621", {"start": v(-512.2, 101.08) * mm, "end": v(-512.56, 101.42) * mm});
            skLineSegment(sketch, "E4622", {"start": v(-512.56, 101.42) * mm, "end": v(-512.81, 101.67) * mm});
            skLineSegment(sketch, "E4623", {"start": v(-512.81, 101.67) * mm, "end": v(-513.06, 101.92) * mm});
            skLineSegment(sketch, "E4624", {"start": v(-513.06, 101.92) * mm, "end": v(-513.3, 102.19) * mm});
            skLineSegment(sketch, "E4625", {"start": v(-513.3, 102.19) * mm, "end": v(-513.53, 102.45) * mm});
            skLineSegment(sketch, "E4626", {"start": v(-513.53, 102.45) * mm, "end": v(-513.76, 102.73) * mm});
            skLineSegment(sketch, "E4627", {"start": v(-513.76, 102.73) * mm, "end": v(-513.97, 103) * mm});
            skLineSegment(sketch, "E4628", {"start": v(-513.97, 103) * mm, "end": v(-514.18, 103.29) * mm});
            skLineSegment(sketch, "E4629", {"start": v(-514.18, 103.29) * mm, "end": v(-514.39, 103.58) * mm});
            skLineSegment(sketch, "E4630", {"start": v(-514.39, 103.58) * mm, "end": v(-514.58, 103.87) * mm});
            skLineSegment(sketch, "E4631", {"start": v(-514.58, 103.87) * mm, "end": v(-514.77, 104.17) * mm});
            skLineSegment(sketch, "E4632", {"start": v(-514.77, 104.17) * mm, "end": v(-514.95, 104.47) * mm});
            skLineSegment(sketch, "E4633", {"start": v(-514.95, 104.47) * mm, "end": v(-515.12, 104.78) * mm});
            skLineSegment(sketch, "E4634", {"start": v(-515.12, 104.78) * mm, "end": v(-515.28, 105.09) * mm});
            skLineSegment(sketch, "E4635", {"start": v(-515.28, 105.09) * mm, "end": v(-515.44, 105.4) * mm});
            skLineSegment(sketch, "E4636", {"start": v(-515.44, 105.4) * mm, "end": v(-515.59, 105.72) * mm});
            skLineSegment(sketch, "E4637", {"start": v(-515.59, 105.72) * mm, "end": v(-515.72, 106.04) * mm});
            skLineSegment(sketch, "E4638", {"start": v(-515.72, 106.04) * mm, "end": v(-515.86, 106.37) * mm});
            skLineSegment(sketch, "E4639", {"start": v(-515.86, 106.37) * mm, "end": v(-515.98, 106.7) * mm});
            skLineSegment(sketch, "E4640", {"start": v(-515.98, 106.7) * mm, "end": v(-516.1, 107.03) * mm});
            skLineSegment(sketch, "E4641", {"start": v(-516.1, 107.03) * mm, "end": v(-516.2, 107.37) * mm});
            skLineSegment(sketch, "E4642", {"start": v(-516.2, 107.37) * mm, "end": v(-516.3, 107.7) * mm});
            skLineSegment(sketch, "E4643", {"start": v(-516.3, 107.7) * mm, "end": v(-516.38, 108.04) * mm});
            skLineSegment(sketch, "E4644", {"start": v(-516.38, 108.04) * mm, "end": v(-516.46, 108.39) * mm});
            skLineSegment(sketch, "E4645", {"start": v(-516.46, 108.39) * mm, "end": v(-516.53, 108.73) * mm});
            skLineSegment(sketch, "E4646", {"start": v(-516.53, 108.73) * mm, "end": v(-516.6, 109.08) * mm});
            skLineSegment(sketch, "E4647", {"start": v(-516.6, 109.08) * mm, "end": v(-516.65, 109.43) * mm});
            skLineSegment(sketch, "E4648", {"start": v(-516.65, 109.43) * mm, "end": v(-516.7, 109.78) * mm});
            skLineSegment(sketch, "E4649", {"start": v(-516.7, 109.78) * mm, "end": v(-516.73, 110.13) * mm});
            skLineSegment(sketch, "E4650", {"start": v(-516.73, 110.13) * mm, "end": v(-516.76, 110.48) * mm});
            skLineSegment(sketch, "E4651", {"start": v(-516.76, 110.48) * mm, "end": v(-516.77, 110.84) * mm});
            skLineSegment(sketch, "E4652", {"start": v(-516.77, 110.84) * mm, "end": v(-516.78, 111.2) * mm});
            skLineSegment(sketch, "E4653", {"start": v(-516.78, 111.2) * mm, "end": v(-516.78, 111.55) * mm});
            skLineSegment(sketch, "E4654", {"start": v(-516.78, 111.55) * mm, "end": v(-516.78, 111.91) * mm});
            skLineSegment(sketch, "E4655", {"start": v(-516.78, 111.91) * mm, "end": v(-516.76, 112.27) * mm});
            skLineSegment(sketch, "E4656", {"start": v(-516.76, 112.27) * mm, "end": v(-516.74, 112.63) * mm});
            skLineSegment(sketch, "E4657", {"start": v(-516.74, 112.63) * mm, "end": v(-516.71, 113) * mm});
            skLineSegment(sketch, "E4658", {"start": v(-516.71, 113) * mm, "end": v(-516.67, 113.35) * mm});
            skLineSegment(sketch, "E4659", {"start": v(-516.67, 113.35) * mm, "end": v(-516.62, 113.7) * mm});
            skLineSegment(sketch, "E4660", {"start": v(-516.62, 113.7) * mm, "end": v(-516.56, 114.06) * mm});
            skLineSegment(sketch, "E4661", {"start": v(-516.56, 114.06) * mm, "end": v(-516.5, 114.41) * mm});
            skLineSegment(sketch, "E4662", {"start": v(-516.5, 114.41) * mm, "end": v(-516.42, 114.76) * mm});
            skLineSegment(sketch, "E4663", {"start": v(-516.42, 114.76) * mm, "end": v(-516.33, 115.1) * mm});
            skLineSegment(sketch, "E4664", {"start": v(-516.33, 115.1) * mm, "end": v(-516.24, 115.45) * mm});
            skLineSegment(sketch, "E4665", {"start": v(-516.24, 115.45) * mm, "end": v(-516.13, 115.8) * mm});
            skLineSegment(sketch, "E4666", {"start": v(-516.13, 115.8) * mm, "end": v(-516.02, 116.14) * mm});
            skLineSegment(sketch, "E4667", {"start": v(-516.02, 116.14) * mm, "end": v(-515.9, 116.47) * mm});
            skLineSegment(sketch, "E4668", {"start": v(-515.9, 116.47) * mm, "end": v(-515.77, 116.8) * mm});
            skLineSegment(sketch, "E4669", {"start": v(-515.77, 116.8) * mm, "end": v(-515.64, 117.13) * mm});
            skLineSegment(sketch, "E4670", {"start": v(-515.64, 117.13) * mm, "end": v(-515.5, 117.46) * mm});
            skLineSegment(sketch, "E4671", {"start": v(-515.5, 117.46) * mm, "end": v(-515.34, 117.78) * mm});
            skLineSegment(sketch, "E4672", {"start": v(-515.34, 117.78) * mm, "end": v(-515.18, 118.1) * mm});
            skLineSegment(sketch, "E4673", {"start": v(-515.18, 118.1) * mm, "end": v(-515, 118.41) * mm});
            skLineSegment(sketch, "E4674", {"start": v(-515, 118.41) * mm, "end": v(-514.83, 118.72) * mm});
            skLineSegment(sketch, "E4675", {"start": v(-514.83, 118.72) * mm, "end": v(-514.64, 119.03) * mm});
            skLineSegment(sketch, "E4676", {"start": v(-514.64, 119.03) * mm, "end": v(-514.45, 119.33) * mm});
            skLineSegment(sketch, "E4677", {"start": v(-514.45, 119.33) * mm, "end": v(-514.25, 119.62) * mm});
            skLineSegment(sketch, "E4678", {"start": v(-514.25, 119.62) * mm, "end": v(-514.04, 119.91) * mm});
            skLineSegment(sketch, "E4679", {"start": v(-514.04, 119.91) * mm, "end": v(-513.82, 120.2) * mm});
            skLineSegment(sketch, "E4680", {"start": v(-513.82, 120.2) * mm, "end": v(-513.6, 120.48) * mm});
            skLineSegment(sketch, "E4681", {"start": v(-513.6, 120.48) * mm, "end": v(-513.36, 120.76) * mm});
            skLineSegment(sketch, "E4682", {"start": v(-513.36, 120.76) * mm, "end": v(-513.12, 121.02) * mm});
            skLineSegment(sketch, "E4683", {"start": v(-513.12, 121.02) * mm, "end": v(-512.88, 121.29) * mm});
            skLineSegment(sketch, "E4684", {"start": v(-512.88, 121.29) * mm, "end": v(-512.62, 121.54) * mm});
            skLineSegment(sketch, "E4685", {"start": v(-512.62, 121.54) * mm, "end": v(-512.36, 121.8) * mm});
            skLineSegment(sketch, "E4686", {"start": v(-512.36, 121.8) * mm, "end": v(-512, 122.12) * mm});
            skLineSegment(sketch, "E4687", {"start": v(-512, 122.12) * mm, "end": v(-511.64, 122.43) * mm});
            skLineSegment(sketch, "E4688", {"start": v(-511.64, 122.43) * mm, "end": v(-511.26, 122.74) * mm});
            skLineSegment(sketch, "E4689", {"start": v(-511.26, 122.74) * mm, "end": v(-510.88, 123.03) * mm});
            skLineSegment(sketch, "E4690", {"start": v(-510.88, 123.03) * mm, "end": v(-510.5, 123.32) * mm});
            skLineSegment(sketch, "E4691", {"start": v(-510.5, 123.32) * mm, "end": v(-510.1, 123.6) * mm});
            skLineSegment(sketch, "E4692", {"start": v(-510.1, 123.6) * mm, "end": v(-509.7, 123.85) * mm});
            skLineSegment(sketch, "E4693", {"start": v(-509.7, 123.85) * mm, "end": v(-509.3, 124.1) * mm});
            skLineSegment(sketch, "E4694", {"start": v(-509.3, 124.1) * mm, "end": v(-508.9, 124.35) * mm});
            skLineSegment(sketch, "E4695", {"start": v(-508.9, 124.35) * mm, "end": v(-508.47, 124.58) * mm});
            skLineSegment(sketch, "E4696", {"start": v(-508.47, 124.58) * mm, "end": v(-508.05, 124.8) * mm});
            skLineSegment(sketch, "E4697", {"start": v(-508.05, 124.8) * mm, "end": v(-507.63, 125.02) * mm});
            skLineSegment(sketch, "E4698", {"start": v(-507.63, 125.02) * mm, "end": v(-507.2, 125.22) * mm});
            skLineSegment(sketch, "E4699", {"start": v(-507.2, 125.22) * mm, "end": v(-506.76, 125.4) * mm});
            skLineSegment(sketch, "E4700", {"start": v(-506.76, 125.4) * mm, "end": v(-506.32, 125.59) * mm});
            skLineSegment(sketch, "E4701", {"start": v(-506.32, 125.59) * mm, "end": v(-505.87, 125.76) * mm});
            skLineSegment(sketch, "E4702", {"start": v(-505.87, 125.76) * mm, "end": v(-505.42, 125.91) * mm});
            skLineSegment(sketch, "E4703", {"start": v(-505.42, 125.91) * mm, "end": v(-504.97, 126.06) * mm});
            skLineSegment(sketch, "E4704", {"start": v(-504.97, 126.06) * mm, "end": v(-504.51, 126.2) * mm});
            skLineSegment(sketch, "E4705", {"start": v(-504.51, 126.2) * mm, "end": v(-504.05, 126.32) * mm});
            skLineSegment(sketch, "E4706", {"start": v(-504.05, 126.32) * mm, "end": v(-503.59, 126.43) * mm});
            skLineSegment(sketch, "E4707", {"start": v(-503.59, 126.43) * mm, "end": v(-503.12, 126.53) * mm});
            skLineSegment(sketch, "E4708", {"start": v(-503.12, 126.53) * mm, "end": v(-502.66, 126.62) * mm});
            skLineSegment(sketch, "E4709", {"start": v(-502.66, 126.62) * mm, "end": v(-502.18, 126.7) * mm});
            skLineSegment(sketch, "E4710", {"start": v(-502.18, 126.7) * mm, "end": v(-501.71, 126.77) * mm});
            skLineSegment(sketch, "E4711", {"start": v(-501.71, 126.77) * mm, "end": v(-501.24, 126.82) * mm});
            skLineSegment(sketch, "E4712", {"start": v(-501.24, 126.82) * mm, "end": v(-500.76, 126.87) * mm});
            skLineSegment(sketch, "E4713", {"start": v(-500.76, 126.87) * mm, "end": v(-500.28, 126.9) * mm});
            skLineSegment(sketch, "E4714", {"start": v(-500.28, 126.9) * mm, "end": v(-499.8, 126.92) * mm});
            skLineSegment(sketch, "E4715", {"start": v(-499.8, 126.92) * mm, "end": v(-499.32, 126.92) * mm});
            skLineSegment(sketch, "E4716", {"start": v(-499.32, 126.92) * mm, "end": v(-498.84, 126.92) * mm});
            skLineSegment(sketch, "E4717", {"start": v(-498.84, 126.92) * mm, "end": v(-498.35, 126.9) * mm});
            skLineSegment(sketch, "E4718", {"start": v(-498.35, 126.9) * mm, "end": v(-497.9, 126.9) * mm});
            skLineSegment(sketch, "E4719", {"start": v(-497.9, 126.9) * mm, "end": v(-497.45, 126.9) * mm});
            skLineSegment(sketch, "E4720", {"start": v(-497.45, 126.9) * mm, "end": v(-497, 126.89) * mm});
            skLineSegment(sketch, "E4721", {"start": v(-497, 126.89) * mm, "end": v(-496.56, 126.86) * mm});
            skLineSegment(sketch, "E4722", {"start": v(-496.56, 126.86) * mm, "end": v(-496.11, 126.82) * mm});
            skLineSegment(sketch, "E4723", {"start": v(-496.11, 126.82) * mm, "end": v(-495.67, 126.78) * mm});
            skLineSegment(sketch, "E4724", {"start": v(-495.67, 126.78) * mm, "end": v(-495.23, 126.72) * mm});
            skLineSegment(sketch, "E4725", {"start": v(-495.23, 126.72) * mm, "end": v(-494.79, 126.64) * mm});
            skLineSegment(sketch, "E4726", {"start": v(-494.79, 126.64) * mm, "end": v(-494.35, 126.56) * mm});
            skLineSegment(sketch, "E4727", {"start": v(-494.35, 126.56) * mm, "end": v(-493.91, 126.47) * mm});
            skLineSegment(sketch, "E4728", {"start": v(-493.91, 126.47) * mm, "end": v(-493.48, 126.37) * mm});
            skLineSegment(sketch, "E4729", {"start": v(-493.48, 126.37) * mm, "end": v(-493.05, 126.25) * mm});
            skLineSegment(sketch, "E4730", {"start": v(-493.05, 126.25) * mm, "end": v(-492.63, 126.13) * mm});
            skLineSegment(sketch, "E4731", {"start": v(-492.63, 126.13) * mm, "end": v(-492.2, 126) * mm});
            skLineSegment(sketch, "E4732", {"start": v(-492.2, 126) * mm, "end": v(-491.78, 125.85) * mm});
            skLineSegment(sketch, "E4733", {"start": v(-491.78, 125.85) * mm, "end": v(-491.37, 125.7) * mm});
            skLineSegment(sketch, "E4734", {"start": v(-491.37, 125.7) * mm, "end": v(-490.96, 125.52) * mm});
            skLineSegment(sketch, "E4735", {"start": v(-490.96, 125.52) * mm, "end": v(-490.55, 125.35) * mm});
            skLineSegment(sketch, "E4736", {"start": v(-490.55, 125.35) * mm, "end": v(-490.15, 125.16) * mm});
            skLineSegment(sketch, "E4737", {"start": v(-490.15, 125.16) * mm, "end": v(-489.75, 124.97) * mm});
            skLineSegment(sketch, "E4738", {"start": v(-489.75, 124.97) * mm, "end": v(-489.35, 124.76) * mm});
            skLineSegment(sketch, "E4739", {"start": v(-489.35, 124.76) * mm, "end": v(-488.97, 124.54) * mm});
            skLineSegment(sketch, "E4740", {"start": v(-488.97, 124.54) * mm, "end": v(-488.58, 124.32) * mm});
            skLineSegment(sketch, "E4741", {"start": v(-488.58, 124.32) * mm, "end": v(-488.2, 124.08) * mm});
            skLineSegment(sketch, "E4742", {"start": v(-488.2, 124.08) * mm, "end": v(-487.83, 123.84) * mm});
            skLineSegment(sketch, "E4743", {"start": v(-487.83, 123.84) * mm, "end": v(-487.47, 123.58) * mm});
            skLineSegment(sketch, "E4744", {"start": v(-487.47, 123.58) * mm, "end": v(-487.1, 123.32) * mm});
            skLineSegment(sketch, "E4745", {"start": v(-487.1, 123.32) * mm, "end": v(-486.75, 123.04) * mm});
            skLineSegment(sketch, "E4746", {"start": v(-486.75, 123.04) * mm, "end": v(-486.4, 122.76) * mm});
            skLineSegment(sketch, "E4747", {"start": v(-486.4, 122.76) * mm, "end": v(-486.06, 122.47) * mm});
            skLineSegment(sketch, "E4748", {"start": v(-486.06, 122.47) * mm, "end": v(-485.73, 122.17) * mm});
            skLineSegment(sketch, "E4749", {"start": v(-485.73, 122.17) * mm, "end": v(-485.4, 121.86) * mm});
            skLineSegment(sketch, "E4750", {"start": v(-485.4, 121.86) * mm, "end": v(-485.15, 121.6) * mm});
            skLineSegment(sketch, "E4751", {"start": v(-485.15, 121.6) * mm, "end": v(-484.9, 121.34) * mm});
            skLineSegment(sketch, "E4752", {"start": v(-484.9, 121.34) * mm, "end": v(-484.66, 121.07) * mm});
            skLineSegment(sketch, "E4753", {"start": v(-484.66, 121.07) * mm, "end": v(-484.43, 120.8) * mm});
            skLineSegment(sketch, "E4754", {"start": v(-484.43, 120.8) * mm, "end": v(-484.2, 120.52) * mm});
            skLineSegment(sketch, "E4755", {"start": v(-484.2, 120.52) * mm, "end": v(-483.98, 120.23) * mm});
            skLineSegment(sketch, "E4756", {"start": v(-483.98, 120.23) * mm, "end": v(-483.77, 119.94) * mm});
            skLineSegment(sketch, "E4757", {"start": v(-483.77, 119.94) * mm, "end": v(-483.57, 119.65) * mm});
            skLineSegment(sketch, "E4758", {"start": v(-483.57, 119.65) * mm, "end": v(-483.37, 119.35) * mm});
            skLineSegment(sketch, "E4759", {"start": v(-483.37, 119.35) * mm, "end": v(-483.18, 119.04) * mm});
            skLineSegment(sketch, "E4760", {"start": v(-483.18, 119.04) * mm, "end": v(-483, 118.74) * mm});
            skLineSegment(sketch, "E4761", {"start": v(-483, 118.74) * mm, "end": v(-482.83, 118.42) * mm});
            skLineSegment(sketch, "E4762", {"start": v(-482.83, 118.42) * mm, "end": v(-482.66, 118.1) * mm});
            skLineSegment(sketch, "E4763", {"start": v(-482.66, 118.1) * mm, "end": v(-482.5, 117.79) * mm});
            skLineSegment(sketch, "E4764", {"start": v(-482.5, 117.79) * mm, "end": v(-482.36, 117.46) * mm});
            skLineSegment(sketch, "E4765", {"start": v(-482.36, 117.46) * mm, "end": v(-482.22, 117.13) * mm});
            skLineSegment(sketch, "E4766", {"start": v(-482.22, 117.13) * mm, "end": v(-482.08, 116.8) * mm});
            skLineSegment(sketch, "E4767", {"start": v(-482.08, 116.8) * mm, "end": v(-481.96, 116.47) * mm});
            skLineSegment(sketch, "E4768", {"start": v(-481.96, 116.47) * mm, "end": v(-481.84, 116.13) * mm});
            skLineSegment(sketch, "E4769", {"start": v(-481.84, 116.13) * mm, "end": v(-481.73, 115.8) * mm});
            skLineSegment(sketch, "E4770", {"start": v(-481.73, 115.8) * mm, "end": v(-481.64, 115.45) * mm});
            skLineSegment(sketch, "E4771", {"start": v(-481.64, 115.45) * mm, "end": v(-481.54, 115.1) * mm});
            skLineSegment(sketch, "E4772", {"start": v(-481.54, 115.1) * mm, "end": v(-481.46, 114.75) * mm});
            skLineSegment(sketch, "E4773", {"start": v(-481.46, 114.75) * mm, "end": v(-481.39, 114.4) * mm});
            skLineSegment(sketch, "E4774", {"start": v(-481.39, 114.4) * mm, "end": v(-481.32, 114.05) * mm});
            skLineSegment(sketch, "E4775", {"start": v(-481.32, 114.05) * mm, "end": v(-481.27, 113.7) * mm});
            skLineSegment(sketch, "E4776", {"start": v(-481.27, 113.7) * mm, "end": v(-481.22, 113.34) * mm});
            skLineSegment(sketch, "E4777", {"start": v(-481.22, 113.34) * mm, "end": v(-481.18, 112.99) * mm});
            skLineSegment(sketch, "E4778", {"start": v(-481.18, 112.99) * mm, "end": v(-481.15, 112.63) * mm});
            skLineSegment(sketch, "E4779", {"start": v(-481.15, 112.63) * mm, "end": v(-481.13, 112.27) * mm});
            skLineSegment(sketch, "E4780", {"start": v(-481.13, 112.27) * mm, "end": v(-481.12, 111.9) * mm});
            skLineSegment(sketch, "E4781", {"start": v(-481.12, 111.9) * mm, "end": v(-481.12, 111.54) * mm});
            skLineSegment(sketch, "E4782", {"start": v(-481.12, 150.26) * mm, "end": v(-481.11, 149.9) * mm});
            skLineSegment(sketch, "E4783", {"start": v(-481.11, 149.9) * mm, "end": v(-481.12, 149.52) * mm});
            skLineSegment(sketch, "E4784", {"start": v(-481.12, 149.52) * mm, "end": v(-481.13, 149.16) * mm});
            skLineSegment(sketch, "E4785", {"start": v(-481.13, 149.16) * mm, "end": v(-481.16, 148.8) * mm});
            skLineSegment(sketch, "E4786", {"start": v(-481.16, 148.8) * mm, "end": v(-481.2, 148.43) * mm});
            skLineSegment(sketch, "E4787", {"start": v(-481.2, 148.43) * mm, "end": v(-481.24, 148.07) * mm});
            skLineSegment(sketch, "E4788", {"start": v(-481.24, 148.07) * mm, "end": v(-481.29, 147.7) * mm});
            skLineSegment(sketch, "E4789", {"start": v(-481.29, 147.7) * mm, "end": v(-481.35, 147.35) * mm});
            skLineSegment(sketch, "E4790", {"start": v(-481.35, 147.35) * mm, "end": v(-481.42, 147) * mm});
            skLineSegment(sketch, "E4791", {"start": v(-481.42, 147) * mm, "end": v(-481.5, 146.64) * mm});
            skLineSegment(sketch, "E4792", {"start": v(-481.5, 146.64) * mm, "end": v(-481.58, 146.29) * mm});
            skLineSegment(sketch, "E4793", {"start": v(-481.58, 146.29) * mm, "end": v(-481.68, 145.94) * mm});
            skLineSegment(sketch, "E4794", {"start": v(-481.68, 145.94) * mm, "end": v(-481.78, 145.6) * mm});
            skLineSegment(sketch, "E4795", {"start": v(-481.78, 145.6) * mm, "end": v(-481.9, 145.25) * mm});
            skLineSegment(sketch, "E4796", {"start": v(-481.9, 145.25) * mm, "end": v(-482.02, 144.9) * mm});
            skLineSegment(sketch, "E4797", {"start": v(-482.02, 144.9) * mm, "end": v(-482.15, 144.57) * mm});
            skLineSegment(sketch, "E4798", {"start": v(-482.15, 144.57) * mm, "end": v(-482.29, 144.23) * mm});
            skLineSegment(sketch, "E4799", {"start": v(-482.29, 144.23) * mm, "end": v(-482.43, 143.9) * mm});
            skLineSegment(sketch, "E4800", {"start": v(-482.43, 143.9) * mm, "end": v(-482.59, 143.58) * mm});
            skLineSegment(sketch, "E4801", {"start": v(-482.59, 143.58) * mm, "end": v(-482.75, 143.25) * mm});
            skLineSegment(sketch, "E4802", {"start": v(-482.75, 143.25) * mm, "end": v(-482.92, 142.93) * mm});
            skLineSegment(sketch, "E4803", {"start": v(-482.92, 142.93) * mm, "end": v(-483.1, 142.62) * mm});
            skLineSegment(sketch, "E4804", {"start": v(-483.1, 142.62) * mm, "end": v(-483.29, 142.3) * mm});
            skLineSegment(sketch, "E4805", {"start": v(-483.29, 142.3) * mm, "end": v(-483.48, 142) * mm});
            skLineSegment(sketch, "E4806", {"start": v(-483.48, 142) * mm, "end": v(-483.68, 141.7) * mm});
            skLineSegment(sketch, "E4807", {"start": v(-483.68, 141.7) * mm, "end": v(-483.9, 141.4) * mm});
            skLineSegment(sketch, "E4808", {"start": v(-483.9, 141.4) * mm, "end": v(-484.11, 141.1) * mm});
            skLineSegment(sketch, "E4809", {"start": v(-484.11, 141.1) * mm, "end": v(-484.34, 140.82) * mm});
            skLineSegment(sketch, "E4810", {"start": v(-484.34, 140.82) * mm, "end": v(-484.57, 140.54) * mm});
            skLineSegment(sketch, "E4811", {"start": v(-484.57, 140.54) * mm, "end": v(-484.8, 140.26) * mm});
            skLineSegment(sketch, "E4812", {"start": v(-484.8, 140.26) * mm, "end": v(-485.06, 140) * mm});
            skLineSegment(sketch, "E4813", {"start": v(-485.06, 140) * mm, "end": v(-485.31, 139.73) * mm});
            skLineSegment(sketch, "E4814", {"start": v(-485.31, 139.73) * mm, "end": v(-485.64, 139.42) * mm});
            skLineSegment(sketch, "E4815", {"start": v(-485.64, 139.42) * mm, "end": v(-485.98, 139.12) * mm});
            skLineSegment(sketch, "E4816", {"start": v(-485.98, 139.12) * mm, "end": v(-486.33, 138.84) * mm});
            skLineSegment(sketch, "E4817", {"start": v(-486.33, 138.84) * mm, "end": v(-486.68, 138.56) * mm});
            skLineSegment(sketch, "E4818", {"start": v(-486.68, 138.56) * mm, "end": v(-487.04, 138.29) * mm});
            skLineSegment(sketch, "E4819", {"start": v(-487.04, 138.29) * mm, "end": v(-487.4, 138.03) * mm});
            skLineSegment(sketch, "E4820", {"start": v(-487.4, 138.03) * mm, "end": v(-487.78, 137.78) * mm});
            skLineSegment(sketch, "E4821", {"start": v(-487.78, 137.78) * mm, "end": v(-488.15, 137.54) * mm});
            skLineSegment(sketch, "E4822", {"start": v(-488.15, 137.54) * mm, "end": v(-488.54, 137.3) * mm});
            skLineSegment(sketch, "E4823", {"start": v(-488.54, 137.3) * mm, "end": v(-488.92, 137.08) * mm});
            skLineSegment(sketch, "E4824", {"start": v(-488.92, 137.08) * mm, "end": v(-489.32, 136.87) * mm});
            skLineSegment(sketch, "E4825", {"start": v(-489.32, 136.87) * mm, "end": v(-489.72, 136.67) * mm});
            skLineSegment(sketch, "E4826", {"start": v(-489.72, 136.67) * mm, "end": v(-490.12, 136.48) * mm});
            skLineSegment(sketch, "E4827", {"start": v(-490.12, 136.48) * mm, "end": v(-490.52, 136.3) * mm});
            skLineSegment(sketch, "E4828", {"start": v(-490.52, 136.3) * mm, "end": v(-490.94, 136.12) * mm});
            skLineSegment(sketch, "E4829", {"start": v(-490.94, 136.12) * mm, "end": v(-491.35, 135.96) * mm});
            skLineSegment(sketch, "E4830", {"start": v(-491.35, 135.96) * mm, "end": v(-491.77, 135.8) * mm});
            skLineSegment(sketch, "E4831", {"start": v(-491.77, 135.8) * mm, "end": v(-492.2, 135.66) * mm});
            skLineSegment(sketch, "E4832", {"start": v(-492.2, 135.66) * mm, "end": v(-492.62, 135.53) * mm});
            skLineSegment(sketch, "E4833", {"start": v(-492.62, 135.53) * mm, "end": v(-493.05, 135.41) * mm});
            skLineSegment(sketch, "E4834", {"start": v(-493.05, 135.41) * mm, "end": v(-493.48, 135.3) * mm});
            skLineSegment(sketch, "E4835", {"start": v(-493.48, 135.3) * mm, "end": v(-493.91, 135.2) * mm});
            skLineSegment(sketch, "E4836", {"start": v(-493.91, 135.2) * mm, "end": v(-494.35, 135.11) * mm});
            skLineSegment(sketch, "E4837", {"start": v(-494.35, 135.11) * mm, "end": v(-494.8, 135.03) * mm});
            skLineSegment(sketch, "E4838", {"start": v(-494.8, 135.03) * mm, "end": v(-495.23, 134.97) * mm});
            skLineSegment(sketch, "E4839", {"start": v(-495.23, 134.97) * mm, "end": v(-495.68, 134.91) * mm});
            skLineSegment(sketch, "E4840", {"start": v(-495.68, 134.91) * mm, "end": v(-496.12, 134.86) * mm});
            skLineSegment(sketch, "E4841", {"start": v(-496.12, 134.86) * mm, "end": v(-496.57, 134.83) * mm});
            skLineSegment(sketch, "E4842", {"start": v(-496.57, 134.83) * mm, "end": v(-497.02, 134.8) * mm});
            skLineSegment(sketch, "E4843", {"start": v(-497.02, 134.8) * mm, "end": v(-497.47, 134.8) * mm});
            skLineSegment(sketch, "E4844", {"start": v(-497.47, 134.8) * mm, "end": v(-497.92, 134.8) * mm});
            skLineSegment(sketch, "E4845", {"start": v(-497.92, 134.8) * mm, "end": v(-498.38, 134.8) * mm});
            skLineSegment(sketch, "E4846", {"start": v(-498.38, 134.8) * mm, "end": v(-498.87, 134.8) * mm});
            skLineSegment(sketch, "E4847", {"start": v(-498.87, 134.8) * mm, "end": v(-499.36, 134.79) * mm});
            skLineSegment(sketch, "E4848", {"start": v(-499.36, 134.79) * mm, "end": v(-499.85, 134.8) * mm});
            skLineSegment(sketch, "E4849", {"start": v(-499.85, 134.8) * mm, "end": v(-500.33, 134.82) * mm});
            skLineSegment(sketch, "E4850", {"start": v(-500.33, 134.82) * mm, "end": v(-500.82, 134.86) * mm});
            skLineSegment(sketch, "E4851", {"start": v(-500.82, 134.86) * mm, "end": v(-501.3, 134.9) * mm});
            skLineSegment(sketch, "E4852", {"start": v(-501.3, 134.9) * mm, "end": v(-501.79, 134.97) * mm});
            skLineSegment(sketch, "E4853", {"start": v(-501.79, 134.97) * mm, "end": v(-502.27, 135.04) * mm});
            skLineSegment(sketch, "E4854", {"start": v(-502.27, 135.04) * mm, "end": v(-502.75, 135.12) * mm});
            skLineSegment(sketch, "E4855", {"start": v(-502.75, 135.12) * mm, "end": v(-503.22, 135.22) * mm});
            skLineSegment(sketch, "E4856", {"start": v(-503.22, 135.22) * mm, "end": v(-503.7, 135.32) * mm});
            skLineSegment(sketch, "E4857", {"start": v(-503.7, 135.32) * mm, "end": v(-504.16, 135.44) * mm});
            skLineSegment(sketch, "E4858", {"start": v(-504.16, 135.44) * mm, "end": v(-504.63, 135.57) * mm});
            skLineSegment(sketch, "E4859", {"start": v(-504.63, 135.57) * mm, "end": v(-505.1, 135.71) * mm});
            skLineSegment(sketch, "E4860", {"start": v(-505.1, 135.71) * mm, "end": v(-505.55, 135.87) * mm});
            skLineSegment(sketch, "E4861", {"start": v(-505.55, 135.87) * mm, "end": v(-506, 136.03) * mm});
            skLineSegment(sketch, "E4862", {"start": v(-506, 136.03) * mm, "end": v(-506.46, 136.2) * mm});
            skLineSegment(sketch, "E4863", {"start": v(-506.46, 136.2) * mm, "end": v(-506.9, 136.4) * mm});
            skLineSegment(sketch, "E4864", {"start": v(-506.9, 136.4) * mm, "end": v(-507.34, 136.6) * mm});
            skLineSegment(sketch, "E4865", {"start": v(-507.34, 136.6) * mm, "end": v(-507.78, 136.8) * mm});
            skLineSegment(sketch, "E4866", {"start": v(-507.78, 136.8) * mm, "end": v(-508.21, 137.02) * mm});
            skLineSegment(sketch, "E4867", {"start": v(-508.21, 137.02) * mm, "end": v(-508.64, 137.25) * mm});
            skLineSegment(sketch, "E4868", {"start": v(-508.64, 137.25) * mm, "end": v(-509.06, 137.5) * mm});
            skLineSegment(sketch, "E4869", {"start": v(-509.06, 137.5) * mm, "end": v(-509.47, 137.75) * mm});
            skLineSegment(sketch, "E4870", {"start": v(-509.47, 137.75) * mm, "end": v(-509.88, 138) * mm});
            skLineSegment(sketch, "E4871", {"start": v(-509.88, 138) * mm, "end": v(-510.29, 138.28) * mm});
            skLineSegment(sketch, "E4872", {"start": v(-510.29, 138.28) * mm, "end": v(-510.68, 138.56) * mm});
            skLineSegment(sketch, "E4873", {"start": v(-510.68, 138.56) * mm, "end": v(-511.07, 138.86) * mm});
            skLineSegment(sketch, "E4874", {"start": v(-511.07, 138.86) * mm, "end": v(-511.45, 139.16) * mm});
            skLineSegment(sketch, "E4875", {"start": v(-511.45, 139.16) * mm, "end": v(-511.83, 139.48) * mm});
            skLineSegment(sketch, "E4876", {"start": v(-511.83, 139.48) * mm, "end": v(-512.2, 139.8) * mm});
            skLineSegment(sketch, "E4877", {"start": v(-512.2, 139.8) * mm, "end": v(-512.56, 140.13) * mm});
            skLineSegment(sketch, "E4878", {"start": v(-512.56, 140.13) * mm, "end": v(-512.81, 140.38) * mm});
            skLineSegment(sketch, "E4879", {"start": v(-512.81, 140.38) * mm, "end": v(-513.06, 140.64) * mm});
            skLineSegment(sketch, "E4880", {"start": v(-513.06, 140.64) * mm, "end": v(-513.3, 140.9) * mm});
            skLineSegment(sketch, "E4881", {"start": v(-513.3, 140.9) * mm, "end": v(-513.53, 141.17) * mm});
            skLineSegment(sketch, "E4882", {"start": v(-513.53, 141.17) * mm, "end": v(-513.76, 141.44) * mm});
            skLineSegment(sketch, "E4883", {"start": v(-513.76, 141.44) * mm, "end": v(-513.97, 141.72) * mm});
            skLineSegment(sketch, "E4884", {"start": v(-513.97, 141.72) * mm, "end": v(-514.18, 142) * mm});
            skLineSegment(sketch, "E4885", {"start": v(-514.18, 142) * mm, "end": v(-514.39, 142.3) * mm});
            skLineSegment(sketch, "E4886", {"start": v(-514.39, 142.3) * mm, "end": v(-514.58, 142.59) * mm});
            skLineSegment(sketch, "E4887", {"start": v(-514.58, 142.59) * mm, "end": v(-514.77, 142.88) * mm});
            skLineSegment(sketch, "E4888", {"start": v(-514.77, 142.88) * mm, "end": v(-514.95, 143.19) * mm});
            skLineSegment(sketch, "E4889", {"start": v(-514.95, 143.19) * mm, "end": v(-515.12, 143.5) * mm});
            skLineSegment(sketch, "E4890", {"start": v(-515.12, 143.5) * mm, "end": v(-515.28, 143.8) * mm});
            skLineSegment(sketch, "E4891", {"start": v(-515.28, 143.8) * mm, "end": v(-515.44, 144.12) * mm});
            skLineSegment(sketch, "E4892", {"start": v(-515.44, 144.12) * mm, "end": v(-515.59, 144.44) * mm});
            skLineSegment(sketch, "E4893", {"start": v(-515.59, 144.44) * mm, "end": v(-515.72, 144.76) * mm});
            skLineSegment(sketch, "E4894", {"start": v(-515.72, 144.76) * mm, "end": v(-515.86, 145.08) * mm});
            skLineSegment(sketch, "E4895", {"start": v(-515.86, 145.08) * mm, "end": v(-515.98, 145.41) * mm});
            skLineSegment(sketch, "E4896", {"start": v(-515.98, 145.41) * mm, "end": v(-516.1, 145.75) * mm});
            skLineSegment(sketch, "E4897", {"start": v(-516.1, 145.75) * mm, "end": v(-516.2, 146.08) * mm});
            skLineSegment(sketch, "E4898", {"start": v(-516.2, 146.08) * mm, "end": v(-516.3, 146.42) * mm});
            skLineSegment(sketch, "E4899", {"start": v(-516.3, 146.42) * mm, "end": v(-516.38, 146.76) * mm});
            skLineSegment(sketch, "E4900", {"start": v(-516.38, 146.76) * mm, "end": v(-516.46, 147.1) * mm});
            skLineSegment(sketch, "E4901", {"start": v(-516.46, 147.1) * mm, "end": v(-516.53, 147.45) * mm});
            skLineSegment(sketch, "E4902", {"start": v(-516.53, 147.45) * mm, "end": v(-516.6, 147.8) * mm});
            skLineSegment(sketch, "E4903", {"start": v(-516.6, 147.8) * mm, "end": v(-516.65, 148.14) * mm});
            skLineSegment(sketch, "E4904", {"start": v(-516.65, 148.14) * mm, "end": v(-516.7, 148.5) * mm});
            skLineSegment(sketch, "E4905", {"start": v(-516.7, 148.5) * mm, "end": v(-516.73, 148.84) * mm});
            skLineSegment(sketch, "E4906", {"start": v(-516.73, 148.84) * mm, "end": v(-516.76, 149.2) * mm});
            skLineSegment(sketch, "E4907", {"start": v(-516.76, 149.2) * mm, "end": v(-516.77, 149.55) * mm});
            skLineSegment(sketch, "E4908", {"start": v(-516.77, 149.55) * mm, "end": v(-516.78, 149.9) * mm});
            skLineSegment(sketch, "E4909", {"start": v(-516.78, 149.9) * mm, "end": v(-516.78, 150.26) * mm});
            skLineSegment(sketch, "E4910", {"start": v(-516.78, 150.26) * mm, "end": v(-516.78, 150.63) * mm});
            skLineSegment(sketch, "E4911", {"start": v(-516.78, 150.63) * mm, "end": v(-516.76, 150.99) * mm});
            skLineSegment(sketch, "E4912", {"start": v(-516.76, 150.99) * mm, "end": v(-516.74, 151.35) * mm});
            skLineSegment(sketch, "E4913", {"start": v(-516.74, 151.35) * mm, "end": v(-516.71, 151.7) * mm});
            skLineSegment(sketch, "E4914", {"start": v(-516.71, 151.7) * mm, "end": v(-516.67, 152.07) * mm});
            skLineSegment(sketch, "E4915", {"start": v(-516.67, 152.07) * mm, "end": v(-516.62, 152.42) * mm});
            skLineSegment(sketch, "E4916", {"start": v(-516.62, 152.42) * mm, "end": v(-516.56, 152.78) * mm});
            skLineSegment(sketch, "E4917", {"start": v(-516.56, 152.78) * mm, "end": v(-516.5, 153.13) * mm});
            skLineSegment(sketch, "E4918", {"start": v(-516.5, 153.13) * mm, "end": v(-516.42, 153.48) * mm});
            skLineSegment(sketch, "E4919", {"start": v(-516.42, 153.48) * mm, "end": v(-516.33, 153.82) * mm});
            skLineSegment(sketch, "E4920", {"start": v(-516.33, 153.82) * mm, "end": v(-516.24, 154.17) * mm});
            skLineSegment(sketch, "E4921", {"start": v(-516.24, 154.17) * mm, "end": v(-516.13, 154.51) * mm});
            skLineSegment(sketch, "E4922", {"start": v(-516.13, 154.51) * mm, "end": v(-516.02, 154.85) * mm});
            skLineSegment(sketch, "E4923", {"start": v(-516.02, 154.85) * mm, "end": v(-515.9, 155.19) * mm});
            skLineSegment(sketch, "E4924", {"start": v(-515.9, 155.19) * mm, "end": v(-515.77, 155.52) * mm});
            skLineSegment(sketch, "E4925", {"start": v(-515.77, 155.52) * mm, "end": v(-515.64, 155.85) * mm});
            skLineSegment(sketch, "E4926", {"start": v(-515.64, 155.85) * mm, "end": v(-515.5, 156.17) * mm});
            skLineSegment(sketch, "E4927", {"start": v(-515.5, 156.17) * mm, "end": v(-515.34, 156.5) * mm});
            skLineSegment(sketch, "E4928", {"start": v(-515.34, 156.5) * mm, "end": v(-515.18, 156.81) * mm});
            skLineSegment(sketch, "E4929", {"start": v(-515.18, 156.81) * mm, "end": v(-515, 157.13) * mm});
            skLineSegment(sketch, "E4930", {"start": v(-515, 157.13) * mm, "end": v(-514.83, 157.44) * mm});
            skLineSegment(sketch, "E4931", {"start": v(-514.83, 157.44) * mm, "end": v(-514.64, 157.74) * mm});
            skLineSegment(sketch, "E4932", {"start": v(-514.64, 157.74) * mm, "end": v(-514.45, 158.04) * mm});
            skLineSegment(sketch, "E4933", {"start": v(-514.45, 158.04) * mm, "end": v(-514.25, 158.34) * mm});
            skLineSegment(sketch, "E4934", {"start": v(-514.25, 158.34) * mm, "end": v(-514.04, 158.63) * mm});
            skLineSegment(sketch, "E4935", {"start": v(-514.04, 158.63) * mm, "end": v(-513.82, 158.91) * mm});
            skLineSegment(sketch, "E4936", {"start": v(-513.82, 158.91) * mm, "end": v(-513.6, 159.2) * mm});
            skLineSegment(sketch, "E4937", {"start": v(-513.6, 159.2) * mm, "end": v(-513.36, 159.47) * mm});
            skLineSegment(sketch, "E4938", {"start": v(-513.36, 159.47) * mm, "end": v(-513.12, 159.74) * mm});
            skLineSegment(sketch, "E4939", {"start": v(-513.12, 159.74) * mm, "end": v(-512.88, 160) * mm});
            skLineSegment(sketch, "E4940", {"start": v(-512.88, 160) * mm, "end": v(-512.62, 160.26) * mm});
            skLineSegment(sketch, "E4941", {"start": v(-512.62, 160.26) * mm, "end": v(-512.36, 160.51) * mm});
            skLineSegment(sketch, "E4942", {"start": v(-512.36, 160.51) * mm, "end": v(-512, 160.83) * mm});
            skLineSegment(sketch, "E4943", {"start": v(-512, 160.83) * mm, "end": v(-511.64, 161.15) * mm});
            skLineSegment(sketch, "E4944", {"start": v(-511.64, 161.15) * mm, "end": v(-511.26, 161.45) * mm});
            skLineSegment(sketch, "E4945", {"start": v(-511.26, 161.45) * mm, "end": v(-510.88, 161.75) * mm});
            skLineSegment(sketch, "E4946", {"start": v(-510.88, 161.75) * mm, "end": v(-510.5, 162.03) * mm});
            skLineSegment(sketch, "E4947", {"start": v(-510.5, 162.03) * mm, "end": v(-510.1, 162.3) * mm});
            skLineSegment(sketch, "E4948", {"start": v(-510.1, 162.3) * mm, "end": v(-509.7, 162.57) * mm});
            skLineSegment(sketch, "E4949", {"start": v(-509.7, 162.57) * mm, "end": v(-509.3, 162.82) * mm});
            skLineSegment(sketch, "E4950", {"start": v(-509.3, 162.82) * mm, "end": v(-508.9, 163.07) * mm});
            skLineSegment(sketch, "E4951", {"start": v(-508.9, 163.07) * mm, "end": v(-508.47, 163.3) * mm});
            skLineSegment(sketch, "E4952", {"start": v(-508.47, 163.3) * mm, "end": v(-508.05, 163.52) * mm});
            skLineSegment(sketch, "E4953", {"start": v(-508.05, 163.52) * mm, "end": v(-507.63, 163.73) * mm});
            skLineSegment(sketch, "E4954", {"start": v(-507.63, 163.73) * mm, "end": v(-507.2, 163.93) * mm});
            skLineSegment(sketch, "E4955", {"start": v(-507.2, 163.93) * mm, "end": v(-506.76, 164.12) * mm});
            skLineSegment(sketch, "E4956", {"start": v(-506.76, 164.12) * mm, "end": v(-506.32, 164.3) * mm});
            skLineSegment(sketch, "E4957", {"start": v(-506.32, 164.3) * mm, "end": v(-505.87, 164.47) * mm});
            skLineSegment(sketch, "E4958", {"start": v(-505.87, 164.47) * mm, "end": v(-505.42, 164.63) * mm});
            skLineSegment(sketch, "E4959", {"start": v(-505.42, 164.63) * mm, "end": v(-504.97, 164.78) * mm});
            skLineSegment(sketch, "E4960", {"start": v(-504.97, 164.78) * mm, "end": v(-504.51, 164.91) * mm});
            skLineSegment(sketch, "E4961", {"start": v(-504.51, 164.91) * mm, "end": v(-504.05, 165.03) * mm});
            skLineSegment(sketch, "E4962", {"start": v(-504.05, 165.03) * mm, "end": v(-503.59, 165.15) * mm});
            skLineSegment(sketch, "E4963", {"start": v(-503.59, 165.15) * mm, "end": v(-503.12, 165.25) * mm});
            skLineSegment(sketch, "E4964", {"start": v(-503.12, 165.25) * mm, "end": v(-502.66, 165.34) * mm});
            skLineSegment(sketch, "E4965", {"start": v(-502.66, 165.34) * mm, "end": v(-502.18, 165.42) * mm});
            skLineSegment(sketch, "E4966", {"start": v(-502.18, 165.42) * mm, "end": v(-501.71, 165.48) * mm});
            skLineSegment(sketch, "E4967", {"start": v(-501.71, 165.48) * mm, "end": v(-501.24, 165.54) * mm});
            skLineSegment(sketch, "E4968", {"start": v(-501.24, 165.54) * mm, "end": v(-500.76, 165.58) * mm});
            skLineSegment(sketch, "E4969", {"start": v(-500.76, 165.58) * mm, "end": v(-500.28, 165.61) * mm});
            skLineSegment(sketch, "E4970", {"start": v(-500.28, 165.61) * mm, "end": v(-499.8, 165.63) * mm});
            skLineSegment(sketch, "E4971", {"start": v(-499.8, 165.63) * mm, "end": v(-499.32, 165.64) * mm});
            skLineSegment(sketch, "E4972", {"start": v(-499.32, 165.64) * mm, "end": v(-498.84, 165.63) * mm});
            skLineSegment(sketch, "E4973", {"start": v(-498.84, 165.63) * mm, "end": v(-498.35, 165.62) * mm});
            skLineSegment(sketch, "E4974", {"start": v(-498.35, 165.62) * mm, "end": v(-497.9, 165.62) * mm});
            skLineSegment(sketch, "E4975", {"start": v(-497.9, 165.62) * mm, "end": v(-497.45, 165.62) * mm});
            skLineSegment(sketch, "E4976", {"start": v(-497.45, 165.62) * mm, "end": v(-497, 165.6) * mm});
            skLineSegment(sketch, "E4977", {"start": v(-497, 165.6) * mm, "end": v(-496.56, 165.58) * mm});
            skLineSegment(sketch, "E4978", {"start": v(-496.56, 165.58) * mm, "end": v(-496.11, 165.54) * mm});
            skLineSegment(sketch, "E4979", {"start": v(-496.11, 165.54) * mm, "end": v(-495.67, 165.49) * mm});
            skLineSegment(sketch, "E4980", {"start": v(-495.67, 165.49) * mm, "end": v(-495.23, 165.43) * mm});
            skLineSegment(sketch, "E4981", {"start": v(-495.23, 165.43) * mm, "end": v(-494.79, 165.36) * mm});
            skLineSegment(sketch, "E4982", {"start": v(-494.79, 165.36) * mm, "end": v(-494.35, 165.28) * mm});
            skLineSegment(sketch, "E4983", {"start": v(-494.35, 165.28) * mm, "end": v(-493.91, 165.18) * mm});
            skLineSegment(sketch, "E4984", {"start": v(-493.91, 165.18) * mm, "end": v(-493.48, 165.08) * mm});
            skLineSegment(sketch, "E4985", {"start": v(-493.48, 165.08) * mm, "end": v(-493.05, 164.97) * mm});
            skLineSegment(sketch, "E4986", {"start": v(-493.05, 164.97) * mm, "end": v(-492.63, 164.84) * mm});
            skLineSegment(sketch, "E4987", {"start": v(-492.63, 164.84) * mm, "end": v(-492.2, 164.7) * mm});
            skLineSegment(sketch, "E4988", {"start": v(-492.2, 164.7) * mm, "end": v(-491.78, 164.56) * mm});
            skLineSegment(sketch, "E4989", {"start": v(-491.78, 164.56) * mm, "end": v(-491.37, 164.4) * mm});
            skLineSegment(sketch, "E4990", {"start": v(-491.37, 164.4) * mm, "end": v(-490.96, 164.24) * mm});
            skLineSegment(sketch, "E4991", {"start": v(-490.96, 164.24) * mm, "end": v(-490.55, 164.06) * mm});
            skLineSegment(sketch, "E4992", {"start": v(-490.55, 164.06) * mm, "end": v(-490.15, 163.88) * mm});
            skLineSegment(sketch, "E4993", {"start": v(-490.15, 163.88) * mm, "end": v(-489.75, 163.68) * mm});
            skLineSegment(sketch, "E4994", {"start": v(-489.75, 163.68) * mm, "end": v(-489.35, 163.47) * mm});
            skLineSegment(sketch, "E4995", {"start": v(-489.35, 163.47) * mm, "end": v(-488.97, 163.26) * mm});
            skLineSegment(sketch, "E4996", {"start": v(-488.97, 163.26) * mm, "end": v(-488.58, 163.03) * mm});
            skLineSegment(sketch, "E4997", {"start": v(-488.58, 163.03) * mm, "end": v(-488.2, 162.8) * mm});
            skLineSegment(sketch, "E4998", {"start": v(-488.2, 162.8) * mm, "end": v(-487.83, 162.55) * mm});
            skLineSegment(sketch, "E4999", {"start": v(-487.83, 162.55) * mm, "end": v(-487.47, 162.3) * mm});
            skLineSegment(sketch, "E5000", {"start": v(-487.47, 162.3) * mm, "end": v(-487.1, 162.03) * mm});
            skLineSegment(sketch, "E5001", {"start": v(-487.1, 162.03) * mm, "end": v(-486.75, 161.76) * mm});
            skLineSegment(sketch, "E5002", {"start": v(-486.75, 161.76) * mm, "end": v(-486.4, 161.48) * mm});
            skLineSegment(sketch, "E5003", {"start": v(-486.4, 161.48) * mm, "end": v(-486.06, 161.18) * mm});
            skLineSegment(sketch, "E5004", {"start": v(-486.06, 161.18) * mm, "end": v(-485.73, 160.88) * mm});
            skLineSegment(sketch, "E5005", {"start": v(-485.73, 160.88) * mm, "end": v(-485.4, 160.57) * mm});
            skLineSegment(sketch, "E5006", {"start": v(-485.4, 160.57) * mm, "end": v(-485.15, 160.32) * mm});
            skLineSegment(sketch, "E5007", {"start": v(-485.15, 160.32) * mm, "end": v(-484.9, 160.05) * mm});
            skLineSegment(sketch, "E5008", {"start": v(-484.9, 160.05) * mm, "end": v(-484.66, 159.78) * mm});
            skLineSegment(sketch, "E5009", {"start": v(-484.66, 159.78) * mm, "end": v(-484.43, 159.51) * mm});
            skLineSegment(sketch, "E5010", {"start": v(-484.43, 159.51) * mm, "end": v(-484.2, 159.23) * mm});
            skLineSegment(sketch, "E5011", {"start": v(-484.2, 159.23) * mm, "end": v(-483.98, 158.95) * mm});
            skLineSegment(sketch, "E5012", {"start": v(-483.98, 158.95) * mm, "end": v(-483.77, 158.66) * mm});
            skLineSegment(sketch, "E5013", {"start": v(-483.77, 158.66) * mm, "end": v(-483.57, 158.36) * mm});
            skLineSegment(sketch, "E5014", {"start": v(-483.57, 158.36) * mm, "end": v(-483.37, 158.06) * mm});
            skLineSegment(sketch, "E5015", {"start": v(-483.37, 158.06) * mm, "end": v(-483.18, 157.76) * mm});
            skLineSegment(sketch, "E5016", {"start": v(-483.18, 157.76) * mm, "end": v(-483, 157.45) * mm});
            skLineSegment(sketch, "E5017", {"start": v(-483, 157.45) * mm, "end": v(-482.83, 157.14) * mm});
            skLineSegment(sketch, "E5018", {"start": v(-482.83, 157.14) * mm, "end": v(-482.66, 156.82) * mm});
            skLineSegment(sketch, "E5019", {"start": v(-482.66, 156.82) * mm, "end": v(-482.5, 156.5) * mm});
            skLineSegment(sketch, "E5020", {"start": v(-482.5, 156.5) * mm, "end": v(-482.36, 156.18) * mm});
            skLineSegment(sketch, "E5021", {"start": v(-482.36, 156.18) * mm, "end": v(-482.22, 155.85) * mm});
            skLineSegment(sketch, "E5022", {"start": v(-482.22, 155.85) * mm, "end": v(-482.08, 155.52) * mm});
            skLineSegment(sketch, "E5023", {"start": v(-482.08, 155.52) * mm, "end": v(-481.96, 155.18) * mm});
            skLineSegment(sketch, "E5024", {"start": v(-481.96, 155.18) * mm, "end": v(-481.84, 154.85) * mm});
            skLineSegment(sketch, "E5025", {"start": v(-481.84, 154.85) * mm, "end": v(-481.73, 154.5) * mm});
            skLineSegment(sketch, "E5026", {"start": v(-481.73, 154.5) * mm, "end": v(-481.64, 154.16) * mm});
            skLineSegment(sketch, "E5027", {"start": v(-481.64, 154.16) * mm, "end": v(-481.54, 153.82) * mm});
            skLineSegment(sketch, "E5028", {"start": v(-481.54, 153.82) * mm, "end": v(-481.46, 153.47) * mm});
            skLineSegment(sketch, "E5029", {"start": v(-481.46, 153.47) * mm, "end": v(-481.39, 153.12) * mm});
            skLineSegment(sketch, "E5030", {"start": v(-481.39, 153.12) * mm, "end": v(-481.32, 152.77) * mm});
            skLineSegment(sketch, "E5031", {"start": v(-481.32, 152.77) * mm, "end": v(-481.27, 152.41) * mm});
            skLineSegment(sketch, "E5032", {"start": v(-481.27, 152.41) * mm, "end": v(-481.22, 152.06) * mm});
            skLineSegment(sketch, "E5033", {"start": v(-481.22, 152.06) * mm, "end": v(-481.18, 151.7) * mm});
            skLineSegment(sketch, "E5034", {"start": v(-481.18, 151.7) * mm, "end": v(-481.15, 151.34) * mm});
            skLineSegment(sketch, "E5035", {"start": v(-481.15, 151.34) * mm, "end": v(-481.13, 150.98) * mm});
            skLineSegment(sketch, "E5036", {"start": v(-481.13, 150.98) * mm, "end": v(-481.12, 150.62) * mm});
            skLineSegment(sketch, "E5037", {"start": v(-481.12, 150.62) * mm, "end": v(-481.12, 150.26) * mm});
            skLineSegment(sketch, "E5038", {"start": v(-481.58, 173.51) * mm, "end": v(-516.58, 173.51) * mm});
            skLineSegment(sketch, "E5039", {"start": v(-516.58, 173.51) * mm, "end": v(-516.58, 195.27) * mm});
            skLineSegment(sketch, "E5040", {"start": v(-499.86, 173.51) * mm, "end": v(-499.86, 193.7) * mm});
            skLineSegment(sketch, "E5041", {"start": v(-494.67, 202.97) * mm, "end": v(-494.67, 227.1) * mm});
            skLineSegment(sketch, "E5042", {"start": v(-481.6, 234.8) * mm, "end": v(-507.77, 234.8) * mm});
            skLineSegment(sketch, "E5043", {"start": v(-516.05, 234.8) * mm, "end": v(-516.5, 234.8) * mm});
            skLineSegment(sketch, "E5044", {"start": v(-481.6, 242.5) * mm, "end": v(-507.83, 242.5) * mm});
            skLineSegment(sketch, "E5045", {"start": v(-497.58, 242.5) * mm, "end": v(-498.15, 242.52) * mm});
            skLineSegment(sketch, "E5046", {"start": v(-498.15, 242.52) * mm, "end": v(-498.72, 242.56) * mm});
            skLineSegment(sketch, "E5047", {"start": v(-498.72, 242.56) * mm, "end": v(-499.28, 242.63) * mm});
            skLineSegment(sketch, "E5048", {"start": v(-499.28, 242.63) * mm, "end": v(-499.84, 242.74) * mm});
            skLineSegment(sketch, "E5049", {"start": v(-499.84, 242.74) * mm, "end": v(-500.4, 242.86) * mm});
            skLineSegment(sketch, "E5050", {"start": v(-500.4, 242.86) * mm, "end": v(-500.94, 243.02) * mm});
            skLineSegment(sketch, "E5051", {"start": v(-500.94, 243.02) * mm, "end": v(-501.48, 243.2) * mm});
            skLineSegment(sketch, "E5052", {"start": v(-501.48, 243.2) * mm, "end": v(-502, 243.41) * mm});
            skLineSegment(sketch, "E5053", {"start": v(-502, 243.41) * mm, "end": v(-502.52, 243.65) * mm});
            skLineSegment(sketch, "E5054", {"start": v(-502.52, 243.65) * mm, "end": v(-503.02, 243.9) * mm});
            skLineSegment(sketch, "E5055", {"start": v(-503.02, 243.9) * mm, "end": v(-503.5, 244.2) * mm});
            skLineSegment(sketch, "E5056", {"start": v(-503.5, 244.2) * mm, "end": v(-503.98, 244.5) * mm});
            skLineSegment(sketch, "E5057", {"start": v(-503.98, 244.5) * mm, "end": v(-504.44, 244.84) * mm});
            skLineSegment(sketch, "E5058", {"start": v(-504.44, 244.84) * mm, "end": v(-504.88, 245.2) * mm});
            skLineSegment(sketch, "E5059", {"start": v(-504.88, 245.2) * mm, "end": v(-505.31, 245.57) * mm});
            skLineSegment(sketch, "E5060", {"start": v(-505.31, 245.57) * mm, "end": v(-505.72, 245.98) * mm});
            skLineSegment(sketch, "E5061", {"start": v(-505.72, 245.98) * mm, "end": v(-506.05, 246.33) * mm});
            skLineSegment(sketch, "E5062", {"start": v(-506.05, 246.33) * mm, "end": v(-506.36, 246.7) * mm});
            skLineSegment(sketch, "E5063", {"start": v(-506.36, 246.7) * mm, "end": v(-506.65, 247.08) * mm});
            skLineSegment(sketch, "E5064", {"start": v(-506.65, 247.08) * mm, "end": v(-506.92, 247.48) * mm});
            skLineSegment(sketch, "E5065", {"start": v(-506.92, 247.48) * mm, "end": v(-507.17, 247.89) * mm});
            skLineSegment(sketch, "E5066", {"start": v(-507.17, 247.89) * mm, "end": v(-507.4, 248.3) * mm});
            skLineSegment(sketch, "E5067", {"start": v(-507.4, 248.3) * mm, "end": v(-507.6, 248.74) * mm});
            skLineSegment(sketch, "E5068", {"start": v(-507.6, 248.74) * mm, "end": v(-507.8, 249.18) * mm});
            skLineSegment(sketch, "E5069", {"start": v(-507.8, 249.18) * mm, "end": v(-507.96, 249.62) * mm});
            skLineSegment(sketch, "E5070", {"start": v(-507.96, 249.62) * mm, "end": v(-508.1, 250.08) * mm});
            skLineSegment(sketch, "E5071", {"start": v(-508.1, 250.08) * mm, "end": v(-508.22, 250.54) * mm});
            skLineSegment(sketch, "E5072", {"start": v(-508.22, 250.54) * mm, "end": v(-508.32, 251.01) * mm});
            skLineSegment(sketch, "E5073", {"start": v(-508.32, 251.01) * mm, "end": v(-508.39, 251.48) * mm});
            skLineSegment(sketch, "E5074", {"start": v(-508.39, 251.48) * mm, "end": v(-508.44, 251.96) * mm});
            skLineSegment(sketch, "E5075", {"start": v(-508.44, 251.96) * mm, "end": v(-508.46, 252.44) * mm});
            skLineSegment(sketch, "E5076", {"start": v(-508.46, 252.44) * mm, "end": v(-508.46, 252.93) * mm});
            skLineSegment(sketch, "E5077", {"start": v(-508.46, 252.93) * mm, "end": v(-508.5, 253.4) * mm});
            skLineSegment(sketch, "E5078", {"start": v(-508.5, 253.4) * mm, "end": v(-508.5, 253.85) * mm});
            skLineSegment(sketch, "E5079", {"start": v(-508.5, 253.85) * mm, "end": v(-508.48, 254.31) * mm});
            skLineSegment(sketch, "E5080", {"start": v(-508.48, 254.31) * mm, "end": v(-508.44, 254.77) * mm});
            skLineSegment(sketch, "E5081", {"start": v(-508.44, 254.77) * mm, "end": v(-508.37, 255.22) * mm});
            skLineSegment(sketch, "E5082", {"start": v(-508.37, 255.22) * mm, "end": v(-508.28, 255.67) * mm});
            skLineSegment(sketch, "E5083", {"start": v(-508.28, 255.67) * mm, "end": v(-508.17, 256.1) * mm});
            skLineSegment(sketch, "E5084", {"start": v(-508.17, 256.1) * mm, "end": v(-508.04, 256.55) * mm});
            skLineSegment(sketch, "E5085", {"start": v(-508.04, 256.55) * mm, "end": v(-507.88, 256.97) * mm});
            skLineSegment(sketch, "E5086", {"start": v(-507.88, 256.97) * mm, "end": v(-507.7, 257.4) * mm});
            skLineSegment(sketch, "E5087", {"start": v(-507.7, 257.4) * mm, "end": v(-507.5, 257.8) * mm});
            skLineSegment(sketch, "E5088", {"start": v(-507.5, 257.8) * mm, "end": v(-507.28, 258.2) * mm});
            skLineSegment(sketch, "E5089", {"start": v(-507.28, 258.2) * mm, "end": v(-507.04, 258.6) * mm});
            skLineSegment(sketch, "E5090", {"start": v(-507.04, 258.6) * mm, "end": v(-506.78, 258.97) * mm});
            skLineSegment(sketch, "E5091", {"start": v(-506.78, 258.97) * mm, "end": v(-506.5, 259.33) * mm});
            skLineSegment(sketch, "E5092", {"start": v(-506.5, 259.33) * mm, "end": v(-506.2, 259.68) * mm});
            skLineSegment(sketch, "E5093", {"start": v(-506.2, 259.68) * mm, "end": v(-505.94, 259.9) * mm});
            skLineSegment(sketch, "E5094", {"start": v(-505.94, 259.9) * mm, "end": v(-505.67, 260.1) * mm});
            skLineSegment(sketch, "E5095", {"start": v(-505.67, 260.1) * mm, "end": v(-505.4, 260.29) * mm});
            skLineSegment(sketch, "E5096", {"start": v(-505.4, 260.29) * mm, "end": v(-505.12, 260.46) * mm});
            skLineSegment(sketch, "E5097", {"start": v(-505.12, 260.46) * mm, "end": v(-504.83, 260.62) * mm});
            skLineSegment(sketch, "E5098", {"start": v(-504.83, 260.62) * mm, "end": v(-504.54, 260.77) * mm});
            skLineSegment(sketch, "E5099", {"start": v(-504.54, 260.77) * mm, "end": v(-504.24, 260.9) * mm});
            skLineSegment(sketch, "E5100", {"start": v(-504.24, 260.9) * mm, "end": v(-503.93, 261.02) * mm});
            skLineSegment(sketch, "E5101", {"start": v(-503.93, 261.02) * mm, "end": v(-503.62, 261.13) * mm});
            skLineSegment(sketch, "E5102", {"start": v(-503.62, 261.13) * mm, "end": v(-503.3, 261.22) * mm});
            skLineSegment(sketch, "E5103", {"start": v(-503.3, 261.22) * mm, "end": v(-502.98, 261.3) * mm});
            skLineSegment(sketch, "E5104", {"start": v(-502.98, 261.3) * mm, "end": v(-502.66, 261.36) * mm});
            skLineSegment(sketch, "E5105", {"start": v(-502.66, 261.36) * mm, "end": v(-502.33, 261.4) * mm});
            skLineSegment(sketch, "E5106", {"start": v(-502.33, 261.4) * mm, "end": v(-502, 261.44) * mm});
            skLineSegment(sketch, "E5107", {"start": v(-502, 261.44) * mm, "end": v(-501.67, 261.45) * mm});
            skLineSegment(sketch, "E5108", {"start": v(-501.67, 261.45) * mm, "end": v(-501.34, 261.45) * mm});
            skLineSegment(sketch, "E5109", {"start": v(-501.34, 261.45) * mm, "end": v(-481.6, 261.45) * mm});
            skLineSegment(sketch, "E5110", {"start": v(506.9, -15.94) * mm, "end": v(507.3, -15.8) * mm});
            skLineSegment(sketch, "E5111", {"start": v(507.3, -15.8) * mm, "end": v(507.68, -15.66) * mm});
            skLineSegment(sketch, "E5112", {"start": v(507.68, -15.66) * mm, "end": v(508.06, -15.5) * mm});
            skLineSegment(sketch, "E5113", {"start": v(508.06, -15.5) * mm, "end": v(508.44, -15.34) * mm});
            skLineSegment(sketch, "E5114", {"start": v(508.44, -15.34) * mm, "end": v(508.8, -15.16) * mm});
            skLineSegment(sketch, "E5115", {"start": v(508.8, -15.16) * mm, "end": v(509.17, -14.97) * mm});
            skLineSegment(sketch, "E5116", {"start": v(509.17, -14.97) * mm, "end": v(509.53, -14.77) * mm});
            skLineSegment(sketch, "E5117", {"start": v(509.53, -14.77) * mm, "end": v(509.88, -14.55) * mm});
            skLineSegment(sketch, "E5118", {"start": v(509.88, -14.55) * mm, "end": v(510.23, -14.33) * mm});
            skLineSegment(sketch, "E5119", {"start": v(510.23, -14.33) * mm, "end": v(510.57, -14.1) * mm});
            skLineSegment(sketch, "E5120", {"start": v(510.57, -14.1) * mm, "end": v(510.9, -13.85) * mm});
            skLineSegment(sketch, "E5121", {"start": v(510.9, -13.85) * mm, "end": v(511.22, -13.59) * mm});
            skLineSegment(sketch, "E5122", {"start": v(511.22, -13.59) * mm, "end": v(511.54, -13.32) * mm});
            skLineSegment(sketch, "E5123", {"start": v(511.54, -13.32) * mm, "end": v(511.84, -13.05) * mm});
            skLineSegment(sketch, "E5124", {"start": v(511.84, -13.05) * mm, "end": v(512.14, -12.76) * mm});
            skLineSegment(sketch, "E5125", {"start": v(512.14, -12.76) * mm, "end": v(512.43, -12.46) * mm});
            skLineSegment(sketch, "E5126", {"start": v(512.43, -12.46) * mm, "end": v(512.66, -12.21) * mm});
            skLineSegment(sketch, "E5127", {"start": v(512.66, -12.21) * mm, "end": v(512.88, -11.96) * mm});
            skLineSegment(sketch, "E5128", {"start": v(512.88, -11.96) * mm, "end": v(513.1, -11.7) * mm});
            skLineSegment(sketch, "E5129", {"start": v(513.1, -11.7) * mm, "end": v(513.3, -11.44) * mm});
            skLineSegment(sketch, "E5130", {"start": v(513.3, -11.44) * mm, "end": v(513.5, -11.18) * mm});
            skLineSegment(sketch, "E5131", {"start": v(513.5, -11.18) * mm, "end": v(513.7, -10.9) * mm});
            skLineSegment(sketch, "E5132", {"start": v(513.7, -10.9) * mm, "end": v(513.89, -10.63) * mm});
            skLineSegment(sketch, "E5133", {"start": v(513.89, -10.63) * mm, "end": v(514.07, -10.35) * mm});
            skLineSegment(sketch, "E5134", {"start": v(514.07, -10.35) * mm, "end": v(514.24, -10.06) * mm});
            skLineSegment(sketch, "E5135", {"start": v(514.24, -10.06) * mm, "end": v(514.4, -9.77) * mm});
            skLineSegment(sketch, "E5136", {"start": v(514.4, -9.77) * mm, "end": v(514.56, -9.48) * mm});
            skLineSegment(sketch, "E5137", {"start": v(514.56, -9.48) * mm, "end": v(514.71, -9.18) * mm});
            skLineSegment(sketch, "E5138", {"start": v(514.71, -9.18) * mm, "end": v(514.85, -8.88) * mm});
            skLineSegment(sketch, "E5139", {"start": v(514.85, -8.88) * mm, "end": v(514.99, -8.58) * mm});
            skLineSegment(sketch, "E5140", {"start": v(514.99, -8.58) * mm, "end": v(515.11, -8.27) * mm});
            skLineSegment(sketch, "E5141", {"start": v(515.11, -8.27) * mm, "end": v(515.23, -7.96) * mm});
            skLineSegment(sketch, "E5142", {"start": v(515.23, -7.96) * mm, "end": v(515.34, -7.65) * mm});
            skLineSegment(sketch, "E5143", {"start": v(515.34, -7.65) * mm, "end": v(515.45, -7.34) * mm});
            skLineSegment(sketch, "E5144", {"start": v(515.45, -7.34) * mm, "end": v(515.54, -7.02) * mm});
            skLineSegment(sketch, "E5145", {"start": v(515.54, -7.02) * mm, "end": v(515.63, -6.7) * mm});
            skLineSegment(sketch, "E5146", {"start": v(515.63, -6.7) * mm, "end": v(515.7, -6.38) * mm});
            skLineSegment(sketch, "E5147", {"start": v(515.7, -6.38) * mm, "end": v(515.78, -6.05) * mm});
            skLineSegment(sketch, "E5148", {"start": v(515.78, -6.05) * mm, "end": v(515.84, -5.72) * mm});
            skLineSegment(sketch, "E5149", {"start": v(515.84, -5.72) * mm, "end": v(515.9, -5.4) * mm});
            skLineSegment(sketch, "E5150", {"start": v(515.9, -5.4) * mm, "end": v(515.94, -5.06) * mm});
            skLineSegment(sketch, "E5151", {"start": v(515.94, -5.06) * mm, "end": v(515.98, -4.73) * mm});
            skLineSegment(sketch, "E5152", {"start": v(515.98, -4.73) * mm, "end": v(516, -4.4) * mm});
            skLineSegment(sketch, "E5153", {"start": v(516, -4.4) * mm, "end": v(516.02, -4.07) * mm});
            skLineSegment(sketch, "E5154", {"start": v(516.02, -4.07) * mm, "end": v(516.04, -3.73) * mm});
            skLineSegment(sketch, "E5155", {"start": v(516.04, -3.73) * mm, "end": v(516.04, -3.4) * mm});
            skLineSegment(sketch, "E5156", {"start": v(516.04, -3.4) * mm, "end": v(516.03, -3.06) * mm});
            skLineSegment(sketch, "E5157", {"start": v(516.03, -3.06) * mm, "end": v(516.02, -2.72) * mm});
            skLineSegment(sketch, "E5158", {"start": v(516.02, -2.72) * mm, "end": v(516.03, -2.41) * mm});
            skLineSegment(sketch, "E5159", {"start": v(516.03, -2.41) * mm, "end": v(516.03, -2.1) * mm});
            skLineSegment(sketch, "E5160", {"start": v(516.03, -2.1) * mm, "end": v(516.02, -1.8) * mm});
            skLineSegment(sketch, "E5161", {"start": v(516.02, -1.8) * mm, "end": v(516, -1.49) * mm});
            skLineSegment(sketch, "E5162", {"start": v(516, -1.49) * mm, "end": v(515.98, -1.18) * mm});
            skLineSegment(sketch, "E5163", {"start": v(515.98, -1.18) * mm, "end": v(515.95, -0.87) * mm});
            skLineSegment(sketch, "E5164", {"start": v(515.95, -0.87) * mm, "end": v(515.91, -0.57) * mm});
            skLineSegment(sketch, "E5165", {"start": v(515.91, -0.57) * mm, "end": v(515.87, -0.27) * mm});
            skLineSegment(sketch, "E5166", {"start": v(515.87, -0.27) * mm, "end": v(515.81, 0.03) * mm});
            skLineSegment(sketch, "E5167", {"start": v(515.81, 0.03) * mm, "end": v(515.75, 0.33) * mm});
            skLineSegment(sketch, "E5168", {"start": v(515.75, 0.33) * mm, "end": v(515.68, 0.63) * mm});
            skLineSegment(sketch, "E5169", {"start": v(515.68, 0.63) * mm, "end": v(515.6, 0.93) * mm});
            skLineSegment(sketch, "E5170", {"start": v(515.6, 0.93) * mm, "end": v(515.52, 1.22) * mm});
            skLineSegment(sketch, "E5171", {"start": v(515.52, 1.22) * mm, "end": v(515.43, 1.5) * mm});
            skLineSegment(sketch, "E5172", {"start": v(515.43, 1.5) * mm, "end": v(515.33, 1.8) * mm});
            skLineSegment(sketch, "E5173", {"start": v(515.33, 1.8) * mm, "end": v(515.23, 2.08) * mm});
            skLineSegment(sketch, "E5174", {"start": v(515.23, 2.08) * mm, "end": v(515.11, 2.37) * mm});
            skLineSegment(sketch, "E5175", {"start": v(515.11, 2.37) * mm, "end": v(515, 2.65) * mm});
            skLineSegment(sketch, "E5176", {"start": v(515, 2.65) * mm, "end": v(514.86, 2.92) * mm});
            skLineSegment(sketch, "E5177", {"start": v(514.86, 2.92) * mm, "end": v(514.73, 3.2) * mm});
            skLineSegment(sketch, "E5178", {"start": v(514.73, 3.2) * mm, "end": v(514.59, 3.47) * mm});
            skLineSegment(sketch, "E5179", {"start": v(514.59, 3.47) * mm, "end": v(514.44, 3.74) * mm});
            skLineSegment(sketch, "E5180", {"start": v(514.44, 3.74) * mm, "end": v(514.28, 4) * mm});
            skLineSegment(sketch, "E5181", {"start": v(514.28, 4) * mm, "end": v(514.12, 4.26) * mm});
            skLineSegment(sketch, "E5182", {"start": v(514.12, 4.26) * mm, "end": v(513.95, 4.51) * mm});
            skLineSegment(sketch, "E5183", {"start": v(513.95, 4.51) * mm, "end": v(513.78, 4.76) * mm});
            skLineSegment(sketch, "E5184", {"start": v(513.78, 4.76) * mm, "end": v(513.6, 5.01) * mm});
            skLineSegment(sketch, "E5185", {"start": v(513.6, 5.01) * mm, "end": v(513.4, 5.25) * mm});
            skLineSegment(sketch, "E5186", {"start": v(513.4, 5.25) * mm, "end": v(513.2, 5.5) * mm});
            skLineSegment(sketch, "E5187", {"start": v(513.2, 5.5) * mm, "end": v(513, 5.72) * mm});
            skLineSegment(sketch, "E5188", {"start": v(513, 5.72) * mm, "end": v(512.8, 5.95) * mm});
            skLineSegment(sketch, "E5189", {"start": v(512.8, 5.95) * mm, "end": v(512.58, 6.17) * mm});
            skLineSegment(sketch, "E5190", {"start": v(512.58, 6.17) * mm, "end": v(512.28, 6.48) * mm});
            skLineSegment(sketch, "E5191", {"start": v(512.28, 6.48) * mm, "end": v(511.97, 6.76) * mm});
            skLineSegment(sketch, "E5192", {"start": v(511.97, 6.76) * mm, "end": v(511.65, 7.03) * mm});
            skLineSegment(sketch, "E5193", {"start": v(511.65, 7.03) * mm, "end": v(511.32, 7.28) * mm});
            skLineSegment(sketch, "E5194", {"start": v(511.32, 7.28) * mm, "end": v(510.98, 7.51) * mm});
            skLineSegment(sketch, "E5195", {"start": v(510.98, 7.51) * mm, "end": v(510.63, 7.73) * mm});
            skLineSegment(sketch, "E5196", {"start": v(510.63, 7.73) * mm, "end": v(510.27, 7.93) * mm});
            skLineSegment(sketch, "E5197", {"start": v(510.27, 7.93) * mm, "end": v(509.9, 8.1) * mm});
            skLineSegment(sketch, "E5198", {"start": v(509.9, 8.1) * mm, "end": v(509.54, 8.27) * mm});
            skLineSegment(sketch, "E5199", {"start": v(509.54, 8.27) * mm, "end": v(509.16, 8.42) * mm});
            skLineSegment(sketch, "E5200", {"start": v(509.16, 8.42) * mm, "end": v(508.78, 8.54) * mm});
            skLineSegment(sketch, "E5201", {"start": v(508.78, 8.54) * mm, "end": v(508.4, 8.65) * mm});
            skLineSegment(sketch, "E5202", {"start": v(508.4, 8.65) * mm, "end": v(508, 8.74) * mm});
            skLineSegment(sketch, "E5203", {"start": v(508, 8.74) * mm, "end": v(507.6, 8.82) * mm});
            skLineSegment(sketch, "E5204", {"start": v(507.6, 8.82) * mm, "end": v(507.2, 8.87) * mm});
            skLineSegment(sketch, "E5205", {"start": v(507.2, 8.87) * mm, "end": v(506.81, 8.91) * mm});
            skLineSegment(sketch, "E5206", {"start": v(506.81, 8.91) * mm, "end": v(506.41, 8.93) * mm});
            skLineSegment(sketch, "E5207", {"start": v(506.41, 8.93) * mm, "end": v(506, 8.93) * mm});
            skLineSegment(sketch, "E5208", {"start": v(506, 8.93) * mm, "end": v(505.6, 8.92) * mm});
            skLineSegment(sketch, "E5209", {"start": v(505.6, 8.92) * mm, "end": v(505.2, 8.88) * mm});
            skLineSegment(sketch, "E5210", {"start": v(505.2, 8.88) * mm, "end": v(504.81, 8.83) * mm});
            skLineSegment(sketch, "E5211", {"start": v(504.81, 8.83) * mm, "end": v(504.41, 8.76) * mm});
            skLineSegment(sketch, "E5212", {"start": v(504.41, 8.76) * mm, "end": v(504.02, 8.67) * mm});
            skLineSegment(sketch, "E5213", {"start": v(504.02, 8.67) * mm, "end": v(503.63, 8.56) * mm});
            skLineSegment(sketch, "E5214", {"start": v(503.63, 8.56) * mm, "end": v(503.24, 8.44) * mm});
            skLineSegment(sketch, "E5215", {"start": v(503.24, 8.44) * mm, "end": v(502.86, 8.3) * mm});
            skLineSegment(sketch, "E5216", {"start": v(502.86, 8.3) * mm, "end": v(502.48, 8.13) * mm});
            skLineSegment(sketch, "E5217", {"start": v(502.48, 8.13) * mm, "end": v(502.11, 7.95) * mm});
            skLineSegment(sketch, "E5218", {"start": v(502.11, 7.95) * mm, "end": v(501.75, 7.75) * mm});
            skLineSegment(sketch, "E5219", {"start": v(501.75, 7.75) * mm, "end": v(501.4, 7.53) * mm});
            skLineSegment(sketch, "E5220", {"start": v(501.4, 7.53) * mm, "end": v(501.05, 7.3) * mm});
            skLineSegment(sketch, "E5221", {"start": v(501.05, 7.3) * mm, "end": v(500.7, 7.04) * mm});
            skLineSegment(sketch, "E5222", {"start": v(500.7, 7.04) * mm, "end": v(500.44, 6.78) * mm});
            skLineSegment(sketch, "E5223", {"start": v(500.44, 6.78) * mm, "end": v(500.19, 6.51) * mm});
            skLineSegment(sketch, "E5224", {"start": v(500.19, 6.51) * mm, "end": v(499.94, 6.24) * mm});
            skLineSegment(sketch, "E5225", {"start": v(499.94, 6.24) * mm, "end": v(499.7, 5.96) * mm});
            skLineSegment(sketch, "E5226", {"start": v(499.7, 5.96) * mm, "end": v(499.47, 5.68) * mm});
            skLineSegment(sketch, "E5227", {"start": v(499.47, 5.68) * mm, "end": v(499.25, 5.4) * mm});
            skLineSegment(sketch, "E5228", {"start": v(499.25, 5.4) * mm, "end": v(499.03, 5.1) * mm});
            skLineSegment(sketch, "E5229", {"start": v(499.03, 5.1) * mm, "end": v(498.83, 4.8) * mm});
            skLineSegment(sketch, "E5230", {"start": v(498.83, 4.8) * mm, "end": v(498.63, 4.5) * mm});
            skLineSegment(sketch, "E5231", {"start": v(498.63, 4.5) * mm, "end": v(498.44, 4.19) * mm});
            skLineSegment(sketch, "E5232", {"start": v(498.44, 4.19) * mm, "end": v(498.26, 3.87) * mm});
            skLineSegment(sketch, "E5233", {"start": v(498.26, 3.87) * mm, "end": v(498.08, 3.55) * mm});
            skLineSegment(sketch, "E5234", {"start": v(498.08, 3.55) * mm, "end": v(497.92, 3.23) * mm});
            skLineSegment(sketch, "E5235", {"start": v(497.92, 3.23) * mm, "end": v(497.77, 2.9) * mm});
            skLineSegment(sketch, "E5236", {"start": v(497.77, 2.9) * mm, "end": v(497.62, 2.57) * mm});
            skLineSegment(sketch, "E5237", {"start": v(497.62, 2.57) * mm, "end": v(497.48, 2.24) * mm});
            skLineSegment(sketch, "E5238", {"start": v(497.48, 2.24) * mm, "end": v(497.35, 1.9) * mm});
            skLineSegment(sketch, "E5239", {"start": v(497.35, 1.9) * mm, "end": v(497.23, 1.56) * mm});
            skLineSegment(sketch, "E5240", {"start": v(497.23, 1.56) * mm, "end": v(497.12, 1.21) * mm});
            skLineSegment(sketch, "E5241", {"start": v(497.12, 1.21) * mm, "end": v(497.02, 0.87) * mm});
            skLineSegment(sketch, "E5242", {"start": v(497.02, 0.87) * mm, "end": v(496.93, 0.52) * mm});
            skLineSegment(sketch, "E5243", {"start": v(496.93, 0.52) * mm, "end": v(496.85, 0.16) * mm});
            skLineSegment(sketch, "E5244", {"start": v(496.85, 0.16) * mm, "end": v(496.77, -0.2) * mm});
            skLineSegment(sketch, "E5245", {"start": v(496.77, -0.2) * mm, "end": v(496.7, -0.55) * mm});
            skLineSegment(sketch, "E5246", {"start": v(496.7, -0.55) * mm, "end": v(496.66, -0.9) * mm});
            skLineSegment(sketch, "E5247", {"start": v(496.66, -0.9) * mm, "end": v(496.61, -1.27) * mm});
            skLineSegment(sketch, "E5248", {"start": v(496.61, -1.27) * mm, "end": v(496.58, -1.63) * mm});
            skLineSegment(sketch, "E5249", {"start": v(496.58, -1.63) * mm, "end": v(496.55, -2) * mm});
            skLineSegment(sketch, "E5250", {"start": v(496.55, -2) * mm, "end": v(496.54, -2.36) * mm});
            skLineSegment(sketch, "E5251", {"start": v(496.54, -2.36) * mm, "end": v(496.53, -2.73) * mm});
            skLineSegment(sketch, "E5252", {"start": v(496.53, -2.73) * mm, "end": v(496.54, -3.1) * mm});
            skLineSegment(sketch, "E5253", {"start": v(496.54, -3.1) * mm, "end": v(496.55, -3.47) * mm});
            skLineSegment(sketch, "E5254", {"start": v(496.55, -3.47) * mm, "end": v(496.6, -3.96) * mm});
            skLineSegment(sketch, "E5255", {"start": v(496.6, -3.96) * mm, "end": v(496.64, -4.45) * mm});
            skLineSegment(sketch, "E5256", {"start": v(496.64, -4.45) * mm, "end": v(496.64, -4.93) * mm});
            skLineSegment(sketch, "E5257", {"start": v(496.64, -4.93) * mm, "end": v(496.63, -5.41) * mm});
            skLineSegment(sketch, "E5258", {"start": v(496.63, -5.41) * mm, "end": v(496.59, -5.9) * mm});
            skLineSegment(sketch, "E5259", {"start": v(496.59, -5.9) * mm, "end": v(496.53, -6.36) * mm});
            skLineSegment(sketch, "E5260", {"start": v(496.53, -6.36) * mm, "end": v(496.44, -6.83) * mm});
            skLineSegment(sketch, "E5261", {"start": v(496.44, -6.83) * mm, "end": v(496.34, -7.29) * mm});
            skLineSegment(sketch, "E5262", {"start": v(496.34, -7.29) * mm, "end": v(496.2, -7.74) * mm});
            skLineSegment(sketch, "E5263", {"start": v(496.2, -7.74) * mm, "end": v(496.06, -8.18) * mm});
            skLineSegment(sketch, "E5264", {"start": v(496.06, -8.18) * mm, "end": v(495.9, -8.62) * mm});
            skLineSegment(sketch, "E5265", {"start": v(495.9, -8.62) * mm, "end": v(495.7, -9.05) * mm});
            skLineSegment(sketch, "E5266", {"start": v(495.7, -9.05) * mm, "end": v(495.5, -9.46) * mm});
            skLineSegment(sketch, "E5267", {"start": v(495.5, -9.46) * mm, "end": v(495.27, -9.87) * mm});
            skLineSegment(sketch, "E5268", {"start": v(495.27, -9.87) * mm, "end": v(495.03, -10.27) * mm});
            skLineSegment(sketch, "E5269", {"start": v(495.03, -10.27) * mm, "end": v(494.77, -10.65) * mm});
            skLineSegment(sketch, "E5270", {"start": v(494.77, -10.65) * mm, "end": v(494.49, -11.02) * mm});
            skLineSegment(sketch, "E5271", {"start": v(494.49, -11.02) * mm, "end": v(494.2, -11.38) * mm});
            skLineSegment(sketch, "E5272", {"start": v(494.2, -11.38) * mm, "end": v(493.88, -11.72) * mm});
            skLineSegment(sketch, "E5273", {"start": v(493.88, -11.72) * mm, "end": v(493.55, -12.05) * mm});
            skLineSegment(sketch, "E5274", {"start": v(493.55, -12.05) * mm, "end": v(493.2, -12.37) * mm});
            skLineSegment(sketch, "E5275", {"start": v(493.2, -12.37) * mm, "end": v(492.85, -12.67) * mm});
            skLineSegment(sketch, "E5276", {"start": v(492.85, -12.67) * mm, "end": v(492.48, -12.95) * mm});
            skLineSegment(sketch, "E5277", {"start": v(492.48, -12.95) * mm, "end": v(492.09, -13.22) * mm});
            skLineSegment(sketch, "E5278", {"start": v(492.09, -13.22) * mm, "end": v(491.69, -13.46) * mm});
            skLineSegment(sketch, "E5279", {"start": v(491.69, -13.46) * mm, "end": v(491.27, -13.7) * mm});
            skLineSegment(sketch, "E5280", {"start": v(491.27, -13.7) * mm, "end": v(490.85, -13.9) * mm});
            skLineSegment(sketch, "E5281", {"start": v(490.85, -13.9) * mm, "end": v(490.4, -14.1) * mm});
            skLineSegment(sketch, "E5282", {"start": v(490.4, -14.1) * mm, "end": v(489.96, -14.27) * mm});
            skLineSegment(sketch, "E5283", {"start": v(489.96, -14.27) * mm, "end": v(489.5, -14.42) * mm});
            skLineSegment(sketch, "E5284", {"start": v(489.5, -14.42) * mm, "end": v(489.02, -14.54) * mm});
            skLineSegment(sketch, "E5285", {"start": v(489.02, -14.54) * mm, "end": v(488.54, -14.65) * mm});
            skLineSegment(sketch, "E5286", {"start": v(488.54, -14.65) * mm, "end": v(488.14, -14.65) * mm});
            skLineSegment(sketch, "E5287", {"start": v(488.14, -14.65) * mm, "end": v(487.74, -14.63) * mm});
            skLineSegment(sketch, "E5288", {"start": v(487.74, -14.63) * mm, "end": v(487.35, -14.58) * mm});
            skLineSegment(sketch, "E5289", {"start": v(487.35, -14.58) * mm, "end": v(486.96, -14.51) * mm});
            skLineSegment(sketch, "E5290", {"start": v(486.96, -14.51) * mm, "end": v(486.58, -14.42) * mm});
            skLineSegment(sketch, "E5291", {"start": v(486.58, -14.42) * mm, "end": v(486.2, -14.31) * mm});
            skLineSegment(sketch, "E5292", {"start": v(486.2, -14.31) * mm, "end": v(485.83, -14.18) * mm});
            skLineSegment(sketch, "E5293", {"start": v(485.83, -14.18) * mm, "end": v(485.47, -14.03) * mm});
            skLineSegment(sketch, "E5294", {"start": v(485.47, -14.03) * mm, "end": v(485.11, -13.86) * mm});
            skLineSegment(sketch, "E5295", {"start": v(485.11, -13.86) * mm, "end": v(484.77, -13.67) * mm});
            skLineSegment(sketch, "E5296", {"start": v(484.77, -13.67) * mm, "end": v(484.44, -13.46) * mm});
            skLineSegment(sketch, "E5297", {"start": v(484.44, -13.46) * mm, "end": v(484.12, -13.24) * mm});
            skLineSegment(sketch, "E5298", {"start": v(484.12, -13.24) * mm, "end": v(483.8, -13) * mm});
            skLineSegment(sketch, "E5299", {"start": v(483.8, -13) * mm, "end": v(483.51, -12.73) * mm});
            skLineSegment(sketch, "E5300", {"start": v(483.51, -12.73) * mm, "end": v(483.23, -12.45) * mm});
            skLineSegment(sketch, "E5301", {"start": v(483.23, -12.45) * mm, "end": v(482.96, -12.15) * mm});
            skLineSegment(sketch, "E5302", {"start": v(482.96, -12.15) * mm, "end": v(482.75, -11.9) * mm});
            skLineSegment(sketch, "E5303", {"start": v(482.75, -11.9) * mm, "end": v(482.53, -11.66) * mm});
            skLineSegment(sketch, "E5304", {"start": v(482.53, -11.66) * mm, "end": v(482.33, -11.4) * mm});
            skLineSegment(sketch, "E5305", {"start": v(482.33, -11.4) * mm, "end": v(482.13, -11.14) * mm});
            skLineSegment(sketch, "E5306", {"start": v(482.13, -11.14) * mm, "end": v(481.94, -10.88) * mm});
            skLineSegment(sketch, "E5307", {"start": v(481.94, -10.88) * mm, "end": v(481.76, -10.61) * mm});
            skLineSegment(sketch, "E5308", {"start": v(481.76, -10.61) * mm, "end": v(481.59, -10.34) * mm});
            skLineSegment(sketch, "E5309", {"start": v(481.59, -10.34) * mm, "end": v(481.42, -10.06) * mm});
            skLineSegment(sketch, "E5310", {"start": v(481.42, -10.06) * mm, "end": v(481.25, -9.78) * mm});
            skLineSegment(sketch, "E5311", {"start": v(481.25, -9.78) * mm, "end": v(481.1, -9.5) * mm});
            skLineSegment(sketch, "E5312", {"start": v(481.1, -9.5) * mm, "end": v(480.95, -9.21) * mm});
            skLineSegment(sketch, "E5313", {"start": v(480.95, -9.21) * mm, "end": v(480.81, -8.92) * mm});
            skLineSegment(sketch, "E5314", {"start": v(480.81, -8.92) * mm, "end": v(480.68, -8.63) * mm});
            skLineSegment(sketch, "E5315", {"start": v(480.68, -8.63) * mm, "end": v(480.55, -8.33) * mm});
            skLineSegment(sketch, "E5316", {"start": v(480.55, -8.33) * mm, "end": v(480.44, -8.03) * mm});
            skLineSegment(sketch, "E5317", {"start": v(480.44, -8.03) * mm, "end": v(480.33, -7.73) * mm});
            skLineSegment(sketch, "E5318", {"start": v(480.33, -7.73) * mm, "end": v(480.22, -7.43) * mm});
            skLineSegment(sketch, "E5319", {"start": v(480.22, -7.43) * mm, "end": v(480.13, -7.12) * mm});
            skLineSegment(sketch, "E5320", {"start": v(480.13, -7.12) * mm, "end": v(480.04, -6.8) * mm});
            skLineSegment(sketch, "E5321", {"start": v(480.04, -6.8) * mm, "end": v(479.96, -6.5) * mm});
            skLineSegment(sketch, "E5322", {"start": v(479.96, -6.5) * mm, "end": v(479.89, -6.18) * mm});
            skLineSegment(sketch, "E5323", {"start": v(479.89, -6.18) * mm, "end": v(479.82, -5.87) * mm});
            skLineSegment(sketch, "E5324", {"start": v(479.82, -5.87) * mm, "end": v(479.77, -5.55) * mm});
            skLineSegment(sketch, "E5325", {"start": v(479.77, -5.55) * mm, "end": v(479.72, -5.23) * mm});
            skLineSegment(sketch, "E5326", {"start": v(479.72, -5.23) * mm, "end": v(479.68, -4.9) * mm});
            skLineSegment(sketch, "E5327", {"start": v(479.68, -4.9) * mm, "end": v(479.65, -4.59) * mm});
            skLineSegment(sketch, "E5328", {"start": v(479.65, -4.59) * mm, "end": v(479.62, -4.26) * mm});
            skLineSegment(sketch, "E5329", {"start": v(479.62, -4.26) * mm, "end": v(479.6, -3.94) * mm});
            skLineSegment(sketch, "E5330", {"start": v(479.6, -3.94) * mm, "end": v(479.6, -3.61) * mm});
            skLineSegment(sketch, "E5331", {"start": v(479.6, -3.61) * mm, "end": v(479.6, -3.29) * mm});
            skLineSegment(sketch, "E5332", {"start": v(479.6, -3.29) * mm, "end": v(479.6, -2.96) * mm});
            skLineSegment(sketch, "E5333", {"start": v(479.6, -2.96) * mm, "end": v(479.62, -2.64) * mm});
            skLineSegment(sketch, "E5334", {"start": v(479.62, -2.64) * mm, "end": v(479.62, -2.06) * mm});
            skLineSegment(sketch, "E5335", {"start": v(479.62, -2.06) * mm, "end": v(479.65, -1.49) * mm});
            skLineSegment(sketch, "E5336", {"start": v(479.65, -1.49) * mm, "end": v(479.7, -0.92) * mm});
            skLineSegment(sketch, "E5337", {"start": v(479.7, -0.92) * mm, "end": v(479.79, -0.36) * mm});
            skLineSegment(sketch, "E5338", {"start": v(479.79, -0.36) * mm, "end": v(479.9, 0.2) * mm});
            skLineSegment(sketch, "E5339", {"start": v(479.9, 0.2) * mm, "end": v(480.03, 0.75) * mm});
            skLineSegment(sketch, "E5340", {"start": v(480.03, 0.75) * mm, "end": v(480.2, 1.3) * mm});
            skLineSegment(sketch, "E5341", {"start": v(480.2, 1.3) * mm, "end": v(480.38, 1.83) * mm});
            skLineSegment(sketch, "E5342", {"start": v(480.38, 1.83) * mm, "end": v(480.6, 2.36) * mm});
            skLineSegment(sketch, "E5343", {"start": v(480.6, 2.36) * mm, "end": v(480.84, 2.87) * mm});
            skLineSegment(sketch, "E5344", {"start": v(480.84, 2.87) * mm, "end": v(481.1, 3.38) * mm});
            skLineSegment(sketch, "E5345", {"start": v(481.1, 3.38) * mm, "end": v(481.38, 3.87) * mm});
            skLineSegment(sketch, "E5346", {"start": v(481.38, 3.87) * mm, "end": v(481.7, 4.34) * mm});
            skLineSegment(sketch, "E5347", {"start": v(481.7, 4.34) * mm, "end": v(482.03, 4.8) * mm});
            skLineSegment(sketch, "E5348", {"start": v(482.03, 4.8) * mm, "end": v(482.39, 5.25) * mm});
            skLineSegment(sketch, "E5349", {"start": v(482.39, 5.25) * mm, "end": v(482.77, 5.68) * mm});
            skLineSegment(sketch, "E5350", {"start": v(482.77, 5.68) * mm, "end": v(483.05, 5.95) * mm});
            skLineSegment(sketch, "E5351", {"start": v(483.05, 5.95) * mm, "end": v(483.35, 6.2) * mm});
            skLineSegment(sketch, "E5352", {"start": v(483.35, 6.2) * mm, "end": v(483.65, 6.44) * mm});
            skLineSegment(sketch, "E5353", {"start": v(483.65, 6.44) * mm, "end": v(483.96, 6.67) * mm});
            skLineSegment(sketch, "E5354", {"start": v(483.96, 6.67) * mm, "end": v(484.28, 6.88) * mm});
            skLineSegment(sketch, "E5355", {"start": v(484.28, 6.88) * mm, "end": v(484.6, 7.1) * mm});
            skLineSegment(sketch, "E5356", {"start": v(484.6, 7.1) * mm, "end": v(484.94, 7.29) * mm});
            skLineSegment(sketch, "E5357", {"start": v(484.94, 7.29) * mm, "end": v(485.28, 7.47) * mm});
            skLineSegment(sketch, "E5358", {"start": v(485.28, 7.47) * mm, "end": v(485.62, 7.64) * mm});
            skLineSegment(sketch, "E5359", {"start": v(485.62, 7.64) * mm, "end": v(485.97, 7.8) * mm});
            skLineSegment(sketch, "E5360", {"start": v(485.97, 7.8) * mm, "end": v(486.33, 7.95) * mm});
            skLineSegment(sketch, "E5361", {"start": v(486.33, 7.95) * mm, "end": v(486.69, 8.08) * mm});
            skLineSegment(sketch, "E5362", {"start": v(486.69, 8.08) * mm, "end": v(487.06, 8.2) * mm});
            skLineSegment(sketch, "E5363", {"start": v(487.06, 8.2) * mm, "end": v(487.43, 8.32) * mm});
            skLineSegment(sketch, "E5364", {"start": v(487.43, 8.32) * mm, "end": v(487.8, 8.41) * mm});
            skLineSegment(sketch, "E5365", {"start": v(487.8, 8.41) * mm, "end": v(488.18, 8.5) * mm});
            skLineSegment(sketch, "E5366", {"start": v(515.29, 16.78) * mm, "end": v(480.34, 16.78) * mm});
            skLineSegment(sketch, "E5367", {"start": v(515.3, 24.48) * mm, "end": v(480.32, 24.48) * mm});
            skLineSegment(sketch, "E5368", {"start": v(480.32, 24.48) * mm, "end": v(480.32, 37.3) * mm});
            skLineSegment(sketch, "E5369", {"start": v(480.32, 37.3) * mm, "end": v(480.33, 37.61) * mm});
            skLineSegment(sketch, "E5370", {"start": v(480.33, 37.61) * mm, "end": v(480.35, 37.91) * mm});
            skLineSegment(sketch, "E5371", {"start": v(480.35, 37.91) * mm, "end": v(480.38, 38.21) * mm});
            skLineSegment(sketch, "E5372", {"start": v(480.38, 38.21) * mm, "end": v(480.42, 38.51) * mm});
            skLineSegment(sketch, "E5373", {"start": v(480.42, 38.51) * mm, "end": v(480.47, 38.81) * mm});
            skLineSegment(sketch, "E5374", {"start": v(480.47, 38.81) * mm, "end": v(480.52, 39.11) * mm});
            skLineSegment(sketch, "E5375", {"start": v(480.52, 39.11) * mm, "end": v(480.58, 39.4) * mm});
            skLineSegment(sketch, "E5376", {"start": v(480.58, 39.4) * mm, "end": v(480.65, 39.7) * mm});
            skLineSegment(sketch, "E5377", {"start": v(480.65, 39.7) * mm, "end": v(480.72, 40) * mm});
            skLineSegment(sketch, "E5378", {"start": v(480.72, 40) * mm, "end": v(480.8, 40.28) * mm});
            skLineSegment(sketch, "E5379", {"start": v(480.8, 40.28) * mm, "end": v(480.9, 40.57) * mm});
            skLineSegment(sketch, "E5380", {"start": v(480.9, 40.57) * mm, "end": v(480.99, 40.85) * mm});
            skLineSegment(sketch, "E5381", {"start": v(480.99, 40.85) * mm, "end": v(481.2, 41.41) * mm});
            skLineSegment(sketch, "E5382", {"start": v(481.2, 41.41) * mm, "end": v(481.44, 41.96) * mm});
            skLineSegment(sketch, "E5383", {"start": v(481.44, 41.96) * mm, "end": v(481.7, 42.5) * mm});
            skLineSegment(sketch, "E5384", {"start": v(481.7, 42.5) * mm, "end": v(482, 43.02) * mm});
            skLineSegment(sketch, "E5385", {"start": v(482, 43.02) * mm, "end": v(482.16, 43.27) * mm});
            skLineSegment(sketch, "E5386", {"start": v(482.16, 43.27) * mm, "end": v(482.32, 43.53) * mm});
            skLineSegment(sketch, "E5387", {"start": v(482.32, 43.53) * mm, "end": v(482.5, 43.77) * mm});
            skLineSegment(sketch, "E5388", {"start": v(482.5, 43.77) * mm, "end": v(482.67, 44.02) * mm});
            skLineSegment(sketch, "E5389", {"start": v(482.67, 44.02) * mm, "end": v(482.85, 44.26) * mm});
            skLineSegment(sketch, "E5390", {"start": v(482.85, 44.26) * mm, "end": v(483.04, 44.5) * mm});
            skLineSegment(sketch, "E5391", {"start": v(483.04, 44.5) * mm, "end": v(483.23, 44.72) * mm});
            skLineSegment(sketch, "E5392", {"start": v(483.23, 44.72) * mm, "end": v(483.43, 44.95) * mm});
            skLineSegment(sketch, "E5393", {"start": v(483.43, 44.95) * mm, "end": v(483.64, 45.17) * mm});
            skLineSegment(sketch, "E5394", {"start": v(483.64, 45.17) * mm, "end": v(483.85, 45.39) * mm});
            skLineSegment(sketch, "E5395", {"start": v(483.85, 45.39) * mm, "end": v(484.07, 45.6) * mm});
            skLineSegment(sketch, "E5396", {"start": v(484.07, 45.6) * mm, "end": v(484.3, 45.8) * mm});
            skLineSegment(sketch, "E5397", {"start": v(484.3, 45.8) * mm, "end": v(484.66, 46.15) * mm});
            skLineSegment(sketch, "E5398", {"start": v(484.66, 46.15) * mm, "end": v(485.03, 46.5) * mm});
            skLineSegment(sketch, "E5399", {"start": v(485.03, 46.5) * mm, "end": v(485.4, 46.82) * mm});
            skLineSegment(sketch, "E5400", {"start": v(485.4, 46.82) * mm, "end": v(485.79, 47.14) * mm});
            skLineSegment(sketch, "E5401", {"start": v(485.79, 47.14) * mm, "end": v(486.18, 47.45) * mm});
            skLineSegment(sketch, "E5402", {"start": v(486.18, 47.45) * mm, "end": v(486.58, 47.75) * mm});
            skLineSegment(sketch, "E5403", {"start": v(486.58, 47.75) * mm, "end": v(486.98, 48.04) * mm});
            skLineSegment(sketch, "E5404", {"start": v(486.98, 48.04) * mm, "end": v(487.4, 48.32) * mm});
            skLineSegment(sketch, "E5405", {"start": v(487.4, 48.32) * mm, "end": v(487.81, 48.59) * mm});
            skLineSegment(sketch, "E5406", {"start": v(487.81, 48.59) * mm, "end": v(488.24, 48.85) * mm});
            skLineSegment(sketch, "E5407", {"start": v(488.24, 48.85) * mm, "end": v(488.67, 49.1) * mm});
            skLineSegment(sketch, "E5408", {"start": v(488.67, 49.1) * mm, "end": v(489.1, 49.33) * mm});
            skLineSegment(sketch, "E5409", {"start": v(489.1, 49.33) * mm, "end": v(489.55, 49.55) * mm});
            skLineSegment(sketch, "E5410", {"start": v(489.55, 49.55) * mm, "end": v(490, 49.77) * mm});
            skLineSegment(sketch, "E5411", {"start": v(490, 49.77) * mm, "end": v(490.45, 49.97) * mm});
            skLineSegment(sketch, "E5412", {"start": v(490.45, 49.97) * mm, "end": v(490.9, 50.16) * mm});
            skLineSegment(sketch, "E5413", {"start": v(490.9, 50.16) * mm, "end": v(491.37, 50.34) * mm});
            skLineSegment(sketch, "E5414", {"start": v(491.37, 50.34) * mm, "end": v(491.84, 50.5) * mm});
            skLineSegment(sketch, "E5415", {"start": v(491.84, 50.5) * mm, "end": v(492.3, 50.66) * mm});
            skLineSegment(sketch, "E5416", {"start": v(492.3, 50.66) * mm, "end": v(492.78, 50.8) * mm});
            skLineSegment(sketch, "E5417", {"start": v(492.78, 50.8) * mm, "end": v(493.26, 50.94) * mm});
            skLineSegment(sketch, "E5418", {"start": v(493.26, 50.94) * mm, "end": v(493.74, 51.06) * mm});
            skLineSegment(sketch, "E5419", {"start": v(493.74, 51.06) * mm, "end": v(494.22, 51.17) * mm});
            skLineSegment(sketch, "E5420", {"start": v(494.22, 51.17) * mm, "end": v(494.71, 51.26) * mm});
            skLineSegment(sketch, "E5421", {"start": v(494.71, 51.26) * mm, "end": v(495.2, 51.35) * mm});
            skLineSegment(sketch, "E5422", {"start": v(495.2, 51.35) * mm, "end": v(495.7, 51.42) * mm});
            skLineSegment(sketch, "E5423", {"start": v(495.7, 51.42) * mm, "end": v(496.2, 51.48) * mm});
            skLineSegment(sketch, "E5424", {"start": v(496.2, 51.48) * mm, "end": v(496.69, 51.53) * mm});
            skLineSegment(sketch, "E5425", {"start": v(496.69, 51.53) * mm, "end": v(497.19, 51.56) * mm});
            skLineSegment(sketch, "E5426", {"start": v(497.19, 51.56) * mm, "end": v(497.69, 51.58) * mm});
            skLineSegment(sketch, "E5427", {"start": v(497.69, 51.58) * mm, "end": v(498.2, 51.6) * mm});
            skLineSegment(sketch, "E5428", {"start": v(498.2, 51.6) * mm, "end": v(498.7, 51.6) * mm});
            skLineSegment(sketch, "E5429", {"start": v(498.7, 51.6) * mm, "end": v(499.12, 51.6) * mm});
            skLineSegment(sketch, "E5430", {"start": v(499.12, 51.6) * mm, "end": v(499.54, 51.6) * mm});
            skLineSegment(sketch, "E5431", {"start": v(499.54, 51.6) * mm, "end": v(499.96, 51.59) * mm});
            skLineSegment(sketch, "E5432", {"start": v(499.96, 51.59) * mm, "end": v(500.38, 51.57) * mm});
            skLineSegment(sketch, "E5433", {"start": v(500.38, 51.57) * mm, "end": v(500.8, 51.54) * mm});
            skLineSegment(sketch, "E5434", {"start": v(500.8, 51.54) * mm, "end": v(501.2, 51.5) * mm});
            skLineSegment(sketch, "E5435", {"start": v(501.2, 51.5) * mm, "end": v(501.62, 51.44) * mm});
            skLineSegment(sketch, "E5436", {"start": v(501.62, 51.44) * mm, "end": v(502.04, 51.38) * mm});
            skLineSegment(sketch, "E5437", {"start": v(502.04, 51.38) * mm, "end": v(502.45, 51.3) * mm});
            skLineSegment(sketch, "E5438", {"start": v(502.45, 51.3) * mm, "end": v(502.86, 51.23) * mm});
            skLineSegment(sketch, "E5439", {"start": v(502.86, 51.23) * mm, "end": v(503.26, 51.13) * mm});
            skLineSegment(sketch, "E5440", {"start": v(503.26, 51.13) * mm, "end": v(503.67, 51.03) * mm});
            skLineSegment(sketch, "E5441", {"start": v(503.67, 51.03) * mm, "end": v(504.07, 50.92) * mm});
            skLineSegment(sketch, "E5442", {"start": v(504.07, 50.92) * mm, "end": v(504.46, 50.8) * mm});
            skLineSegment(sketch, "E5443", {"start": v(504.46, 50.8) * mm, "end": v(504.86, 50.67) * mm});
            skLineSegment(sketch, "E5444", {"start": v(504.86, 50.67) * mm, "end": v(505.25, 50.53) * mm});
            skLineSegment(sketch, "E5445", {"start": v(505.25, 50.53) * mm, "end": v(505.64, 50.38) * mm});
            skLineSegment(sketch, "E5446", {"start": v(505.64, 50.38) * mm, "end": v(506.02, 50.22) * mm});
            skLineSegment(sketch, "E5447", {"start": v(506.02, 50.22) * mm, "end": v(506.4, 50.05) * mm});
            skLineSegment(sketch, "E5448", {"start": v(506.4, 50.05) * mm, "end": v(506.78, 49.87) * mm});
            skLineSegment(sketch, "E5449", {"start": v(506.78, 49.87) * mm, "end": v(507.15, 49.68) * mm});
            skLineSegment(sketch, "E5450", {"start": v(507.15, 49.68) * mm, "end": v(507.52, 49.49) * mm});
            skLineSegment(sketch, "E5451", {"start": v(507.52, 49.49) * mm, "end": v(507.88, 49.28) * mm});
            skLineSegment(sketch, "E5452", {"start": v(507.88, 49.28) * mm, "end": v(508.24, 49.07) * mm});
            skLineSegment(sketch, "E5453", {"start": v(508.24, 49.07) * mm, "end": v(508.59, 48.84) * mm});
            skLineSegment(sketch, "E5454", {"start": v(508.59, 48.84) * mm, "end": v(508.94, 48.6) * mm});
            skLineSegment(sketch, "E5455", {"start": v(508.94, 48.6) * mm, "end": v(509.28, 48.37) * mm});
            skLineSegment(sketch, "E5456", {"start": v(509.28, 48.37) * mm, "end": v(509.61, 48.12) * mm});
            skLineSegment(sketch, "E5457", {"start": v(509.61, 48.12) * mm, "end": v(509.94, 47.86) * mm});
            skLineSegment(sketch, "E5458", {"start": v(509.94, 47.86) * mm, "end": v(510.27, 47.6) * mm});
            skLineSegment(sketch, "E5459", {"start": v(510.27, 47.6) * mm, "end": v(510.59, 47.32) * mm});
            skLineSegment(sketch, "E5460", {"start": v(510.59, 47.32) * mm, "end": v(510.9, 47.03) * mm});
            skLineSegment(sketch, "E5461", {"start": v(510.9, 47.03) * mm, "end": v(511.15, 46.8) * mm});
            skLineSegment(sketch, "E5462", {"start": v(511.15, 46.8) * mm, "end": v(511.39, 46.55) * mm});
            skLineSegment(sketch, "E5463", {"start": v(511.39, 46.55) * mm, "end": v(511.62, 46.3) * mm});
            skLineSegment(sketch, "E5464", {"start": v(511.62, 46.3) * mm, "end": v(511.85, 46.04) * mm});
            skLineSegment(sketch, "E5465", {"start": v(511.85, 46.04) * mm, "end": v(512.08, 45.78) * mm});
            skLineSegment(sketch, "E5466", {"start": v(512.08, 45.78) * mm, "end": v(512.3, 45.51) * mm});
            skLineSegment(sketch, "E5467", {"start": v(512.3, 45.51) * mm, "end": v(512.5, 45.24) * mm});
            skLineSegment(sketch, "E5468", {"start": v(512.5, 45.24) * mm, "end": v(512.7, 44.97) * mm});
            skLineSegment(sketch, "E5469", {"start": v(512.7, 44.97) * mm, "end": v(512.9, 44.68) * mm});
            skLineSegment(sketch, "E5470", {"start": v(512.9, 44.68) * mm, "end": v(513.08, 44.4) * mm});
            skLineSegment(sketch, "E5471", {"start": v(513.08, 44.4) * mm, "end": v(513.27, 44.11) * mm});
            skLineSegment(sketch, "E5472", {"start": v(513.27, 44.11) * mm, "end": v(513.44, 43.82) * mm});
            skLineSegment(sketch, "E5473", {"start": v(513.44, 43.82) * mm, "end": v(513.6, 43.52) * mm});
            skLineSegment(sketch, "E5474", {"start": v(513.6, 43.52) * mm, "end": v(513.76, 43.22) * mm});
            skLineSegment(sketch, "E5475", {"start": v(513.76, 43.22) * mm, "end": v(513.92, 42.91) * mm});
            skLineSegment(sketch, "E5476", {"start": v(513.92, 42.91) * mm, "end": v(514.06, 42.6) * mm});
            skLineSegment(sketch, "E5477", {"start": v(514.06, 42.6) * mm, "end": v(514.2, 42.3) * mm});
            skLineSegment(sketch, "E5478", {"start": v(514.2, 42.3) * mm, "end": v(514.32, 41.98) * mm});
            skLineSegment(sketch, "E5479", {"start": v(514.32, 41.98) * mm, "end": v(514.45, 41.66) * mm});
            skLineSegment(sketch, "E5480", {"start": v(514.45, 41.66) * mm, "end": v(514.56, 41.34) * mm});
            skLineSegment(sketch, "E5481", {"start": v(514.56, 41.34) * mm, "end": v(514.67, 41.01) * mm});
            skLineSegment(sketch, "E5482", {"start": v(514.67, 41.01) * mm, "end": v(514.76, 40.69) * mm});
            skLineSegment(sketch, "E5483", {"start": v(514.76, 40.69) * mm, "end": v(514.85, 40.36) * mm});
            skLineSegment(sketch, "E5484", {"start": v(514.85, 40.36) * mm, "end": v(514.94, 40.03) * mm});
            skLineSegment(sketch, "E5485", {"start": v(514.94, 40.03) * mm, "end": v(515, 39.7) * mm});
            skLineSegment(sketch, "E5486", {"start": v(515, 39.7) * mm, "end": v(515.08, 39.36) * mm});
            skLineSegment(sketch, "E5487", {"start": v(515.08, 39.36) * mm, "end": v(515.13, 39.02) * mm});
            skLineSegment(sketch, "E5488", {"start": v(515.13, 39.02) * mm, "end": v(515.18, 38.68) * mm});
            skLineSegment(sketch, "E5489", {"start": v(515.18, 38.68) * mm, "end": v(515.22, 38.34) * mm});
            skLineSegment(sketch, "E5490", {"start": v(515.22, 38.34) * mm, "end": v(515.26, 38) * mm});
            skLineSegment(sketch, "E5491", {"start": v(515.26, 38) * mm, "end": v(515.28, 37.65) * mm});
            skLineSegment(sketch, "E5492", {"start": v(515.28, 37.65) * mm, "end": v(515.3, 37.3) * mm});
            skLineSegment(sketch, "E5493", {"start": v(515.3, 37.3) * mm, "end": v(515.3, 24.48) * mm});
            skLineSegment(sketch, "E5494", {"start": v(515.29, 82.51) * mm, "end": v(515.29, 59.49) * mm});
            skLineSegment(sketch, "E5495", {"start": v(515.29, 59.49) * mm, "end": v(480.33, 59.49) * mm});
            skLineSegment(sketch, "E5496", {"start": v(480.33, 59.49) * mm, "end": v(480.33, 82.51) * mm});
            skLineSegment(sketch, "E5497", {"start": v(497.18, 59.49) * mm, "end": v(497.18, 79.63) * mm});
            skLineSegment(sketch, "E5498", {"start": v(502.23, 90.21) * mm, "end": v(502.23, 114.34) * mm});
            skLineSegment(sketch, "E5499", {"start": v(515.72, 133.6) * mm, "end": v(515.72, 133.1) * mm});
            skLineSegment(sketch, "E5500", {"start": v(515.72, 133.1) * mm, "end": v(515.7, 132.58) * mm});
            skLineSegment(sketch, "E5501", {"start": v(515.7, 132.58) * mm, "end": v(515.65, 132.07) * mm});
            skLineSegment(sketch, "E5502", {"start": v(515.65, 132.07) * mm, "end": v(515.57, 131.57) * mm});
            skLineSegment(sketch, "E5503", {"start": v(515.57, 131.57) * mm, "end": v(515.47, 131.07) * mm});
            skLineSegment(sketch, "E5504", {"start": v(515.47, 131.07) * mm, "end": v(515.34, 130.58) * mm});
            skLineSegment(sketch, "E5505", {"start": v(515.34, 130.58) * mm, "end": v(515.19, 130.1) * mm});
            skLineSegment(sketch, "E5506", {"start": v(515.19, 130.1) * mm, "end": v(515, 129.62) * mm});
            skLineSegment(sketch, "E5507", {"start": v(515, 129.62) * mm, "end": v(514.8, 129.15) * mm});
            skLineSegment(sketch, "E5508", {"start": v(514.8, 129.15) * mm, "end": v(514.58, 128.7) * mm});
            skLineSegment(sketch, "E5509", {"start": v(514.58, 128.7) * mm, "end": v(514.34, 128.25) * mm});
            skLineSegment(sketch, "E5510", {"start": v(514.34, 128.25) * mm, "end": v(514.07, 127.82) * mm});
            skLineSegment(sketch, "E5511", {"start": v(514.07, 127.82) * mm, "end": v(513.78, 127.4) * mm});
            skLineSegment(sketch, "E5512", {"start": v(513.78, 127.4) * mm, "end": v(513.46, 127) * mm});
            skLineSegment(sketch, "E5513", {"start": v(513.46, 127) * mm, "end": v(513.13, 126.6) * mm});
            skLineSegment(sketch, "E5514", {"start": v(513.13, 126.6) * mm, "end": v(512.77, 126.24) * mm});
            skLineSegment(sketch, "E5515", {"start": v(512.77, 126.24) * mm, "end": v(512.52, 125.98) * mm});
            skLineSegment(sketch, "E5516", {"start": v(512.52, 125.98) * mm, "end": v(512.25, 125.73) * mm});
            skLineSegment(sketch, "E5517", {"start": v(512.25, 125.73) * mm, "end": v(511.98, 125.48) * mm});
            skLineSegment(sketch, "E5518", {"start": v(511.98, 125.48) * mm, "end": v(511.71, 125.25) * mm});
            skLineSegment(sketch, "E5519", {"start": v(511.71, 125.25) * mm, "end": v(511.43, 125.02) * mm});
            skLineSegment(sketch, "E5520", {"start": v(511.43, 125.02) * mm, "end": v(511.15, 124.8) * mm});
            skLineSegment(sketch, "E5521", {"start": v(511.15, 124.8) * mm, "end": v(510.85, 124.59) * mm});
            skLineSegment(sketch, "E5522", {"start": v(510.85, 124.59) * mm, "end": v(510.56, 124.38) * mm});
            skLineSegment(sketch, "E5523", {"start": v(510.56, 124.38) * mm, "end": v(510.26, 124.19) * mm});
            skLineSegment(sketch, "E5524", {"start": v(510.26, 124.19) * mm, "end": v(509.95, 124) * mm});
            skLineSegment(sketch, "E5525", {"start": v(509.95, 124) * mm, "end": v(509.64, 123.82) * mm});
            skLineSegment(sketch, "E5526", {"start": v(509.64, 123.82) * mm, "end": v(509.33, 123.65) * mm});
            skLineSegment(sketch, "E5527", {"start": v(509.33, 123.65) * mm, "end": v(509.01, 123.48) * mm});
            skLineSegment(sketch, "E5528", {"start": v(509.01, 123.48) * mm, "end": v(508.69, 123.33) * mm});
            skLineSegment(sketch, "E5529", {"start": v(508.69, 123.33) * mm, "end": v(508.36, 123.18) * mm});
            skLineSegment(sketch, "E5530", {"start": v(508.36, 123.18) * mm, "end": v(508.03, 123.04) * mm});
            skLineSegment(sketch, "E5531", {"start": v(508.03, 123.04) * mm, "end": v(507.7, 122.91) * mm});
            skLineSegment(sketch, "E5532", {"start": v(507.7, 122.91) * mm, "end": v(507.36, 122.8) * mm});
            skLineSegment(sketch, "E5533", {"start": v(507.36, 122.8) * mm, "end": v(507.02, 122.68) * mm});
            skLineSegment(sketch, "E5534", {"start": v(507.02, 122.68) * mm, "end": v(506.68, 122.58) * mm});
            skLineSegment(sketch, "E5535", {"start": v(506.68, 122.58) * mm, "end": v(506.34, 122.48) * mm});
            skLineSegment(sketch, "E5536", {"start": v(506.34, 122.48) * mm, "end": v(505.99, 122.4) * mm});
            skLineSegment(sketch, "E5537", {"start": v(505.99, 122.4) * mm, "end": v(505.64, 122.32) * mm});
            skLineSegment(sketch, "E5538", {"start": v(505.64, 122.32) * mm, "end": v(505.29, 122.25) * mm});
            skLineSegment(sketch, "E5539", {"start": v(505.29, 122.25) * mm, "end": v(504.93, 122.2) * mm});
            skLineSegment(sketch, "E5540", {"start": v(504.93, 122.2) * mm, "end": v(504.58, 122.14) * mm});
            skLineSegment(sketch, "E5541", {"start": v(504.58, 122.14) * mm, "end": v(504.22, 122.1) * mm});
            skLineSegment(sketch, "E5542", {"start": v(504.22, 122.1) * mm, "end": v(503.86, 122.07) * mm});
            skLineSegment(sketch, "E5543", {"start": v(503.86, 122.07) * mm, "end": v(503.5, 122.05) * mm});
            skLineSegment(sketch, "E5544", {"start": v(503.5, 122.05) * mm, "end": v(503.14, 122.04) * mm});
            skLineSegment(sketch, "E5545", {"start": v(503.14, 122.04) * mm, "end": v(502.77, 122.03) * mm});
            skLineSegment(sketch, "E5546", {"start": v(502.77, 122.03) * mm, "end": v(502.4, 122.04) * mm});
            skLineSegment(sketch, "E5547", {"start": v(502.4, 122.04) * mm, "end": v(502.05, 122.03) * mm});
            skLineSegment(sketch, "E5548", {"start": v(502.05, 122.03) * mm, "end": v(501.69, 122.02) * mm});
            skLineSegment(sketch, "E5549", {"start": v(501.69, 122.02) * mm, "end": v(501.32, 122.03) * mm});
            skLineSegment(sketch, "E5550", {"start": v(501.32, 122.03) * mm, "end": v(500.96, 122.04) * mm});
            skLineSegment(sketch, "E5551", {"start": v(500.96, 122.04) * mm, "end": v(500.6, 122.06) * mm});
            skLineSegment(sketch, "E5552", {"start": v(500.6, 122.06) * mm, "end": v(500.25, 122.1) * mm});
            skLineSegment(sketch, "E5553", {"start": v(500.25, 122.1) * mm, "end": v(499.9, 122.13) * mm});
            skLineSegment(sketch, "E5554", {"start": v(499.9, 122.13) * mm, "end": v(499.53, 122.18) * mm});
            skLineSegment(sketch, "E5555", {"start": v(499.53, 122.18) * mm, "end": v(499.18, 122.24) * mm});
            skLineSegment(sketch, "E5556", {"start": v(499.18, 122.24) * mm, "end": v(498.83, 122.3) * mm});
            skLineSegment(sketch, "E5557", {"start": v(498.83, 122.3) * mm, "end": v(498.48, 122.37) * mm});
            skLineSegment(sketch, "E5558", {"start": v(498.48, 122.37) * mm, "end": v(498.13, 122.46) * mm});
            skLineSegment(sketch, "E5559", {"start": v(498.13, 122.46) * mm, "end": v(497.79, 122.55) * mm});
            skLineSegment(sketch, "E5560", {"start": v(497.79, 122.55) * mm, "end": v(497.44, 122.65) * mm});
            skLineSegment(sketch, "E5561", {"start": v(497.44, 122.65) * mm, "end": v(497.1, 122.75) * mm});
            skLineSegment(sketch, "E5562", {"start": v(497.1, 122.75) * mm, "end": v(496.76, 122.87) * mm});
            skLineSegment(sketch, "E5563", {"start": v(496.76, 122.87) * mm, "end": v(496.43, 123) * mm});
            skLineSegment(sketch, "E5564", {"start": v(496.43, 123) * mm, "end": v(496.1, 123.12) * mm});
            skLineSegment(sketch, "E5565", {"start": v(496.1, 123.12) * mm, "end": v(495.77, 123.26) * mm});
            skLineSegment(sketch, "E5566", {"start": v(495.77, 123.26) * mm, "end": v(495.44, 123.41) * mm});
            skLineSegment(sketch, "E5567", {"start": v(495.44, 123.41) * mm, "end": v(495.12, 123.57) * mm});
            skLineSegment(sketch, "E5568", {"start": v(495.12, 123.57) * mm, "end": v(494.8, 123.73) * mm});
            skLineSegment(sketch, "E5569", {"start": v(494.8, 123.73) * mm, "end": v(494.49, 123.9) * mm});
            skLineSegment(sketch, "E5570", {"start": v(494.49, 123.9) * mm, "end": v(494.18, 124.08) * mm});
            skLineSegment(sketch, "E5571", {"start": v(494.18, 124.08) * mm, "end": v(493.87, 124.27) * mm});
            skLineSegment(sketch, "E5572", {"start": v(493.87, 124.27) * mm, "end": v(493.57, 124.46) * mm});
            skLineSegment(sketch, "E5573", {"start": v(493.57, 124.46) * mm, "end": v(493.27, 124.67) * mm});
            skLineSegment(sketch, "E5574", {"start": v(493.27, 124.67) * mm, "end": v(492.98, 124.88) * mm});
            skLineSegment(sketch, "E5575", {"start": v(492.98, 124.88) * mm, "end": v(492.7, 125.1) * mm});
            skLineSegment(sketch, "E5576", {"start": v(492.7, 125.1) * mm, "end": v(492.41, 125.32) * mm});
            skLineSegment(sketch, "E5577", {"start": v(492.41, 125.32) * mm, "end": v(492.13, 125.55) * mm});
            skLineSegment(sketch, "E5578", {"start": v(492.13, 125.55) * mm, "end": v(491.86, 125.79) * mm});
            skLineSegment(sketch, "E5579", {"start": v(491.86, 125.79) * mm, "end": v(491.5, 126.2) * mm});
            skLineSegment(sketch, "E5580", {"start": v(491.5, 126.2) * mm, "end": v(491.15, 126.6) * mm});
            skLineSegment(sketch, "E5581", {"start": v(491.15, 126.6) * mm, "end": v(490.83, 127.04) * mm});
            skLineSegment(sketch, "E5582", {"start": v(490.83, 127.04) * mm, "end": v(490.53, 127.49) * mm});
            skLineSegment(sketch, "E5583", {"start": v(490.53, 127.49) * mm, "end": v(490.25, 127.95) * mm});
            skLineSegment(sketch, "E5584", {"start": v(490.25, 127.95) * mm, "end": v(490, 128.42) * mm});
            skLineSegment(sketch, "E5585", {"start": v(490, 128.42) * mm, "end": v(489.77, 128.9) * mm});
            skLineSegment(sketch, "E5586", {"start": v(489.77, 128.9) * mm, "end": v(489.56, 129.4) * mm});
            skLineSegment(sketch, "E5587", {"start": v(489.56, 129.4) * mm, "end": v(489.37, 129.9) * mm});
            skLineSegment(sketch, "E5588", {"start": v(489.37, 129.9) * mm, "end": v(489.2, 130.41) * mm});
            skLineSegment(sketch, "E5589", {"start": v(489.2, 130.41) * mm, "end": v(489.07, 130.93) * mm});
            skLineSegment(sketch, "E5590", {"start": v(489.07, 130.93) * mm, "end": v(488.95, 131.46) * mm});
            skLineSegment(sketch, "E5591", {"start": v(488.95, 131.46) * mm, "end": v(488.86, 131.99) * mm});
            skLineSegment(sketch, "E5592", {"start": v(488.86, 131.99) * mm, "end": v(488.8, 132.52) * mm});
            skLineSegment(sketch, "E5593", {"start": v(488.8, 132.52) * mm, "end": v(488.76, 133.06) * mm});
            skLineSegment(sketch, "E5594", {"start": v(488.76, 133.06) * mm, "end": v(488.75, 133.6) * mm});
            skLineSegment(sketch, "E5595", {"start": v(488.75, 133.6) * mm, "end": v(488.77, 134.13) * mm});
            skLineSegment(sketch, "E5596", {"start": v(488.77, 134.13) * mm, "end": v(488.83, 134.65) * mm});
            skLineSegment(sketch, "E5597", {"start": v(488.83, 134.65) * mm, "end": v(488.9, 135.17) * mm});
            skLineSegment(sketch, "E5598", {"start": v(488.9, 135.17) * mm, "end": v(489.02, 135.68) * mm});
            skLineSegment(sketch, "E5599", {"start": v(489.02, 135.68) * mm, "end": v(489.15, 136.18) * mm});
            skLineSegment(sketch, "E5600", {"start": v(489.15, 136.18) * mm, "end": v(489.3, 136.68) * mm});
            skLineSegment(sketch, "E5601", {"start": v(489.3, 136.68) * mm, "end": v(489.5, 137.16) * mm});
            skLineSegment(sketch, "E5602", {"start": v(489.5, 137.16) * mm, "end": v(489.7, 137.64) * mm});
            skLineSegment(sketch, "E5603", {"start": v(489.7, 137.64) * mm, "end": v(489.94, 138.1) * mm});
            skLineSegment(sketch, "E5604", {"start": v(489.94, 138.1) * mm, "end": v(490.2, 138.55) * mm});
            skLineSegment(sketch, "E5605", {"start": v(490.2, 138.55) * mm, "end": v(490.47, 138.99) * mm});
            skLineSegment(sketch, "E5606", {"start": v(490.47, 138.99) * mm, "end": v(490.78, 139.4) * mm});
            skLineSegment(sketch, "E5607", {"start": v(490.78, 139.4) * mm, "end": v(491.1, 139.81) * mm});
            skLineSegment(sketch, "E5608", {"start": v(491.1, 139.81) * mm, "end": v(491.45, 140.2) * mm});
            skLineSegment(sketch, "E5609", {"start": v(491.45, 140.2) * mm, "end": v(491.82, 140.58) * mm});
            skLineSegment(sketch, "E5610", {"start": v(491.82, 140.58) * mm, "end": v(492.21, 140.93) * mm});
            skLineSegment(sketch, "E5611", {"start": v(492.21, 140.93) * mm, "end": v(492.47, 141.17) * mm});
            skLineSegment(sketch, "E5612", {"start": v(492.47, 141.17) * mm, "end": v(492.73, 141.4) * mm});
            skLineSegment(sketch, "E5613", {"start": v(492.73, 141.4) * mm, "end": v(493, 141.63) * mm});
            skLineSegment(sketch, "E5614", {"start": v(493, 141.63) * mm, "end": v(493.28, 141.85) * mm});
            skLineSegment(sketch, "E5615", {"start": v(493.28, 141.85) * mm, "end": v(493.56, 142.06) * mm});
            skLineSegment(sketch, "E5616", {"start": v(493.56, 142.06) * mm, "end": v(493.84, 142.26) * mm});
            skLineSegment(sketch, "E5617", {"start": v(493.84, 142.26) * mm, "end": v(494.13, 142.45) * mm});
            skLineSegment(sketch, "E5618", {"start": v(494.13, 142.45) * mm, "end": v(494.43, 142.64) * mm});
            skLineSegment(sketch, "E5619", {"start": v(494.43, 142.64) * mm, "end": v(494.72, 142.82) * mm});
            skLineSegment(sketch, "E5620", {"start": v(494.72, 142.82) * mm, "end": v(495.03, 143) * mm});
            skLineSegment(sketch, "E5621", {"start": v(495.03, 143) * mm, "end": v(495.33, 143.16) * mm});
            skLineSegment(sketch, "E5622", {"start": v(495.33, 143.16) * mm, "end": v(495.64, 143.31) * mm});
            skLineSegment(sketch, "E5623", {"start": v(495.64, 143.31) * mm, "end": v(495.96, 143.46) * mm});
            skLineSegment(sketch, "E5624", {"start": v(495.96, 143.46) * mm, "end": v(496.28, 143.6) * mm});
            skLineSegment(sketch, "E5625", {"start": v(496.28, 143.6) * mm, "end": v(496.6, 143.73) * mm});
            skLineSegment(sketch, "E5626", {"start": v(496.6, 143.73) * mm, "end": v(496.92, 143.85) * mm});
            skLineSegment(sketch, "E5627", {"start": v(496.92, 143.85) * mm, "end": v(497.25, 143.97) * mm});
            skLineSegment(sketch, "E5628", {"start": v(497.25, 143.97) * mm, "end": v(497.58, 144.07) * mm});
            skLineSegment(sketch, "E5629", {"start": v(497.58, 144.07) * mm, "end": v(497.91, 144.17) * mm});
            skLineSegment(sketch, "E5630", {"start": v(497.91, 144.17) * mm, "end": v(498.25, 144.26) * mm});
            skLineSegment(sketch, "E5631", {"start": v(498.25, 144.26) * mm, "end": v(498.59, 144.34) * mm});
            skLineSegment(sketch, "E5632", {"start": v(498.59, 144.34) * mm, "end": v(498.93, 144.41) * mm});
            skLineSegment(sketch, "E5633", {"start": v(498.93, 144.41) * mm, "end": v(499.27, 144.48) * mm});
            skLineSegment(sketch, "E5634", {"start": v(499.27, 144.48) * mm, "end": v(499.61, 144.53) * mm});
            skLineSegment(sketch, "E5635", {"start": v(499.61, 144.53) * mm, "end": v(499.96, 144.58) * mm});
            skLineSegment(sketch, "E5636", {"start": v(499.96, 144.58) * mm, "end": v(500.3, 144.61) * mm});
            skLineSegment(sketch, "E5637", {"start": v(500.3, 144.61) * mm, "end": v(500.65, 144.64) * mm});
            skLineSegment(sketch, "E5638", {"start": v(500.65, 144.64) * mm, "end": v(501, 144.66) * mm});
            skLineSegment(sketch, "E5639", {"start": v(501, 144.66) * mm, "end": v(501.35, 144.67) * mm});
            skLineSegment(sketch, "E5640", {"start": v(501.35, 144.67) * mm, "end": v(501.7, 144.67) * mm});
            skLineSegment(sketch, "E5641", {"start": v(501.7, 144.67) * mm, "end": v(502.06, 144.66) * mm});
            skLineSegment(sketch, "E5642", {"start": v(502.06, 144.66) * mm, "end": v(502.4, 144.64) * mm});
            skLineSegment(sketch, "E5643", {"start": v(502.4, 144.64) * mm, "end": v(502.76, 144.65) * mm});
            skLineSegment(sketch, "E5644", {"start": v(502.76, 144.65) * mm, "end": v(503.1, 144.66) * mm});
            skLineSegment(sketch, "E5645", {"start": v(503.1, 144.66) * mm, "end": v(503.46, 144.65) * mm});
            skLineSegment(sketch, "E5646", {"start": v(503.46, 144.65) * mm, "end": v(503.8, 144.64) * mm});
            skLineSegment(sketch, "E5647", {"start": v(503.8, 144.64) * mm, "end": v(504.15, 144.61) * mm});
            skLineSegment(sketch, "E5648", {"start": v(504.15, 144.61) * mm, "end": v(504.5, 144.58) * mm});
            skLineSegment(sketch, "E5649", {"start": v(504.5, 144.58) * mm, "end": v(504.84, 144.54) * mm});
            skLineSegment(sketch, "E5650", {"start": v(504.84, 144.54) * mm, "end": v(505.18, 144.49) * mm});
            skLineSegment(sketch, "E5651", {"start": v(505.18, 144.49) * mm, "end": v(505.52, 144.43) * mm});
            skLineSegment(sketch, "E5652", {"start": v(505.52, 144.43) * mm, "end": v(505.86, 144.36) * mm});
            skLineSegment(sketch, "E5653", {"start": v(505.86, 144.36) * mm, "end": v(506.2, 144.29) * mm});
            skLineSegment(sketch, "E5654", {"start": v(506.2, 144.29) * mm, "end": v(506.53, 144.2) * mm});
            skLineSegment(sketch, "E5655", {"start": v(506.53, 144.2) * mm, "end": v(506.87, 144.11) * mm});
            skLineSegment(sketch, "E5656", {"start": v(506.87, 144.11) * mm, "end": v(507.2, 144.01) * mm});
            skLineSegment(sketch, "E5657", {"start": v(507.2, 144.01) * mm, "end": v(507.52, 143.9) * mm});
            skLineSegment(sketch, "E5658", {"start": v(507.52, 143.9) * mm, "end": v(507.85, 143.8) * mm});
            skLineSegment(sketch, "E5659", {"start": v(507.85, 143.8) * mm, "end": v(508.17, 143.67) * mm});
            skLineSegment(sketch, "E5660", {"start": v(508.17, 143.67) * mm, "end": v(508.49, 143.53) * mm});
            skLineSegment(sketch, "E5661", {"start": v(508.49, 143.53) * mm, "end": v(508.8, 143.4) * mm});
            skLineSegment(sketch, "E5662", {"start": v(508.8, 143.4) * mm, "end": v(509.11, 143.25) * mm});
            skLineSegment(sketch, "E5663", {"start": v(509.11, 143.25) * mm, "end": v(509.42, 143.1) * mm});
            skLineSegment(sketch, "E5664", {"start": v(509.42, 143.1) * mm, "end": v(509.72, 142.93) * mm});
            skLineSegment(sketch, "E5665", {"start": v(509.72, 142.93) * mm, "end": v(510.02, 142.76) * mm});
            skLineSegment(sketch, "E5666", {"start": v(510.02, 142.76) * mm, "end": v(510.32, 142.58) * mm});
            skLineSegment(sketch, "E5667", {"start": v(510.32, 142.58) * mm, "end": v(510.61, 142.4) * mm});
            skLineSegment(sketch, "E5668", {"start": v(510.61, 142.4) * mm, "end": v(510.9, 142.2) * mm});
            skLineSegment(sketch, "E5669", {"start": v(510.9, 142.2) * mm, "end": v(511.18, 142) * mm});
            skLineSegment(sketch, "E5670", {"start": v(511.18, 142) * mm, "end": v(511.46, 141.79) * mm});
            skLineSegment(sketch, "E5671", {"start": v(511.46, 141.79) * mm, "end": v(511.73, 141.57) * mm});
            skLineSegment(sketch, "E5672", {"start": v(511.73, 141.57) * mm, "end": v(512, 141.35) * mm});
            skLineSegment(sketch, "E5673", {"start": v(512, 141.35) * mm, "end": v(512.26, 141.12) * mm});
            skLineSegment(sketch, "E5674", {"start": v(512.26, 141.12) * mm, "end": v(512.52, 140.88) * mm});
            skLineSegment(sketch, "E5675", {"start": v(512.52, 140.88) * mm, "end": v(512.89, 140.52) * mm});
            skLineSegment(sketch, "E5676", {"start": v(512.89, 140.52) * mm, "end": v(513.24, 140.14) * mm});
            skLineSegment(sketch, "E5677", {"start": v(513.24, 140.14) * mm, "end": v(513.56, 139.75) * mm});
            skLineSegment(sketch, "E5678", {"start": v(513.56, 139.75) * mm, "end": v(513.87, 139.34) * mm});
            skLineSegment(sketch, "E5679", {"start": v(513.87, 139.34) * mm, "end": v(514.15, 138.92) * mm});
            skLineSegment(sketch, "E5680", {"start": v(514.15, 138.92) * mm, "end": v(514.41, 138.48) * mm});
            skLineSegment(sketch, "E5681", {"start": v(514.41, 138.48) * mm, "end": v(514.65, 138.03) * mm});
            skLineSegment(sketch, "E5682", {"start": v(514.65, 138.03) * mm, "end": v(514.87, 137.57) * mm});
            skLineSegment(sketch, "E5683", {"start": v(514.87, 137.57) * mm, "end": v(515.06, 137.1) * mm});
            skLineSegment(sketch, "E5684", {"start": v(515.06, 137.1) * mm, "end": v(515.23, 136.63) * mm});
            skLineSegment(sketch, "E5685", {"start": v(515.23, 136.63) * mm, "end": v(515.38, 136.14) * mm});
            skLineSegment(sketch, "E5686", {"start": v(515.38, 136.14) * mm, "end": v(515.5, 135.64) * mm});
            skLineSegment(sketch, "E5687", {"start": v(515.5, 135.64) * mm, "end": v(515.6, 135.14) * mm});
            skLineSegment(sketch, "E5688", {"start": v(515.6, 135.14) * mm, "end": v(515.66, 134.63) * mm});
            skLineSegment(sketch, "E5689", {"start": v(515.66, 134.63) * mm, "end": v(515.7, 134.12) * mm});
            skLineSegment(sketch, "E5690", {"start": v(515.7, 134.12) * mm, "end": v(515.72, 133.6) * mm});
            skLineSegment(sketch, "E5691", {"start": v(515.3, 171.55) * mm, "end": v(489.17, 171.55) * mm});
            skLineSegment(sketch, "E5692", {"start": v(505.87, 171.55) * mm, "end": v(506.35, 171.53) * mm});
            skLineSegment(sketch, "E5693", {"start": v(506.35, 171.53) * mm, "end": v(506.82, 171.48) * mm});
            skLineSegment(sketch, "E5694", {"start": v(506.82, 171.48) * mm, "end": v(507.29, 171.42) * mm});
            skLineSegment(sketch, "E5695", {"start": v(507.29, 171.42) * mm, "end": v(507.75, 171.32) * mm});
            skLineSegment(sketch, "E5696", {"start": v(507.75, 171.32) * mm, "end": v(508.21, 171.21) * mm});
            skLineSegment(sketch, "E5697", {"start": v(508.21, 171.21) * mm, "end": v(508.66, 171.08) * mm});
            skLineSegment(sketch, "E5698", {"start": v(508.66, 171.08) * mm, "end": v(509.1, 170.92) * mm});
            skLineSegment(sketch, "E5699", {"start": v(509.1, 170.92) * mm, "end": v(509.54, 170.74) * mm});
            skLineSegment(sketch, "E5700", {"start": v(509.54, 170.74) * mm, "end": v(509.97, 170.54) * mm});
            skLineSegment(sketch, "E5701", {"start": v(509.97, 170.54) * mm, "end": v(510.39, 170.32) * mm});
            skLineSegment(sketch, "E5702", {"start": v(510.39, 170.32) * mm, "end": v(510.79, 170.08) * mm});
            skLineSegment(sketch, "E5703", {"start": v(510.79, 170.08) * mm, "end": v(511.18, 169.81) * mm});
            skLineSegment(sketch, "E5704", {"start": v(511.18, 169.81) * mm, "end": v(511.56, 169.53) * mm});
            skLineSegment(sketch, "E5705", {"start": v(511.56, 169.53) * mm, "end": v(511.93, 169.23) * mm});
            skLineSegment(sketch, "E5706", {"start": v(511.93, 169.23) * mm, "end": v(512.28, 168.91) * mm});
            skLineSegment(sketch, "E5707", {"start": v(512.28, 168.91) * mm, "end": v(512.62, 168.57) * mm});
            skLineSegment(sketch, "E5708", {"start": v(512.62, 168.57) * mm, "end": v(512.96, 168.23) * mm});
            skLineSegment(sketch, "E5709", {"start": v(512.96, 168.23) * mm, "end": v(513.27, 167.87) * mm});
            skLineSegment(sketch, "E5710", {"start": v(513.27, 167.87) * mm, "end": v(513.57, 167.5) * mm});
            skLineSegment(sketch, "E5711", {"start": v(513.57, 167.5) * mm, "end": v(513.85, 167.1) * mm});
            skLineSegment(sketch, "E5712", {"start": v(513.85, 167.1) * mm, "end": v(514.11, 166.7) * mm});
            skLineSegment(sketch, "E5713", {"start": v(514.11, 166.7) * mm, "end": v(514.35, 166.3) * mm});
            skLineSegment(sketch, "E5714", {"start": v(514.35, 166.3) * mm, "end": v(514.57, 165.88) * mm});
            skLineSegment(sketch, "E5715", {"start": v(514.57, 165.88) * mm, "end": v(514.77, 165.44) * mm});
            skLineSegment(sketch, "E5716", {"start": v(514.77, 165.44) * mm, "end": v(514.94, 165) * mm});
            skLineSegment(sketch, "E5717", {"start": v(514.94, 165) * mm, "end": v(515.1, 164.55) * mm});
            skLineSegment(sketch, "E5718", {"start": v(515.1, 164.55) * mm, "end": v(515.23, 164.1) * mm});
            skLineSegment(sketch, "E5719", {"start": v(515.23, 164.1) * mm, "end": v(515.34, 163.63) * mm});
            skLineSegment(sketch, "E5720", {"start": v(515.34, 163.63) * mm, "end": v(515.42, 163.16) * mm});
            skLineSegment(sketch, "E5721", {"start": v(515.42, 163.16) * mm, "end": v(515.49, 162.69) * mm});
            skLineSegment(sketch, "E5722", {"start": v(515.49, 162.69) * mm, "end": v(515.53, 162.2) * mm});
            skLineSegment(sketch, "E5723", {"start": v(515.53, 162.2) * mm, "end": v(515.54, 161.73) * mm});
            skLineSegment(sketch, "E5724", {"start": v(515.54, 161.73) * mm, "end": v(515.58, 161.26) * mm});
            skLineSegment(sketch, "E5725", {"start": v(515.58, 161.26) * mm, "end": v(515.6, 160.79) * mm});
            skLineSegment(sketch, "E5726", {"start": v(515.6, 160.79) * mm, "end": v(515.58, 160.32) * mm});
            skLineSegment(sketch, "E5727", {"start": v(515.58, 160.32) * mm, "end": v(515.55, 159.85) * mm});
            skLineSegment(sketch, "E5728", {"start": v(515.55, 159.85) * mm, "end": v(515.5, 159.39) * mm});
            skLineSegment(sketch, "E5729", {"start": v(515.5, 159.39) * mm, "end": v(515.41, 158.93) * mm});
            skLineSegment(sketch, "E5730", {"start": v(515.41, 158.93) * mm, "end": v(515.3, 158.47) * mm});
            skLineSegment(sketch, "E5731", {"start": v(515.3, 158.47) * mm, "end": v(515.18, 158.02) * mm});
            skLineSegment(sketch, "E5732", {"start": v(515.18, 158.02) * mm, "end": v(515.04, 157.58) * mm});
            skLineSegment(sketch, "E5733", {"start": v(515.04, 157.58) * mm, "end": v(514.87, 157.15) * mm});
            skLineSegment(sketch, "E5734", {"start": v(514.87, 157.15) * mm, "end": v(514.68, 156.72) * mm});
            skLineSegment(sketch, "E5735", {"start": v(514.68, 156.72) * mm, "end": v(514.47, 156.3) * mm});
            skLineSegment(sketch, "E5736", {"start": v(514.47, 156.3) * mm, "end": v(514.24, 155.9) * mm});
            skLineSegment(sketch, "E5737", {"start": v(514.24, 155.9) * mm, "end": v(513.99, 155.5) * mm});
            skLineSegment(sketch, "E5738", {"start": v(513.99, 155.5) * mm, "end": v(513.71, 155.12) * mm});
            skLineSegment(sketch, "E5739", {"start": v(513.71, 155.12) * mm, "end": v(513.42, 154.75) * mm});
            skLineSegment(sketch, "E5740", {"start": v(513.42, 154.75) * mm, "end": v(513.1, 154.47) * mm});
            skLineSegment(sketch, "E5741", {"start": v(513.1, 154.47) * mm, "end": v(512.78, 154.2) * mm});
            skLineSegment(sketch, "E5742", {"start": v(512.78, 154.2) * mm, "end": v(512.44, 153.96) * mm});
            skLineSegment(sketch, "E5743", {"start": v(512.44, 153.96) * mm, "end": v(512.08, 153.73) * mm});
            skLineSegment(sketch, "E5744", {"start": v(512.08, 153.73) * mm, "end": v(511.72, 153.52) * mm});
            skLineSegment(sketch, "E5745", {"start": v(511.72, 153.52) * mm, "end": v(511.35, 153.33) * mm});
            skLineSegment(sketch, "E5746", {"start": v(511.35, 153.33) * mm, "end": v(510.97, 153.16) * mm});
            skLineSegment(sketch, "E5747", {"start": v(510.97, 153.16) * mm, "end": v(510.58, 153) * mm});
            skLineSegment(sketch, "E5748", {"start": v(510.58, 153) * mm, "end": v(510.18, 152.88) * mm});
            skLineSegment(sketch, "E5749", {"start": v(510.18, 152.88) * mm, "end": v(509.78, 152.77) * mm});
            skLineSegment(sketch, "E5750", {"start": v(509.78, 152.77) * mm, "end": v(509.37, 152.68) * mm});
            skLineSegment(sketch, "E5751", {"start": v(509.37, 152.68) * mm, "end": v(508.96, 152.6) * mm});
            skLineSegment(sketch, "E5752", {"start": v(508.96, 152.6) * mm, "end": v(508.54, 152.56) * mm});
            skLineSegment(sketch, "E5753", {"start": v(508.54, 152.56) * mm, "end": v(508.12, 152.53) * mm});
            skLineSegment(sketch, "E5754", {"start": v(508.12, 152.53) * mm, "end": v(507.7, 152.53) * mm});
            skLineSegment(sketch, "E5755", {"start": v(507.7, 152.53) * mm, "end": v(507.27, 152.54) * mm});
            skLineSegment(sketch, "E5756", {"start": v(507.27, 152.54) * mm, "end": v(489.17, 152.54) * mm});
            skLineSegment(sketch, "E5757", {"start": v(515.16, 187.88) * mm, "end": v(515.29, 187.65) * mm});
            skLineSegment(sketch, "E5758", {"start": v(515.29, 187.65) * mm, "end": v(515.4, 187.41) * mm});
            skLineSegment(sketch, "E5759", {"start": v(515.4, 187.41) * mm, "end": v(515.49, 187.17) * mm});
            skLineSegment(sketch, "E5760", {"start": v(515.49, 187.17) * mm, "end": v(515.56, 186.92) * mm});
            skLineSegment(sketch, "E5761", {"start": v(515.56, 186.92) * mm, "end": v(515.61, 186.66) * mm});
            skLineSegment(sketch, "E5762", {"start": v(515.61, 186.66) * mm, "end": v(515.65, 186.4) * mm});
            skLineSegment(sketch, "E5763", {"start": v(515.65, 186.4) * mm, "end": v(515.67, 186.14) * mm});
            skLineSegment(sketch, "E5764", {"start": v(515.67, 186.14) * mm, "end": v(515.67, 185.88) * mm});
            skLineSegment(sketch, "E5765", {"start": v(515.67, 185.88) * mm, "end": v(515.67, 185.7) * mm});
            skLineSegment(sketch, "E5766", {"start": v(515.67, 185.7) * mm, "end": v(515.65, 185.5) * mm});
            skLineSegment(sketch, "E5767", {"start": v(515.65, 185.5) * mm, "end": v(515.64, 185.31) * mm});
            skLineSegment(sketch, "E5768", {"start": v(515.64, 185.31) * mm, "end": v(515.6, 185.13) * mm});
            skLineSegment(sketch, "E5769", {"start": v(515.6, 185.13) * mm, "end": v(515.57, 184.94) * mm});
            skLineSegment(sketch, "E5770", {"start": v(515.57, 184.94) * mm, "end": v(515.53, 184.76) * mm});
            skLineSegment(sketch, "E5771", {"start": v(515.53, 184.76) * mm, "end": v(515.48, 184.58) * mm});
            skLineSegment(sketch, "E5772", {"start": v(515.48, 184.58) * mm, "end": v(515.42, 184.4) * mm});
            skLineSegment(sketch, "E5773", {"start": v(515.42, 184.4) * mm, "end": v(515.35, 184.23) * mm});
            skLineSegment(sketch, "E5774", {"start": v(515.35, 184.23) * mm, "end": v(515.27, 184.05) * mm});
            skLineSegment(sketch, "E5775", {"start": v(515.27, 184.05) * mm, "end": v(515.19, 183.89) * mm});
            skLineSegment(sketch, "E5776", {"start": v(515.19, 183.89) * mm, "end": v(515.1, 183.72) * mm});
            skLineSegment(sketch, "E5777", {"start": v(515.1, 183.72) * mm, "end": v(515, 183.56) * mm});
            skLineSegment(sketch, "E5778", {"start": v(515, 183.56) * mm, "end": v(514.9, 183.4) * mm});
            skLineSegment(sketch, "E5779", {"start": v(514.9, 183.4) * mm, "end": v(514.78, 183.25) * mm});
            skLineSegment(sketch, "E5780", {"start": v(514.78, 183.25) * mm, "end": v(514.66, 183.1) * mm});
            skLineSegment(sketch, "E5781", {"start": v(514.66, 183.1) * mm, "end": v(514.54, 182.98) * mm});
            skLineSegment(sketch, "E5782", {"start": v(514.54, 182.98) * mm, "end": v(514.41, 182.87) * mm});
            skLineSegment(sketch, "E5783", {"start": v(514.41, 182.87) * mm, "end": v(514.28, 182.77) * mm});
            skLineSegment(sketch, "E5784", {"start": v(514.28, 182.77) * mm, "end": v(514.14, 182.67) * mm});
            skLineSegment(sketch, "E5785", {"start": v(514.14, 182.67) * mm, "end": v(514, 182.58) * mm});
            skLineSegment(sketch, "E5786", {"start": v(514, 182.58) * mm, "end": v(513.86, 182.5) * mm});
            skLineSegment(sketch, "E5787", {"start": v(513.86, 182.5) * mm, "end": v(513.7, 182.41) * mm});
            skLineSegment(sketch, "E5788", {"start": v(513.7, 182.41) * mm, "end": v(513.55, 182.34) * mm});
            skLineSegment(sketch, "E5789", {"start": v(513.55, 182.34) * mm, "end": v(513.4, 182.28) * mm});
            skLineSegment(sketch, "E5790", {"start": v(513.4, 182.28) * mm, "end": v(513.24, 182.23) * mm});
            skLineSegment(sketch, "E5791", {"start": v(513.24, 182.23) * mm, "end": v(513.08, 182.18) * mm});
            skLineSegment(sketch, "E5792", {"start": v(513.08, 182.18) * mm, "end": v(512.91, 182.15) * mm});
            skLineSegment(sketch, "E5793", {"start": v(512.91, 182.15) * mm, "end": v(512.75, 182.12) * mm});
            skLineSegment(sketch, "E5794", {"start": v(512.75, 182.12) * mm, "end": v(512.58, 182.1) * mm});
            skLineSegment(sketch, "E5795", {"start": v(512.58, 182.1) * mm, "end": v(512.4, 182.08) * mm});
            skLineSegment(sketch, "E5796", {"start": v(512.4, 182.08) * mm, "end": v(512.24, 182.08) * mm});
            skLineSegment(sketch, "E5797", {"start": v(512.24, 182.08) * mm, "end": v(481.88, 182.08) * mm});
            skLineSegment(sketch, "E5798", {"start": v(489, 179.44) * mm, "end": v(489, 187.5) * mm});
            skArc(sketch, "E5799", {"start": v(-577.34, -1167.74) * mm, "mid": v(-579.46, -1168.61) * mm, "end": v(-580.34, -1170.74) * mm});
            skArc(sketch, "E5800", {"start": v(-580.34, -1170.74) * mm, "mid": v(-579.46, -1172.86) * mm, "end": v(-577.34, -1173.74) * mm});
            skArc(sketch, "E5801", {"start": v(-577.34, -1173.74) * mm, "mid": v(-575.22, -1172.86) * mm, "end": v(-574.34, -1170.74) * mm});
            skArc(sketch, "E5802", {"start": v(-574.34, -1170.74) * mm, "mid": v(-575.22, -1168.61) * mm, "end": v(-577.34, -1167.74) * mm});
            skArc(sketch, "E5803", {"start": v(-158.93, -1169.27) * mm, "mid": v(-161.06, -1170.15) * mm, "end": v(-161.93, -1172.27) * mm});
            skArc(sketch, "E5804", {"start": v(-161.93, -1172.27) * mm, "mid": v(-161.06, -1174.4) * mm, "end": v(-158.93, -1175.27) * mm});
            skArc(sketch, "E5805", {"start": v(-158.93, -1175.27) * mm, "mid": v(-156.81, -1174.4) * mm, "end": v(-155.93, -1172.27) * mm});
            skArc(sketch, "E5806", {"start": v(-155.93, -1172.27) * mm, "mid": v(-156.81, -1170.15) * mm, "end": v(-158.93, -1169.27) * mm});
            skArc(sketch, "E5807", {"start": v(174.86, -1170.81) * mm, "mid": v(172.74, -1171.7) * mm, "end": v(171.86, -1173.81) * mm});
            skArc(sketch, "E5808", {"start": v(171.86, -1173.81) * mm, "mid": v(172.74, -1175.93) * mm, "end": v(174.86, -1176.81) * mm});
            skArc(sketch, "E5809", {"start": v(174.86, -1176.81) * mm, "mid": v(176.99, -1175.93) * mm, "end": v(177.86, -1173.81) * mm});
            skArc(sketch, "E5810", {"start": v(177.86, -1173.81) * mm, "mid": v(176.99, -1171.7) * mm, "end": v(174.86, -1170.81) * mm});
            skArc(sketch, "E5811", {"start": v(576.35, -1163.12) * mm, "mid": v(574.23, -1164) * mm, "end": v(573.35, -1166.12) * mm});
            skArc(sketch, "E5812", {"start": v(573.35, -1166.12) * mm, "mid": v(574.23, -1168.24) * mm, "end": v(576.35, -1169.12) * mm});
            skArc(sketch, "E5813", {"start": v(576.35, -1169.12) * mm, "mid": v(578.47, -1168.24) * mm, "end": v(579.35, -1166.12) * mm});
            skArc(sketch, "E5814", {"start": v(579.35, -1166.12) * mm, "mid": v(578.47, -1164) * mm, "end": v(576.35, -1163.12) * mm});
            skArc(sketch, "E5815", {"start": v(579.71, -521.86) * mm, "mid": v(577.6, -522.74) * mm, "end": v(576.71, -524.86) * mm});
            skArc(sketch, "E5816", {"start": v(576.71, -524.86) * mm, "mid": v(577.6, -526.99) * mm, "end": v(579.71, -527.86) * mm});
            skArc(sketch, "E5817", {"start": v(579.71, -527.86) * mm, "mid": v(581.83, -526.99) * mm, "end": v(582.71, -524.86) * mm});
            skArc(sketch, "E5818", {"start": v(582.71, -524.86) * mm, "mid": v(581.83, -522.74) * mm, "end": v(579.71, -521.86) * mm});
            skArc(sketch, "E5819", {"start": v(255.24, -581.95) * mm, "mid": v(253.12, -582.83) * mm, "end": v(252.24, -584.95) * mm});
            skArc(sketch, "E5820", {"start": v(252.24, -584.95) * mm, "mid": v(253.12, -587.07) * mm, "end": v(255.24, -587.95) * mm});
            skArc(sketch, "E5821", {"start": v(255.24, -587.95) * mm, "mid": v(257.36, -587.07) * mm, "end": v(258.24, -584.95) * mm});
            skArc(sketch, "E5822", {"start": v(258.24, -584.95) * mm, "mid": v(257.36, -582.83) * mm, "end": v(255.24, -581.95) * mm});
            skArc(sketch, "E5823", {"start": v(-83.66, -545.9) * mm, "mid": v(-85.78, -546.78) * mm, "end": v(-86.66, -548.9) * mm});
            skArc(sketch, "E5824", {"start": v(-86.66, -548.9) * mm, "mid": v(-85.78, -551.02) * mm, "end": v(-83.66, -551.9) * mm});
            skArc(sketch, "E5825", {"start": v(-83.66, -551.9) * mm, "mid": v(-81.53, -551.02) * mm, "end": v(-80.66, -548.9) * mm});
            skArc(sketch, "E5826", {"start": v(-80.66, -548.9) * mm, "mid": v(-81.53, -546.78) * mm, "end": v(-83.66, -545.9) * mm});
            skArc(sketch, "E5827", {"start": v(-415.34, -500.23) * mm, "mid": v(-417.46, -501.11) * mm, "end": v(-418.34, -503.23) * mm});
            skArc(sketch, "E5828", {"start": v(-418.34, -503.23) * mm, "mid": v(-417.46, -505.35) * mm, "end": v(-415.34, -506.23) * mm});
            skArc(sketch, "E5829", {"start": v(-415.34, -506.23) * mm, "mid": v(-413.22, -505.35) * mm, "end": v(-412.34, -503.23) * mm});
            skArc(sketch, "E5830", {"start": v(-412.34, -503.23) * mm, "mid": v(-413.22, -501.11) * mm, "end": v(-415.34, -500.23) * mm});
            skArc(sketch, "E5831", {"start": v(-581.18, -38.76) * mm, "mid": v(-583.3, -39.64) * mm, "end": v(-584.18, -41.76) * mm});
            skArc(sketch, "E5832", {"start": v(-584.18, -41.76) * mm, "mid": v(-583.3, -43.88) * mm, "end": v(-581.18, -44.76) * mm});
            skArc(sketch, "E5833", {"start": v(-581.18, -44.76) * mm, "mid": v(-579.06, -43.88) * mm, "end": v(-578.18, -41.76) * mm});
            skArc(sketch, "E5834", {"start": v(-578.18, -41.76) * mm, "mid": v(-579.06, -39.64) * mm, "end": v(-581.18, -38.76) * mm});
            skArc(sketch, "E5835", {"start": v(-239.21, -94.04) * mm, "mid": v(-241.33, -94.92) * mm, "end": v(-242.21, -97.04) * mm});
            skArc(sketch, "E5836", {"start": v(-242.21, -97.04) * mm, "mid": v(-241.33, -99.16) * mm, "end": v(-239.21, -100.04) * mm});
            skArc(sketch, "E5837", {"start": v(-239.21, -100.04) * mm, "mid": v(-237.1, -99.16) * mm, "end": v(-236.21, -97.04) * mm});
            skArc(sketch, "E5838", {"start": v(-236.21, -97.04) * mm, "mid": v(-237.1, -94.92) * mm, "end": v(-239.21, -94.04) * mm});
            skArc(sketch, "E5839", {"start": v(89.97, 22.87) * mm, "mid": v(87.85, 21.99) * mm, "end": v(86.97, 19.87) * mm});
            skArc(sketch, "E5840", {"start": v(86.97, 19.87) * mm, "mid": v(87.85, 17.75) * mm, "end": v(89.97, 16.87) * mm});
            skArc(sketch, "E5841", {"start": v(89.97, 16.87) * mm, "mid": v(92.1, 17.75) * mm, "end": v(92.97, 19.87) * mm});
            skArc(sketch, "E5842", {"start": v(92.97, 19.87) * mm, "mid": v(92.1, 21.99) * mm, "end": v(89.97, 22.87) * mm});
            skArc(sketch, "E5843", {"start": v(417.62, -3.28) * mm, "mid": v(415.5, -4.16) * mm, "end": v(414.62, -6.28) * mm});
            skArc(sketch, "E5844", {"start": v(414.62, -6.28) * mm, "mid": v(415.5, -8.4) * mm, "end": v(417.62, -9.28) * mm});
            skArc(sketch, "E5845", {"start": v(417.62, -9.28) * mm, "mid": v(419.74, -8.4) * mm, "end": v(420.62, -6.28) * mm});
            skArc(sketch, "E5846", {"start": v(420.62, -6.28) * mm, "mid": v(419.74, -4.16) * mm, "end": v(417.62, -3.28) * mm});
            skArc(sketch, "E5847", {"start": v(581.87, 480.47) * mm, "mid": v(579.75, 479.6) * mm, "end": v(578.87, 477.47) * mm});
            skArc(sketch, "E5848", {"start": v(578.87, 477.47) * mm, "mid": v(579.75, 475.35) * mm, "end": v(581.87, 474.47) * mm});
            skArc(sketch, "E5849", {"start": v(581.87, 474.47) * mm, "mid": v(584, 475.35) * mm, "end": v(584.87, 477.47) * mm});
            skArc(sketch, "E5850", {"start": v(584.87, 477.47) * mm, "mid": v(584, 479.6) * mm, "end": v(581.87, 480.47) * mm});
            skArc(sketch, "E5851", {"start": v(257.4, 480.47) * mm, "mid": v(255.28, 479.6) * mm, "end": v(254.4, 477.47) * mm});
            skArc(sketch, "E5852", {"start": v(254.4, 477.47) * mm, "mid": v(255.28, 475.35) * mm, "end": v(257.4, 474.47) * mm});
            skArc(sketch, "E5853", {"start": v(257.4, 474.47) * mm, "mid": v(259.52, 475.35) * mm, "end": v(260.4, 477.47) * mm});
            skArc(sketch, "E5854", {"start": v(260.4, 477.47) * mm, "mid": v(259.52, 479.6) * mm, "end": v(257.4, 480.47) * mm});
            skArc(sketch, "E5855", {"start": v(-78.01, 489.08) * mm, "mid": v(-80.13, 488.2) * mm, "end": v(-81.01, 486.08) * mm});
            skArc(sketch, "E5856", {"start": v(-81.01, 486.08) * mm, "mid": v(-80.13, 483.96) * mm, "end": v(-78.01, 483.08) * mm});
            skArc(sketch, "E5857", {"start": v(-78.01, 483.08) * mm, "mid": v(-75.9, 483.96) * mm, "end": v(-75.01, 486.08) * mm});
            skArc(sketch, "E5858", {"start": v(-75.01, 486.08) * mm, "mid": v(-75.9, 488.2) * mm, "end": v(-78.01, 489.08) * mm});
            skArc(sketch, "E5859", {"start": v(-411.5, 561.69) * mm, "mid": v(-413.63, 560.8) * mm, "end": v(-414.5, 558.69) * mm});
            skArc(sketch, "E5860", {"start": v(-414.5, 558.69) * mm, "mid": v(-413.63, 556.57) * mm, "end": v(-411.5, 555.69) * mm});
            skArc(sketch, "E5861", {"start": v(-411.5, 555.69) * mm, "mid": v(-409.38, 556.57) * mm, "end": v(-408.5, 558.69) * mm});
            skArc(sketch, "E5862", {"start": v(-408.5, 558.69) * mm, "mid": v(-409.38, 560.8) * mm, "end": v(-411.5, 561.69) * mm});
            skArc(sketch, "E5863", {"start": v(-581.65, 990.65) * mm, "mid": v(-583.78, 989.77) * mm, "end": v(-584.65, 987.65) * mm});
            skArc(sketch, "E5864", {"start": v(-584.65, 987.65) * mm, "mid": v(-583.78, 985.53) * mm, "end": v(-581.65, 984.65) * mm});
            skArc(sketch, "E5865", {"start": v(-581.65, 984.65) * mm, "mid": v(-579.53, 985.53) * mm, "end": v(-578.65, 987.65) * mm});
            skArc(sketch, "E5866", {"start": v(-578.65, 987.65) * mm, "mid": v(-579.53, 989.77) * mm, "end": v(-581.65, 990.65) * mm});
            skArc(sketch, "E5867", {"start": v(-234.4, 1121.01) * mm, "mid": v(-236.52, 1120.14) * mm, "end": v(-237.4, 1118.01) * mm});
            skArc(sketch, "E5868", {"start": v(-237.4, 1118.01) * mm, "mid": v(-236.52, 1115.9) * mm, "end": v(-234.4, 1115.01) * mm});
            skArc(sketch, "E5869", {"start": v(-234.4, 1115.01) * mm, "mid": v(-232.27, 1115.9) * mm, "end": v(-231.4, 1118.01) * mm});
            skArc(sketch, "E5870", {"start": v(-231.4, 1118.01) * mm, "mid": v(-232.27, 1120.14) * mm, "end": v(-234.4, 1121.01) * mm});
            skArc(sketch, "E5871", {"start": v(87.67, 933.54) * mm, "mid": v(85.55, 932.66) * mm, "end": v(84.67, 930.54) * mm});
            skArc(sketch, "E5872", {"start": v(84.67, 930.54) * mm, "mid": v(85.55, 928.42) * mm, "end": v(87.67, 927.54) * mm});
            skArc(sketch, "E5873", {"start": v(87.67, 927.54) * mm, "mid": v(89.8, 928.42) * mm, "end": v(90.67, 930.54) * mm});
            skArc(sketch, "E5874", {"start": v(90.67, 930.54) * mm, "mid": v(89.8, 932.66) * mm, "end": v(87.67, 933.54) * mm});
            skArc(sketch, "E5875", {"start": v(390.52, 1099.38) * mm, "mid": v(388.4, 1098.5) * mm, "end": v(387.52, 1096.38) * mm});
            skArc(sketch, "E5876", {"start": v(387.52, 1096.38) * mm, "mid": v(388.4, 1094.26) * mm, "end": v(390.52, 1093.38) * mm});
            skArc(sketch, "E5877", {"start": v(390.52, 1093.38) * mm, "mid": v(392.64, 1094.26) * mm, "end": v(393.52, 1096.38) * mm});
            skArc(sketch, "E5878", {"start": v(393.52, 1096.38) * mm, "mid": v(392.64, 1098.5) * mm, "end": v(390.52, 1099.38) * mm});
            skArc(sketch, "E5879", {"start": v(419.58, 773) * mm, "mid": v(417.46, 772.12) * mm, "end": v(416.58, 770) * mm});
            skArc(sketch, "E5880", {"start": v(416.58, 770) * mm, "mid": v(417.46, 767.88) * mm, "end": v(419.58, 767) * mm});
            skArc(sketch, "E5881", {"start": v(419.58, 767) * mm, "mid": v(421.7, 767.88) * mm, "end": v(422.58, 770) * mm});
            skArc(sketch, "E5882", {"start": v(422.58, 770) * mm, "mid": v(421.7, 772.12) * mm, "end": v(419.58, 773) * mm});
            skArc(sketch, "E5883", {"start": v(-266.98, -856.7) * mm, "mid": v(-269.1, -857.59) * mm, "end": v(-269.98, -859.7) * mm});
            skArc(sketch, "E5884", {"start": v(-269.98, -859.7) * mm, "mid": v(-269.1, -861.83) * mm, "end": v(-266.98, -862.7) * mm});
            skArc(sketch, "E5885", {"start": v(-266.98, -862.7) * mm, "mid": v(-264.86, -861.83) * mm, "end": v(-263.98, -859.7) * mm});
            skArc(sketch, "E5886", {"start": v(-263.98, -859.7) * mm, "mid": v(-264.86, -857.59) * mm, "end": v(-266.98, -856.7) * mm});
            skArc(sketch, "E5887", {"start": v(86.03, -827.52) * mm, "mid": v(83.9, -828.4) * mm, "end": v(83.03, -830.52) * mm});
            skArc(sketch, "E5888", {"start": v(83.03, -830.52) * mm, "mid": v(83.9, -832.64) * mm, "end": v(86.03, -833.52) * mm});
            skArc(sketch, "E5889", {"start": v(86.03, -833.52) * mm, "mid": v(88.15, -832.64) * mm, "end": v(89.03, -830.52) * mm});
            skArc(sketch, "E5890", {"start": v(89.03, -830.52) * mm, "mid": v(88.15, -828.4) * mm, "end": v(86.03, -827.52) * mm});
            skArc(sketch, "E5891", {"start": v(417.9, -840.17) * mm, "mid": v(415.78, -841.05) * mm, "end": v(414.9, -843.17) * mm});
            skArc(sketch, "E5892", {"start": v(414.9, -843.17) * mm, "mid": v(415.78, -845.29) * mm, "end": v(417.9, -846.17) * mm});
            skArc(sketch, "E5893", {"start": v(417.9, -846.17) * mm, "mid": v(420.02, -845.29) * mm, "end": v(420.9, -843.17) * mm});
            skArc(sketch, "E5894", {"start": v(420.9, -843.17) * mm, "mid": v(420.02, -841.05) * mm, "end": v(417.9, -840.17) * mm});
            skSolve(sketch);
        }
        {
            var Q0;
            Q0=makeQuery(id+"F0.imprint","IMPRINT",FACE,{"disambiguationData":[TD([[makeQuery(id+"F0.imprint","IMPRINT",EDGE,{"derivedFrom":sQuery(id+"F0.wireOp",EDGE,"E660")}),1.0]])]});
            var Q1;
            Q1=makeQuery(id+"F0.imprint","IMPRINT",FACE,{"disambiguationData":[TD([[makeQuery(id+"F0.imprint","IMPRINT",EDGE,{"derivedFrom":sQuery(id+"F0.wireOp",EDGE,"E4782")}),-1.0]])]});
            var Q2;
            Q2=makeQuery(id+"F0.imprint","IMPRINT",FACE,{"disambiguationData":[TD([[makeQuery(id+"F0.imprint","IMPRINT",EDGE,{"derivedFrom":sQuery(id+"F0.wireOp",EDGE,"E4526")}),-1.0]])]});
            var Q3;
            {var subQ0=sQuery(id+"F0.wireOp",EDGE,"E4412");Q3=makeQuery(id+"F0.imprint","IMPRINT",FACE,{"disambiguationData":[TD([[makeQuery(id+"F0.imprint","IMPRINT",EDGE,{"derivedFrom":subQ0}),-1.0]])]});}
            extrude(context, id + "F1", {"entities" : qUnion([Q0, Q1, Q2, Q3]), "depth" : 18 * mm});
        }
        {
            var Q0;
            Q0=makeQuery(id+"F0.imprint","IMPRINT",FACE,{"disambiguationData":[TD([[makeQuery(id+"F0.imprint","IMPRINT",EDGE,{"derivedFrom":sQuery(id+"F0.wireOp",EDGE,"E4")}),1.0]])]});
            var Q1;
            Q1=makeQuery(id+"F0.imprint","IMPRINT",FACE,{"disambiguationData":[TD([[makeQuery(id+"F0.imprint","IMPRINT",EDGE,{"derivedFrom":sQuery(id+"F0.wireOp",EDGE,"E1193")}),-1.0]])]});
            extrude(context, id + "F2", {"entities" : qUnion([Q0, Q1]), "depth" : 18 * mm});
        }
        {
            var Q0;
            Q0=makeQuery(id+"F0.imprint","IMPRINT",FACE,{"disambiguationData":[TD([[makeQuery(id+"F0.imprint","IMPRINT",EDGE,{"derivedFrom":sQuery(id+"F0.wireOp",EDGE,"E404")}),1.0]])]});
            var Q1;
            Q1=makeQuery(id+"F0.imprint","IMPRINT",FACE,{"disambiguationData":[TD([[makeQuery(id+"F0.imprint","IMPRINT",EDGE,{"derivedFrom":sQuery(id+"F0.wireOp",EDGE,"E3412")}),-1.0]])]});
            var Q2;
            Q2=makeQuery(id+"F0.imprint","IMPRINT",FACE,{"disambiguationData":[TD([[makeQuery(id+"F0.imprint","IMPRINT",EDGE,{"derivedFrom":sQuery(id+"F0.wireOp",EDGE,"E3152")}),-1.0]])]});
            var Q3;
            Q3=makeQuery(id+"F0.imprint","IMPRINT",FACE,{"disambiguationData":[TD([[makeQuery(id+"F0.imprint","IMPRINT",EDGE,{"derivedFrom":sQuery(id+"F0.wireOp",EDGE,"E2896")}),-1.0]])]});
            var Q4;
            {var subQ0=sQuery(id+"F0.wireOp",EDGE,"E2782");Q4=makeQuery(id+"F0.imprint","IMPRINT",FACE,{"disambiguationData":[TD([[makeQuery(id+"F0.imprint","IMPRINT",EDGE,{"derivedFrom":subQ0}),-1.0]])]});}
            extrude(context, id + "F3", {"entities" : qUnion([Q0, Q1, Q2, Q3, Q4]), "depth" : 18 * mm});
        }
        {
            var Q0;
            Q0=makeQuery(id+"F0.imprint","IMPRINT",FACE,{"disambiguationData":[TD([[makeQuery(id+"F0.imprint","IMPRINT",EDGE,{"derivedFrom":sQuery(id+"F0.wireOp",EDGE,"E772")}),1.0]])]});
            var Q1;
            Q1=makeQuery(id+"F0.imprint","IMPRINT",FACE,{"disambiguationData":[TD([[makeQuery(id+"F0.imprint","IMPRINT",EDGE,{"derivedFrom":sQuery(id+"F0.wireOp",EDGE,"E5499")}),-1.0]])]});
            var Q2;
            Q2=makeQuery(id+"F0.imprint","IMPRINT",FACE,{"disambiguationData":[TD([[makeQuery(id+"F0.imprint","IMPRINT",EDGE,{"derivedFrom":sQuery(id+"F0.wireOp",EDGE,"E5367")}),-1.0]])]});
            extrude(context, id + "F4", {"entities" : qUnion([Q0, Q1, Q2]), "depth" : 25 * mm});
        }
    });
